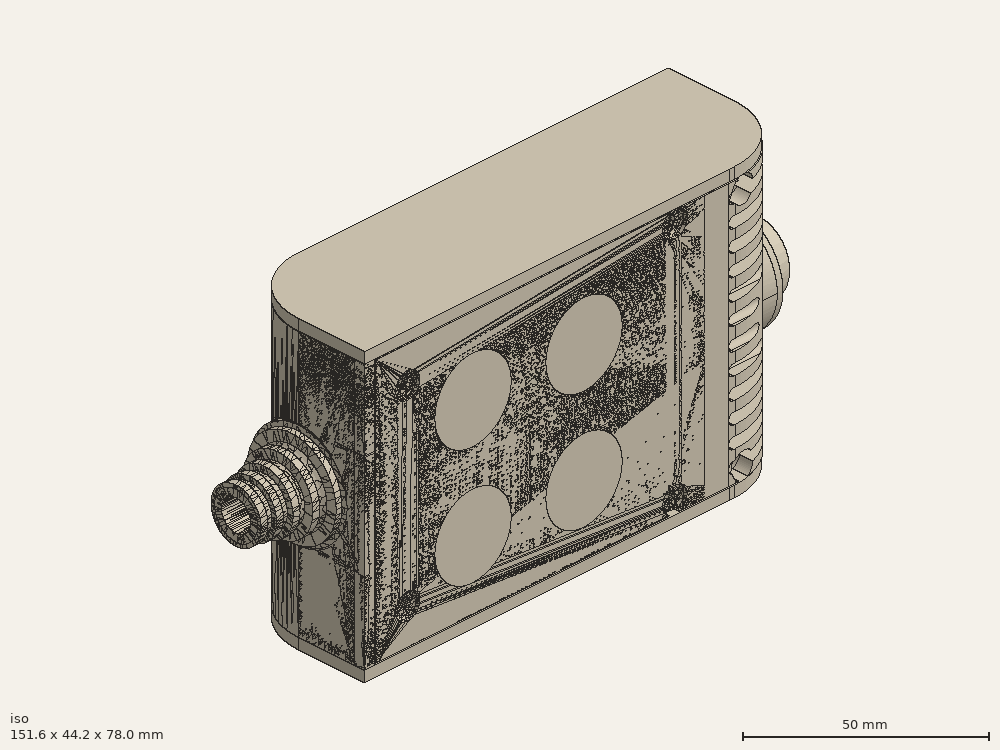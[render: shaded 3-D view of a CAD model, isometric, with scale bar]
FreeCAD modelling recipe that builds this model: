
FCSTD DOCUMENT  (FreeCAD 0.19R0.19.2)
Label: enclosure_183FCStd
License: All rights reserved
LicenseURL: http://en.wikipedia.org/wiki/All_rights_reserved
objects: Part::Revolution×152, Part::MultiFuse×146, Part::Feature×146, Sketcher::SketchObject×84, Part::Cut×70, Part::Cylinder×70, Part::Extrusion×67, Part::Fillet×58, Part::Box×36, App::MeasureDistance×4, PartDesign::Body×2, Image::ImagePlane×1
note: 831 computed .brp shape members not serialized (recipe doc carries the construction recipe); baked Part::Feature solids carry a one-line shape summary decoded from their .brp

FEATURE [Sketcher::SketchObject] Sketch  label="topSketch"
  FullyConstrained = true
  sketch-geometry (20):
    g0: LineSegment StartX=5.21097e-06 StartY=3 StartZ=0 EndX=5.21097e-06 EndY=19 EndZ=0
    g1: ArcOfCircle CenterX=19 CenterY=19 CenterZ=0 NormalX=0 NormalY=0 NormalZ=1 AngleXU=0 Radius=19 StartAngle=1.5708 EndAngle=3.14159
    g2: ArcOfCircle CenterX=19 CenterY=19 CenterZ=0 NormalX=0 NormalY=0 NormalZ=1 AngleXU=0 Radius=16 StartAngle=1.5708 EndAngle=3.14159
    g3: LineSegment StartX=114 StartY=35 StartZ=0 EndX=19 EndY=35 EndZ=0
    g4: LineSegment StartX=5.21097e-06 StartY=3 StartZ=0 EndX=5.21097e-06 EndY=0 EndZ=0
    g5: LineSegment StartX=3 StartY=0 StartZ=0 EndX=5.21097e-06 EndY=0 EndZ=0
    g6: LineSegment StartX=3 StartY=19 StartZ=0 EndX=3 EndY=0 EndZ=0
    g7: LineSegment StartX=19 StartY=38 StartZ=0 EndX=124 EndY=38 EndZ=0
    g8: Circle CenterX=119 CenterY=35 CenterZ=0 NormalX=0 NormalY=0 NormalZ=1 AngleXU=0 Radius=1
    g9: Circle CenterX=121 CenterY=35 CenterZ=0 NormalX=0 NormalY=0 NormalZ=1 AngleXU=0 Radius=1
    g10: Circle CenterX=121 CenterY=33 CenterZ=0 NormalX=0 NormalY=0 NormalZ=1 AngleXU=0 Radius=1
    g11: BSplineCurve PolesCount=3 KnotsCount=2 Degree=2 IsPeriodic=0
    g12: GeomPoint X=119 Y=35 Z=0
    g13: GeomPoint X=121 Y=33 Z=0
    g14: LineSegment StartX=119 StartY=35 StartZ=0 EndX=114 EndY=35 EndZ=0
    g15: ArcOfCircle CenterX=105 CenterY=19 CenterZ=0 NormalX=0 NormalY=0 NormalZ=1 AngleXU=0 Radius=19 StartAngle=5.7297 EndAngle=6.28319
    g16: ArcOfCircle CenterX=105 CenterY=19 CenterZ=0 NormalX=0 NormalY=0 NormalZ=1 AngleXU=0 Radius=16 StartAngle=5.60905 EndAngle=6.28319
    g17: LineSegment StartX=121 StartY=33 StartZ=0 EndX=121 EndY=19 EndZ=0
    g18: LineSegment StartX=124 StartY=38 StartZ=0 EndX=124 EndY=19 EndZ=0
    g19: LineSegment StartX=117.5 StartY=9.01251 StartZ=0 EndX=121.163 EndY=9.0125 EndZ=0
  constraints (46):
    c: Vertical(g0)
    c: Block(g0)
    c: Coincident(g1,g0)
    c: Block(g1)
    c: Coincident(g2,g1)
    c: Block(g2)
    c: Coincident(g3,g2)
    c: Horizontal(g3)
    c: Tangent(g3,g2)
    c: Coincident(g4,g0)
    c: Distance(g4) = 3
    c: Vertical(g4)
    c: Coincident(g5,g4)
    c: Horizontal(g5)
    c: Coincident(g6,g2)
    c: Coincident(g6,g5)
    c: Vertical(g6)
    c: Horizontal(g7)
    c: Distance(g7) = 105
    c: Coincident(g7,g1)
    c: Block(g3)
    c: Weight(g8) = 1
    c: Equal(g8,g9)
    c: Equal(g8,g10)
    c: InternalAlignment(g8,g11)
    c: InternalAlignment(g9,g11)
    c: InternalAlignment(g10,g11)
    c: InternalAlignment(g12,g11)
    c: InternalAlignment(g13,g11)
    c: Block(g11)
    c: Coincident(g14,g11)
    c: Coincident(g14,g3)
    c: Horizontal(g14)
    c: Block(g15)
    c: Coincident(g16,g15)
    c: Block(g16)
    c: Coincident(g17,g11)
    c: Coincident(g17,g16)
    c: Vertical(g17)
    c: Distance(g17) = 14
    c: Coincident(g18,g7)
    c: Coincident(g18,g15)
    c: Vertical(g18)
    c: Distance(g18) = 19
    c: Coincident(g19,g16)
    c: Coincident(g19,g15)
FEATURE [Sketcher::SketchObject] Sketch001  label="bottomSketch"
  FullyConstrained = true
  sketch-geometry (32):
    g0: LineSegment StartX=3.3 StartY=-6.03275e-07 StartZ=0 EndX=98 EndY=-6.03275e-07 EndZ=0
    g1: ArcOfCircle CenterX=98 CenterY=19 CenterZ=0 NormalX=0 NormalY=0 NormalZ=1 AngleXU=0 Radius=19 StartAngle=4.71239 EndAngle=5.71103
    g2: LineSegment StartX=6.3 StartY=8 StartZ=0 EndX=3.3 EndY=8 EndZ=0
    g3: LineSegment StartX=3.3 StartY=8 StartZ=0 EndX=3.3 EndY=-6.03275e-07 EndZ=0
    g4: ArcOfCircle CenterX=8.3 CenterY=5 CenterZ=0 NormalX=0 NormalY=0 NormalZ=1 AngleXU=0 Radius=2 StartAngle=3.14159 EndAngle=4.71239
    g5: LineSegment StartX=6.3 StartY=8 StartZ=0 EndX=6.3 EndY=5 EndZ=0
    g6: ArcOfCircle CenterX=98 CenterY=19 CenterZ=0 NormalX=0 NormalY=0 NormalZ=1 AngleXU=0 Radius=12.7 StartAngle=4.71239 EndAngle=6.28319
    g7: LineSegment StartX=94.7 StartY=3 StartZ=0 EndX=8.3 EndY=3 EndZ=0
    g8-g12: Circle x5 (B-spline internal-alignment scaffolding for g13; pole/knot coordinates omitted)
    g13: BSplineCurve PolesCount=5 KnotsCount=3 Degree=3 IsPeriodic=0
    g14: GeomPoint X=98 Y=6.3 Z=0
    g15: GeomPoint X=96.3938 Y=4.71946 Z=0
    g16: GeomPoint X=94.7 Y=3 Z=0
    g17-g23: Circle x7 (B-spline internal-alignment scaffolding for g24; pole/knot coordinates omitted)
    g24: BSplineCurve PolesCount=7 KnotsCount=5 Degree=3 IsPeriodic=0
    g25-g29: GeomPoint x5 (B-spline internal-alignment scaffolding for g24; pole/knot coordinates omitted)
    g30: ArcOfCircle CenterX=98 CenterY=19 CenterZ=0 NormalX=0 NormalY=0 NormalZ=1 AngleXU=0 Radius=15.7 StartAngle=5.81226 EndAngle=6.28319
    g31: LineSegment StartX=110.7 StartY=19 StartZ=0 EndX=113.7 EndY=19 EndZ=0
  constraints (41):
    c: Horizontal(g0)
    c: Coincident(g1,g0)
    c: Block(g1)
    c: Horizontal(g2)
    c: Distance(g2) = 3
    c: Coincident(g3,g2)
    c: Vertical(g3)
    c: Coincident(g3,g0)
    c: Block(g4)
    c: Block(g2)
    c: Coincident(g5,g2)
    c: Coincident(g5,g4)
    c: Vertical(g5)
    c: Coincident(g6,g1)
    c: Block(g6)
    c: Coincident(g7,g4)
    c: Horizontal(g7)
    c: Block(g0)
    c: Block(g7)
    c: Block(g3)
    c: Coincident(g13,g6)
    c: Weight(g8) = 1
    c: Equal(g8, g9-g12) x4
    c: Coincident(g13,g7)
    c: InternalAlignment(g8-g12 -> g13) x5
    c: InternalAlignment(g14,g13)
    c: InternalAlignment(g15,g13)
    c: InternalAlignment(g16,g13)
    c: Block(g13)
    c: Weight(g17) = 1
    c: Equal(g17, g18-g23) x6
    c: Coincident(g24,g1)
    c: InternalAlignment(g17-g23 -> g24) x7
    c: InternalAlignment(g25-g29 -> g24) x5
    c: Block(g24)
    c: Coincident(g30,g24)
    c: Coincident(g31,g6)
    c: Coincident(g31,g30)
    c: Horizontal(g31)
    c: Block(g31)
    c: Block(g30)
FEATURE [Part::Extrusion] Extrude  label="top"
  Base = -> Sketch
  Dir = (0,0,1)
  DirMode = 2
  FaceMakerClass = Part::FaceMakerBullseye
  LengthFwd = 72
  LengthRev = 0
  Solid = true
  Symmetric = false
FEATURE [Part::Extrusion] Extrude001  label="bottom"
  Base = -> Sketch001
  Dir = (0,0,1)
  DirMode = 2
  FaceMakerClass = Part::FaceMakerBullseye
  LengthFwd = 71.4
  LengthRev = 0
  Placement = pos=(0,0,0.3) rot=(0,0,1;0rad)
  Solid = true
  Symmetric = false
FEATURE [Sketcher::SketchObject] Sketch002  label="topSketch001"
  FullyConstrained = true
  sketch-geometry (8):
    g0: ArcOfCircle CenterX=19 CenterY=19.0975 CenterZ=0 NormalX=0 NormalY=0 NormalZ=1 AngleXU=0 Radius=18.9025 StartAngle=1.5708 EndAngle=3.14674
    g1: LineSegment StartX=0.0977805 StartY=19.0003 StartZ=0 EndX=0.0977805 EndY=0.000251602 EndZ=0
    g2: LineSegment StartX=19 StartY=38 StartZ=0 EndX=124 EndY=38 EndZ=0
    g3: LineSegment StartX=0.0977805 StartY=0.000251602 StartZ=0 EndX=105.098 EndY=0.000251602 EndZ=0
    g4: LineSegment StartX=124 StartY=38 StartZ=0 EndX=125.616 EndY=38 EndZ=0
    g5: LineSegment StartX=105.098 StartY=0.000251602 StartZ=0 EndX=106.713 EndY=0.000251602 EndZ=0
    g6: ArcOfCircle CenterX=106.616 CenterY=19 CenterZ=0 NormalX=0 NormalY=0 NormalZ=1 AngleXU=0 Radius=19 StartAngle=4.71754 EndAngle=6.28319
    g7: LineSegment StartX=125.616 StartY=38 StartZ=0 EndX=125.616 EndY=19 EndZ=0
  constraints (21):
    c: Block(g0)
    c: Coincident(g1,g0)
    c: Vertical(g1)
    c: Horizontal(g2)
    c: Distance(g2) = 105
    c: Coincident(g2,g0)
    c: Distance(g1) = 19
    c: Coincident(g3,g1)
    c: Horizontal(g3)
    c: Distance(g3) = 105
    c: Coincident(g4,g2)
    c: Horizontal(g4)
    c: Distance(g4) = 1.61553
    c: Horizontal(g5)
    c: Equal(g4,g5) = 1.61553
    c: Coincident(g5,g3)
    c: Block(g6)
    c: Coincident(g6,g5)
    c: Coincident(g7,g4)
    c: Coincident(g7,g6)
    c: Vertical(g7)
FEATURE [Part::Extrusion] Extrude002  label="sideA"
  Base = -> Sketch002
  Dir = (0,0,1)
  DirMode = 2
  FaceMakerClass = Part::FaceMakerBullseye
  LengthFwd = 3
  LengthRev = 0
  Placement = pos=(0,0,-3) rot=(0,0,1;0rad)
  Solid = true
  Symmetric = false
FEATURE [Sketcher::SketchObject] Sketch003  label="topSketch002"
  FullyConstrained = true
  sketch-geometry (6):
    g0: LineSegment StartX=19 StartY=38 StartZ=0 EndX=117 EndY=38 EndZ=0
    g1: ArcOfCircle CenterX=19 CenterY=19 CenterZ=0 NormalX=0 NormalY=0 NormalZ=1 AngleXU=0 Radius=19 StartAngle=1.5708 EndAngle=3.14159
    g2: LineSegment StartX=117 StartY=38 StartZ=0 EndX=117 EndY=19 EndZ=0
    g3: LineSegment StartX=98 StartY=1.0161e-12 StartZ=0 EndX=5.22862e-06 EndY=1.0161e-12 EndZ=0
    g4: LineSegment StartX=5.22862e-06 StartY=19 StartZ=0 EndX=5.22862e-06 EndY=1.0161e-12 EndZ=0
    g5: ArcOfCircle CenterX=98 CenterY=19 CenterZ=0 NormalX=0 NormalY=0 NormalZ=1 AngleXU=0 Radius=19 StartAngle=4.71239 EndAngle=6.28319
  constraints (16):
    c: Horizontal(g0)
    c: Distance(g0) = 98
    c: Coincident(g1,g0)
    c: Block(g1)
    c: Coincident(g2,g0)
    c: Vertical(g2)
    c: Distance(g2) = 19
    c: Horizontal(g3)
    c: Coincident(g4,g1)
    c: Vertical(g4)
    c: Coincident(g3,g4)
    c: Block(g3)
    c: Coincident(g5,g2)
    c: Coincident(g5,g3)
    c: Block(g0)
    c: Block(g5)
FEATURE [Sketcher::SketchObject] Sketch004
  FullyConstrained = true
  MapMode = 3
  Placement = pos=(0,0,0) rot=(1,0,0;1.5708rad)
  Support = -> [Extrude]
  sketch-geometry (8):
    g0: Circle CenterX=80.351 CenterY=-67.6202 CenterZ=0 NormalX=0 NormalY=0 NormalZ=1 AngleXU=0 Radius=2
    g1: Circle CenterX=80.351 CenterY=-67.6202 CenterZ=0 NormalX=0 NormalY=0 NormalZ=1 AngleXU=0 Radius=3
    g2: Circle CenterX=80.351 CenterY=-4.92017 CenterZ=0 NormalX=0 NormalY=0 NormalZ=1 AngleXU=0 Radius=2
    g3: Circle CenterX=80.351 CenterY=-4.92017 CenterZ=0 NormalX=0 NormalY=0 NormalZ=1 AngleXU=0 Radius=3
    g4: Circle CenterX=23.851 CenterY=-4.92017 CenterZ=0 NormalX=0 NormalY=0 NormalZ=1 AngleXU=0 Radius=2
    g5: Circle CenterX=23.851 CenterY=-4.92017 CenterZ=0 NormalX=0 NormalY=0 NormalZ=1 AngleXU=0 Radius=3
    g6: Circle CenterX=23.851 CenterY=-67.6202 CenterZ=0 NormalX=0 NormalY=0 NormalZ=1 AngleXU=0 Radius=2
    g7: Circle CenterX=23.851 CenterY=-67.6202 CenterZ=0 NormalX=0 NormalY=0 NormalZ=1 AngleXU=0 Radius=3
  constraints (8):
    c: Block(g3)
    c: Block(g2)
    c: Block(g1)
    c: Block(g0)
    c: Block(g6)
    c: Block(g7)
    c: Block(g4)
    c: Block(g5)
FEATURE [Part::Extrusion] Extrude004
  Base = -> Sketch004
  Dir = (0,-1,2e-16)
  DirMode = 2
  FaceMakerClass = Part::FaceMakerBullseye
  LengthFwd = 6
  LengthRev = 0
  Placement = pos=(0,9,0) rot=(0,0,1;0rad)
  Solid = true
  Symmetric = false
FEATURE [Sketcher::SketchObject] Sketch005
  FullyConstrained = true
  MapMode = 3
  Placement = pos=(0,0,0) rot=(1,0,0;1.5708rad)
  Support = -> [Extrude]
  sketch-geometry (8):
    g0: Circle CenterX=80.351 CenterY=-67.6202 CenterZ=0 NormalX=0 NormalY=0 NormalZ=1 AngleXU=0 Radius=3
    g1: Circle CenterX=80.351 CenterY=-4.92017 CenterZ=0 NormalX=0 NormalY=0 NormalZ=1 AngleXU=0 Radius=3
    g2: Circle CenterX=23.851 CenterY=-4.92017 CenterZ=0 NormalX=0 NormalY=0 NormalZ=1 AngleXU=0 Radius=3
    g3: Circle CenterX=23.851 CenterY=-67.6202 CenterZ=0 NormalX=0 NormalY=0 NormalZ=1 AngleXU=0 Radius=3
    g4: Circle CenterX=23.851 CenterY=-67.6202 CenterZ=0 NormalX=0 NormalY=0 NormalZ=1 AngleXU=0 Radius=5
    g5: Circle CenterX=80.351 CenterY=-67.6202 CenterZ=0 NormalX=0 NormalY=0 NormalZ=1 AngleXU=0 Radius=5
    g6: Circle CenterX=23.851 CenterY=-4.92017 CenterZ=0 NormalX=0 NormalY=0 NormalZ=1 AngleXU=0 Radius=5
    g7: Circle CenterX=80.351 CenterY=-4.92017 CenterZ=0 NormalX=0 NormalY=0 NormalZ=1 AngleXU=0 Radius=5
  constraints (8):
    c: Block(g1)
    c: Block(g0)
    c: Block(g3)
    c: Block(g2)
    c: Block(g5)
    c: Block(g4)
    c: Block(g6)
    c: Block(g7)
FEATURE [Part::Extrusion] Extrude005
  Base = -> Sketch005
  Dir = (0,-1,2e-16)
  DirMode = 2
  FaceMakerClass = Part::FaceMakerBullseye
  LengthFwd = 2
  LengthRev = 0
  Solid = true
  Symmetric = false
FEATURE [Sketcher::SketchObject] Sketch006
  FullyConstrained = true
  MapMode = 3
  Placement = pos=(0,0,0) rot=(1,0,0;1.5708rad)
  sketch-geometry (8):
    g0: Circle CenterX=80.351 CenterY=-67.6202 CenterZ=0 NormalX=0 NormalY=0 NormalZ=1 AngleXU=0 Radius=3
    g1: Circle CenterX=80.351 CenterY=-4.92017 CenterZ=0 NormalX=0 NormalY=0 NormalZ=1 AngleXU=0 Radius=3
    g2: Circle CenterX=23.851 CenterY=-4.92017 CenterZ=0 NormalX=0 NormalY=0 NormalZ=1 AngleXU=0 Radius=3
    g3: Circle CenterX=23.851 CenterY=-67.6202 CenterZ=0 NormalX=0 NormalY=0 NormalZ=1 AngleXU=0 Radius=3
    g4: Circle CenterX=23.851 CenterY=-67.6202 CenterZ=0 NormalX=0 NormalY=0 NormalZ=1 AngleXU=0 Radius=5
    g5: Circle CenterX=80.351 CenterY=-67.6202 CenterZ=0 NormalX=0 NormalY=0 NormalZ=1 AngleXU=0 Radius=5
    g6: Circle CenterX=23.851 CenterY=-4.92017 CenterZ=0 NormalX=0 NormalY=0 NormalZ=1 AngleXU=0 Radius=5
    g7: Circle CenterX=80.351 CenterY=-4.92017 CenterZ=0 NormalX=0 NormalY=0 NormalZ=1 AngleXU=0 Radius=5
  constraints (8):
    c: Block(g1)
    c: Block(g0)
    c: Block(g3)
    c: Block(g2)
    c: Block(g5)
    c: Block(g4)
    c: Block(g6)
    c: Block(g7)
FEATURE [Part::Extrusion] Extrude007
  Base = -> Sketch006
  Dir = (0,-1,2e-16)
  DirMode = 2
  FaceMakerClass = Part::FaceMakerBullseye
  LengthFwd = 2
  LengthRev = 0
  Solid = true
  Symmetric = false
FEATURE [Part::Fillet] Fillet
  Base = -> Extrude007
  Edges = 4 edges r=1.99: [Edge6,Edge12,Edge18,Edge24]
FEATURE [Part::Cut] Cut
  Base = -> Extrude005
  Placement = pos=(0,5,0) rot=(0,0,1;0rad)
  Tool = -> Fillet
FEATURE [Part::MultiFuse] Fusion  label="pCBScrews"
  Placement = pos=(-2.5,0,72.3) rot=(0,0,1;0rad)
  Shapes = -> [Extrude004,Cut]
FEATURE [App::MeasureDistance] Distance  label="Distance: 0.69 mm"
  Distance = 0.685967
  P1 = (24.0138,2.9647,0.3)
  P2 = (23.8901,3,-0.373787)
FEATURE [App::MeasureDistance] Distance001  label="Distance: 0.53 mm"
  Distance = 0.533607
  P1 = (80.2939,3,72.2334)
  P2 = (80.281,2.99661,71.7)
FEATURE [Part::Fillet] Fillet001
  Base = -> Extrude001
  Edges = 1 edges r=2.4: [Edge17]
FEATURE [Part::Fillet] Fillet002  label="bottom001"
  Base = -> Fillet001
  Edges = 1 edges r=2.4: [Edge36]
FEATURE [Part::Fillet] Fillet003  label="top001"
  Base = -> Extrude
  Edges = 1 edges r=2: [Edge1]
FEATURE [Sketcher::SketchObject] Sketch007
  FullyConstrained = true
  sketch-geometry (16):
    g0: LineSegment StartX=4 StartY=0 StartZ=0 EndX=4 EndY=2.4 EndZ=0
    g1: LineSegment StartX=4 StartY=2.4 StartZ=0 EndX=7 EndY=2.4 EndZ=0
    g2: LineSegment StartX=4 StartY=0 StartZ=0 EndX=5.7 EndY=0 EndZ=0
    g3: LineSegment StartX=5.7 StartY=0 StartZ=0 EndX=5.7 EndY=-5.6 EndZ=0
    g4-g8: Circle x5 (B-spline internal-alignment scaffolding for g9; pole/knot coordinates omitted)
    g9: BSplineCurve PolesCount=5 KnotsCount=3 Degree=3 IsPeriodic=0
    g10: GeomPoint X=7 Y=2.4 Z=0
    g11: GeomPoint X=10.4582 Y=-1.55472 Z=0
    g12: GeomPoint X=14 Y=-5.6 Z=0
    g13: LineSegment StartX=14 StartY=-5.6 StartZ=0 EndX=14 EndY=-14.1 EndZ=0
    g14: LineSegment StartX=14 StartY=-14.1 StartZ=0 EndX=6.5 EndY=-14.1 EndZ=0
    g15: LineSegment StartX=5.7 StartY=-5.6 StartZ=0 EndX=6.5 EndY=-14.1 EndZ=0
  constraints (28):
    c: Distance(g0) = 2.4
    c: Vertical(g0)
    c: Block(g0)
    c: Coincident(g1,g0)
    c: Horizontal(g1)
    c: Distance(g1) = 3
    c: Coincident(g2,g0)
    c: Horizontal(g2)
    c: Distance(g2) = 1.7
    c: Coincident(g3,g2)
    c: Vertical(g3)
    c: Distance(g3) = 5.6
    c: Coincident(g9,g1)
    c: Weight(g4) = 1
    c: Equal(g4, g5-g8) x4
    c: InternalAlignment(g4-g8 -> g9) x5
    c: InternalAlignment(g10,g9)
    c: InternalAlignment(g11,g9)
    c: InternalAlignment(g12,g9)
    c: Block(g9)
    c: Coincident(g13,g9)
    c: Vertical(g13)
    c: Distance(g13) = 8.5
    c: Coincident(g14,g13)
    c: Horizontal(g14)
    c: Distance(g14) = 7.5
    c: Coincident(g15,g3)
    c: Coincident(g15,g14)
FEATURE [Part::Feature] Face
  shape: bbox 10 x 16.5 x 2e-07 mm, 1 faces, 0 solids (baked)
FEATURE [Part::Revolution] Revolve  label="plugHousing"
  Angle = 360
  Axis = (0,1,0)
  Base = (0,0,0)
  FaceMakerClass = Part::FaceMakerBullseye
  Placement = pos=(0,0,36.15) rot=(0,0,1;0rad)
  Solid = false
  Source = -> Face
  Symmetric = false
FEATURE [Part::Feature] Face001
  shape: bbox 10 x 16.5 x 2e-07 mm, 1 faces, 0 solids (baked)
FEATURE [Part::Revolution] Revolve001  label="plugHousing001"
  Angle = 360
  Axis = (0,1,0)
  Base = (0,0,0)
  FaceMakerClass = Part::FaceMakerBullseye
  Placement = pos=(0,0,36.15) rot=(0,0,1;0rad)
  Solid = false
  Source = -> Face001
  Symmetric = false
FEATURE [Part::MultiFuse] Fusion001  label="plugHousing002"
  Placement = pos=(0,0,0) rot=(0,0,1;1.5708rad)
  Shapes = -> [Revolve001,Revolve]
FEATURE [Part::Feature] Face002
  shape: bbox 10 x 16.5 x 2e-07 mm, 1 faces, 0 solids (baked)
FEATURE [Part::Revolution] Revolve003  label="plugHousing005"
  Angle = 360
  Axis = (0,1,0)
  Base = (0,0,0)
  FaceMakerClass = Part::FaceMakerBullseye
  Placement = pos=(0,0,36.15) rot=(0,0,1;0rad)
  Solid = false
  Source = -> Face002
  Symmetric = false
FEATURE [Part::Feature] Face003
  shape: bbox 10 x 16.5 x 2e-07 mm, 1 faces, 0 solids (baked)
FEATURE [Part::Revolution] Revolve002  label="plugHousing003"
  Angle = 360
  Axis = (0,1,0)
  Base = (0,0,0)
  FaceMakerClass = Part::FaceMakerBullseye
  Placement = pos=(0,0,36.15) rot=(0,0,1;0rad)
  Solid = false
  Source = -> Face003
  Symmetric = false
FEATURE [Part::MultiFuse] Fusion002  label="plugHousing004"
  Placement = pos=(0,0,0) rot=(0,0,1;1.5708rad)
  Shapes = -> [Revolve002,Revolve003]
FEATURE [Part::MultiFuse] Fusion003  label="plugHousing006"
  Placement = pos=(0,19,0) rot=(0,0,1;3.14159rad)
  Shapes = -> [Fusion002,Fusion001]
FEATURE [Part::Feature] Face004
  shape: bbox 10 x 16.5 x 2e-07 mm, 1 faces, 0 solids (baked)
FEATURE [Part::Revolution] Revolve006  label="plugHousing010"
  Angle = 360
  Axis = (0,1,0)
  Base = (0,0,0)
  FaceMakerClass = Part::FaceMakerBullseye
  Placement = pos=(0,0,36.15) rot=(0,0,1;0rad)
  Solid = false
  Source = -> Face004
  Symmetric = false
FEATURE [Part::Feature] Face005
  shape: bbox 10 x 16.5 x 2e-07 mm, 1 faces, 0 solids (baked)
FEATURE [Part::Revolution] Revolve007  label="plugHousing011"
  Angle = 360
  Axis = (0,1,0)
  Base = (0,0,0)
  FaceMakerClass = Part::FaceMakerBullseye
  Placement = pos=(0,0,36.15) rot=(0,0,1;0rad)
  Solid = false
  Source = -> Face005
  Symmetric = false
FEATURE [Part::Feature] Face006
  shape: bbox 10 x 16.5 x 2e-07 mm, 1 faces, 0 solids (baked)
FEATURE [Part::Revolution] Revolve004  label="plugHousing007"
  Angle = 360
  Axis = (0,1,0)
  Base = (0,0,0)
  FaceMakerClass = Part::FaceMakerBullseye
  Placement = pos=(0,0,36.15) rot=(0,0,1;0rad)
  Solid = false
  Source = -> Face006
  Symmetric = false
FEATURE [Part::MultiFuse] Fusion004  label="plugHousing009"
  Placement = pos=(0,0,0) rot=(0,0,1;1.5708rad)
  Shapes = -> [Revolve004,Revolve007]
FEATURE [Part::Feature] Face007
  shape: bbox 10 x 16.5 x 2e-07 mm, 1 faces, 0 solids (baked)
FEATURE [Part::Revolution] Revolve005  label="plugHousing008"
  Angle = 360
  Axis = (0,1,0)
  Base = (0,0,0)
  FaceMakerClass = Part::FaceMakerBullseye
  Placement = pos=(0,0,36.15) rot=(0,0,1;0rad)
  Solid = false
  Source = -> Face007
  Symmetric = false
FEATURE [Part::MultiFuse] Fusion005  label="plugHousing012"
  Placement = pos=(0,0,0) rot=(0,0,1;1.5708rad)
  Shapes = -> [Revolve006,Revolve005]
FEATURE [Part::MultiFuse] Fusion006  label="plugHousing013"
  Placement = pos=(0,19,0) rot=(0,0,1;3.14159rad)
  Shapes = -> [Fusion005,Fusion004]
FEATURE [Part::MultiFuse] Fusion007  label="plugHousing014"
  Placement = pos=(122.621,0,-0.15) rot=(0,0,1;0rad)
  Shapes = -> [Fusion003,Fusion006]
FEATURE [Part::Cylinder] Cylinder002
  Angle = 360
  AttacherType = Attacher::AttachEngine3D
  Height = 20
  Placement = pos=(0,0,36.15) rot=(0,0,1;0rad)
  Radius = 4
FEATURE [Part::Cylinder] Cylinder003
  Angle = 360
  AttacherType = Attacher::AttachEngine3D
  Height = 10
  Placement = pos=(0,0,36.15) rot=(0,0,1;0rad)
  Radius = 4
FEATURE [Part::MultiFuse] Fusion009  label="removeToCreateHoleForPlugHousing"
  Placement = pos=(70,19,36.15) rot=(0,1,0;1.5708rad)
  Shapes = -> [Cylinder002,Cylinder003]
FEATURE [Part::Cylinder] Cylinder004
  Angle = 360
  AttacherType = Attacher::AttachEngine3D
  Height = 20
  Placement = pos=(0,0,36.15) rot=(0,0,1;0rad)
  Radius = 4
FEATURE [Part::Cylinder] Cylinder005
  Angle = 360
  AttacherType = Attacher::AttachEngine3D
  Height = 10
  Placement = pos=(0,0,36.15) rot=(0,0,1;0rad)
  Radius = 4
FEATURE [Part::MultiFuse] Fusion010  label="removeToCreateHoleForPlugHousing001"
  Placement = pos=(70,19,36.15) rot=(0,1,0;1.5708rad)
  Shapes = -> [Cylinder004,Cylinder005]
FEATURE [Part::Cut] Cut001
  Base = -> Fillet003
  Tool = -> Fusion010
FEATURE [Part::Cut] Cut002  label="Bottom"
  Base = -> Fillet002
  Tool = -> Fusion009
FEATURE [Part::Feature] Face008
  shape: bbox 10 x 16.5 x 2e-07 mm, 1 faces, 0 solids (baked)
FEATURE [Part::Revolution] Revolve011  label="plugHousing021"
  Angle = 360
  Axis = (0,1,0)
  Base = (0,0,0)
  FaceMakerClass = Part::FaceMakerBullseye
  Placement = pos=(0,0,36.15) rot=(0,0,1;0rad)
  Solid = false
  Source = -> Face008
  Symmetric = false
FEATURE [Part::Feature] Face009
  shape: bbox 10 x 16.5 x 2e-07 mm, 1 faces, 0 solids (baked)
FEATURE [Part::Revolution] Revolve012  label="plugHousing022"
  Angle = 360
  Axis = (0,1,0)
  Base = (0,0,0)
  FaceMakerClass = Part::FaceMakerBullseye
  Placement = pos=(0,0,36.15) rot=(0,0,1;0rad)
  Solid = false
  Source = -> Face009
  Symmetric = false
FEATURE [Part::Feature] Face010 .. Face013  x4 (patterned run collapsed; names and placements below)
  shape: bbox 10 x 16.5 x 2e-07 mm, 1 faces, 0 solids (baked)
FEATURE [Part::Revolution] Revolve015  label="plugHousing027"
  Angle = 360
  Axis = (0,1,0)
  Base = (0,0,0)
  FaceMakerClass = Part::FaceMakerBullseye
  Placement = pos=(0,0,36.15) rot=(0,0,1;0rad)
  Solid = false
  Source = -> Face013
  Symmetric = false
FEATURE [Part::Feature] Face014
  shape: bbox 10 x 16.5 x 2e-07 mm, 1 faces, 0 solids (baked)
FEATURE [Part::Feature] Face015
  shape: bbox 10 x 16.5 x 2e-07 mm, 1 faces, 0 solids (baked)
FEATURE [Part::Feature] Face016
  shape: bbox 10 x 16.5 x 2e-07 mm, 1 faces, 0 solids (baked)
FEATURE [Part::Revolution] Revolve019  label="plugHousing033"
  Angle = 360
  Axis = (0,1,0)
  Base = (0,0,0)
  FaceMakerClass = Part::FaceMakerBullseye
  Placement = pos=(0,0,36.15) rot=(0,0,1;0rad)
  Solid = false
  Source = -> Face016
  Symmetric = false
FEATURE [Part::Feature] Face017
  shape: bbox 10 x 16.5 x 2e-07 mm, 1 faces, 0 solids (baked)
FEATURE [Part::Revolution] Revolve020  label="plugHousing034"
  Angle = 360
  Axis = (0,1,0)
  Base = (0,0,0)
  FaceMakerClass = Part::FaceMakerBullseye
  Placement = pos=(0,0,36.15) rot=(0,0,1;0rad)
  Solid = false
  Source = -> Face017
  Symmetric = false
FEATURE [Part::Feature] Face018
  shape: bbox 10 x 16.5 x 2e-07 mm, 1 faces, 0 solids (baked)
FEATURE [Part::Revolution] Revolve016  label="plugHousing030"
  Angle = 360
  Axis = (0,1,0)
  Base = (0,0,0)
  FaceMakerClass = Part::FaceMakerBullseye
  Placement = pos=(0,0,36.15) rot=(0,0,1;0rad)
  Solid = false
  Source = -> Face018
  Symmetric = false
FEATURE [Part::MultiFuse] Fusion020  label="plugHousing038"
  Placement = pos=(0,0,0) rot=(0,0,1;1.5708rad)
  Shapes = -> [Revolve016,Revolve020]
FEATURE [Part::Feature] Face019
  shape: bbox 10 x 16.5 x 2e-07 mm, 1 faces, 0 solids (baked)
FEATURE [Part::Feature] Face020
  shape: bbox 10 x 16.5 x 2e-07 mm, 1 faces, 0 solids (baked)
FEATURE [Part::Revolution] Revolve017  label="plugHousing031"
  Angle = 360
  Axis = (0,1,0)
  Base = (0,0,0)
  FaceMakerClass = Part::FaceMakerBullseye
  Placement = pos=(0,0,36.15) rot=(0,0,1;0rad)
  Solid = false
  Source = -> Face020
  Symmetric = false
FEATURE [Part::MultiFuse] Fusion021  label="plugHousing039"
  Placement = pos=(0,0,0) rot=(0,0,1;1.5708rad)
  Shapes = -> [Revolve019,Revolve017]
FEATURE [Part::MultiFuse] Fusion023  label="plugHousing041"
  Placement = pos=(0,19,0) rot=(0,0,1;3.14159rad)
  Shapes = -> [Fusion021,Fusion020]
FEATURE [Part::Revolution] Revolve022  label="plugHousing043"
  Angle = 360
  Axis = (0,1,0)
  Base = (0,0,0)
  FaceMakerClass = Part::FaceMakerBullseye
  Placement = pos=(0,0,36.15) rot=(0,0,1;0rad)
  Solid = false
  Source = -> Face019
  Symmetric = false
FEATURE [Part::Feature] Face021
  shape: bbox 10 x 16.5 x 2e-07 mm, 1 faces, 0 solids (baked)
FEATURE [Part::Revolution] Revolve023  label="plugHousing044"
  Angle = 360
  Axis = (0,1,0)
  Base = (0,0,0)
  FaceMakerClass = Part::FaceMakerBullseye
  Placement = pos=(0,0,36.15) rot=(0,0,1;0rad)
  Solid = false
  Source = -> Face021
  Symmetric = false
FEATURE [Part::Feature] Face022
  shape: bbox 10 x 16.5 x 2e-07 mm, 1 faces, 0 solids (baked)
FEATURE [Part::Revolution] Revolve018  label="plugHousing032"
  Angle = 360
  Axis = (0,1,0)
  Base = (0,0,0)
  FaceMakerClass = Part::FaceMakerBullseye
  Placement = pos=(0,0,36.15) rot=(0,0,1;0rad)
  Solid = false
  Source = -> Face022
  Symmetric = false
FEATURE [Part::MultiFuse] Fusion022  label="plugHousing040"
  Placement = pos=(0,0,0) rot=(0,0,1;1.5708rad)
  Shapes = -> [Revolve018,Revolve023]
FEATURE [Part::Feature] Face023
  shape: bbox 10 x 16.5 x 2e-07 mm, 1 faces, 0 solids (baked)
FEATURE [Part::Revolution] Revolve021  label="plugHousing035"
  Angle = 360
  Axis = (0,1,0)
  Base = (0,0,0)
  FaceMakerClass = Part::FaceMakerBullseye
  Placement = pos=(0,0,36.15) rot=(0,0,1;0rad)
  Solid = false
  Source = -> Face023
  Symmetric = false
FEATURE [Part::MultiFuse] Fusion018  label="plugHousing036"
  Placement = pos=(0,0,0) rot=(0,0,1;1.5708rad)
  Shapes = -> [Revolve022,Revolve021]
FEATURE [Part::MultiFuse] Fusion019  label="plugHousing037"
  Placement = pos=(0,19,0) rot=(0,0,1;3.14159rad)
  Shapes = -> [Fusion018,Fusion022]
FEATURE [Part::MultiFuse] Fusion024  label="plugHousing042"
  Placement = pos=(122.621,0,-0.15) rot=(0,0,1;0rad)
  Shapes = -> [Fusion023,Fusion019]
FEATURE [Part::Cylinder] Cylinder006
  Angle = 360
  AttacherType = Attacher::AttachEngine3D
  Height = 20
  Placement = pos=(0,0,36.15) rot=(0,0,1;0rad)
  Radius = 14.3
FEATURE [Part::Cylinder] Cylinder007
  Angle = 360
  AttacherType = Attacher::AttachEngine3D
  Height = 10
  Placement = pos=(0,0,36.15) rot=(0,0,1;0rad)
  Radius = 4
FEATURE [Part::MultiFuse] Fusion026  label="removeToCreteHoleForPlugHousing"
  Placement = pos=(70,19,36) rot=(0,1,0;1.5708rad)
  Shapes = -> [Cylinder006,Cylinder007]
FEATURE [Part::Box] Box001  label="Cube001"
  AttacherType = Attacher::AttachEngine3D
  Height = 28
  Length = 3
  Placement = pos=(110.7,19,22) rot=(0,0,1;0rad)
  Width = 15.7
FEATURE [Part::Cut] Cut003  label="top002"
  Base = -> Cut001
  Tool = -> Fusion007
FEATURE [Part::Revolution] Revolve008  label="plugHousing015"
  Angle = 360
  Axis = (0,1,0)
  Base = (0,0,0)
  FaceMakerClass = Part::FaceMakerBullseye
  Placement = pos=(0,0,36.15) rot=(0,0,1;0rad)
  Solid = false
  Source = -> Face010
  Symmetric = false
FEATURE [Part::MultiFuse] Fusion013  label="plugHousing020"
  Placement = pos=(0,0,0) rot=(0,0,1;1.5708rad)
  Shapes = -> [Revolve008,Revolve012]
FEATURE [Part::Cut] Cut004  label="top003"
  Base = -> Cut003
  Placement = pos=(1,0,0) rot=(0,0,1;0rad)
  Tool = -> Fusion026
FEATURE [Part::Cylinder] Cylinder008
  Angle = 360
  AttacherType = Attacher::AttachEngine3D
  Height = 20
  Placement = pos=(0,0,36.15) rot=(0,0,1;0rad)
  Radius = 10.3
FEATURE [Part::Cylinder] Cylinder009
  Angle = 360
  AttacherType = Attacher::AttachEngine3D
  Height = 10
  Placement = pos=(0,0,36.15) rot=(0,0,1;0rad)
  Radius = 4
FEATURE [Part::MultiFuse] Fusion027  label="removeToCreteHoleForPlugHousing001"
  Placement = pos=(70,19,36) rot=(0,1,0;1.5708rad)
  Shapes = -> [Cylinder008,Cylinder009]
FEATURE [Part::Cut] Cut005  label="plugHousingTab"
  Base = -> Box001
  Tool = -> Fusion027
FEATURE [Part::MultiFuse] Fusion028  label="plugHousing045"
  Shapes = -> [Fusion024,Cut005]
FEATURE [Part::Box] Box002  label="Cube002"
  AttacherType = Attacher::AttachEngine3D
  Height = 28.8
  Length = 3
  Placement = pos=(107.3,28,21.6) rot=(0,0,1;0rad)
  Width = 7
FEATURE [Part::Box] Box003  label="Cube003"
  AttacherType = Attacher::AttachEngine3D
  Height = 3
  Length = 6.4
  Placement = pos=(107.3,28,18.6) rot=(0,0,1;0rad)
  Width = 7
FEATURE [Part::Box] Box004  label="Cube004"
  AttacherType = Attacher::AttachEngine3D
  Height = 3
  Length = 6.4
  Placement = pos=(107.3,28,50.4) rot=(0,0,1;0rad)
  Width = 7
FEATURE [Part::MultiFuse] Fusion029  label="plugHousingBracketHolder"
  Shapes = -> [Box004,Box002,Box003]
FEATURE [Part::Cylinder] Cylinder010
  Angle = 360
  AttacherType = Attacher::AttachEngine3D
  Height = 20
  Placement = pos=(0,0,36.15) rot=(0,0,1;0rad)
  Radius = 14.3
FEATURE [Part::Cylinder] Cylinder011
  Angle = 360
  AttacherType = Attacher::AttachEngine3D
  Height = 10
  Placement = pos=(0,0,36.15) rot=(0,0,1;0rad)
  Radius = 4
FEATURE [Part::MultiFuse] Fusion030  label="removeToCreteHoleForPlugHousing002"
  Placement = pos=(70,19,36) rot=(0,1,0;1.5708rad)
  Shapes = -> [Cylinder010,Cylinder011]
FEATURE [Part::Cut] Cut006  label="plugHousingBracketHolder001"
  Base = -> Fusion029
  Tool = -> Fusion030
FEATURE [Part::Cylinder] Cylinder012
  Angle = 360
  AttacherType = Attacher::AttachEngine3D
  Height = 20
  Placement = pos=(0,0,36.15) rot=(0,0,1;0rad)
  Radius = 7
FEATURE [Part::Cylinder] Cylinder013
  Angle = 360
  AttacherType = Attacher::AttachEngine3D
  Height = 10
  Placement = pos=(0,0,36.15) rot=(0,0,1;0rad)
  Radius = 4
FEATURE [Part::MultiFuse] Fusion032  label="removeToCreteHoleForPlugHousing003"
  Placement = pos=(70,19,36) rot=(0,1,0;1.5708rad)
  Shapes = -> [Cylinder012,Cylinder013]
FEATURE [Part::Cut] Cut007  label="bottom002"
  Base = -> Cut002
  Tool = -> Fusion032
FEATURE [Sketcher::SketchObject] Sketch008
  FullyConstrained = true
  sketch-geometry (54):
    g0: LineSegment StartX=-4.2 StartY=0 StartZ=0 EndX=-6.2 EndY=0 EndZ=0
    g1: LineSegment StartX=-14 StartY=-18 StartZ=0 EndX=-14 EndY=-26.5 EndZ=0
    g2: LineSegment StartX=-4.2 StartY=0 StartZ=0 EndX=-4.2 EndY=-13.4877 EndZ=0
    g3: Circle CenterX=-4.2 CenterY=-13.4877 CenterZ=0 NormalX=0 NormalY=0 NormalZ=1 AngleXU=0 Radius=1
    g4: Circle CenterX=-4.2 CenterY=-26.5 CenterZ=0 NormalX=0 NormalY=0 NormalZ=1 AngleXU=0 Radius=1
    g5: Circle CenterX=-8.2 CenterY=-26.5 CenterZ=0 NormalX=0 NormalY=0 NormalZ=1 AngleXU=0 Radius=1
    g6: BSplineCurve PolesCount=3 KnotsCount=2 Degree=2 IsPeriodic=0
    g7: GeomPoint X=-4.2 Y=-13.4877 Z=0
    g8: GeomPoint X=-8.2 Y=-26.5 Z=0
    g9: LineSegment StartX=-14 StartY=-26.5 StartZ=0 EndX=-8.2 EndY=-26.5 EndZ=0
    g10: LineSegment StartX=-10.15 StartY=-12 StartZ=0 EndX=-10.15 EndY=-14 EndZ=0
    g11: LineSegment StartX=-12.8401 StartY=-16 StartZ=0 EndX=-10.1571 EndY=-16 EndZ=0
    g12: LineSegment StartX=-10.15 StartY=-14 StartZ=0 EndX=-8.70761 EndY=-14 EndZ=0
    g13: LineSegment StartX=-12.8401 StartY=-16 StartZ=0 EndX=-12.8401 EndY=-17.6958 EndZ=0
    g14: LineSegment StartX=-10.15 StartY=-12 StartZ=0 EndX=-7.79258 EndY=-12 EndZ=0
    g15: Circle CenterX=-6.2215 CenterY=-2 CenterZ=0 NormalX=0 NormalY=0 NormalZ=1 AngleXU=0 Radius=1
    g16: Circle CenterX=-6.22762 CenterY=-2.58724 CenterZ=0 NormalX=0 NormalY=0 NormalZ=1 AngleXU=0 Radius=1
    g17: Circle CenterX=-6.32538 CenterY=-4 CenterZ=0 NormalX=0 NormalY=0 NormalZ=1 AngleXU=0 Radius=1
    g18: BSplineCurve PolesCount=3 KnotsCount=2 Degree=2 IsPeriodic=0
    g19: GeomPoint X=-6.2215 Y=-2 Z=0
    g20: GeomPoint X=-6.32538 Y=-4 Z=0
    g21: Circle CenterX=-6.48644 CenterY=-5.99526 CenterZ=0 NormalX=0 NormalY=0 NormalZ=1 AngleXU=0 Radius=1
    g22: Circle CenterX=-6.58486 CenterY=-6.99526 CenterZ=0 NormalX=0 NormalY=0 NormalZ=1 AngleXU=0 Radius=1
    g23: Circle CenterX=-6.77343 CenterY=-8 CenterZ=0 NormalX=0 NormalY=0 NormalZ=1 AngleXU=0 Radius=1
    g24: BSplineCurve PolesCount=3 KnotsCount=2 Degree=2 IsPeriodic=0
    g25: GeomPoint X=-6.48644 Y=-5.99526 Z=0
    g26: GeomPoint X=-6.77343 Y=-8 Z=0
    g27: Circle CenterX=-7.19003 CenterY=-10 CenterZ=0 NormalX=0 NormalY=0 NormalZ=1 AngleXU=0 Radius=1
    g28: Circle CenterX=-7.44407 CenterY=-11.0915 CenterZ=0 NormalX=0 NormalY=0 NormalZ=1 AngleXU=0 Radius=1
    g29: Circle CenterX=-7.79258 CenterY=-12 CenterZ=0 NormalX=0 NormalY=0 NormalZ=1 AngleXU=0 Radius=1
    g30: BSplineCurve PolesCount=3 KnotsCount=2 Degree=2 IsPeriodic=0
    g31: GeomPoint X=-7.19003 Y=-10 Z=0
    g32: GeomPoint X=-7.79258 Y=-12 Z=0
    g33: Circle CenterX=-8.70761 CenterY=-14 CenterZ=0 NormalX=0 NormalY=0 NormalZ=1 AngleXU=0 Radius=1
    g34: Circle CenterX=-9.33087 CenterY=-15.1837 CenterZ=0 NormalX=0 NormalY=0 NormalZ=1 AngleXU=0 Radius=1
    g35: Circle CenterX=-10.1571 CenterY=-16 CenterZ=0 NormalX=0 NormalY=0 NormalZ=1 AngleXU=0 Radius=1
    g36: BSplineCurve PolesCount=3 KnotsCount=2 Degree=2 IsPeriodic=0
    g37: GeomPoint X=-8.70761 Y=-14 Z=0
    g38: GeomPoint X=-10.1571 Y=-16 Z=0
    g39: Circle CenterX=-12.8401 CenterY=-17.6958 CenterZ=0 NormalX=0 NormalY=0 NormalZ=1 AngleXU=0 Radius=1
    g40: Circle CenterX=-13.3521 CenterY=-17.9027 CenterZ=0 NormalX=0 NormalY=0 NormalZ=1 AngleXU=0 Radius=1
    g41: Circle CenterX=-14 CenterY=-18 CenterZ=0 NormalX=0 NormalY=0 NormalZ=1 AngleXU=0 Radius=1
    g42: BSplineCurve PolesCount=3 KnotsCount=2 Degree=2 IsPeriodic=0
    g43: GeomPoint X=-12.8401 Y=-17.6958 Z=0
    g44: GeomPoint X=-14 Y=-18 Z=0
    g45: LineSegment StartX=-6.2 StartY=0 StartZ=0 EndX=-7.2 EndY=0 EndZ=0
    g46: LineSegment StartX=-7.2 StartY=0 StartZ=0 EndX=-7.2 EndY=-2 EndZ=0
    g47: LineSegment StartX=-7.2 StartY=-2 StartZ=0 EndX=-6.2215 EndY=-2 EndZ=0
    g48: LineSegment StartX=-6.32538 StartY=-4 StartZ=0 EndX=-7.65538 EndY=-4 EndZ=0
    g49: LineSegment StartX=-7.65538 StartY=-4 StartZ=0 EndX=-7.65538 EndY=-5.99526 EndZ=0
    g50: LineSegment StartX=-7.65538 StartY=-5.99526 StartZ=0 EndX=-6.48644 EndY=-5.99526 EndZ=0
    g51: LineSegment StartX=-6.77343 StartY=-8 StartZ=0 EndX=-8.43343 EndY=-8 EndZ=0
    g52: LineSegment StartX=-8.43343 StartY=-8 StartZ=0 EndX=-8.43343 EndY=-10 EndZ=0
    g53: LineSegment StartX=-8.43343 StartY=-10 StartZ=0 EndX=-7.19003 EndY=-10 EndZ=0
  constraints (112):
    c: Horizontal(g0)
    c: Distance(g0) = 2
    c: Block(g0)
    c: Vertical(g1)
    c: Coincident(g2,g0)
    c: Vertical(g2)
    c: Block(g2)
    c: Coincident(g6,g2)
    c: Weight(g3) = 1
    c: Equal(g3,g4)
    c: Equal(g3,g5)
    c: InternalAlignment(g3,g6)
    c: InternalAlignment(g4,g6)
    c: InternalAlignment(g5,g6)
    c: InternalAlignment(g7,g6)
    c: InternalAlignment(g8,g6)
    c: Block(g6)
    c: Coincident(g9,g1)
    c: Coincident(g9,g6)
    c: Horizontal(g9)
    c: Vertical(g10)
    c: Block(g10)
    c: Horizontal(g11)
    c: Block(g11)
    c: Coincident(g12,g10)
    c: Horizontal(g12)
    c: Block(g12)
    c: Coincident(g13,g11)
    c: Vertical(g13)
    c: Block(g13)
    c: Coincident(g14,g10)
    c: Horizontal(g14)
    c: Block(g14)
    c: Block(g9)
    c: Block(g1)
    c: Weight(g15) = 1
    c: Equal(g15,g16)
    c: Equal(g15,g17)
    c: InternalAlignment(g15,g18)
    c: InternalAlignment(g16,g18)
    c: InternalAlignment(g17,g18)
    c: InternalAlignment(g19,g18)
    c: InternalAlignment(g20,g18)
    c: Weight(g21) = 1
    c: Equal(g21,g22)
    c: Equal(g21,g23)
    c: InternalAlignment(g21,g24)
    c: InternalAlignment(g22,g24)
    c: InternalAlignment(g23,g24)
    c: InternalAlignment(g25,g24)
    c: InternalAlignment(g26,g24)
    c: Weight(g27) = 1
    c: Equal(g27,g28)
    c: Equal(g27,g29)
    c: Coincident(g30,g14)
    c: InternalAlignment(g27,g30)
    c: InternalAlignment(g28,g30)
    c: InternalAlignment(g29,g30)
    c: InternalAlignment(g31,g30)
    c: InternalAlignment(g32,g30)
    c: Coincident(g36,g12)
    c: Weight(g33) = 1
    c: Equal(g33,g34)
    c: Equal(g33,g35)
    c: Coincident(g36,g11)
    c: InternalAlignment(g33,g36)
    c: InternalAlignment(g34,g36)
    c: InternalAlignment(g35,g36)
    c: InternalAlignment(g37,g36)
    c: InternalAlignment(g38,g36)
    c: Coincident(g42,g13)
    c: Weight(g39) = 1
    c: Equal(g39,g40)
    c: Equal(g39,g41)
    c: Coincident(g42,g1)
    c: InternalAlignment(g39,g42)
    c: InternalAlignment(g40,g42)
    c: InternalAlignment(g41,g42)
    c: InternalAlignment(g43,g42)
    c: InternalAlignment(g44,g42)
    c: Block(g18)
    c: Block(g24)
    c: Block(g30)
    c: Block(g36)
    c: Block(g42)
    c: Horizontal(g45)
    c: Coincident(g45,g0)
    c: Vertical(g46)
    c: Coincident(g46,g45)
    c: Coincident(g47,g46)
    c: Coincident(g47,g18)
    c: Horizontal(g47)
    c: Block(g46)
    c: Coincident(g48,g18)
    c: Horizontal(g48)
    c: Distance(g48) = 1.33
    c: Vertical(g49)
    c: Coincident(g49,g48)
    c: Coincident(g50,g49)
    c: Coincident(g50,g24)
    c: Horizontal(g50)
    c: Tangent(g50,g22)
    c: Horizontal(g51)
    c: Coincident(g51,g24)
    c: Block(g51)
    c: Vertical(g52)
    c: Block(g52)
    c: Coincident(g52,g51)
    c: Coincident(g53,g52)
    c: Coincident(g53,g30)
    c: Horizontal(g53)
    c: Distance(g1) = 8.5
FEATURE [Part::Feature] Face024
  shape: bbox 9.8 x 26.5 x 2e-07 mm, 1 faces, 0 solids (baked)
FEATURE [Part::Revolution] Revolve024
  Angle = 360
  Axis = (0,1,0)
  Base = (0,0,0)
  FaceMakerClass = Part::FaceMakerBullseye
  Placement = pos=(0,0,0) rot=(0,0,1;1.5708rad)
  Solid = false
  Source = -> Face024
  Symmetric = false
FEATURE [Part::Feature] Face025
  shape: bbox 9.8 x 26.5 x 2e-07 mm, 1 faces, 0 solids (baked)
FEATURE [Part::Revolution] Revolve025
  Angle = 360
  Axis = (0,1,0)
  Base = (0,0,0)
  FaceMakerClass = Part::FaceMakerBullseye
  Placement = pos=(0,0,0) rot=(0,0,1;1.5708rad)
  Solid = false
  Source = -> Face025
  Symmetric = false
FEATURE [Part::MultiFuse] Fusion033
  Placement = pos=(-18,19,36) rot=(0,0,1;0rad)
  Shapes = -> [Revolve025,Revolve024]
FEATURE [Part::Cylinder] Cylinder014
  Angle = 360
  AttacherType = Attacher::AttachEngine3D
  Height = 20
  Placement = pos=(0,0,36.15) rot=(0,0,1;0rad)
  Radius = 14.3
FEATURE [Part::Cylinder] Cylinder015
  Angle = 360
  AttacherType = Attacher::AttachEngine3D
  Height = 10
  Placement = pos=(0,0,36.15) rot=(0,0,1;0rad)
  Radius = 4
FEATURE [Part::MultiFuse] Fusion034  label="removeToCreteHoleForPlugHousing004"
  Placement = pos=(-42,19,36) rot=(0,1,0;1.5708rad)
  Shapes = -> [Cylinder014,Cylinder015]
FEATURE [Part::Cut] Cut008  label="top004"
  Base = -> Cut004
  Placement = pos=(-1,0,0) rot=(0,0,1;0rad)
  Tool = -> Fusion034
FEATURE [Part::Box] Box005  label="Cube005"
  AttacherType = Attacher::AttachEngine3D
  Height = 28
  Length = 3
  Placement = pos=(110.7,19,22) rot=(0,0,1;0rad)
  Width = 15.7
FEATURE [Part::Cylinder] Cylinder016
  Angle = 360
  AttacherType = Attacher::AttachEngine3D
  Height = 10
  Placement = pos=(0,0,36.15) rot=(0,0,1;0rad)
  Radius = 4
FEATURE [Part::Cylinder] Cylinder017
  Angle = 360
  AttacherType = Attacher::AttachEngine3D
  Height = 20
  Placement = pos=(0,0,36.15) rot=(0,0,1;0rad)
  Radius = 10.3
FEATURE [Part::MultiFuse] Fusion035  label="removeToCreteHoleForPlugHousing005"
  Placement = pos=(70,19,36) rot=(0,1,0;1.5708rad)
  Shapes = -> [Cylinder017,Cylinder016]
FEATURE [Part::Cut] Cut009  label="plugHousingTab001"
  Base = -> Box005
  Placement = pos=(-107.4,-14,0) rot=(0,0,1;0rad)
  Tool = -> Fusion035
FEATURE [Part::Box] Box006  label="Cube006"
  AttacherType = Attacher::AttachEngine3D
  Height = 28
  Length = 3
  Placement = pos=(110.7,19,22) rot=(0,0,1;0rad)
  Width = 15.7
FEATURE [Part::Cylinder] Cylinder018
  Angle = 360
  AttacherType = Attacher::AttachEngine3D
  Height = 10
  Placement = pos=(0,0,36.15) rot=(0,0,1;0rad)
  Radius = 4
FEATURE [Part::Cylinder] Cylinder019
  Angle = 360
  AttacherType = Attacher::AttachEngine3D
  Height = 20
  Placement = pos=(0,0,36.15) rot=(0,0,1;0rad)
  Radius = 10.3
FEATURE [Part::MultiFuse] Fusion036  label="removeToCreteHoleForPlugHousing006"
  Placement = pos=(70,19,36) rot=(0,1,0;1.5708rad)
  Shapes = -> [Cylinder019,Cylinder018]
FEATURE [Part::Cut] Cut010  label="plugHousingTab002"
  Base = -> Box006
  Placement = pos=(-107.4,-14,0) rot=(0,0,1;0rad)
  Tool = -> Fusion036
FEATURE [Part::MultiFuse] Fusion037
  Placement = pos=(9.6,23,0) rot=(0,0,1;3.14159rad)
  Shapes = -> [Cut009,Cut010]
FEATURE [Part::Box] Box  label="Cube"
  AttacherType = Attacher::AttachEngine3D
  Height = 10
  Length = 3
  Placement = pos=(3.3,4,12) rot=(0,0,1;0rad)
  Width = 10
FEATURE [Part::Fillet] Fillet004
  Base = -> Fusion028
  Edges = 1 edges r=2: [Edge25]
FEATURE [Part::Fillet] Fillet005  label="plugHousing046"
  Base = -> Fillet004
  Edges = 1 edges r=2: [Edge8]
FEATURE [Part::Fillet] Fillet006
  Base = -> Box
  Edges = 1 edges r=2: [Edge11]
FEATURE [Part::Box] Box007  label="Cube007"
  AttacherType = Attacher::AttachEngine3D
  Height = 10
  Length = 3
  Placement = pos=(3.3,4,50) rot=(0,0,1;0rad)
  Width = 10
FEATURE [Part::Fillet] Fillet007
  Base = -> Box007
  Edges = 1 edges r=2: [Edge12]
FEATURE [Part::Box] Box008  label="Cube008"
  AttacherType = Attacher::AttachEngine3D
  Height = 28
  Length = 4
  Placement = pos=(5,0,22) rot=(0,0,1;0rad)
  Width = 10
FEATURE [Part::Fillet] Fillet008
  Base = -> Box008
  Edges = 1 edges r=1: [Edge7]
FEATURE [Part::Fillet] Fillet009
  Base = -> Fillet008
  Edges = 1 edges r=2: [Edge5]
FEATURE [Part::Fillet] Fillet010
  Base = -> Fillet009
  Edges = 1 edges r=2: [Edge2]
FEATURE [Sketcher::SketchObject] Sketch009  label="topSketch003"
  FullyConstrained = true
  sketch-geometry (4):
    g0: LineSegment StartX=16.8446 StartY=31.512 StartZ=0 EndX=16.3251 EndY=34.4666 EndZ=0
    g1: ArcOfCircle CenterX=19 CenterY=19.2524 CenterZ=0 NormalX=0 NormalY=0 NormalZ=1 AngleXU=0 Radius=15.4476 StartAngle=1.74483 EndAngle=2.72717
    g2: ArcOfCircle CenterX=19 CenterY=19.2524 CenterZ=0 NormalX=0 NormalY=0 NormalZ=1 AngleXU=0 Radius=12.4476 StartAngle=1.74483 EndAngle=2.73189
    g3: LineSegment StartX=4.86004 StartY=25.4725 StartZ=0 EndX=7.58253 EndY=24.2107 EndZ=0
  constraints (7):
    c: Block(g0)
    c: Coincident(g1,g0)
    c: Coincident(g2,g0)
    c: Coincident(g3,g1)
    c: Coincident(g3,g2)
    c: Block(g1)
    c: Block(g2)
FEATURE [Part::Extrusion] Extrude008
  Base = -> Sketch009
  Dir = (0,0,1)
  DirMode = 2
  FaceMakerClass = Part::FaceMakerBullseye
  LengthFwd = 10
  LengthRev = 0
  Placement = pos=(0,0,31) rot=(0,0,1;0rad)
  Solid = true
  Symmetric = false
FEATURE [Part::Cylinder] Cylinder020
  Angle = 360
  AttacherType = Attacher::AttachEngine3D
  Height = 20
  Placement = pos=(0,0,36.15) rot=(0,0,1;0rad)
  Radius = 8.2
FEATURE [Part::Cylinder] Cylinder021
  Angle = 360
  AttacherType = Attacher::AttachEngine3D
  Height = 10
  Placement = pos=(0,0,36.15) rot=(0,0,1;0rad)
  Radius = 4
FEATURE [Part::MultiFuse] Fusion038  label="removeToCreteHoleForPlugHousing007"
  Placement = pos=(-42,19,36) rot=(0,1,0;1.5708rad)
  Shapes = -> [Cylinder020,Cylinder021]
FEATURE [Part::Cut] Cut011
  Base = -> Extrude008
  Tool = -> Fusion038
FEATURE [Part::Fillet] Fillet011
  Base = -> Cut011
  Edges = 1 edges r=2: [Edge1]
FEATURE [Part::Fillet] Fillet012
  Base = -> Fillet011
  Edges = 1 edges r=2.5: [Edge1]
FEATURE [Part::Fillet] Fillet013
  Base = -> Fillet012
  Edges = 1 edges r=2.5: [Edge2]
FEATURE [Part::Box] Box010  label="Cube010"
  AttacherType = Attacher::AttachEngine3D
  Height = 16
  Length = 8
  Placement = pos=(12.7,31.52,28) rot=(0,0,1;0rad)
  Width = 4
FEATURE [Sketcher::SketchObject] Sketch010  label="topSketch004"
  FullyConstrained = true
  sketch-geometry (4):
    g0: LineSegment StartX=16.8446 StartY=31.512 StartZ=0 EndX=16.3251 EndY=34.4666 EndZ=0
    g1: ArcOfCircle CenterX=19 CenterY=19.2524 CenterZ=0 NormalX=0 NormalY=0 NormalZ=1 AngleXU=0 Radius=15.4476 StartAngle=1.74483 EndAngle=2.72717
    g2: ArcOfCircle CenterX=19 CenterY=19.2524 CenterZ=0 NormalX=0 NormalY=0 NormalZ=1 AngleXU=0 Radius=12.4476 StartAngle=1.74483 EndAngle=2.73189
    g3: LineSegment StartX=4.86004 StartY=25.4725 StartZ=0 EndX=7.58253 EndY=24.2107 EndZ=0
  constraints (7):
    c: Block(g0)
    c: Coincident(g1,g0)
    c: Coincident(g2,g0)
    c: Coincident(g3,g1)
    c: Coincident(g3,g2)
    c: Block(g1)
    c: Block(g2)
FEATURE [Part::Cylinder] Cylinder022
  Angle = 360
  AttacherType = Attacher::AttachEngine3D
  Height = 10
  Placement = pos=(0,0,36.15) rot=(0,0,1;0rad)
  Radius = 4
FEATURE [Sketcher::SketchObject] Sketch011  label="topSketch005"
  FullyConstrained = true
  sketch-geometry (4):
    g0: LineSegment StartX=16.8446 StartY=31.512 StartZ=0 EndX=16.3251 EndY=34.4666 EndZ=0
    g1: ArcOfCircle CenterX=19 CenterY=19.2524 CenterZ=0 NormalX=0 NormalY=0 NormalZ=1 AngleXU=0 Radius=15.4476 StartAngle=1.74483 EndAngle=2.72717
    g2: ArcOfCircle CenterX=19 CenterY=19.2524 CenterZ=0 NormalX=0 NormalY=0 NormalZ=1 AngleXU=0 Radius=12.4476 StartAngle=1.74483 EndAngle=2.73189
    g3: LineSegment StartX=4.86004 StartY=25.4725 StartZ=0 EndX=7.58253 EndY=24.2107 EndZ=0
  constraints (7):
    c: Block(g0)
    c: Coincident(g1,g0)
    c: Coincident(g2,g0)
    c: Coincident(g3,g1)
    c: Coincident(g3,g2)
    c: Block(g1)
    c: Block(g2)
FEATURE [Part::Extrusion] Extrude010
  Base = -> Sketch011
  Dir = (0,0,1)
  DirMode = 2
  FaceMakerClass = Part::FaceMakerBullseye
  LengthFwd = 10.6
  LengthRev = 0
  Placement = pos=(0,0,31) rot=(0,0,1;0rad)
  Solid = true
  Symmetric = false
FEATURE [Part::Cylinder] Cylinder023
  Angle = 360
  AttacherType = Attacher::AttachEngine3D
  Height = 20
  Placement = pos=(0,0,36.15) rot=(0,0,1;0rad)
  Radius = 8.2
FEATURE [Part::MultiFuse] Fusion039  label="removeToCreteHoleForPlugHousing008"
  Placement = pos=(-42,19,36) rot=(0,1,0;1.5708rad)
  Shapes = -> [Cylinder023,Cylinder022]
FEATURE [Part::Cut] Cut012
  Base = -> Extrude010
  Placement = pos=(0,0,-0.3) rot=(0,0,1;0rad)
  Tool = -> Fusion039
FEATURE [Part::Cut] Cut013
  Base = -> Box010
  Tool = -> Cut012
FEATURE [Part::Fillet] Fillet014
  Base = -> Cut013
  Edges = 1 edges r=0.7: [Edge13]
FEATURE [Part::Fillet] Fillet015
  Base = -> Fillet014
  Edges = 1 edges r=0.7: [Edge13]
FEATURE [Part::Fillet] Fillet016
  Base = -> Fillet015
  Edges = 1 edges r=0.7: [Edge16]
FEATURE [Part::Fillet] Fillet017
  Base = -> Fillet016
  Edges = 1 edges r=0.7: [Edge11]
FEATURE [Part::Fillet] Fillet018
  Base = -> Fillet017
  Edges = 1 edges r=0.7: [Edge10]
FEATURE [Part::Fillet] Fillet019
  Base = -> Fillet018
  Edges = 1 edges r=1.2: [Edge5]
FEATURE [Part::Fillet] Fillet020
  Base = -> Fillet019
  Edges = 1 edges r=1.2: [Edge12]
FEATURE [Part::Fillet] Fillet021
  Base = -> Fillet020
  Edges = 1 edges r=2: [Edge1]
  Placement = pos=(0.3,0,0) rot=(0,0,1;0rad)
FEATURE [Part::MultiFuse] Fusion040  label="top005"
  Shapes = -> [Cut008,Fillet021]
FEATURE [Part::MultiFuse] Fusion041  label="wireHolder"
  Shapes = -> [Fusion033,Fillet013]
FEATURE [Part::MultiFuse] Fusion042
  Shapes = -> [Fillet007,Fusion041]
FEATURE [Part::MultiFuse] Fusion043  label="wireHolder001"
  Shapes = -> [Fusion042,Fillet010]
FEATURE [Part::MultiFuse] Fusion044  label="wireHolder002"
  Shapes = -> [Fillet006,Fusion037,Fusion043]
FEATURE [Part::Feature] Face026
  shape: bbox 11 x 6 x 2e-07 mm, 1 faces, 0 solids (baked)
FEATURE [Part::Revolution] Revolve026
  Angle = 360
  Axis = (0,1,0)
  Base = (0,0,0)
  FaceMakerClass = Part::FaceMakerBullseye
  Placement = pos=(30.3,-1,19.7) rot=(0,0,1;0rad)
  Solid = false
  Source = -> Face026
  Symmetric = false
FEATURE [Sketcher::SketchObject] Sketch013  label="topSketch006"
  FullyConstrained = true
  sketch-geometry (13):
    g0: LineSegment StartX=117 StartY=19 StartZ=0 EndX=117 EndY=38 EndZ=0
    g1: ArcOfCircle CenterX=98 CenterY=19 CenterZ=0 NormalX=0 NormalY=0 NormalZ=1 AngleXU=0 Radius=19 StartAngle=5.7297 EndAngle=6.28319
    g2: LineSegment StartX=0 StartY=3 StartZ=0 EndX=0 EndY=19 EndZ=0
    g3: LineSegment StartX=19 StartY=38 StartZ=0 EndX=117 EndY=38 EndZ=0
    g4: ArcOfCircle CenterX=19 CenterY=19 CenterZ=0 NormalX=0 NormalY=0 NormalZ=1 AngleXU=0 Radius=19 StartAngle=1.5708 EndAngle=3.14159
    g5: ArcOfCircle CenterX=19 CenterY=19 CenterZ=0 NormalX=0 NormalY=0 NormalZ=1 AngleXU=0 Radius=16 StartAngle=1.5708 EndAngle=3.14159
    g6: ArcOfCircle CenterX=98 CenterY=19 CenterZ=0 NormalX=0 NormalY=0 NormalZ=1 AngleXU=0 Radius=16 StartAngle=5.60905 EndAngle=6.28319
    g7: LineSegment StartX=114 StartY=19 StartZ=0 EndX=114 EndY=35 EndZ=0
    g8: LineSegment StartX=110.5 StartY=9.01251 StartZ=0 EndX=114.163 EndY=9.01251 EndZ=0
    g9: LineSegment StartX=114 StartY=35 StartZ=0 EndX=19 EndY=35 EndZ=0
    g10: LineSegment StartX=0 StartY=3 StartZ=0 EndX=0 EndY=0 EndZ=0
    g11: LineSegment StartX=3 StartY=0 StartZ=0 EndX=0 EndY=0 EndZ=0
    g12: LineSegment StartX=3 StartY=19 StartZ=0 EndX=3 EndY=0 EndZ=0
  constraints (33):
    c: Vertical(g0)
    c: Distance(g0) = 19
    c: Block(g0)
    c: Coincident(g1,g0)
    c: Block(g1)
    c: Vertical(g2)
    c: Block(g2)
    c: Coincident(g3,g0)
    c: Horizontal(g3)
    c: Distance(g3) = 98
    c: Coincident(g4,g3)
    c: Coincident(g4,g2)
    c: Block(g4)
    c: Coincident(g5,g4)
    c: Coincident(g6,g1)
    c: Block(g6)
    c: Block(g5)
    c: Coincident(g7,g6)
    c: Vertical(g7)
    c: Coincident(g8,g6)
    c: Coincident(g8,g1)
    c: Coincident(g9,g7)
    c: Coincident(g9,g5)
    c: Horizontal(g9)
    c: Tangent(g9,g5)
    c: Coincident(g10,g2)
    c: Distance(g10) = 3
    c: Vertical(g10)
    c: Coincident(g11,g10)
    c: Horizontal(g11)
    c: Coincident(g12,g5)
    c: Coincident(g12,g11)
    c: Vertical(g12)
FEATURE [Part::Extrusion] Extrude011  label="top006"
  Base = -> Sketch013
  Dir = (0,0,1)
  DirMode = 2
  FaceMakerClass = Part::FaceMakerBullseye
  LengthFwd = 72
  LengthRev = 0
  Solid = true
  Symmetric = false
FEATURE [Sketcher::SketchObject] Sketch014
  FullyConstrained = true
  MapMode = 3
  Placement = pos=(0,0,0) rot=(1,0,0;1.5708rad)
  Support = -> [Extrude011]
  sketch-geometry (8):
    g0: Circle CenterX=80.351 CenterY=-67.6202 CenterZ=0 NormalX=0 NormalY=0 NormalZ=1 AngleXU=0 Radius=2
    g1: Circle CenterX=80.351 CenterY=-67.6202 CenterZ=0 NormalX=0 NormalY=0 NormalZ=1 AngleXU=0 Radius=3
    g2: Circle CenterX=80.351 CenterY=-4.92017 CenterZ=0 NormalX=0 NormalY=0 NormalZ=1 AngleXU=0 Radius=2
    g3: Circle CenterX=80.351 CenterY=-4.92017 CenterZ=0 NormalX=0 NormalY=0 NormalZ=1 AngleXU=0 Radius=3
    g4: Circle CenterX=23.851 CenterY=-4.92017 CenterZ=0 NormalX=0 NormalY=0 NormalZ=1 AngleXU=0 Radius=2
    g5: Circle CenterX=23.851 CenterY=-4.92017 CenterZ=0 NormalX=0 NormalY=0 NormalZ=1 AngleXU=0 Radius=3
    g6: Circle CenterX=23.851 CenterY=-67.6202 CenterZ=0 NormalX=0 NormalY=0 NormalZ=1 AngleXU=0 Radius=2
    g7: Circle CenterX=23.851 CenterY=-67.6202 CenterZ=0 NormalX=0 NormalY=0 NormalZ=1 AngleXU=0 Radius=3
  constraints (8):
    c: Block(g3)
    c: Block(g2)
    c: Block(g1)
    c: Block(g0)
    c: Block(g6)
    c: Block(g7)
    c: Block(g4)
    c: Block(g5)
FEATURE [Part::Feature] Face027
  shape: bbox 11 x 6 x 2e-07 mm, 1 faces, 0 solids (baked)
FEATURE [Part::Revolution] Revolve027
  Angle = 360
  Axis = (0,1,0)
  Base = (0,0,0)
  FaceMakerClass = Part::FaceMakerBullseye
  Placement = pos=(30.3,-1,51.7) rot=(0,0,1;0rad)
  Solid = false
  Source = -> Face027
  Symmetric = false
FEATURE [Part::Feature] Face028
  shape: bbox 11 x 6 x 2e-07 mm, 1 faces, 0 solids (baked)
FEATURE [Part::Revolution] Revolve028
  Angle = 360
  Axis = (0,1,0)
  Base = (0,0,0)
  FaceMakerClass = Part::FaceMakerBullseye
  Placement = pos=(62.3,-1,19.7) rot=(0,0,1;0rad)
  Solid = false
  Source = -> Face028
  Symmetric = false
FEATURE [Part::Feature] Face029
  shape: bbox 11 x 6 x 2e-07 mm, 1 faces, 0 solids (baked)
FEATURE [Part::Revolution] Revolve029
  Angle = 360
  Axis = (0,1,0)
  Base = (0,0,0)
  FaceMakerClass = Part::FaceMakerBullseye
  Placement = pos=(62.3,-1,51.7) rot=(0,0,1;0rad)
  Solid = false
  Source = -> Face029
  Symmetric = false
FEATURE [Part::Feature] Wire
  shape: bbox 11 x 5.2 x 2e-07 mm, 0 faces, 0 solids (baked)
FEATURE [Part::Revolution] Revolve030
  Angle = 360
  Axis = (0,1,0)
  Base = (0,0,0)
  FaceMakerClass = Part::FaceMakerBullseye
  Placement = pos=(30.3,38,19.7) rot=(0,0,1;0rad)
  Solid = true
  Source = -> Wire
  Symmetric = false
FEATURE [Part::Feature] Wire001
  shape: bbox 11 x 5.2 x 2e-07 mm, 0 faces, 0 solids (baked)
FEATURE [Part::Revolution] Revolve031
  Angle = 360
  Axis = (0,1,0)
  Base = (0,0,0)
  FaceMakerClass = Part::FaceMakerBullseye
  Placement = pos=(30.3,38,51.7) rot=(0,0,1;0rad)
  Solid = true
  Source = -> Wire001
  Symmetric = false
FEATURE [Part::Feature] Wire002
  shape: bbox 11 x 5.2 x 2e-07 mm, 0 faces, 0 solids (baked)
FEATURE [Part::Revolution] Revolve032
  Angle = 360
  Axis = (0,1,0)
  Base = (0,0,0)
  FaceMakerClass = Part::FaceMakerBullseye
  Placement = pos=(62.3,38,51.7) rot=(0,0,1;0rad)
  Solid = true
  Source = -> Wire002
  Symmetric = false
FEATURE [Part::Feature] Wire003
  shape: bbox 11 x 5.2 x 2e-07 mm, 0 faces, 0 solids (baked)
FEATURE [Part::Revolution] Revolve033
  Angle = 360
  Axis = (0,1,0)
  Base = (0,0,0)
  FaceMakerClass = Part::FaceMakerBullseye
  Placement = pos=(62.3,38,19.7) rot=(0,0,1;0rad)
  Solid = true
  Source = -> Wire003
  Symmetric = false
FEATURE [Part::MultiFuse] Fusion045  label="altRandScrewHousing"
  Shapes = -> [Revolve029,Revolve027,Revolve028,Revolve026]
FEATURE [Part::MultiFuse] Fusion046  label="fanScrewHousing"
  Shapes = -> [Revolve033,Revolve032,Revolve031,Revolve030]
FEATURE [Sketcher::SketchObject] Sketch015
  FullyConstrained = true
  sketch-geometry (17):
    g0: Circle CenterX=-3.5 CenterY=23.5 CenterZ=0 NormalX=0 NormalY=0 NormalZ=1 AngleXU=0 Radius=1
    g1: Circle CenterX=-1 CenterY=15.25 CenterZ=0 NormalX=0 NormalY=0 NormalZ=1 AngleXU=0 Radius=1
    g2: Circle CenterX=-3.5 CenterY=7 CenterZ=0 NormalX=0 NormalY=0 NormalZ=1 AngleXU=0 Radius=1
    g3: BSplineCurve PolesCount=3 KnotsCount=2 Degree=2 IsPeriodic=0
    g4: GeomPoint X=-3.5 Y=23.5 Z=0
    g5: GeomPoint X=-3.5 Y=7 Z=0
    g6: Circle CenterX=-4.8 CenterY=30.5 CenterZ=0 NormalX=0 NormalY=0 NormalZ=1 AngleXU=0 Radius=1
    g7: Circle CenterX=-3.5 CenterY=30.5 CenterZ=0 NormalX=0 NormalY=0 NormalZ=1 AngleXU=0 Radius=1
    g8: Circle CenterX=-3.5 CenterY=29.2 CenterZ=0 NormalX=0 NormalY=0 NormalZ=1 AngleXU=0 Radius=1
    g9: BSplineCurve PolesCount=3 KnotsCount=2 Degree=2 IsPeriodic=0
    g10: GeomPoint X=-4.8 Y=30.5 Z=0
    g11: GeomPoint X=-3.5 Y=29.2 Z=0
    g12: LineSegment StartX=-3.5 StartY=29.2 StartZ=0 EndX=-3.5 EndY=23.5 EndZ=0
    g13: LineSegment StartX=-4.8 StartY=30.5 StartZ=0 EndX=0 EndY=30.5 EndZ=0
    g14: LineSegment StartX=-3.5 StartY=0.3 StartZ=0 EndX=0 EndY=0.3 EndZ=0
    g15: LineSegment StartX=-3.5 StartY=0.3 StartZ=0 EndX=-3.5 EndY=7 EndZ=0
    g16: LineSegment StartX=0 StartY=0.3 StartZ=0 EndX=0 EndY=30.5 EndZ=0
  constraints (33):
    c: Weight(g0) = 1
    c: Equal(g0,g1)
    c: Equal(g0,g2)
    c: InternalAlignment(g0,g3)
    c: InternalAlignment(g1,g3)
    c: InternalAlignment(g2,g3)
    c: InternalAlignment(g4,g3)
    c: InternalAlignment(g5,g3)
    c: Block(g3)
    c: Weight(g6) = 1
    c: Equal(g6,g7)
    c: Equal(g6,g8)
    c: InternalAlignment(g6,g9)
    c: InternalAlignment(g7,g9)
    c: InternalAlignment(g8,g9)
    c: InternalAlignment(g10,g9)
    c: InternalAlignment(g11,g9)
    c: Block(g9)
    c: Coincident(g12,g9)
    c: Coincident(g12,g3)
    c: Vertical(g12)
    c: Coincident(g13,g9)
    c: Horizontal(g13)
    c: Distance(g13) = 4.8
    c: Horizontal(g14)
    c: Block(g14)
    c: Coincident(g15,g14)
    c: Coincident(g15,g3)
    c: Vertical(g15)
    c: Coincident(g16,g14)
    c: Coincident(g16,g13)
    c: Vertical(g16)
    c: Tangent(g16,g1)
FEATURE [Sketcher::SketchObject] Sketch016
  FullyConstrained = true
  sketch-geometry (16):
    g0: Circle CenterX=-3.5 CenterY=23.5 CenterZ=0 NormalX=0 NormalY=0 NormalZ=1 AngleXU=0 Radius=1
    g1: Circle CenterX=-1 CenterY=15.25 CenterZ=0 NormalX=0 NormalY=0 NormalZ=1 AngleXU=0 Radius=1
    g2: Circle CenterX=-3.5 CenterY=7 CenterZ=0 NormalX=0 NormalY=0 NormalZ=1 AngleXU=0 Radius=1
    g3: BSplineCurve PolesCount=3 KnotsCount=2 Degree=2 IsPeriodic=0
    g4: GeomPoint X=-3.5 Y=23.5 Z=0
    g5: GeomPoint X=-3.5 Y=7 Z=0
    g6: LineSegment StartX=-3.5 StartY=28.2 StartZ=0 EndX=-3.5 EndY=23.5 EndZ=0
    g7: LineSegment StartX=0 StartY=29.5 StartZ=0 EndX=0 EndY=30 EndZ=0
    g8: LineSegment StartX=-3.5 StartY=28.2 StartZ=0 EndX=-3.5 EndY=30 EndZ=0
    g9: LineSegment StartX=0 StartY=30 StartZ=0 EndX=0 EndY=30.5 EndZ=0
    g10: LineSegment StartX=0 StartY=30.5 StartZ=0 EndX=-3.5 EndY=30.5 EndZ=0
    g11: LineSegment StartX=-3.5 StartY=30.5 StartZ=0 EndX=-3.5 EndY=30 EndZ=0
    g12: LineSegment StartX=0 StartY=29.5 StartZ=0 EndX=0 EndY=5 EndZ=0
    g13: LineSegment StartX=-3.5 StartY=0.3 StartZ=0 EndX=-3.5 EndY=7 EndZ=0
    g14: LineSegment StartX=-3.5 StartY=0.3 StartZ=0 EndX=0 EndY=0.3 EndZ=0
    g15: LineSegment StartX=0 StartY=5 StartZ=0 EndX=0 EndY=0.3 EndZ=0
  constraints (39):
    c: Weight(g0) = 1
    c: Equal(g0,g1)
    c: Equal(g0,g2)
    c: InternalAlignment(g0,g3)
    c: InternalAlignment(g1,g3)
    c: InternalAlignment(g2,g3)
    c: InternalAlignment(g4,g3)
    c: InternalAlignment(g5,g3)
    c: Block(g3)
    c: Coincident(g6,g3)
    c: Vertical(g6)
    c: Vertical(g7)
    c: Distance(g7) = 0.5
    c: Coincident(g8,g6)
    c: Vertical(g8)
    c: Block(g6)
    c: Block(g7)
    c: Vertical(g9)
    c: Equal(g7,g9) = 0.5
    c: Block(g9)
    c: Coincident(g9,g7)
    c: Horizontal(g10)
    c: Coincident(g10,g9)
    c: Coincident(g11,g10)
    c: Coincident(g11,g8)
    c: Vertical(g11)
    c: Block(g11)
    c: Coincident(g12,g7)
    c: Vertical(g12)
    c: Coincident(g13,g3)
    c: Vertical(g13)
    c: Distance(g13) = 6.7
    c: Coincident(g14,g13)
    c: Horizontal(g14)
    c: Block(g14)
    c: Coincident(g15,g12)
    c: Coincident(g15,g14)
    c: Vertical(g15)
    c: Block(g15)
FEATURE [Sketcher::SketchObject] Sketch017
  FullyConstrained = true
  sketch-geometry (11):
    g0: LineSegment StartX=-3.5 StartY=1e-16 StartZ=0 EndX=-1.6 EndY=1e-16 EndZ=0
    g1: LineSegment StartX=-1.6 StartY=1e-16 StartZ=0 EndX=-1.6 EndY=1.5 EndZ=0
    g2: LineSegment StartX=-3.5 StartY=1.5 StartZ=0 EndX=-1.6 EndY=1.5 EndZ=0
    g3: LineSegment StartX=-3.5 StartY=1e-16 StartZ=0 EndX=-4.8 EndY=1e-16 EndZ=0
    g4: Circle CenterX=-3.5 CenterY=1.3 CenterZ=0 NormalX=0 NormalY=0 NormalZ=1 AngleXU=0 Radius=1
    g5: Circle CenterX=-3.5 CenterY=1e-16 CenterZ=0 NormalX=0 NormalY=0 NormalZ=1 AngleXU=0 Radius=1
    g6: Circle CenterX=-4.8 CenterY=1e-16 CenterZ=0 NormalX=0 NormalY=0 NormalZ=1 AngleXU=0 Radius=1
    g7: BSplineCurve PolesCount=3 KnotsCount=2 Degree=2 IsPeriodic=0
    g8: GeomPoint X=-3.5 Y=1.3 Z=0
    g9: GeomPoint X=-4.8 Y=1e-16 Z=0
    g10: LineSegment StartX=-3.5 StartY=1.3 StartZ=0 EndX=-3.5 EndY=1.5 EndZ=0
  constraints (24):
    c: Horizontal(g0)
    c: Distance(g0) = 1.9
    c: Block(g0)
    c: Coincident(g1,g0)
    c: Vertical(g1)
    c: Coincident(g2,g1)
    c: Horizontal(g2)
    c: Coincident(g3,g0)
    c: Horizontal(g3)
    c: Distance(g3) = 1.3
    c: Weight(g4) = 1
    c: Equal(g4,g5)
    c: Coincident(g5,g0)
    c: Equal(g4,g6)
    c: Coincident(g7,g3)
    c: InternalAlignment(g4,g7)
    c: InternalAlignment(g5,g7)
    c: InternalAlignment(g6,g7)
    c: InternalAlignment(g8,g7)
    c: InternalAlignment(g9,g7)
    c: Coincident(g10,g7)
    c: Coincident(g10,g2)
    c: Vertical(g10)
    c: Block(g10)
FEATURE [Part::Feature] Face035
  shape: bbox 3.2 x 1.5 x 2e-07 mm, 1 faces, 0 solids (baked)
FEATURE [Part::Revolution] Revolve039  label="backCaseScrewRetainer"
  Angle = 360
  Axis = (0,1,0)
  Base = (0,0,0)
  FaceMakerClass = Part::FaceMakerBullseye
  Placement = pos=(12.5,3,62) rot=(0,0,1;0rad)
  Solid = false
  Source = -> Face035
  Symmetric = false
FEATURE [Part::Feature] Face036
  shape: bbox 3.2 x 1.5 x 2e-07 mm, 1 faces, 0 solids (baked)
FEATURE [Part::Feature] Face039
  shape: bbox 4.8 x 30.2 x 2e-07 mm, 1 faces, 0 solids (baked)
FEATURE [Part::Revolution] Revolve043  label="frontCaseScrewPost002"
  Angle = 360
  Axis = (0,1,0)
  Base = (0,0,0)
  FaceMakerClass = Part::FaceMakerBullseye
  Placement = pos=(89.5,4.5,3.5) rot=(0,0,1;0rad)
  Solid = false
  Source = -> Face039
  Symmetric = false
FEATURE [Part::Feature] Face042
  shape: bbox 4.8 x 30.2 x 2e-07 mm, 1 faces, 0 solids (baked)
FEATURE [Part::Revolution] Revolve046  label="frontCaseScrewPost003"
  Angle = 360
  Axis = (0,1,0)
  Base = (0,0,0)
  FaceMakerClass = Part::FaceMakerBullseye
  Placement = pos=(89.5,4.5,68.5) rot=(0,0,1;0rad)
  Solid = false
  Source = -> Face042
  Symmetric = false
FEATURE [Part::Feature] Face043
  shape: bbox 3.2 x 1.5 x 2e-07 mm, 1 faces, 0 solids (baked)
FEATURE [Part::Revolution] Revolve047  label="frontCaseScrewRetainer002"
  Angle = 360
  Axis = (0,1,0)
  Base = (0,0,0)
  FaceMakerClass = Part::FaceMakerBullseye
  Placement = pos=(89.5,3,68.5) rot=(0,0,1;0rad)
  Solid = false
  Source = -> Face043
  Symmetric = false
FEATURE [Part::Feature] Face044
  shape: bbox 3.2 x 1.5 x 2e-07 mm, 1 faces, 0 solids (baked)
FEATURE [Part::Revolution] Revolve048  label="frontCaseScrewRetainer003"
  Angle = 360
  Axis = (0,1,0)
  Base = (0,0,0)
  FaceMakerClass = Part::FaceMakerBullseye
  Placement = pos=(89.5,3,3.5) rot=(0,0,1;0rad)
  Solid = false
  Source = -> Face044
  Symmetric = false
FEATURE [App::MeasureDistance] Distance002  label="Distance: 1.67 mm"
  Distance = 1.66921
  P1 = (99.2361,4.7524,71.7)
  P2 = (99.2347,6.42161,71.7)
FEATURE [Sketcher::SketchObject] Sketch018
  FullyConstrained = true
  sketch-geometry (7):
    g0: LineSegment StartX=0 StartY=0 StartZ=0 EndX=0 EndY=6 EndZ=0
    g1: Circle CenterX=0 CenterY=0 CenterZ=0 NormalX=0 NormalY=0 NormalZ=1 AngleXU=0 Radius=1
    g2: Circle CenterX=8 CenterY=6 CenterZ=0 NormalX=0 NormalY=0 NormalZ=1 AngleXU=0 Radius=1
    g3: BSplineCurve PolesCount=3 KnotsCount=2 Degree=2 IsPeriodic=0
    g4: GeomPoint X=0 Y=0 Z=0
    g5: GeomPoint X=8 Y=6 Z=0
    g6: LineSegment StartX=0 StartY=6 StartZ=0 EndX=8 EndY=6 EndZ=0
  constraints (14):
    c: Coincident(g0,g-1)
    c: Distance(g0) = 6
    c: Vertical(g0)
    c: Coincident(g3,g0)
    c: Weight(g1) = 1
    c: Equal(g1,g2)
    c: InternalAlignment(g1,g3)
    c: InternalAlignment(g2,g3)
    c: InternalAlignment(g4,g3)
    c: InternalAlignment(g5,g3)
    c: Block(g3)
    c: Coincident(g6,g0)
    c: Coincident(g6,g3)
    c: Horizontal(g6)
FEATURE [Part::Extrusion] Extrude012  label="caseScrewPillarBracket"
  Base = -> Sketch018
  Dir = (0,0,1)
  DirMode = 2
  FaceMakerClass = Part::FaceMakerBullseye
  LengthFwd = 2.4
  LengthRev = 0
  Placement = pos=(15.76,29,8.8) rot=(0,1,0;0rad)
  Solid = true
  Symmetric = false
FEATURE [Sketcher::SketchObject] Sketch019
  FullyConstrained = true
  sketch-geometry (7):
    g0: LineSegment StartX=0 StartY=0 StartZ=0 EndX=0 EndY=6 EndZ=0
    g1: Circle CenterX=0 CenterY=0 CenterZ=0 NormalX=0 NormalY=0 NormalZ=1 AngleXU=0 Radius=1
    g2: Circle CenterX=8 CenterY=6 CenterZ=0 NormalX=0 NormalY=0 NormalZ=1 AngleXU=0 Radius=1
    g3: BSplineCurve PolesCount=3 KnotsCount=2 Degree=2 IsPeriodic=0
    g4: GeomPoint X=0 Y=0 Z=0
    g5: GeomPoint X=8 Y=6 Z=0
    g6: LineSegment StartX=0 StartY=6 StartZ=0 EndX=8 EndY=6 EndZ=0
  constraints (14):
    c: Coincident(g0,g-1)
    c: Distance(g0) = 6
    c: Vertical(g0)
    c: Coincident(g3,g0)
    c: Weight(g1) = 1
    c: Equal(g1,g2)
    c: InternalAlignment(g1,g3)
    c: InternalAlignment(g2,g3)
    c: InternalAlignment(g4,g3)
    c: InternalAlignment(g5,g3)
    c: Block(g3)
    c: Coincident(g6,g0)
    c: Coincident(g6,g3)
    c: Horizontal(g6)
FEATURE [Part::Extrusion] Extrude013  label="caseScrewPillarBracket001"
  Base = -> Sketch019
  Dir = (0,0,1)
  DirMode = 2
  FaceMakerClass = Part::FaceMakerBullseye
  LengthFwd = 2.4
  LengthRev = 0
  Placement = pos=(15.76,29,60.8) rot=(0,0,1;0rad)
  Solid = true
  Symmetric = false
FEATURE [Sketcher::SketchObject] Sketch020
  FullyConstrained = true
  sketch-geometry (7):
    g0: LineSegment StartX=0 StartY=0 StartZ=0 EndX=0 EndY=6 EndZ=0
    g1: Circle CenterX=0 CenterY=0 CenterZ=0 NormalX=0 NormalY=0 NormalZ=1 AngleXU=0 Radius=1
    g2: Circle CenterX=8 CenterY=6 CenterZ=0 NormalX=0 NormalY=0 NormalZ=1 AngleXU=0 Radius=1
    g3: BSplineCurve PolesCount=3 KnotsCount=2 Degree=2 IsPeriodic=0
    g4: GeomPoint X=0 Y=0 Z=0
    g5: GeomPoint X=8 Y=6 Z=0
    g6: LineSegment StartX=0 StartY=6 StartZ=0 EndX=8 EndY=6 EndZ=0
  constraints (14):
    c: Coincident(g0,g-1)
    c: Distance(g0) = 6
    c: Vertical(g0)
    c: Coincident(g3,g0)
    c: Weight(g1) = 1
    c: Equal(g1,g2)
    c: InternalAlignment(g1,g3)
    c: InternalAlignment(g2,g3)
    c: InternalAlignment(g4,g3)
    c: InternalAlignment(g5,g3)
    c: Block(g3)
    c: Coincident(g6,g0)
    c: Coincident(g6,g3)
    c: Horizontal(g6)
FEATURE [Part::Extrusion] Extrude014  label="caseScrewPillarBracket002"
  Base = -> Sketch020
  Dir = (0,0,1)
  DirMode = 2
  FaceMakerClass = Part::FaceMakerBullseye
  LengthFwd = 2.4
  LengthRev = 0
  Placement = pos=(13.7,29,13.26) rot=(0,-1,0;1.5708rad)
  Solid = true
  Symmetric = false
FEATURE [Sketcher::SketchObject] Sketch021
  FullyConstrained = true
  sketch-geometry (7):
    g0: LineSegment StartX=0 StartY=0 StartZ=0 EndX=0 EndY=6 EndZ=0
    g1: Circle CenterX=0 CenterY=0 CenterZ=0 NormalX=0 NormalY=0 NormalZ=1 AngleXU=0 Radius=1
    g2: Circle CenterX=8 CenterY=6 CenterZ=0 NormalX=0 NormalY=0 NormalZ=1 AngleXU=0 Radius=1
    g3: BSplineCurve PolesCount=3 KnotsCount=2 Degree=2 IsPeriodic=0
    g4: GeomPoint X=0 Y=0 Z=0
    g5: GeomPoint X=8 Y=6 Z=0
    g6: LineSegment StartX=0 StartY=6 StartZ=0 EndX=8 EndY=6 EndZ=0
  constraints (14):
    c: Coincident(g0,g-1)
    c: Distance(g0) = 6
    c: Vertical(g0)
    c: Coincident(g3,g0)
    c: Weight(g1) = 1
    c: Equal(g1,g2)
    c: InternalAlignment(g1,g3)
    c: InternalAlignment(g2,g3)
    c: InternalAlignment(g4,g3)
    c: InternalAlignment(g5,g3)
    c: Block(g3)
    c: Coincident(g6,g0)
    c: Coincident(g6,g3)
    c: Horizontal(g6)
FEATURE [Part::Extrusion] Extrude015  label="caseScrewPillarBracket003"
  Base = -> Sketch021
  Dir = (0,0,1)
  DirMode = 2
  FaceMakerClass = Part::FaceMakerBullseye
  LengthFwd = 2.4
  LengthRev = 0
  Placement = pos=(11.3,29,58.74) rot=(0,1,0;1.5708rad)
  Solid = true
  Symmetric = false
FEATURE [Sketcher::SketchObject] Sketch022
  FullyConstrained = true
  sketch-geometry (7):
    g0: LineSegment StartX=0 StartY=0 StartZ=0 EndX=0 EndY=6 EndZ=0
    g1: Circle CenterX=0 CenterY=0 CenterZ=0 NormalX=0 NormalY=0 NormalZ=1 AngleXU=0 Radius=1
    g2: Circle CenterX=8 CenterY=6 CenterZ=0 NormalX=0 NormalY=0 NormalZ=1 AngleXU=0 Radius=1
    g3: BSplineCurve PolesCount=3 KnotsCount=2 Degree=2 IsPeriodic=0
    g4: GeomPoint X=0 Y=0 Z=0
    g5: GeomPoint X=8 Y=6 Z=0
    g6: LineSegment StartX=0 StartY=6 StartZ=0 EndX=8 EndY=6 EndZ=0
  constraints (14):
    c: Coincident(g0,g-1)
    c: Distance(g0) = 6
    c: Vertical(g0)
    c: Coincident(g3,g0)
    c: Weight(g1) = 1
    c: Equal(g1,g2)
    c: InternalAlignment(g1,g3)
    c: InternalAlignment(g2,g3)
    c: InternalAlignment(g4,g3)
    c: InternalAlignment(g5,g3)
    c: Block(g3)
    c: Coincident(g6,g0)
    c: Coincident(g6,g3)
    c: Horizontal(g6)
FEATURE [Part::Extrusion] Extrude016  label="caseScrewPillarBracket004"
  Base = -> Sketch022
  Dir = (0,0,1)
  DirMode = 2
  FaceMakerClass = Part::FaceMakerBullseye
  LengthFwd = 2.4
  LengthRev = 0
  Placement = pos=(88.3,29,65.23) rot=(0,1,0;1.5708rad)
  Solid = true
  Symmetric = false
FEATURE [Sketcher::SketchObject] Sketch023
  FullyConstrained = true
  sketch-geometry (7):
    g0: LineSegment StartX=0 StartY=0 StartZ=0 EndX=0 EndY=6 EndZ=0
    g1: Circle CenterX=0 CenterY=0 CenterZ=0 NormalX=0 NormalY=0 NormalZ=1 AngleXU=0 Radius=1
    g2: Circle CenterX=8 CenterY=6 CenterZ=0 NormalX=0 NormalY=0 NormalZ=1 AngleXU=0 Radius=1
    g3: BSplineCurve PolesCount=3 KnotsCount=2 Degree=2 IsPeriodic=0
    g4: GeomPoint X=0 Y=0 Z=0
    g5: GeomPoint X=8 Y=6 Z=0
    g6: LineSegment StartX=0 StartY=6 StartZ=0 EndX=8 EndY=6 EndZ=0
  constraints (14):
    c: Coincident(g0,g-1)
    c: Distance(g0) = 6
    c: Vertical(g0)
    c: Coincident(g3,g0)
    c: Weight(g1) = 1
    c: Equal(g1,g2)
    c: InternalAlignment(g1,g3)
    c: InternalAlignment(g2,g3)
    c: InternalAlignment(g4,g3)
    c: InternalAlignment(g5,g3)
    c: Block(g3)
    c: Coincident(g6,g0)
    c: Coincident(g6,g3)
    c: Horizontal(g6)
FEATURE [Part::Extrusion] Extrude017  label="caseScrewPillarBracket005"
  Base = -> Sketch023
  Dir = (0,0,1)
  DirMode = 2
  FaceMakerClass = Part::FaceMakerBullseye
  LengthFwd = 2.4
  LengthRev = 0
  Placement = pos=(90.7,29,6.77) rot=(0,-1,0;1.5708rad)
  Solid = true
  Symmetric = false
FEATURE [Sketcher::SketchObject] Sketch024
  FullyConstrained = true
  sketch-geometry (7):
    g0: LineSegment StartX=0 StartY=0 StartZ=0 EndX=0 EndY=6 EndZ=0
    g1: Circle CenterX=0 CenterY=0 CenterZ=0 NormalX=0 NormalY=0 NormalZ=1 AngleXU=0 Radius=1
    g2: Circle CenterX=8 CenterY=6 CenterZ=0 NormalX=0 NormalY=0 NormalZ=1 AngleXU=0 Radius=1
    g3: BSplineCurve PolesCount=3 KnotsCount=2 Degree=2 IsPeriodic=0
    g4: GeomPoint X=0 Y=0 Z=0
    g5: GeomPoint X=8 Y=6 Z=0
    g6: LineSegment StartX=0 StartY=6 StartZ=0 EndX=8 EndY=6 EndZ=0
  constraints (14):
    c: Coincident(g0,g-1)
    c: Distance(g0) = 6
    c: Vertical(g0)
    c: Coincident(g3,g0)
    c: Weight(g1) = 1
    c: Equal(g1,g2)
    c: InternalAlignment(g1,g3)
    c: InternalAlignment(g2,g3)
    c: InternalAlignment(g4,g3)
    c: InternalAlignment(g5,g3)
    c: Block(g3)
    c: Coincident(g6,g0)
    c: Coincident(g6,g3)
    c: Horizontal(g6)
FEATURE [Part::Extrusion] Extrude018  label="caseScrewPillarBracket006"
  Base = -> Sketch024
  Dir = (0,0,1)
  DirMode = 2
  FaceMakerClass = Part::FaceMakerBullseye
  LengthFwd = 2.4
  LengthRev = 0
  Placement = pos=(103.7,29,6.77) rot=(0,-1,0;1.5708rad)
  Solid = true
  Symmetric = false
FEATURE [Sketcher::SketchObject] Sketch025
  FullyConstrained = true
  sketch-geometry (7):
    g0: LineSegment StartX=0 StartY=0 StartZ=0 EndX=0 EndY=6 EndZ=0
    g1: Circle CenterX=0 CenterY=0 CenterZ=0 NormalX=0 NormalY=0 NormalZ=1 AngleXU=0 Radius=1
    g2: Circle CenterX=8 CenterY=6 CenterZ=0 NormalX=0 NormalY=0 NormalZ=1 AngleXU=0 Radius=1
    g3: BSplineCurve PolesCount=3 KnotsCount=2 Degree=2 IsPeriodic=0
    g4: GeomPoint X=0 Y=0 Z=0
    g5: GeomPoint X=8 Y=6 Z=0
    g6: LineSegment StartX=0 StartY=6 StartZ=0 EndX=8 EndY=6 EndZ=0
  constraints (14):
    c: Coincident(g0,g-1)
    c: Distance(g0) = 6
    c: Vertical(g0)
    c: Coincident(g3,g0)
    c: Weight(g1) = 1
    c: Equal(g1,g2)
    c: InternalAlignment(g1,g3)
    c: InternalAlignment(g2,g3)
    c: InternalAlignment(g4,g3)
    c: InternalAlignment(g5,g3)
    c: Block(g3)
    c: Coincident(g6,g0)
    c: Coincident(g6,g3)
    c: Horizontal(g6)
FEATURE [Part::Extrusion] Extrude019  label="caseScrewPillarBracket007"
  Base = -> Sketch025
  Dir = (0,0,1)
  DirMode = 2
  FaceMakerClass = Part::FaceMakerBullseye
  LengthFwd = 2.4
  LengthRev = 0
  Placement = pos=(101.3,29,65.23) rot=(0,1,0;1.5708rad)
  Solid = true
  Symmetric = false
FEATURE [Part::Box] Box011  label="frontCaseScrewPillarBracket"
  AttacherType = Attacher::AttachEngine3D
  Height = 2.4
  Length = 16
  Placement = pos=(87,28,2.3) rot=(0,0,1;0rad)
  Width = 7
FEATURE [Part::Box] Box012  label="frontCaseScrewPillarBracket001"
  AttacherType = Attacher::AttachEngine3D
  Height = 2.4
  Length = 16
  Placement = pos=(87,28,67.3) rot=(0,0,1;0rad)
  Width = 7
FEATURE [Sketcher::SketchObject] Sketch026
  FullyConstrained = true
  sketch-geometry (17):
    g0: Circle CenterX=-3.5 CenterY=23.5 CenterZ=0 NormalX=0 NormalY=0 NormalZ=1 AngleXU=0 Radius=1
    g1: Circle CenterX=-1 CenterY=15.25 CenterZ=0 NormalX=0 NormalY=0 NormalZ=1 AngleXU=0 Radius=1
    g2: Circle CenterX=-3.5 CenterY=7 CenterZ=0 NormalX=0 NormalY=0 NormalZ=1 AngleXU=0 Radius=1
    g3: BSplineCurve PolesCount=3 KnotsCount=2 Degree=2 IsPeriodic=0
    g4: GeomPoint X=-3.5 Y=23.5 Z=0
    g5: GeomPoint X=-3.5 Y=7 Z=0
    g6: Circle CenterX=-4.8 CenterY=30.5 CenterZ=0 NormalX=0 NormalY=0 NormalZ=1 AngleXU=0 Radius=1
    g7: Circle CenterX=-3.5 CenterY=30.5 CenterZ=0 NormalX=0 NormalY=0 NormalZ=1 AngleXU=0 Radius=1
    g8: Circle CenterX=-3.5 CenterY=29.2 CenterZ=0 NormalX=0 NormalY=0 NormalZ=1 AngleXU=0 Radius=1
    g9: BSplineCurve PolesCount=3 KnotsCount=2 Degree=2 IsPeriodic=0
    g10: GeomPoint X=-4.8 Y=30.5 Z=0
    g11: GeomPoint X=-3.5 Y=29.2 Z=0
    g12: LineSegment StartX=-3.5 StartY=29.2 StartZ=0 EndX=-3.5 EndY=23.5 EndZ=0
    g13: LineSegment StartX=-4.8 StartY=30.5 StartZ=0 EndX=0 EndY=30.5 EndZ=0
    g14: LineSegment StartX=-3.5 StartY=5 StartZ=0 EndX=-3.5 EndY=7 EndZ=0
    g15: LineSegment StartX=0 StartY=5 StartZ=0 EndX=0 EndY=30.5 EndZ=0
    g16: LineSegment StartX=-3.5 StartY=5 StartZ=0 EndX=0 EndY=5 EndZ=0
  constraints (33):
    c: Weight(g0) = 1
    c: Equal(g0,g1)
    c: Equal(g0,g2)
    c: InternalAlignment(g0,g3)
    c: InternalAlignment(g1,g3)
    c: InternalAlignment(g2,g3)
    c: InternalAlignment(g4,g3)
    c: InternalAlignment(g5,g3)
    c: Block(g3)
    c: Weight(g6) = 1
    c: Equal(g6,g7)
    c: Equal(g6,g8)
    c: InternalAlignment(g6,g9)
    c: InternalAlignment(g7,g9)
    c: InternalAlignment(g8,g9)
    c: InternalAlignment(g10,g9)
    c: InternalAlignment(g11,g9)
    c: Block(g9)
    c: Coincident(g12,g9)
    c: Coincident(g12,g3)
    c: Vertical(g12)
    c: Coincident(g13,g9)
    c: Horizontal(g13)
    c: Distance(g13) = 4.8
    c: Coincident(g14,g3)
    c: Vertical(g14)
    c: Coincident(g15,g13)
    c: Vertical(g15)
    c: Tangent(g15,g1)
    c: Distance(g14) = 2
    c: Coincident(g16,g14)
    c: Horizontal(g16)
    c: Coincident(g15,g16)
FEATURE [Part::Feature] Face050
  shape: bbox 4.8 x 25.5 x 2e-07 mm, 1 faces, 0 solids (baked)
FEATURE [Part::Revolution] Revolve054  label="moreFrontCaseScrewPost001"
  Angle = 360
  Axis = (0,1,0)
  Base = (0,0,0)
  FaceMakerClass = Part::FaceMakerBullseye
  Placement = pos=(102.5,4.5,3.5) rot=(0,0,1;0rad)
  Solid = false
  Source = -> Face050
  Symmetric = false
FEATURE [Part::Feature] Face051
  shape: bbox 4.8 x 25.5 x 2e-07 mm, 1 faces, 0 solids (baked)
FEATURE [Part::Revolution] Revolve055  label="moreFrontCaseScrewPost002"
  Angle = 360
  Axis = (0,1,0)
  Base = (0,0,0)
  FaceMakerClass = Part::FaceMakerBullseye
  Placement = pos=(102.5,4.5,68.5) rot=(0,0,1;0rad)
  Solid = false
  Source = -> Face051
  Symmetric = false
FEATURE [Sketcher::SketchObject] Sketch027
  FullyConstrained = true
  sketch-geometry (10):
    g0: LineSegment StartX=-1.6 StartY=4.7 StartZ=0 EndX=-1.6 EndY=1.7 EndZ=0
    g1: LineSegment StartX=-3.5 StartY=4.7 StartZ=0 EndX=-1.6 EndY=4.7 EndZ=0
    g2: LineSegment StartX=-1.6 StartY=1.7 StartZ=0 EndX=-1.6 EndY=1.5 EndZ=0
    g3: LineSegment StartX=-1.6 StartY=1.5 StartZ=0 EndX=-5.2 EndY=1.5 EndZ=0
    g4: Circle CenterX=-3.5 CenterY=4.7 CenterZ=0 NormalX=0 NormalY=0 NormalZ=1 AngleXU=0 Radius=1
    g5: Circle CenterX=-3.59627 CenterY=2.99743 CenterZ=0 NormalX=0 NormalY=0 NormalZ=1 AngleXU=0 Radius=1
    g6: Circle CenterX=-5.2 CenterY=1.5 CenterZ=0 NormalX=0 NormalY=0 NormalZ=1 AngleXU=0 Radius=1
    g7: BSplineCurve PolesCount=3 KnotsCount=2 Degree=2 IsPeriodic=0
    g8: GeomPoint X=-3.5 Y=4.7 Z=0
    g9: GeomPoint X=-5.2 Y=1.5 Z=0
  constraints (23):
    c: Vertical(g0)
    c: Distance(g0) = 3
    c: Coincident(g1,g0)
    c: Horizontal(g1)
    c: Block(g0)
    c: Block(g1)
    c: Coincident(g2,g0)
    c: Vertical(g2)
    c: Distance(g2) = 0.2
    c: Coincident(g3,g2)
    c: Horizontal(g3)
    c: Block(g3)
    c: Coincident(g7,g1)
    c: Weight(g4) = 1
    c: Equal(g4,g5)
    c: Equal(g4,g6)
    c: Coincident(g7,g3)
    c: InternalAlignment(g4,g7)
    c: InternalAlignment(g5,g7)
    c: InternalAlignment(g6,g7)
    c: InternalAlignment(g8,g7)
    c: InternalAlignment(g9,g7)
    c: Block(g7)
FEATURE [Sketcher::SketchObject] Sketch028
  FullyConstrained = true
  sketch-geometry (18):
    g0: LineSegment StartX=0 StartY=3e-16 StartZ=0 EndX=0 EndY=1.7 EndZ=0
    g1: LineSegment StartX=-3.5 StartY=0 StartZ=0 EndX=-3.5 EndY=0.9 EndZ=0
    g2: Circle CenterX=-2.7 CenterY=1.7 CenterZ=0 NormalX=0 NormalY=0 NormalZ=1 AngleXU=0 Radius=1
    g3: Circle CenterX=-3.5 CenterY=1.7 CenterZ=0 NormalX=0 NormalY=0 NormalZ=1 AngleXU=0 Radius=1
    g4: Circle CenterX=-3.5 CenterY=0.9 CenterZ=0 NormalX=0 NormalY=0 NormalZ=1 AngleXU=0 Radius=1
    g5: BSplineCurve PolesCount=3 KnotsCount=2 Degree=2 IsPeriodic=0
    g6: GeomPoint X=-2.7 Y=1.7 Z=0
    g7: GeomPoint X=-3.5 Y=0.9 Z=0
    g8: LineSegment StartX=-3.5 StartY=0 StartZ=0 EndX=-3.5 EndY=-7 EndZ=0
    g9: LineSegment StartX=0 StartY=3e-16 StartZ=0 EndX=0 EndY=-7 EndZ=0
    g10: LineSegment StartX=-3.5 StartY=-7 StartZ=0 EndX=0 EndY=-7 EndZ=0
    g11: LineSegment StartX=-2.7 StartY=1.7 StartZ=0 EndX=-1.6 EndY=1.7 EndZ=0
    g12: LineSegment StartX=0 StartY=1.7 StartZ=0 EndX=0 EndY=4.5 EndZ=0
    g13: LineSegment StartX=0 StartY=4.5 StartZ=0 EndX=0 EndY=10.8 EndZ=0
    g14: LineSegment StartX=0 StartY=10.8 StartZ=0 EndX=-2 EndY=10.8 EndZ=0
    g15: LineSegment StartX=-1.6 StartY=4.7 StartZ=0 EndX=-1.6 EndY=1.7 EndZ=0
    g16: LineSegment StartX=-1.6 StartY=4.7 StartZ=0 EndX=-2 EndY=4.7 EndZ=0
    g17: LineSegment StartX=-2 StartY=4.7 StartZ=0 EndX=-2 EndY=10.8 EndZ=0
  constraints (44):
    c: Vertical(g0)
    c: Vertical(g1)
    c: Distance(g1) = 0.9
    c: Block(g0)
    c: Distance(g0) = 1.7
    c: Weight(g2) = 1
    c: Equal(g2,g3)
    c: Equal(g2,g4)
    c: Coincident(g5,g1)
    c: InternalAlignment(g2,g5)
    c: InternalAlignment(g3,g5)
    c: InternalAlignment(g4,g5)
    c: InternalAlignment(g6,g5)
    c: InternalAlignment(g7,g5)
    c: Block(g5)
    c: Coincident(g8,g1)
    c: Vertical(g8)
    c: Distance(g8) = 7
    c: Vertical(g9)
    c: Equal(g8,g9) = 7
    c: Coincident(g9,g0)
    c: Coincident(g10,g8)
    c: Coincident(g10,g9)
    c: Horizontal(g10)
    c: Coincident(g11,g5)
    c: Horizontal(g11)
    c: Coincident(g12,g0)
    c: Vertical(g12)
    c: Distance(g12) = 2.8
    c: Coincident(g13,g12)
    c: Vertical(g13)
    c: Distance(g13) = 6.3
    c: Coincident(g14,g13)
    c: Horizontal(g14)
    c: Distance(g14) = 2
    c: Vertical(g15)
    c: Distance(g15) = 3
    c: Block(g11)
    c: Coincident(g15,g11)
    c: Coincident(g16,g15)
    c: Horizontal(g16)
    c: Coincident(g17,g16)
    c: Coincident(g17,g14)
    c: Vertical(g17)
FEATURE [Part::Revolution] Revolve040  label="backCaseScrewRetainer001"
  Angle = 360
  Axis = (0,1,0)
  Base = (0,0,0)
  FaceMakerClass = Part::FaceMakerBullseye
  Placement = pos=(12.5,3,10) rot=(0,0,1;0rad)
  Solid = false
  Source = -> Face036
  Symmetric = false
FEATURE [Part::Feature] Face055
  shape: bbox 3.5 x 30.2 x 2e-07 mm, 1 faces, 0 solids (baked)
FEATURE [Part::Revolution] Revolve059  label="backCaseScrewPost"
  Angle = 360
  Axis = (0,1,0)
  Base = (0,0,0)
  FaceMakerClass = Part::FaceMakerBullseye
  Placement = pos=(12.5,4.5,10) rot=(0,0,1;0rad)
  Solid = false
  Source = -> Face055
  Symmetric = false
FEATURE [Part::Feature] Face056
  shape: bbox 3.5 x 30.2 x 2e-07 mm, 1 faces, 0 solids (baked)
FEATURE [Part::Revolution] Revolve060  label="backCaseScrewPost001"
  Angle = 360
  Axis = (0,1,0)
  Base = (0,0,0)
  FaceMakerClass = Part::FaceMakerBullseye
  Placement = pos=(12.5,4.5,62) rot=(0,0,1;0rad)
  Solid = false
  Source = -> Face056
  Symmetric = false
FEATURE [Part::Feature] Face057
  shape: bbox 3.5 x 17.8 x 2e-07 mm, 1 faces, 0 solids (baked)
FEATURE [Part::Revolution] Revolve061  label="removeToCreateScrewAndThreadedInsertHole"
  Angle = 360
  Axis = (0,1,0)
  Base = (0,0,0)
  FaceMakerClass = Part::FaceMakerBullseye
  Placement = pos=(12.5,0,10) rot=(0,0,1;0rad)
  Solid = false
  Source = -> Face057
  Symmetric = false
FEATURE [Part::Feature] Face058
  shape: bbox 3.5 x 17.8 x 2e-07 mm, 1 faces, 0 solids (baked)
FEATURE [Part::Revolution] Revolve062  label="removeToCreateScrewAndThreadedInsertHole001"
  Angle = 360
  Axis = (0,1,0)
  Base = (0,0,0)
  FaceMakerClass = Part::FaceMakerBullseye
  Placement = pos=(12.5,0,62) rot=(0,0,1;0rad)
  Solid = false
  Source = -> Face058
  Symmetric = false
FEATURE [Part::Feature] Face059
  shape: bbox 3.5 x 17.8 x 2e-07 mm, 1 faces, 0 solids (baked)
FEATURE [Part::Revolution] Revolve063  label="removeToCreateScrewAndThreadedInsertHole002"
  Angle = 360
  Axis = (0,1,0)
  Base = (0,0,0)
  FaceMakerClass = Part::FaceMakerBullseye
  Placement = pos=(89.5,0,68.5) rot=(0,0,1;0rad)
  Solid = false
  Source = -> Face059
  Symmetric = false
FEATURE [Part::Feature] Face060
  shape: bbox 3.5 x 17.8 x 2e-07 mm, 1 faces, 0 solids (baked)
FEATURE [Part::Revolution] Revolve064  label="removeToCreateScrewAndThreadedInsertHole003"
  Angle = 360
  Axis = (0,1,0)
  Base = (0,0,0)
  FaceMakerClass = Part::FaceMakerBullseye
  Placement = pos=(89.5,0,3.5) rot=(0,0,1;0rad)
  Solid = false
  Source = -> Face060
  Symmetric = false
FEATURE [Part::Feature] Face061
  shape: bbox 3.5 x 17.8 x 2e-07 mm, 1 faces, 0 solids (baked)
FEATURE [Part::Revolution] Revolve065  label="removeToCreateScrewAndThreadedInsertHole004"
  Angle = 360
  Axis = (0,1,0)
  Base = (0,0,0)
  FaceMakerClass = Part::FaceMakerBullseye
  Placement = pos=(102.5,4.7,3.5) rot=(0,0,1;0rad)
  Solid = false
  Source = -> Face061
  Symmetric = false
FEATURE [Part::Feature] Face062
  shape: bbox 3.5 x 17.8 x 2e-07 mm, 1 faces, 0 solids (baked)
FEATURE [Part::Revolution] Revolve066  label="removeToCreateScrewAndThreadedInsertHole005"
  Angle = 360
  Axis = (0,1,0)
  Base = (0,0,0)
  FaceMakerClass = Part::FaceMakerBullseye
  Placement = pos=(102.5,4.7,68.5) rot=(0,0,1;0rad)
  Solid = false
  Source = -> Face062
  Symmetric = false
FEATURE [Part::MultiFuse] Fusion047  label="makeHoles"
  Shapes = -> [Revolve066,Revolve065,Revolve064,Revolve063,Revolve062,Revolve061]
FEATURE [Part::Feature] Face063
  shape: bbox 3.6 x 3.2 x 2e-07 mm, 1 faces, 0 solids (baked)
FEATURE [Part::Revolution] Revolve067  label="moreFrontCaseScrewRetainer002"
  Angle = 360
  Axis = (0,1,0)
  Base = (0,0,0)
  FaceMakerClass = Part::FaceMakerBullseye
  Placement = pos=(102.5,4.5,68.5) rot=(0,0,1;0rad)
  Solid = false
  Source = -> Face063
  Symmetric = false
FEATURE [Part::Feature] Face064
  shape: bbox 3.6 x 3.2 x 2e-07 mm, 1 faces, 0 solids (baked)
FEATURE [Part::Revolution] Revolve068  label="moreFrontCaseScrewRetainer003"
  Angle = 360
  Axis = (0,1,0)
  Base = (0,0,0)
  FaceMakerClass = Part::FaceMakerBullseye
  Placement = pos=(102.5,4.5,3.5) rot=(0,0,1;0rad)
  Solid = false
  Source = -> Face064
  Symmetric = false
FEATURE [Part::Feature] Face065
  shape: bbox 3.5 x 17.8 x 2e-07 mm, 1 faces, 0 solids (baked)
FEATURE [Part::Revolution] Revolve069  label="removeToCreateScrewAndThreadedInsertHole006"
  Angle = 360
  Axis = (0,1,0)
  Base = (0,0,0)
  FaceMakerClass = Part::FaceMakerBullseye
  Placement = pos=(12.5,0,10) rot=(0,0,1;0rad)
  Solid = false
  Source = -> Face065
  Symmetric = false
FEATURE [Part::Feature] Face066
  shape: bbox 3.5 x 17.8 x 2e-07 mm, 1 faces, 0 solids (baked)
FEATURE [Part::Revolution] Revolve070  label="removeToCreateScrewAndThreadedInsertHole007"
  Angle = 360
  Axis = (0,1,0)
  Base = (0,0,0)
  FaceMakerClass = Part::FaceMakerBullseye
  Placement = pos=(12.5,0,62) rot=(0,0,1;0rad)
  Solid = false
  Source = -> Face066
  Symmetric = false
FEATURE [Part::Feature] Face067
  shape: bbox 3.5 x 17.8 x 2e-07 mm, 1 faces, 0 solids (baked)
FEATURE [Part::Revolution] Revolve071  label="removeToCreateScrewAndThreadedInsertHole008"
  Angle = 360
  Axis = (0,1,0)
  Base = (0,0,0)
  FaceMakerClass = Part::FaceMakerBullseye
  Placement = pos=(89.5,0,68.5) rot=(0,0,1;0rad)
  Solid = false
  Source = -> Face067
  Symmetric = false
FEATURE [Part::Feature] Face068
  shape: bbox 3.5 x 17.8 x 2e-07 mm, 1 faces, 0 solids (baked)
FEATURE [Part::Revolution] Revolve072  label="removeToCreateScrewAndThreadedInsertHole009"
  Angle = 360
  Axis = (0,1,0)
  Base = (0,0,0)
  FaceMakerClass = Part::FaceMakerBullseye
  Placement = pos=(89.5,0,3.5) rot=(0,0,1;0rad)
  Solid = false
  Source = -> Face068
  Symmetric = false
FEATURE [Part::Feature] Face069
  shape: bbox 3.5 x 17.8 x 2e-07 mm, 1 faces, 0 solids (baked)
FEATURE [Part::Feature] Face070
  shape: bbox 3.5 x 17.8 x 2e-07 mm, 1 faces, 0 solids (baked)
FEATURE [Part::Revolution] Revolve073  label="removeToCreateScrewAndThreadedInsertHole010"
  Angle = 360
  Axis = (0,1,0)
  Base = (0,0,0)
  FaceMakerClass = Part::FaceMakerBullseye
  Placement = pos=(102.5,4.7,3.5) rot=(0,0,1;0rad)
  Solid = false
  Source = -> Face069
  Symmetric = false
FEATURE [Part::Revolution] Revolve074  label="removeToCreateScrewAndThreadedInsertHole011"
  Angle = 360
  Axis = (0,1,0)
  Base = (0,0,0)
  FaceMakerClass = Part::FaceMakerBullseye
  Placement = pos=(102.5,4.7,68.5) rot=(0,0,1;0rad)
  Solid = false
  Source = -> Face070
  Symmetric = false
FEATURE [Part::MultiFuse] Fusion048  label="makeHoles001"
  Shapes = -> [Revolve074,Revolve073,Revolve072,Revolve071,Revolve070,Revolve069]
FEATURE [Part::MultiFuse] Fusion049  label="caseScrewRetainers"
  Shapes = -> [Revolve067,Revolve068,Revolve048,Revolve047,Revolve039,Revolve040]
FEATURE [Part::Cut] Cut015  label="caseScrewRetainers001"
  Base = -> Fusion049
  Tool = -> Fusion048
FEATURE [Part::MultiFuse] Fusion050  label="casePillars"
  Shapes = -> [Revolve055,Revolve054,Revolve043,Revolve046,Revolve059,Revolve060]
FEATURE [Part::Feature] Face071 .. Face076  x6 (patterned run collapsed; names and placements below)
  shape: bbox 3.5 x 17.8 x 2e-07 mm, 1 faces, 0 solids (baked)
FEATURE [Part::Revolution] Revolve075  label="removeToCreateScrewAndThreadedInsertHole012"
  Angle = 360
  Axis = (0,1,0)
  Base = (0,0,0)
  FaceMakerClass = Part::FaceMakerBullseye
  Placement = pos=(12.5,0,10) rot=(0,0,1;0rad)
  Solid = false
  Source = -> Face071
  Symmetric = false
FEATURE [Part::Revolution] Revolve076  label="removeToCreateScrewAndThreadedInsertHole013"
  Angle = 360
  Axis = (0,1,0)
  Base = (0,0,0)
  FaceMakerClass = Part::FaceMakerBullseye
  Placement = pos=(12.5,0,62) rot=(0,0,1;0rad)
  Solid = false
  Source = -> Face072
  Symmetric = false
FEATURE [Part::Revolution] Revolve077  label="removeToCreateScrewAndThreadedInsertHole014"
  Angle = 360
  Axis = (0,1,0)
  Base = (0,0,0)
  FaceMakerClass = Part::FaceMakerBullseye
  Placement = pos=(89.5,0,68.5) rot=(0,0,1;0rad)
  Solid = false
  Source = -> Face073
  Symmetric = false
FEATURE [Part::Revolution] Revolve078  label="removeToCreateScrewAndThreadedInsertHole015"
  Angle = 360
  Axis = (0,1,0)
  Base = (0,0,0)
  FaceMakerClass = Part::FaceMakerBullseye
  Placement = pos=(89.5,0,3.5) rot=(0,0,1;0rad)
  Solid = false
  Source = -> Face074
  Symmetric = false
FEATURE [Part::Revolution] Revolve079  label="removeToCreateScrewAndThreadedInsertHole016"
  Angle = 360
  Axis = (0,1,0)
  Base = (0,0,0)
  FaceMakerClass = Part::FaceMakerBullseye
  Placement = pos=(102.5,4.7,3.5) rot=(0,0,1;0rad)
  Solid = false
  Source = -> Face075
  Symmetric = false
FEATURE [Part::Revolution] Revolve080  label="removeToCreateScrewAndThreadedInsertHole017"
  Angle = 360
  Axis = (0,1,0)
  Base = (0,0,0)
  FaceMakerClass = Part::FaceMakerBullseye
  Placement = pos=(102.5,4.7,68.5) rot=(0,0,1;0rad)
  Solid = false
  Source = -> Face076
  Symmetric = false
FEATURE [Part::MultiFuse] Fusion051  label="makeHoles002"
  Shapes = -> [Revolve080,Revolve079,Revolve078,Revolve077,Revolve076,Revolve075]
FEATURE [Part::Cut] Cut016  label="caesPillars"
  Base = -> Fusion050
  Tool = -> Fusion051
FEATURE [Part::Revolution] Revolve009  label="plugHousing016"
  Angle = 360
  Axis = (0,1,0)
  Base = (0,0,0)
  FaceMakerClass = Part::FaceMakerBullseye
  Placement = pos=(0,0,36.15) rot=(0,0,1;0rad)
  Solid = false
  Source = -> Face012
  Symmetric = false
FEATURE [Part::MultiFuse] Fusion014  label="plugHousing023"
  Placement = pos=(0,0,0) rot=(0,0,1;1.5708rad)
  Shapes = -> [Revolve011,Revolve009]
FEATURE [Part::Revolution] Revolve010  label="plugHousing017"
  Angle = 360
  Axis = (0,1,0)
  Base = (0,0,0)
  FaceMakerClass = Part::FaceMakerBullseye
  Placement = pos=(0,0,36.15) rot=(0,0,1;0rad)
  Solid = false
  Source = -> Face014
  Symmetric = false
FEATURE [Part::MultiFuse] Fusion015  label="plugHousing024"
  Placement = pos=(0,0,0) rot=(0,0,1;1.5708rad)
  Shapes = -> [Revolve010,Revolve015]
FEATURE [Part::Revolution] Revolve014  label="plugHousing026"
  Angle = 360
  Axis = (0,1,0)
  Base = (0,0,0)
  FaceMakerClass = Part::FaceMakerBullseye
  Placement = pos=(0,0,36.15) rot=(0,0,1;0rad)
  Solid = false
  Source = -> Face011
  Symmetric = false
FEATURE [Part::Revolution] Revolve013  label="plugHousing025"
  Angle = 360
  Axis = (0,1,0)
  Base = (0,0,0)
  FaceMakerClass = Part::FaceMakerBullseye
  Placement = pos=(0,0,36.15) rot=(0,0,1;0rad)
  Solid = false
  Source = -> Face015
  Symmetric = false
FEATURE [Part::MultiFuse] Fusion016  label="plugHousing028"
  Placement = pos=(0,19,0) rot=(0,0,1;3.14159rad)
  Shapes = -> [Fusion014,Fusion013]
FEATURE [Part::MultiFuse] Fusion011  label="plugHousing018"
  Placement = pos=(0,0,0) rot=(0,0,1;1.5708rad)
  Shapes = -> [Revolve014,Revolve013]
FEATURE [Part::MultiFuse] Fusion012  label="plugHousing019"
  Placement = pos=(0,19,0) rot=(0,0,1;3.14159rad)
  Shapes = -> [Fusion011,Fusion015]
FEATURE [Part::MultiFuse] Fusion017  label="plugHousing029"
  Placement = pos=(122.621,0,-0.15) rot=(0,0,1;0rad)
  Shapes = -> [Fusion016,Fusion012]
FEATURE [Part::MultiFuse] Fusion052  label="casePillarRetainers"
  Shapes = -> [Extrude012,Extrude013,Extrude014,Extrude015,Extrude016,Extrude017,Extrude018,Extrude019,Box011,Box012]
FEATURE [Part::Feature] Face077
  shape: bbox 3.5 x 17.8 x 2e-07 mm, 1 faces, 0 solids (baked)
FEATURE [Part::Revolution] Revolve081  label="removeToCreateScrewAndThreadedInsertHole018"
  Angle = 360
  Axis = (0,1,0)
  Base = (0,0,0)
  FaceMakerClass = Part::FaceMakerBullseye
  Placement = pos=(62.3,30.3,19.7) rot=(0,0,1;0rad)
  Solid = false
  Source = -> Face077
  Symmetric = false
FEATURE [Part::Feature] Face078
  shape: bbox 3.5 x 17.8 x 2e-07 mm, 1 faces, 0 solids (baked)
FEATURE [Part::Revolution] Revolve082  label="removeToCreateScrewAndThreadedInsertHole019"
  Angle = 360
  Axis = (0,1,0)
  Base = (0,0,0)
  FaceMakerClass = Part::FaceMakerBullseye
  Placement = pos=(62.3,30.3,51.7) rot=(0,0,1;0rad)
  Solid = false
  Source = -> Face078
  Symmetric = false
FEATURE [Part::Feature] Face079
  shape: bbox 3.5 x 17.8 x 2e-07 mm, 1 faces, 0 solids (baked)
FEATURE [Part::Revolution] Revolve083  label="removeToCreateScrewAndThreadedInsertHole020"
  Angle = 360
  Axis = (0,1,0)
  Base = (0,0,0)
  FaceMakerClass = Part::FaceMakerBullseye
  Placement = pos=(30.3,30.3,19.7) rot=(0,0,1;0rad)
  Solid = false
  Source = -> Face079
  Symmetric = false
FEATURE [Part::Feature] Face080
  shape: bbox 3.5 x 17.8 x 2e-07 mm, 1 faces, 0 solids (baked)
FEATURE [Part::Revolution] Revolve084  label="removeToCreateScrewAndThreadedInsertHole021"
  Angle = 360
  Axis = (0,1,0)
  Base = (0,0,0)
  FaceMakerClass = Part::FaceMakerBullseye
  Placement = pos=(30.3,30.3,51.7) rot=(0,0,1;0rad)
  Solid = false
  Source = -> Face080
  Symmetric = false
FEATURE [Part::MultiFuse] Fusion053  label="createThreadedInsertHolesForFan"
  Shapes = -> [Revolve081,Revolve082,Revolve083,Revolve084]
FEATURE [Part::Cut] Cut017  label="fanScrewHousing001"
  Base = -> Fusion046
  Tool = -> Fusion053
FEATURE [Part::Feature] Face081
  shape: bbox 3.5 x 17.8 x 2e-07 mm, 1 faces, 0 solids (baked)
FEATURE [Part::Revolution] Revolve085  label="removeToCreateScrewAndThreadedInsertHole022"
  Angle = 360
  Axis = (0,1,0)
  Base = (0,0,0)
  FaceMakerClass = Part::FaceMakerBullseye
  Placement = pos=(62.3,30.3,19.7) rot=(0,0,1;0rad)
  Solid = false
  Source = -> Face081
  Symmetric = false
FEATURE [Part::Feature] Face082
  shape: bbox 3.5 x 17.8 x 2e-07 mm, 1 faces, 0 solids (baked)
FEATURE [Part::Revolution] Revolve086  label="removeToCreateScrewAndThreadedInsertHole023"
  Angle = 360
  Axis = (0,1,0)
  Base = (0,0,0)
  FaceMakerClass = Part::FaceMakerBullseye
  Placement = pos=(62.3,30.3,51.7) rot=(0,0,1;0rad)
  Solid = false
  Source = -> Face082
  Symmetric = false
FEATURE [Part::Feature] Face083
  shape: bbox 3.5 x 17.8 x 2e-07 mm, 1 faces, 0 solids (baked)
FEATURE [Part::Revolution] Revolve087  label="removeToCreateScrewAndThreadedInsertHole024"
  Angle = 360
  Axis = (0,1,0)
  Base = (0,0,0)
  FaceMakerClass = Part::FaceMakerBullseye
  Placement = pos=(30.3,30.3,19.7) rot=(0,0,1;0rad)
  Solid = false
  Source = -> Face083
  Symmetric = false
FEATURE [Part::Feature] Face084
  shape: bbox 3.5 x 17.8 x 2e-07 mm, 1 faces, 0 solids (baked)
FEATURE [Part::Revolution] Revolve088  label="removeToCreateScrewAndThreadedInsertHole025"
  Angle = 360
  Axis = (0,1,0)
  Base = (0,0,0)
  FaceMakerClass = Part::FaceMakerBullseye
  Placement = pos=(30.3,30.3,51.7) rot=(0,0,1;0rad)
  Solid = false
  Source = -> Face084
  Symmetric = false
FEATURE [Part::MultiFuse] Fusion054  label="createThreadedInsertHolesForFan001"
  Shapes = -> [Revolve085,Revolve086,Revolve087,Revolve088]
FEATURE [Part::Cut] Cut018  label="top007"
  Base = -> Fusion040
  Tool = -> Fusion054
FEATURE [Sketcher::SketchObject] Sketch029
  FullyConstrained = false
  Placement = pos=(0,0,0) rot=(1,0,0;1.5708rad)
  sketch-geometry (24):
    g0: ArcOfCircle CenterX=-4 CenterY=-10.5 CenterZ=0 NormalX=0 NormalY=0 NormalZ=1 AngleXU=0 Radius=1.5 StartAngle=6e-16 EndAngle=3.14159
    g1: ArcOfCircle CenterX=-34.2 CenterY=-10.5 CenterZ=0 NormalX=0 NormalY=0 NormalZ=1 AngleXU=0 Radius=1.5 StartAngle=0 EndAngle=3.14159
    g2: ArcOfCircle CenterX=-34.2 CenterY=-27.7 CenterZ=0 NormalX=0 NormalY=0 NormalZ=1 AngleXU=0 Radius=1.5 StartAngle=3.14159 EndAngle=6.28319
    g3: ArcOfCircle CenterX=-4 CenterY=-27.7 CenterZ=0 NormalX=0 NormalY=0 NormalZ=1 AngleXU=0 Radius=1.5 StartAngle=3.1416 EndAngle=6.28319
    g4: ArcOfCircle CenterX=-10 CenterY=-4.3 CenterZ=0 NormalX=0 NormalY=0 NormalZ=1 AngleXU=0 Radius=1.5 StartAngle=2e-16 EndAngle=3.14159
    g5: ArcOfCircle CenterX=-16.1 CenterY=-1.8 CenterZ=0 NormalX=0 NormalY=0 NormalZ=1 AngleXU=0 Radius=1.5 StartAngle=5e-16 EndAngle=3.14159
    g6: ArcOfCircle CenterX=-22.1 CenterY=-1.8 CenterZ=0 NormalX=0 NormalY=0 NormalZ=1 AngleXU=0 Radius=1.5 StartAngle=5e-16 EndAngle=3.14159
    g7: ArcOfCircle CenterX=-28.2 CenterY=-4.3 CenterZ=0 NormalX=0 NormalY=0 NormalZ=1 AngleXU=0 Radius=1.5 StartAngle=2e-16 EndAngle=3.14159
    g8: ArcOfCircle CenterX=-10 CenterY=-33.9 CenterZ=0 NormalX=0 NormalY=0 NormalZ=1 AngleXU=0 Radius=1.5 StartAngle=3.14159 EndAngle=6.28319
    g9: ArcOfCircle CenterX=-16.1 CenterY=-36.4 CenterZ=0 NormalX=0 NormalY=0 NormalZ=1 AngleXU=0 Radius=1.5 StartAngle=3.14159 EndAngle=6.28319
    g10: ArcOfCircle CenterX=-22.1 CenterY=-36.4 CenterZ=0 NormalX=0 NormalY=0 NormalZ=1 AngleXU=0 Radius=1.5 StartAngle=3.14159 EndAngle=6.28319
    g11: ArcOfCircle CenterX=-28.2 CenterY=-33.9 CenterZ=0 NormalX=0 NormalY=0 NormalZ=1 AngleXU=0 Radius=1.5 StartAngle=3.14159 EndAngle=6.28319
    g12: LineSegment StartX=-35.7 StartY=-10.5 StartZ=0 EndX=-35.7 EndY=-27.7 EndZ=0
    g13: LineSegment StartX=-32.7 StartY=-10.5 StartZ=0 EndX=-32.7 EndY=-27.7 EndZ=0
    g14: LineSegment StartX=-29.7 StartY=-33.9 StartZ=0 EndX=-29.7 EndY=-4.3 EndZ=0
    g15: LineSegment StartX=-26.7 StartY=-33.9 StartZ=0 EndX=-26.7 EndY=-4.3 EndZ=0
    g16: LineSegment StartX=-2.5 StartY=-10.5 StartZ=0 EndX=-2.5 EndY=-27.7 EndZ=0
    g17: LineSegment StartX=-8.5 StartY=-4.3 StartZ=0 EndX=-8.5 EndY=-33.9 EndZ=0
    g18: LineSegment StartX=-5.5 StartY=-10.5 StartZ=0 EndX=-5.5 EndY=-27.7 EndZ=0
    g19: LineSegment StartX=-11.5 StartY=-4.3 StartZ=0 EndX=-11.5 EndY=-33.9 EndZ=0
    g20: LineSegment StartX=-14.6 StartY=-1.8 StartZ=0 EndX=-14.6 EndY=-36.4 EndZ=0
    g21: LineSegment StartX=-17.6 StartY=-1.8 StartZ=0 EndX=-17.6 EndY=-36.4 EndZ=0
    g22: LineSegment StartX=-20.6 StartY=-36.4 StartZ=0 EndX=-20.6 EndY=-1.8 EndZ=0
    g23: LineSegment StartX=-23.6 StartY=-1.8 StartZ=0 EndX=-23.6 EndY=-36.4 EndZ=0
  constraints (48):
    c: Block(g0)
    c: Block(g1)
    c: Block(g2)
    c: Block(g3)
    c: Block(g4)
    c: Block(g5)
    c: Block(g6)
    c: Block(g7)
    c: Block(g8)
    c: Block(g9)
    c: Block(g10)
    c: Block(g11)
    c: Coincident(g12,g1)
    c: Coincident(g12,g2)
    c: Vertical(g12)
    c: Coincident(g13,g1)
    c: Coincident(g13,g2)
    c: Vertical(g13)
    c: Coincident(g14,g11)
    c: Coincident(g14,g7)
    c: Vertical(g14)
    c: Coincident(g15,g11)
    c: Coincident(g15,g7)
    c: Vertical(g15)
    c: Coincident(g16,g0)
    c: Coincident(g16,g3)
    c: Vertical(g16)
    c: Coincident(g17,g4)
    c: Coincident(g17,g8)
    c: Vertical(g17)
    c: Coincident(g18,g0)
    c: Coincident(g18,g3)
    c: Vertical(g18)
    c: Coincident(g19,g4)
    c: Coincident(g19,g8)
    c: Vertical(g19)
    c: Coincident(g20,g5)
    c: Coincident(g20,g9)
    c: Vertical(g20)
    c: Coincident(g21,g5)
    c: Coincident(g21,g9)
    c: Vertical(g21)
    c: Coincident(g22,g10)
    c: Coincident(g22,g6)
    c: Vertical(g22)
    c: Coincident(g23,g6)
    c: Coincident(g23,g10)
    c: Vertical(g23)
FEATURE [Part::Extrusion] Extrude020  label="removeToCreateFanGrillHoles"
  Base = -> Sketch029
  Dir = (0,-1,6e-16)
  DirMode = 2
  FaceMakerClass = Part::FaceMakerBullseye
  LengthFwd = 10
  LengthRev = 0
  Placement = pos=(65.4,44,54.82) rot=(0,0,1;0rad)
  Solid = true
  Symmetric = false
FEATURE [Part::MultiFuse] Fusion055  label="top008"
  Shapes = -> [Cut017,Cut018]
FEATURE [Part::Cut] Cut019  label="top009"
  Base = -> Fusion055
  Tool = -> Extrude020
FEATURE [App::MeasureDistance] Distance003  label="Distance: 71.95 mm"
  Distance = 71.9513
  P1 = (117,38,72)
  P2 = (117,38,0.0487319)
FEATURE [Sketcher::SketchObject] Sketch030
  FullyConstrained = true
  Placement = pos=(117,19,0) rot=(0.57735,0.57735,0.57735;2.0944rad)
  sketch-geometry (48):
    g0: LineSegment StartX=-49.19 StartY=69.25 StartZ=0 EndX=-49.19 EndY=66.25 EndZ=0
    g1: LineSegment StartX=-49.19 StartY=63.5 StartZ=0 EndX=-49.19 EndY=60.5 EndZ=0
    g2: LineSegment StartX=-49.19 StartY=57.75 StartZ=0 EndX=-49.19 EndY=54.75 EndZ=0
    g3: LineSegment StartX=-49.19 StartY=52 StartZ=0 EndX=-49.19 EndY=49 EndZ=0
    g4: LineSegment StartX=-49.19 StartY=46.25 StartZ=0 EndX=-49.19 EndY=43.25 EndZ=0
    g5: LineSegment StartX=-49.19 StartY=40.5 StartZ=0 EndX=-49.19 EndY=37.5 EndZ=0
    g6: LineSegment StartX=-49.19 StartY=34.5 StartZ=0 EndX=-49.19 EndY=31.5 EndZ=0
    g7: LineSegment StartX=-49.19 StartY=28.75 StartZ=0 EndX=-49.19 EndY=25.75 EndZ=0
    g8: LineSegment StartX=-49.19 StartY=23 StartZ=0 EndX=-49.19 EndY=20 EndZ=0
    g9: LineSegment StartX=-49.19 StartY=17.25 StartZ=0 EndX=-49.19 EndY=14.25 EndZ=0
    g10: LineSegment StartX=-49.19 StartY=11.5 StartZ=0 EndX=-49.19 EndY=8.5 EndZ=0
    g11: LineSegment StartX=-49.19 StartY=5.75 StartZ=0 EndX=-49.19 EndY=2.75 EndZ=0
    g12: ArcOfCircle CenterX=-1.5 CenterY=67.75 CenterZ=0 NormalX=0 NormalY=0 NormalZ=1 AngleXU=0 Radius=1.5 StartAngle=4.71239 EndAngle=7.85398
    g13: ArcOfCircle CenterX=-1.5 CenterY=62 CenterZ=0 NormalX=0 NormalY=0 NormalZ=1 AngleXU=0 Radius=1.5 StartAngle=4.71239 EndAngle=7.85398
    g14: ArcOfCircle CenterX=-1.5 CenterY=56.25 CenterZ=0 NormalX=0 NormalY=0 NormalZ=1 AngleXU=0 Radius=1.5 StartAngle=4.71239 EndAngle=7.85398
    g15: ArcOfCircle CenterX=-11.49 CenterY=50.5 CenterZ=0 NormalX=0 NormalY=0 NormalZ=1 AngleXU=0 Radius=1.5 StartAngle=4.71239 EndAngle=7.85398
    g16: ArcOfCircle CenterX=-16.28 CenterY=44.75 CenterZ=0 NormalX=0 NormalY=0 NormalZ=1 AngleXU=0 Radius=1.5 StartAngle=4.71239 EndAngle=7.85398
    g17: ArcOfCircle CenterX=-18.2337 CenterY=39 CenterZ=0 NormalX=0 NormalY=0 NormalZ=1 AngleXU=0 Radius=1.5 StartAngle=4.71485 EndAngle=7.85398
    g18: ArcOfCircle CenterX=-16.2837 CenterY=27.25 CenterZ=0 NormalX=0 NormalY=0 NormalZ=1 AngleXU=0 Radius=1.5 StartAngle=4.71485 EndAngle=7.85398
    g19: ArcOfCircle CenterX=-18.2337 CenterY=33 CenterZ=0 NormalX=0 NormalY=0 NormalZ=1 AngleXU=0 Radius=1.5 StartAngle=4.71485 EndAngle=7.85398
    g20: ArcOfCircle CenterX=-11.49 CenterY=21.5 CenterZ=0 NormalX=0 NormalY=0 NormalZ=1 AngleXU=0 Radius=1.5 StartAngle=4.71239 EndAngle=7.85398
    g21: ArcOfCircle CenterX=-1.5 CenterY=4.25 CenterZ=0 NormalX=0 NormalY=0 NormalZ=1 AngleXU=0 Radius=1.5 StartAngle=4.71239 EndAngle=7.85398
    g22: ArcOfCircle CenterX=-1.5 CenterY=10 CenterZ=0 NormalX=0 NormalY=0 NormalZ=1 AngleXU=0 Radius=1.5 StartAngle=4.71239 EndAngle=7.85398
    g23: ArcOfCircle CenterX=-1.5 CenterY=15.75 CenterZ=0 NormalX=0 NormalY=0 NormalZ=1 AngleXU=0 Radius=1.5 StartAngle=4.71239 EndAngle=7.85398
    g24: LineSegment StartX=-49.19 StartY=69.25 StartZ=0 EndX=-1.5 EndY=69.25 EndZ=0
    g25: LineSegment StartX=-49.19 StartY=66.25 StartZ=0 EndX=-1.5 EndY=66.25 EndZ=0
    g26: LineSegment StartX=-49.19 StartY=63.5 StartZ=0 EndX=-1.5 EndY=63.5 EndZ=0
    g27: LineSegment StartX=-49.19 StartY=60.5 StartZ=0 EndX=-1.5 EndY=60.5 EndZ=0
    g28: LineSegment StartX=-49.19 StartY=57.75 StartZ=0 EndX=-1.5 EndY=57.75 EndZ=0
    g29: LineSegment StartX=-49.19 StartY=54.75 StartZ=0 EndX=-1.5 EndY=54.75 EndZ=0
    g30: LineSegment StartX=-49.19 StartY=52 StartZ=0 EndX=-11.49 EndY=52 EndZ=0
    g31: LineSegment StartX=-49.19 StartY=49 StartZ=0 EndX=-11.49 EndY=49 EndZ=0
    g32: LineSegment StartX=-49.19 StartY=46.25 StartZ=0 EndX=-16.28 EndY=46.25 EndZ=0
    g33: LineSegment StartX=-49.19 StartY=43.25 StartZ=0 EndX=-16.28 EndY=43.25 EndZ=0
    g34: LineSegment StartX=-49.19 StartY=40.5 StartZ=0 EndX=-18.2337 EndY=40.5 EndZ=0
    g35: LineSegment StartX=-49.19 StartY=37.5 StartZ=0 EndX=-18.23 EndY=37.5 EndZ=0
    g36: LineSegment StartX=-49.19 StartY=34.5 StartZ=0 EndX=-18.2337 EndY=34.5 EndZ=0
    g37: LineSegment StartX=-49.19 StartY=31.5 StartZ=0 EndX=-18.23 EndY=31.5 EndZ=0
    g38: LineSegment StartX=-49.19 StartY=28.75 StartZ=0 EndX=-16.2837 EndY=28.75 EndZ=0
    g39: LineSegment StartX=-49.19 StartY=25.75 StartZ=0 EndX=-16.28 EndY=25.75 EndZ=0
    g40: LineSegment StartX=-49.19 StartY=23 StartZ=0 EndX=-11.49 EndY=23 EndZ=0
    g41: LineSegment StartX=-49.19 StartY=20 StartZ=0 EndX=-11.49 EndY=20 EndZ=0
    g42: LineSegment StartX=-49.19 StartY=17.25 StartZ=0 EndX=-1.5 EndY=17.25 EndZ=0
    g43: LineSegment StartX=-49.19 StartY=14.25 StartZ=0 EndX=-1.5 EndY=14.25 EndZ=0
    g44: LineSegment StartX=-49.19 StartY=11.5 StartZ=0 EndX=-1.5 EndY=11.5 EndZ=0
    g45: LineSegment StartX=-49.19 StartY=8.5 StartZ=0 EndX=-1.5 EndY=8.5 EndZ=0
    g46: LineSegment StartX=-49.19 StartY=5.75 StartZ=0 EndX=-1.5 EndY=5.75 EndZ=0
    g47: LineSegment StartX=-49.19 StartY=2.75 StartZ=0 EndX=-1.5 EndY=2.75 EndZ=0
  constraints (120):
    c: Vertical(g0)
    c: Distance(g0) = 3
    c: Block(g0)
    c: Vertical(g1)
    c: Distance(g1) = 3
    c: Vertical(g2)
    c: Equal(g0,g2) = 3
    c: Block(g2)
    c: Vertical(g3)
    c: Equal(g1,g3) = 3
    c: Vertical(g4)
    c: Equal(g0,g4) = 3
    c: Block(g4)
    c: Vertical(g5)
    c: Equal(g1,g5) = 3
    c: Vertical(g6)
    c: Equal(g0,g6) = 3
    c: Block(g6)
    c: Vertical(g7)
    c: Equal(g1,g7) = 3
    c: Vertical(g8)
    c: Equal(g0,g8) = 3
    c: Block(g8)
    c: Vertical(g9)
    c: Equal(g1,g9) = 3
    c: Vertical(g10)
    c: Equal(g0,g10) = 3
    c: Block(g10)
    c: Vertical(g11)
    c: Equal(g1,g11) = 3
    c: Block(g12)
    c: Block(g13)
    c: Block(g14)
    c: Block(g15)
    c: Block(g16)
    c: Block(g17)
    c: Block(g18)
    c: Block(g19)
    c: Block(g20)
    c: Block(g21)
    c: Block(g22)
    c: Block(g23)
    c: Block(g11)
    c: Block(g9)
    c: Block(g7)
    c: Block(g5)
    c: Block(g3)
    c: Block(g1)
    c: Coincident(g24,g0)
    c: Coincident(g24,g12)
    c: Horizontal(g24)
    c: Coincident(g25,g0)
    c: Coincident(g25,g12)
    c: Horizontal(g25)
    c: Coincident(g26,g1)
    c: Coincident(g26,g13)
    c: Horizontal(g26)
    c: Coincident(g27,g1)
    c: Coincident(g27,g13)
    c: Horizontal(g27)
    c: Coincident(g28,g2)
    c: Coincident(g28,g14)
    c: Horizontal(g28)
    c: Coincident(g29,g2)
    c: Coincident(g29,g14)
    c: Horizontal(g29)
    c: Coincident(g30,g3)
    c: Coincident(g30,g15)
    c: Horizontal(g30)
    c: Coincident(g31,g3)
    c: Coincident(g31,g15)
    c: Horizontal(g31)
    c: Coincident(g32,g4)
    c: Coincident(g32,g16)
    c: Horizontal(g32)
    c: Coincident(g33,g4)
    c: Coincident(g33,g16)
    c: Horizontal(g33)
    c: Coincident(g34,g5)
    c: Coincident(g34,g17)
    c: Horizontal(g34)
    c: Coincident(g35,g5)
    c: Coincident(g35,g17)
    c: Horizontal(g35)
    c: Coincident(g36,g6)
    c: Coincident(g36,g19)
    c: Horizontal(g36)
    c: Coincident(g37,g6)
    c: Coincident(g37,g19)
    c: Horizontal(g37)
    c: Coincident(g38,g7)
    c: Coincident(g38,g18)
    c: Horizontal(g38)
    c: Coincident(g39,g7)
    c: Coincident(g39,g18)
    c: Horizontal(g39)
    c: Coincident(g40,g8)
    c: Coincident(g40,g20)
    c: Horizontal(g40)
    c: Coincident(g41,g8)
    c: Coincident(g41,g20)
    c: Horizontal(g41)
    c: Coincident(g42,g9)
    c: Coincident(g42,g23)
    c: Horizontal(g42)
    c: Coincident(g43,g9)
    c: Coincident(g43,g23)
    c: Horizontal(g43)
    c: Coincident(g44,g10)
    c: Coincident(g44,g22)
    c: Horizontal(g44)
    c: Coincident(g45,g10)
    c: Coincident(g45,g22)
    c: Horizontal(g45)
    c: Coincident(g46,g11)
    c: Coincident(g46,g21)
    c: Horizontal(g46)
    c: Coincident(g47,g11)
    c: Coincident(g47,g21)
    c: Horizontal(g47)
FEATURE [Sketcher::SketchObject] Sketch031
  FullyConstrained = true
  Placement = pos=(117,19,0) rot=(0.57735,0.57735,0.57735;2.0944rad)
  sketch-geometry (24):
    g0: ArcOfCircle CenterX=-49.19 CenterY=67.75 CenterZ=0 NormalX=0 NormalY=0 NormalZ=1 AngleXU=0 Radius=1.5 StartAngle=1.5708 EndAngle=4.71239
    g1: ArcOfCircle CenterX=-49.19 CenterY=62 CenterZ=0 NormalX=0 NormalY=0 NormalZ=1 AngleXU=0 Radius=1.5 StartAngle=1.5708 EndAngle=4.71239
    g2: ArcOfCircle CenterX=-49.19 CenterY=56.25 CenterZ=0 NormalX=0 NormalY=0 NormalZ=1 AngleXU=0 Radius=1.5 StartAngle=1.5708 EndAngle=4.71239
    g3: ArcOfCircle CenterX=-49.19 CenterY=50.5 CenterZ=0 NormalX=0 NormalY=0 NormalZ=1 AngleXU=0 Radius=1.5 StartAngle=1.5708 EndAngle=4.71239
    g4: ArcOfCircle CenterX=-49.19 CenterY=44.75 CenterZ=0 NormalX=0 NormalY=0 NormalZ=1 AngleXU=0 Radius=1.5 StartAngle=1.5708 EndAngle=4.71239
    g5: ArcOfCircle CenterX=-49.19 CenterY=39 CenterZ=0 NormalX=0 NormalY=0 NormalZ=1 AngleXU=0 Radius=1.5 StartAngle=1.5708 EndAngle=4.71239
    g6: ArcOfCircle CenterX=-49.19 CenterY=33 CenterZ=0 NormalX=0 NormalY=0 NormalZ=1 AngleXU=0 Radius=1.5 StartAngle=1.5708 EndAngle=4.71239
    g7: ArcOfCircle CenterX=-49.19 CenterY=27.25 CenterZ=0 NormalX=0 NormalY=0 NormalZ=1 AngleXU=0 Radius=1.5 StartAngle=1.5708 EndAngle=4.71239
    g8: ArcOfCircle CenterX=-49.19 CenterY=21.5 CenterZ=0 NormalX=0 NormalY=0 NormalZ=1 AngleXU=0 Radius=1.5 StartAngle=1.5708 EndAngle=4.71239
    g9: ArcOfCircle CenterX=-49.19 CenterY=15.75 CenterZ=0 NormalX=0 NormalY=0 NormalZ=1 AngleXU=0 Radius=1.5 StartAngle=1.5708 EndAngle=4.71239
    g10: ArcOfCircle CenterX=-49.19 CenterY=10 CenterZ=0 NormalX=0 NormalY=0 NormalZ=1 AngleXU=0 Radius=1.5 StartAngle=1.5708 EndAngle=4.71239
    g11: ArcOfCircle CenterX=-49.19 CenterY=4.25 CenterZ=0 NormalX=0 NormalY=0 NormalZ=1 AngleXU=0 Radius=1.5 StartAngle=1.5708 EndAngle=4.71239
    g12: LineSegment StartX=-49.19 StartY=69.25 StartZ=0 EndX=-49.19 EndY=66.25 EndZ=0
    g13: LineSegment StartX=-49.19 StartY=63.5 StartZ=0 EndX=-49.19 EndY=60.5 EndZ=0
    g14: LineSegment StartX=-49.19 StartY=57.75 StartZ=0 EndX=-49.19 EndY=54.75 EndZ=0
    g15: LineSegment StartX=-49.19 StartY=52 StartZ=0 EndX=-49.19 EndY=49 EndZ=0
    g16: LineSegment StartX=-49.19 StartY=46.25 StartZ=0 EndX=-49.19 EndY=43.25 EndZ=0
    g17: LineSegment StartX=-49.19 StartY=40.5 StartZ=0 EndX=-49.19 EndY=37.5 EndZ=0
    g18: LineSegment StartX=-49.19 StartY=34.5 StartZ=0 EndX=-49.19 EndY=31.5 EndZ=0
    g19: LineSegment StartX=-49.19 StartY=28.75 StartZ=0 EndX=-49.19 EndY=25.75 EndZ=0
    g20: LineSegment StartX=-49.19 StartY=23 StartZ=0 EndX=-49.19 EndY=20 EndZ=0
    g21: LineSegment StartX=-49.19 StartY=17.25 StartZ=0 EndX=-49.19 EndY=14.25 EndZ=0
    g22: LineSegment StartX=-49.19 StartY=11.5 StartZ=0 EndX=-49.19 EndY=8.5 EndZ=0
    g23: LineSegment StartX=-49.19 StartY=5.75 StartZ=0 EndX=-49.19 EndY=2.75 EndZ=0
  constraints (48):
    c: Block(g0)
    c: Block(g1)
    c: Block(g2)
    c: Block(g3)
    c: Block(g4)
    c: Block(g5)
    c: Block(g6)
    c: Block(g7)
    c: Block(g8)
    c: Block(g9)
    c: Block(g10)
    c: Block(g11)
    c: Coincident(g12,g0)
    c: Coincident(g12,g0)
    c: Vertical(g12)
    c: Vertical(g13)
    c: Coincident(g13,g1)
    c: Vertical(g14)
    c: Coincident(g14,g2)
    c: Vertical(g15)
    c: Coincident(g15,g3)
    c: Vertical(g16)
    c: Coincident(g16,g4)
    c: Vertical(g17)
    c: Coincident(g17,g5)
    c: Vertical(g18)
    c: Coincident(g18,g6)
    c: Vertical(g19)
    c: Coincident(g19,g7)
    c: Vertical(g20)
    c: Coincident(g20,g8)
    c: Vertical(g21)
    c: Coincident(g21,g9)
    c: Vertical(g22)
    c: Coincident(g22,g10)
    c: Vertical(g23)
    c: Coincident(g23,g11)
    c: Block(g23)
    c: Block(g22)
    c: Block(g21)
    c: Block(g20)
    c: Block(g13)
    c: Block(g14)
    c: Block(g15)
    c: Block(g16)
    c: Block(g17)
    c: Block(g18)
    c: Block(g19)
FEATURE [Part::Extrusion] Extrude022
  Base = -> Sketch030
  Dir = (1,-2e-16,2e-16)
  DirMode = 2
  FaceMakerClass = Part::FaceMakerBullseye
  LengthFwd = 19
  LengthRev = 0
  Placement = pos=(-19,0,0) rot=(0,0,1;0rad)
  Solid = true
  Symmetric = false
FEATURE [Part::Fillet] Fillet022
  Base = -> Extrude022
  Edges = 24 edges r=1.49: [Edge6,Edge11,Edge18,Edge23,Edge30,Edge35,Edge42,Edge47,Edge54,Edge59,Edge66,Edge71,Edge78,Edge83,Edge90,Edge95,Edge102,Edge107,Edge114,Edge119,Edge126,Edge131,Edge138,Edge143]
FEATURE [Part::Cut] Cut020  label="top010"
  Base = -> Cut019
  Tool = -> Fillet022
FEATURE [Sketcher::SketchObject] Sketch032
  FullyConstrained = true
  Placement = pos=(117,19,0) rot=(0.57735,0.57735,0.57735;2.0944rad)
  sketch-geometry (48):
    g0: LineSegment StartX=-49.19 StartY=69.25 StartZ=0 EndX=-49.19 EndY=66.25 EndZ=0
    g1: LineSegment StartX=-49.19 StartY=63.5 StartZ=0 EndX=-49.19 EndY=60.5 EndZ=0
    g2: LineSegment StartX=-49.19 StartY=57.75 StartZ=0 EndX=-49.19 EndY=54.75 EndZ=0
    g3: LineSegment StartX=-49.19 StartY=52 StartZ=0 EndX=-49.19 EndY=49 EndZ=0
    g4: LineSegment StartX=-49.19 StartY=46.25 StartZ=0 EndX=-49.19 EndY=43.25 EndZ=0
    g5: LineSegment StartX=-49.19 StartY=40.5 StartZ=0 EndX=-49.19 EndY=37.5 EndZ=0
    g6: LineSegment StartX=-49.19 StartY=34.5 StartZ=0 EndX=-49.19 EndY=31.5 EndZ=0
    g7: LineSegment StartX=-49.19 StartY=28.75 StartZ=0 EndX=-49.19 EndY=25.75 EndZ=0
    g8: LineSegment StartX=-49.19 StartY=23 StartZ=0 EndX=-49.19 EndY=20 EndZ=0
    g9: LineSegment StartX=-49.19 StartY=17.25 StartZ=0 EndX=-49.19 EndY=14.25 EndZ=0
    g10: LineSegment StartX=-49.19 StartY=11.5 StartZ=0 EndX=-49.19 EndY=8.5 EndZ=0
    g11: LineSegment StartX=-49.19 StartY=5.75 StartZ=0 EndX=-49.19 EndY=2.75 EndZ=0
    g12: ArcOfCircle CenterX=-1.5 CenterY=67.75 CenterZ=0 NormalX=0 NormalY=0 NormalZ=1 AngleXU=0 Radius=1.5 StartAngle=4.71239 EndAngle=7.85398
    g13: ArcOfCircle CenterX=-1.5 CenterY=62 CenterZ=0 NormalX=0 NormalY=0 NormalZ=1 AngleXU=0 Radius=1.5 StartAngle=4.71239 EndAngle=7.85398
    g14: ArcOfCircle CenterX=-1.5 CenterY=56.25 CenterZ=0 NormalX=0 NormalY=0 NormalZ=1 AngleXU=0 Radius=1.5 StartAngle=4.71239 EndAngle=7.85398
    g15: ArcOfCircle CenterX=-11.49 CenterY=50.5 CenterZ=0 NormalX=0 NormalY=0 NormalZ=1 AngleXU=0 Radius=1.5 StartAngle=4.71239 EndAngle=7.85398
    g16: ArcOfCircle CenterX=-16.28 CenterY=44.75 CenterZ=0 NormalX=0 NormalY=0 NormalZ=1 AngleXU=0 Radius=1.5 StartAngle=4.71239 EndAngle=7.85398
    g17: ArcOfCircle CenterX=-18.2337 CenterY=39 CenterZ=0 NormalX=0 NormalY=0 NormalZ=1 AngleXU=0 Radius=1.5 StartAngle=4.71485 EndAngle=7.85398
    g18: ArcOfCircle CenterX=-16.2837 CenterY=27.25 CenterZ=0 NormalX=0 NormalY=0 NormalZ=1 AngleXU=0 Radius=1.5 StartAngle=4.71485 EndAngle=7.85398
    g19: ArcOfCircle CenterX=-18.2337 CenterY=33 CenterZ=0 NormalX=0 NormalY=0 NormalZ=1 AngleXU=0 Radius=1.5 StartAngle=4.71485 EndAngle=7.85398
    g20: ArcOfCircle CenterX=-11.49 CenterY=21.5 CenterZ=0 NormalX=0 NormalY=0 NormalZ=1 AngleXU=0 Radius=1.5 StartAngle=4.71239 EndAngle=7.85398
    g21: ArcOfCircle CenterX=-1.5 CenterY=4.25 CenterZ=0 NormalX=0 NormalY=0 NormalZ=1 AngleXU=0 Radius=1.5 StartAngle=4.71239 EndAngle=7.85398
    g22: ArcOfCircle CenterX=-1.5 CenterY=10 CenterZ=0 NormalX=0 NormalY=0 NormalZ=1 AngleXU=0 Radius=1.5 StartAngle=4.71239 EndAngle=7.85398
    g23: ArcOfCircle CenterX=-1.5 CenterY=15.75 CenterZ=0 NormalX=0 NormalY=0 NormalZ=1 AngleXU=0 Radius=1.5 StartAngle=4.71239 EndAngle=7.85398
    g24: LineSegment StartX=-49.19 StartY=69.25 StartZ=0 EndX=-1.5 EndY=69.25 EndZ=0
    g25: LineSegment StartX=-49.19 StartY=66.25 StartZ=0 EndX=-1.5 EndY=66.25 EndZ=0
    g26: LineSegment StartX=-49.19 StartY=63.5 StartZ=0 EndX=-1.5 EndY=63.5 EndZ=0
    g27: LineSegment StartX=-49.19 StartY=60.5 StartZ=0 EndX=-1.5 EndY=60.5 EndZ=0
    g28: LineSegment StartX=-49.19 StartY=57.75 StartZ=0 EndX=-1.5 EndY=57.75 EndZ=0
    g29: LineSegment StartX=-49.19 StartY=54.75 StartZ=0 EndX=-1.5 EndY=54.75 EndZ=0
    g30: LineSegment StartX=-49.19 StartY=52 StartZ=0 EndX=-11.49 EndY=52 EndZ=0
    g31: LineSegment StartX=-49.19 StartY=49 StartZ=0 EndX=-11.49 EndY=49 EndZ=0
    g32: LineSegment StartX=-49.19 StartY=46.25 StartZ=0 EndX=-16.28 EndY=46.25 EndZ=0
    g33: LineSegment StartX=-49.19 StartY=43.25 StartZ=0 EndX=-16.28 EndY=43.25 EndZ=0
    g34: LineSegment StartX=-49.19 StartY=40.5 StartZ=0 EndX=-18.2337 EndY=40.5 EndZ=0
    g35: LineSegment StartX=-49.19 StartY=37.5 StartZ=0 EndX=-18.23 EndY=37.5 EndZ=0
    g36: LineSegment StartX=-49.19 StartY=34.5 StartZ=0 EndX=-18.2337 EndY=34.5 EndZ=0
    g37: LineSegment StartX=-49.19 StartY=31.5 StartZ=0 EndX=-18.23 EndY=31.5 EndZ=0
    g38: LineSegment StartX=-49.19 StartY=28.75 StartZ=0 EndX=-16.2837 EndY=28.75 EndZ=0
    g39: LineSegment StartX=-49.19 StartY=25.75 StartZ=0 EndX=-16.28 EndY=25.75 EndZ=0
    g40: LineSegment StartX=-49.19 StartY=23 StartZ=0 EndX=-11.49 EndY=23 EndZ=0
    g41: LineSegment StartX=-49.19 StartY=20 StartZ=0 EndX=-11.49 EndY=20 EndZ=0
    g42: LineSegment StartX=-49.19 StartY=17.25 StartZ=0 EndX=-1.5 EndY=17.25 EndZ=0
    g43: LineSegment StartX=-49.19 StartY=14.25 StartZ=0 EndX=-1.5 EndY=14.25 EndZ=0
    g44: LineSegment StartX=-49.19 StartY=11.5 StartZ=0 EndX=-1.5 EndY=11.5 EndZ=0
    g45: LineSegment StartX=-49.19 StartY=8.5 StartZ=0 EndX=-1.5 EndY=8.5 EndZ=0
    g46: LineSegment StartX=-49.19 StartY=5.75 StartZ=0 EndX=-1.5 EndY=5.75 EndZ=0
    g47: LineSegment StartX=-49.19 StartY=2.75 StartZ=0 EndX=-1.5 EndY=2.75 EndZ=0
  constraints (120):
    c: Vertical(g0)
    c: Distance(g0) = 3
    c: Block(g0)
    c: Vertical(g1)
    c: Distance(g1) = 3
    c: Vertical(g2)
    c: Equal(g0,g2) = 3
    c: Block(g2)
    c: Vertical(g3)
    c: Equal(g1,g3) = 3
    c: Vertical(g4)
    c: Equal(g0,g4) = 3
    c: Block(g4)
    c: Vertical(g5)
    c: Equal(g1,g5) = 3
    c: Vertical(g6)
    c: Equal(g0,g6) = 3
    c: Block(g6)
    c: Vertical(g7)
    c: Equal(g1,g7) = 3
    c: Vertical(g8)
    c: Equal(g0,g8) = 3
    c: Block(g8)
    c: Vertical(g9)
    c: Equal(g1,g9) = 3
    c: Vertical(g10)
    c: Equal(g0,g10) = 3
    c: Block(g10)
    c: Vertical(g11)
    c: Equal(g1,g11) = 3
    c: Block(g12)
    c: Block(g13)
    c: Block(g14)
    c: Block(g15)
    c: Block(g16)
    c: Block(g17)
    c: Block(g18)
    c: Block(g19)
    c: Block(g20)
    c: Block(g21)
    c: Block(g22)
    c: Block(g23)
    c: Block(g11)
    c: Block(g9)
    c: Block(g7)
    c: Block(g5)
    c: Block(g3)
    c: Block(g1)
    c: Coincident(g24,g0)
    c: Coincident(g24,g12)
    c: Horizontal(g24)
    c: Coincident(g25,g0)
    c: Coincident(g25,g12)
    c: Horizontal(g25)
    c: Coincident(g26,g1)
    c: Coincident(g26,g13)
    c: Horizontal(g26)
    c: Coincident(g27,g1)
    c: Coincident(g27,g13)
    c: Horizontal(g27)
    c: Coincident(g28,g2)
    c: Coincident(g28,g14)
    c: Horizontal(g28)
    c: Coincident(g29,g2)
    c: Coincident(g29,g14)
    c: Horizontal(g29)
    c: Coincident(g30,g3)
    c: Coincident(g30,g15)
    c: Horizontal(g30)
    c: Coincident(g31,g3)
    c: Coincident(g31,g15)
    c: Horizontal(g31)
    c: Coincident(g32,g4)
    c: Coincident(g32,g16)
    c: Horizontal(g32)
    c: Coincident(g33,g4)
    c: Coincident(g33,g16)
    c: Horizontal(g33)
    c: Coincident(g34,g5)
    c: Coincident(g34,g17)
    c: Horizontal(g34)
    c: Coincident(g35,g5)
    c: Coincident(g35,g17)
    c: Horizontal(g35)
    c: Coincident(g36,g6)
    c: Coincident(g36,g19)
    c: Horizontal(g36)
    c: Coincident(g37,g6)
    c: Coincident(g37,g19)
    c: Horizontal(g37)
    c: Coincident(g38,g7)
    c: Coincident(g38,g18)
    c: Horizontal(g38)
    c: Coincident(g39,g7)
    c: Coincident(g39,g18)
    c: Horizontal(g39)
    c: Coincident(g40,g8)
    c: Coincident(g40,g20)
    c: Horizontal(g40)
    c: Coincident(g41,g8)
    c: Coincident(g41,g20)
    c: Horizontal(g41)
    c: Coincident(g42,g9)
    c: Coincident(g42,g23)
    c: Horizontal(g42)
    c: Coincident(g43,g9)
    c: Coincident(g43,g23)
    c: Horizontal(g43)
    c: Coincident(g44,g10)
    c: Coincident(g44,g22)
    c: Horizontal(g44)
    c: Coincident(g45,g10)
    c: Coincident(g45,g22)
    c: Horizontal(g45)
    c: Coincident(g46,g11)
    c: Coincident(g46,g21)
    c: Horizontal(g46)
    c: Coincident(g47,g11)
    c: Coincident(g47,g21)
    c: Horizontal(g47)
FEATURE [Part::Extrusion] Extrude023
  Base = -> Sketch032
  Dir = (1,-2e-16,2e-16)
  DirMode = 2
  FaceMakerClass = Part::FaceMakerBullseye
  LengthFwd = 19
  LengthRev = 0
  Placement = pos=(-19,0,0) rot=(0,0,1;0rad)
  Solid = true
  Symmetric = false
FEATURE [Part::Fillet] Fillet023
  Base = -> Extrude023
  Edges = <same value as first occurrence — deduplicated (x6 in doc)>
  Placement = pos=(0,0.05,0) rot=(0,0,1;0rad)
FEATURE [Part::Cut] Cut014  label="bottom003"
  Base = -> Cut007
  Tool = -> Fusion047
FEATURE [Part::Cut] Cut021  label="bottom004"
  Base = -> Cut014
  Tool = -> Fillet023
FEATURE [Sketcher::SketchObject] Sketch033
  FullyConstrained = true
  Placement = pos=(117,19,0) rot=(0.57735,0.57735,0.57735;2.0944rad)
  sketch-geometry (8):
    g0: LineSegment StartX=-49.19 StartY=69.25 StartZ=0 EndX=-49.19 EndY=66.25 EndZ=0
    g1: LineSegment StartX=-49.19 StartY=5.75 StartZ=0 EndX=-49.19 EndY=2.75 EndZ=0
    g2: ArcOfCircle CenterX=-1.5 CenterY=67.75 CenterZ=0 NormalX=0 NormalY=0 NormalZ=1 AngleXU=0 Radius=1.5 StartAngle=4.71239 EndAngle=7.85398
    g3: ArcOfCircle CenterX=-1.5 CenterY=4.25 CenterZ=0 NormalX=0 NormalY=0 NormalZ=1 AngleXU=0 Radius=1.5 StartAngle=4.71239 EndAngle=7.85398
    g4: LineSegment StartX=-49.19 StartY=69.25 StartZ=0 EndX=-1.5 EndY=69.25 EndZ=0
    g5: LineSegment StartX=-49.19 StartY=66.25 StartZ=0 EndX=-1.5 EndY=66.25 EndZ=0
    g6: LineSegment StartX=-49.19 StartY=5.75 StartZ=0 EndX=-1.5 EndY=5.75 EndZ=0
    g7: LineSegment StartX=-49.19 StartY=2.75 StartZ=0 EndX=-1.5 EndY=2.75 EndZ=0
  constraints (19):
    c: Vertical(g0)
    c: Distance(g0) = 3
    c: Block(g0)
    c: Vertical(g1)
    c: Block(g2)
    c: Block(g3)
    c: Block(g1)
    c: Coincident(g4,g0)
    c: Coincident(g4,g2)
    c: Horizontal(g4)
    c: Coincident(g5,g0)
    c: Coincident(g5,g2)
    c: Horizontal(g5)
    c: Coincident(g6,g1)
    c: Coincident(g6,g3)
    c: Horizontal(g6)
    c: Coincident(g7,g1)
    c: Coincident(g7,g3)
    c: Horizontal(g7)
FEATURE [Sketcher::SketchObject] Sketch034
  FullyConstrained = true
  Placement = pos=(117,19,0) rot=(0.57735,0.57735,0.57735;2.0944rad)
  sketch-geometry (8):
    g0: LineSegment StartX=-49.19 StartY=63.5 StartZ=0 EndX=-49.19 EndY=60.5 EndZ=0
    g1: LineSegment StartX=-49.19 StartY=11.5 StartZ=0 EndX=-49.19 EndY=8.5 EndZ=0
    g2: ArcOfCircle CenterX=-1.5 CenterY=62 CenterZ=0 NormalX=0 NormalY=0 NormalZ=1 AngleXU=0 Radius=1.5 StartAngle=4.71239 EndAngle=7.85398
    g3: ArcOfCircle CenterX=-1.5 CenterY=10 CenterZ=0 NormalX=0 NormalY=0 NormalZ=1 AngleXU=0 Radius=1.5 StartAngle=4.71239 EndAngle=7.85398
    g4: LineSegment StartX=-49.19 StartY=63.5 StartZ=0 EndX=-1.5 EndY=63.5 EndZ=0
    g5: LineSegment StartX=-49.19 StartY=60.5 StartZ=0 EndX=-1.5 EndY=60.5 EndZ=0
    g6: LineSegment StartX=-49.19 StartY=11.5 StartZ=0 EndX=-1.5 EndY=11.5 EndZ=0
    g7: LineSegment StartX=-49.19 StartY=8.5 StartZ=0 EndX=-1.5 EndY=8.5 EndZ=0
  constraints (19):
    c: Vertical(g0)
    c: Distance(g0) = 3
    c: Vertical(g1)
    c: Block(g1)
    c: Block(g2)
    c: Block(g3)
    c: Block(g0)
    c: Coincident(g4,g0)
    c: Coincident(g4,g2)
    c: Horizontal(g4)
    c: Coincident(g5,g0)
    c: Coincident(g5,g2)
    c: Horizontal(g5)
    c: Coincident(g6,g1)
    c: Coincident(g6,g3)
    c: Horizontal(g6)
    c: Coincident(g7,g1)
    c: Coincident(g7,g3)
    c: Horizontal(g7)
FEATURE [Part::Extrusion] Extrude024
  Base = -> Sketch033
  Dir = (1,0,0)
  DirMode = 2
  FaceMakerClass = Part::FaceMakerBullseye
  LengthFwd = 10
  LengthRev = 0
  Solid = true
  Symmetric = false
FEATURE [Part::Extrusion] Extrude025
  Base = -> Sketch034
  Dir = (1,0,0)
  DirMode = 2
  FaceMakerClass = Part::FaceMakerBullseye
  LengthFwd = 10
  LengthRev = 0
  Solid = true
  Symmetric = false
FEATURE [Part::Fillet] Fillet024  label="removeFromtMoreFrontCaseScrewRetainers"
  Base = -> Extrude024
  Edges = 4 edges r=1.49: [Edge6,Edge11,Edge18,Edge23]
  Placement = pos=(-11,0,0) rot=(0,0,1;0rad)
FEATURE [Part::Fillet] Fillet025  label="removeFromtMoreFrontCaseScrewRetainers001"
  Base = -> Extrude025
  Edges = 4 edges r=1.49: [Edge6,Edge11,Edge18,Edge23]
  Placement = pos=(-19,0,0) rot=(0,0,1;0rad)
FEATURE [Part::Cut] Cut022
  Base = -> Cut015
  Tool = -> Fillet025
FEATURE [Part::Cut] Cut023  label="screwRetainers"
  Base = -> Cut022
  Tool = -> Fillet024
FEATURE [Part::MultiFuse] Fusion056  label="bottom005"
  Shapes = -> [Fusion044,Cut021]
FEATURE [Part::MultiFuse] Fusion057  label="casePillars001"
  Shapes = -> [Cut016,Fusion052]
FEATURE [Part::MultiFuse] Fusion058  label="bottom006"
  Shapes = -> [Fusion056,Cut023]
FEATURE [Part::MultiFuse] Fusion059  label="bottom007"
  Shapes = -> [Fusion058,Fillet005]
FEATURE [Part::MultiFuse] Fusion060  label="bottom008"
  Shapes = -> [Fusion059,Fusion]
FEATURE [Part::MultiFuse] Fusion061  label="top011"
  Shapes = -> [Cut006,Cut020]
FEATURE [Part::MultiFuse] Fusion062  label="top012"
  Shapes = -> [Fusion057,Fusion061]
FEATURE [Sketcher::SketchObject] Sketch035  label="topSketch007"
  FullyConstrained = true
  sketch-geometry (6):
    g0: LineSegment StartX=19 StartY=38 StartZ=0 EndX=117 EndY=38 EndZ=0
    g1: ArcOfCircle CenterX=19 CenterY=19 CenterZ=0 NormalX=0 NormalY=0 NormalZ=1 AngleXU=0 Radius=19 StartAngle=1.5708 EndAngle=3.14159
    g2: LineSegment StartX=117 StartY=38 StartZ=0 EndX=117 EndY=19 EndZ=0
    g3: LineSegment StartX=98 StartY=1.0161e-12 StartZ=0 EndX=5.22862e-06 EndY=1.0161e-12 EndZ=0
    g4: LineSegment StartX=5.22862e-06 StartY=19 StartZ=0 EndX=5.22862e-06 EndY=1.0161e-12 EndZ=0
    g5: ArcOfCircle CenterX=98 CenterY=19 CenterZ=0 NormalX=0 NormalY=0 NormalZ=1 AngleXU=0 Radius=19 StartAngle=4.71239 EndAngle=6.28319
  constraints (16):
    c: Horizontal(g0)
    c: Distance(g0) = 98
    c: Coincident(g1,g0)
    c: Block(g1)
    c: Coincident(g2,g0)
    c: Vertical(g2)
    c: Distance(g2) = 19
    c: Horizontal(g3)
    c: Coincident(g4,g1)
    c: Vertical(g4)
    c: Coincident(g3,g4)
    c: Block(g3)
    c: Coincident(g5,g2)
    c: Coincident(g5,g3)
    c: Block(g0)
    c: Block(g5)
FEATURE [Part::Extrusion] Extrude026  label="sideA001"
  Base = -> Sketch035
  Dir = (0,0,1)
  DirMode = 2
  FaceMakerClass = Part::FaceMakerBullseye
  LengthFwd = 3
  LengthRev = 0
  Placement = pos=(0,0,-2.7) rot=(0,0,1;0rad)
  Solid = true
  Symmetric = false
FEATURE [Sketcher::SketchObject] Sketch036  label="topSketch008"
  FullyConstrained = true
  sketch-geometry (6):
    g0: LineSegment StartX=19 StartY=38 StartZ=0 EndX=117 EndY=38 EndZ=0
    g1: ArcOfCircle CenterX=19 CenterY=19 CenterZ=0 NormalX=0 NormalY=0 NormalZ=1 AngleXU=0 Radius=19 StartAngle=1.5708 EndAngle=3.14159
    g2: LineSegment StartX=117 StartY=38 StartZ=0 EndX=117 EndY=19 EndZ=0
    g3: LineSegment StartX=98 StartY=1.0161e-12 StartZ=0 EndX=5.22862e-06 EndY=1.0161e-12 EndZ=0
    g4: LineSegment StartX=5.22862e-06 StartY=19 StartZ=0 EndX=5.22862e-06 EndY=1.0161e-12 EndZ=0
    g5: ArcOfCircle CenterX=98 CenterY=19 CenterZ=0 NormalX=0 NormalY=0 NormalZ=1 AngleXU=0 Radius=19 StartAngle=4.71239 EndAngle=6.28319
  constraints (16):
    c: Horizontal(g0)
    c: Distance(g0) = 98
    c: Coincident(g1,g0)
    c: Block(g1)
    c: Coincident(g2,g0)
    c: Vertical(g2)
    c: Distance(g2) = 19
    c: Horizontal(g3)
    c: Coincident(g4,g1)
    c: Vertical(g4)
    c: Coincident(g3,g4)
    c: Block(g3)
    c: Coincident(g5,g2)
    c: Coincident(g5,g3)
    c: Block(g0)
    c: Block(g5)
FEATURE [Part::Extrusion] Extrude027  label="sideB001"
  Base = -> Sketch036
  Dir = (0,0,1)
  DirMode = 2
  FaceMakerClass = Part::FaceMakerBullseye
  LengthFwd = 3
  LengthRev = 0
  Placement = pos=(0,0,71.7) rot=(0,0,1;0rad)
  Solid = true
  Symmetric = false
FEATURE [Part::MultiFuse] Fusion064  label="removeFromBottom"
  Shapes = -> [Extrude026,Extrude027]
FEATURE [Part::Cut] Cut024  label="bottom009"
  Base = -> Fusion060
  Tool = -> Fusion064
FEATURE [Sketcher::SketchObject] Sketch037  label="topSketch009"
  FullyConstrained = true
  sketch-geometry (8):
    g0: ArcOfCircle CenterX=19 CenterY=19.1201 CenterZ=0 NormalX=0 NormalY=0 NormalZ=1 AngleXU=0 Radius=18.8799 StartAngle=1.5708 EndAngle=3.14793
    g1: LineSegment StartX=0.120501 StartY=19.0004 StartZ=0 EndX=0.120501 EndY=0.000382114 EndZ=0
    g2: LineSegment StartX=19 StartY=38 StartZ=0 EndX=124 EndY=38 EndZ=0
    g3: LineSegment StartX=0.120501 StartY=0.000382114 StartZ=0 EndX=105.121 EndY=0.000382114 EndZ=0
    g4: LineSegment StartX=124 StartY=38 StartZ=0 EndX=125.616 EndY=38 EndZ=0
    g5: LineSegment StartX=105.121 StartY=0.000382114 StartZ=0 EndX=106.736 EndY=0.000382114 EndZ=0
    g6: ArcOfCircle CenterX=106.616 CenterY=19 CenterZ=0 NormalX=0 NormalY=0 NormalZ=1 AngleXU=0 Radius=19 StartAngle=4.71873 EndAngle=6.28319
    g7: LineSegment StartX=125.616 StartY=38 StartZ=0 EndX=125.616 EndY=19 EndZ=0
  constraints (21):
    c: Block(g0)
    c: Coincident(g1,g0)
    c: Vertical(g1)
    c: Horizontal(g2)
    c: Distance(g2) = 105
    c: Coincident(g2,g0)
    c: Distance(g1) = 19
    c: Coincident(g3,g1)
    c: Horizontal(g3)
    c: Distance(g3) = 105
    c: Coincident(g4,g2)
    c: Horizontal(g4)
    c: Distance(g4) = 1.61553
    c: Horizontal(g5)
    c: Equal(g4,g5) = 1.61553
    c: Coincident(g5,g3)
    c: Block(g6)
    c: Coincident(g6,g5)
    c: Coincident(g7,g4)
    c: Coincident(g7,g6)
    c: Vertical(g7)
FEATURE [Part::Extrusion] Extrude028  label="sideB"
  Base = -> Sketch037
  Dir = (0,0,1)
  DirMode = 2
  FaceMakerClass = Part::FaceMakerBullseye
  LengthFwd = 3
  LengthRev = 0
  Placement = pos=(0,0,72) rot=(0,0,1;0rad)
  Solid = true
  Symmetric = false
FEATURE [Sketcher::SketchObject] Sketch038  label="topSketch010"
  FullyConstrained = true
  sketch-geometry (22):
    g0: LineSegment StartX=5.21097e-06 StartY=3 StartZ=0 EndX=5.21097e-06 EndY=19 EndZ=0
    g1: ArcOfCircle CenterX=19 CenterY=19 CenterZ=0 NormalX=0 NormalY=0 NormalZ=1 AngleXU=0 Radius=19 StartAngle=1.5708 EndAngle=3.14159
    g2: ArcOfCircle CenterX=19 CenterY=19 CenterZ=0 NormalX=0 NormalY=0 NormalZ=1 AngleXU=0 Radius=16 StartAngle=1.5708 EndAngle=3.14159
    g3: LineSegment StartX=114 StartY=35 StartZ=0 EndX=19 EndY=35 EndZ=0
    g4: LineSegment StartX=5.21097e-06 StartY=3 StartZ=0 EndX=5.21097e-06 EndY=0 EndZ=0
    g5: LineSegment StartX=3 StartY=0 StartZ=0 EndX=5.21097e-06 EndY=0 EndZ=0
    g6: LineSegment StartX=3 StartY=19 StartZ=0 EndX=3 EndY=0 EndZ=0
    g7: LineSegment StartX=19 StartY=38 StartZ=0 EndX=124 EndY=38 EndZ=0
    g8: Circle CenterX=119 CenterY=35 CenterZ=0 NormalX=0 NormalY=0 NormalZ=1 AngleXU=0 Radius=1
    g9: Circle CenterX=121 CenterY=35 CenterZ=0 NormalX=0 NormalY=0 NormalZ=1 AngleXU=0 Radius=1
    g10: Circle CenterX=121 CenterY=33 CenterZ=0 NormalX=0 NormalY=0 NormalZ=1 AngleXU=0 Radius=1
    g11: BSplineCurve PolesCount=3 KnotsCount=2 Degree=2 IsPeriodic=0
    g12: GeomPoint X=119 Y=35 Z=0
    g13: GeomPoint X=121 Y=33 Z=0
    g14: LineSegment StartX=119 StartY=35 StartZ=0 EndX=114 EndY=35 EndZ=0
    g15: ArcOfCircle CenterX=105 CenterY=19 CenterZ=0 NormalX=0 NormalY=0 NormalZ=1 AngleXU=0 Radius=16 StartAngle=5.60905 EndAngle=6.28319
    g16: LineSegment StartX=121 StartY=33 StartZ=0 EndX=121 EndY=19 EndZ=0
    g17: LineSegment StartX=117.5 StartY=9.01251 StartZ=0 EndX=121.163 EndY=9.0125 EndZ=0
    g18: ArcOfCircle CenterX=105 CenterY=19 CenterZ=0 NormalX=0 NormalY=0 NormalZ=1 AngleXU=0 Radius=20.6155 StartAngle=5.7297 EndAngle=6.28319
    g19: LineSegment StartX=121.163 StartY=9.0125 StartZ=0 EndX=122.538 EndY=8.16329 EndZ=0
    g20: LineSegment StartX=124 StartY=38 StartZ=0 EndX=125.616 EndY=38 EndZ=0
    g21: LineSegment StartX=125.616 StartY=19 StartZ=0 EndX=125.616 EndY=38 EndZ=0
  constraints (49):
    c: Vertical(g0)
    c: Block(g0)
    c: Coincident(g1,g0)
    c: Block(g1)
    c: Coincident(g2,g1)
    c: Block(g2)
    c: Coincident(g3,g2)
    c: Horizontal(g3)
    c: Tangent(g3,g2)
    c: Coincident(g4,g0)
    c: Distance(g4) = 3
    c: Vertical(g4)
    c: Coincident(g5,g4)
    c: Horizontal(g5)
    c: Coincident(g6,g2)
    c: Coincident(g6,g5)
    c: Vertical(g6)
    c: Horizontal(g7)
    c: Distance(g7) = 105
    c: Coincident(g7,g1)
    c: Block(g3)
    c: Weight(g8) = 1
    c: Equal(g8,g9)
    c: Equal(g8,g10)
    c: InternalAlignment(g8,g11)
    c: InternalAlignment(g9,g11)
    c: InternalAlignment(g10,g11)
    c: InternalAlignment(g12,g11)
    c: InternalAlignment(g13,g11)
    c: Block(g11)
    c: Coincident(g14,g11)
    c: Coincident(g14,g3)
    c: Horizontal(g14)
    c: Block(g15)
    c: Coincident(g16,g11)
    c: Coincident(g16,g15)
    c: Vertical(g16)
    c: Distance(g16) = 14
    c: Coincident(g17,g15)
    c: Block(g18)
    c: Coincident(g19,g18)
    c: Coincident(g20,g7)
    c: Horizontal(g20)
    c: Vertical(g21)
    c: Coincident(g20,g21)
    c: Block(g20)
    c: Block(g21)
    c: Block(g19)
    c: Block(g17)
FEATURE [Part::Extrusion] Extrude029
  Base = -> Sketch038
  Dir = (0,0,1)
  DirMode = 2
  FaceMakerClass = Part::FaceMakerBullseye
  LengthFwd = 72
  LengthRev = 0
  Solid = true
  Symmetric = false
FEATURE [Part::Feature] Face085
  shape: bbox 4.8 x 25.5 x 2e-07 mm, 1 faces, 0 solids (baked)
FEATURE [Part::Revolution] Revolve089  label="moreFrontCaseScrewPost003"
  Angle = 360
  Axis = (0,1,0)
  Base = (0,0,0)
  FaceMakerClass = Part::FaceMakerBullseye
  Placement = pos=(109.5,4.5,3.5) rot=(0,0,1;0rad)
  Solid = false
  Source = -> Face085
  Symmetric = false
FEATURE [Part::Feature] Face086
  shape: bbox 4.8 x 25.5 x 2e-07 mm, 1 faces, 0 solids (baked)
FEATURE [Part::Revolution] Revolve090  label="moreFrontCaseScrewPost004"
  Angle = 360
  Axis = (0,1,0)
  Base = (0,0,0)
  FaceMakerClass = Part::FaceMakerBullseye
  Placement = pos=(109.5,4.5,68.5) rot=(0,0,1;0rad)
  Solid = false
  Source = -> Face086
  Symmetric = false
FEATURE [Part::Fillet] Fillet026  label="top013"
  Base = -> Extrude029
  Edges = 1 edges r=2: [Edge35]
FEATURE [Sketcher::SketchObject] Sketch039
  FullyConstrained = true
  sketch-geometry (7):
    g0: LineSegment StartX=0 StartY=0 StartZ=0 EndX=0 EndY=6 EndZ=0
    g1: Circle CenterX=0 CenterY=0 CenterZ=0 NormalX=0 NormalY=0 NormalZ=1 AngleXU=0 Radius=1
    g2: Circle CenterX=8 CenterY=6 CenterZ=0 NormalX=0 NormalY=0 NormalZ=1 AngleXU=0 Radius=1
    g3: BSplineCurve PolesCount=3 KnotsCount=2 Degree=2 IsPeriodic=0
    g4: GeomPoint X=0 Y=0 Z=0
    g5: GeomPoint X=8 Y=6 Z=0
    g6: LineSegment StartX=0 StartY=6 StartZ=0 EndX=8 EndY=6 EndZ=0
  constraints (14):
    c: Coincident(g0,g-1)
    c: Distance(g0) = 6
    c: Vertical(g0)
    c: Coincident(g3,g0)
    c: Weight(g1) = 1
    c: Equal(g1,g2)
    c: InternalAlignment(g1,g3)
    c: InternalAlignment(g2,g3)
    c: InternalAlignment(g4,g3)
    c: InternalAlignment(g5,g3)
    c: Block(g3)
    c: Coincident(g6,g0)
    c: Coincident(g6,g3)
    c: Horizontal(g6)
FEATURE [Sketcher::SketchObject] Sketch040
  FullyConstrained = true
  sketch-geometry (7):
    g0: LineSegment StartX=0 StartY=0 StartZ=0 EndX=0 EndY=6 EndZ=0
    g1: Circle CenterX=0 CenterY=0 CenterZ=0 NormalX=0 NormalY=0 NormalZ=1 AngleXU=0 Radius=1
    g2: Circle CenterX=8 CenterY=6 CenterZ=0 NormalX=0 NormalY=0 NormalZ=1 AngleXU=0 Radius=1
    g3: BSplineCurve PolesCount=3 KnotsCount=2 Degree=2 IsPeriodic=0
    g4: GeomPoint X=0 Y=0 Z=0
    g5: GeomPoint X=8 Y=6 Z=0
    g6: LineSegment StartX=0 StartY=6 StartZ=0 EndX=8 EndY=6 EndZ=0
  constraints (14):
    c: Coincident(g0,g-1)
    c: Distance(g0) = 6
    c: Vertical(g0)
    c: Coincident(g3,g0)
    c: Weight(g1) = 1
    c: Equal(g1,g2)
    c: InternalAlignment(g1,g3)
    c: InternalAlignment(g2,g3)
    c: InternalAlignment(g4,g3)
    c: InternalAlignment(g5,g3)
    c: Block(g3)
    c: Coincident(g6,g0)
    c: Coincident(g6,g3)
    c: Horizontal(g6)
FEATURE [Sketcher::SketchObject] Sketch041
  FullyConstrained = true
  sketch-geometry (7):
    g0: LineSegment StartX=0 StartY=0 StartZ=0 EndX=0 EndY=6 EndZ=0
    g1: Circle CenterX=0 CenterY=0 CenterZ=0 NormalX=0 NormalY=0 NormalZ=1 AngleXU=0 Radius=1
    g2: Circle CenterX=8 CenterY=6 CenterZ=0 NormalX=0 NormalY=0 NormalZ=1 AngleXU=0 Radius=1
    g3: BSplineCurve PolesCount=3 KnotsCount=2 Degree=2 IsPeriodic=0
    g4: GeomPoint X=0 Y=0 Z=0
    g5: GeomPoint X=8 Y=6 Z=0
    g6: LineSegment StartX=0 StartY=6 StartZ=0 EndX=8 EndY=6 EndZ=0
  constraints (14):
    c: Coincident(g0,g-1)
    c: Distance(g0) = 6
    c: Vertical(g0)
    c: Coincident(g3,g0)
    c: Weight(g1) = 1
    c: Equal(g1,g2)
    c: InternalAlignment(g1,g3)
    c: InternalAlignment(g2,g3)
    c: InternalAlignment(g4,g3)
    c: InternalAlignment(g5,g3)
    c: Block(g3)
    c: Coincident(g6,g0)
    c: Coincident(g6,g3)
    c: Horizontal(g6)
FEATURE [Sketcher::SketchObject] Sketch042
  FullyConstrained = true
  sketch-geometry (7):
    g0: LineSegment StartX=0 StartY=0 StartZ=0 EndX=0 EndY=6 EndZ=0
    g1: Circle CenterX=0 CenterY=0 CenterZ=0 NormalX=0 NormalY=0 NormalZ=1 AngleXU=0 Radius=1
    g2: Circle CenterX=8 CenterY=6 CenterZ=0 NormalX=0 NormalY=0 NormalZ=1 AngleXU=0 Radius=1
    g3: BSplineCurve PolesCount=3 KnotsCount=2 Degree=2 IsPeriodic=0
    g4: GeomPoint X=0 Y=0 Z=0
    g5: GeomPoint X=8 Y=6 Z=0
    g6: LineSegment StartX=0 StartY=6 StartZ=0 EndX=8 EndY=6 EndZ=0
  constraints (14):
    c: Coincident(g0,g-1)
    c: Distance(g0) = 6
    c: Vertical(g0)
    c: Coincident(g3,g0)
    c: Weight(g1) = 1
    c: Equal(g1,g2)
    c: InternalAlignment(g1,g3)
    c: InternalAlignment(g2,g3)
    c: InternalAlignment(g4,g3)
    c: InternalAlignment(g5,g3)
    c: Block(g3)
    c: Coincident(g6,g0)
    c: Coincident(g6,g3)
    c: Horizontal(g6)
FEATURE [Part::Extrusion] Extrude030  label="caseScrewPillarBracket008"
  Base = -> Sketch039
  Dir = (0,0,1)
  DirMode = 2
  FaceMakerClass = Part::FaceMakerBullseye
  LengthFwd = 2.4
  LengthRev = 0
  Placement = pos=(15.76,29,8.8) rot=(0,1,0;0rad)
  Solid = true
  Symmetric = false
FEATURE [Part::Extrusion] Extrude031  label="caseScrewPillarBracket009"
  Base = -> Sketch040
  Dir = (0,0,1)
  DirMode = 2
  FaceMakerClass = Part::FaceMakerBullseye
  LengthFwd = 2.4
  LengthRev = 0
  Placement = pos=(15.76,29,60.8) rot=(0,0,1;0rad)
  Solid = true
  Symmetric = false
FEATURE [Part::Extrusion] Extrude032  label="caseScrewPillarBracket010"
  Base = -> Sketch041
  Dir = (0,0,1)
  DirMode = 2
  FaceMakerClass = Part::FaceMakerBullseye
  LengthFwd = 2.4
  LengthRev = 0
  Placement = pos=(13.7,29,13.26) rot=(0,-1,0;1.5708rad)
  Solid = true
  Symmetric = false
FEATURE [Part::Extrusion] Extrude033  label="caseScrewPillarBracket011"
  Base = -> Sketch042
  Dir = (0,0,1)
  DirMode = 2
  FaceMakerClass = Part::FaceMakerBullseye
  LengthFwd = 2.4
  LengthRev = 0
  Placement = pos=(11.3,29,58.74) rot=(0,1,0;1.5708rad)
  Solid = true
  Symmetric = false
FEATURE [Sketcher::SketchObject] Sketch043
  FullyConstrained = true
  sketch-geometry (7):
    g0: LineSegment StartX=0 StartY=0 StartZ=0 EndX=0 EndY=6 EndZ=0
    g1: Circle CenterX=0 CenterY=0 CenterZ=0 NormalX=0 NormalY=0 NormalZ=1 AngleXU=0 Radius=1
    g2: Circle CenterX=8 CenterY=6 CenterZ=0 NormalX=0 NormalY=0 NormalZ=1 AngleXU=0 Radius=1
    g3: BSplineCurve PolesCount=3 KnotsCount=2 Degree=2 IsPeriodic=0
    g4: GeomPoint X=0 Y=0 Z=0
    g5: GeomPoint X=8 Y=6 Z=0
    g6: LineSegment StartX=0 StartY=6 StartZ=0 EndX=8 EndY=6 EndZ=0
  constraints (14):
    c: Coincident(g0,g-1)
    c: Distance(g0) = 6
    c: Vertical(g0)
    c: Coincident(g3,g0)
    c: Weight(g1) = 1
    c: Equal(g1,g2)
    c: InternalAlignment(g1,g3)
    c: InternalAlignment(g2,g3)
    c: InternalAlignment(g4,g3)
    c: InternalAlignment(g5,g3)
    c: Block(g3)
    c: Coincident(g6,g0)
    c: Coincident(g6,g3)
    c: Horizontal(g6)
FEATURE [Part::Extrusion] Extrude034  label="caseScrewPillarBracket012"
  Base = -> Sketch043
  Dir = (0,0,1)
  DirMode = 2
  FaceMakerClass = Part::FaceMakerBullseye
  LengthFwd = 2.4
  LengthRev = 0
  Placement = pos=(88.3,29,65.23) rot=(0,1,0;1.5708rad)
  Solid = true
  Symmetric = false
FEATURE [Sketcher::SketchObject] Sketch044
  FullyConstrained = true
  sketch-geometry (7):
    g0: LineSegment StartX=0 StartY=0 StartZ=0 EndX=0 EndY=6 EndZ=0
    g1: Circle CenterX=0 CenterY=0 CenterZ=0 NormalX=0 NormalY=0 NormalZ=1 AngleXU=0 Radius=1
    g2: Circle CenterX=8 CenterY=6 CenterZ=0 NormalX=0 NormalY=0 NormalZ=1 AngleXU=0 Radius=1
    g3: BSplineCurve PolesCount=3 KnotsCount=2 Degree=2 IsPeriodic=0
    g4: GeomPoint X=0 Y=0 Z=0
    g5: GeomPoint X=8 Y=6 Z=0
    g6: LineSegment StartX=0 StartY=6 StartZ=0 EndX=8 EndY=6 EndZ=0
  constraints (14):
    c: Coincident(g0,g-1)
    c: Distance(g0) = 6
    c: Vertical(g0)
    c: Coincident(g3,g0)
    c: Weight(g1) = 1
    c: Equal(g1,g2)
    c: InternalAlignment(g1,g3)
    c: InternalAlignment(g2,g3)
    c: InternalAlignment(g4,g3)
    c: InternalAlignment(g5,g3)
    c: Block(g3)
    c: Coincident(g6,g0)
    c: Coincident(g6,g3)
    c: Horizontal(g6)
FEATURE [Part::Extrusion] Extrude035  label="caseScrewPillarBracket013"
  Base = -> Sketch044
  Dir = (0,0,1)
  DirMode = 2
  FaceMakerClass = Part::FaceMakerBullseye
  LengthFwd = 2.4
  LengthRev = 0
  Placement = pos=(90.7,29,6.77) rot=(0,-1,0;1.5708rad)
  Solid = true
  Symmetric = false
FEATURE [Sketcher::SketchObject] Sketch045
  FullyConstrained = true
  sketch-geometry (7):
    g0: LineSegment StartX=0 StartY=0 StartZ=0 EndX=0 EndY=6 EndZ=0
    g1: Circle CenterX=0 CenterY=0 CenterZ=0 NormalX=0 NormalY=0 NormalZ=1 AngleXU=0 Radius=1
    g2: Circle CenterX=8 CenterY=6 CenterZ=0 NormalX=0 NormalY=0 NormalZ=1 AngleXU=0 Radius=1
    g3: BSplineCurve PolesCount=3 KnotsCount=2 Degree=2 IsPeriodic=0
    g4: GeomPoint X=0 Y=0 Z=0
    g5: GeomPoint X=8 Y=6 Z=0
    g6: LineSegment StartX=0 StartY=6 StartZ=0 EndX=8 EndY=6 EndZ=0
  constraints (14):
    c: Coincident(g0,g-1)
    c: Distance(g0) = 6
    c: Vertical(g0)
    c: Coincident(g3,g0)
    c: Weight(g1) = 1
    c: Equal(g1,g2)
    c: InternalAlignment(g1,g3)
    c: InternalAlignment(g2,g3)
    c: InternalAlignment(g4,g3)
    c: InternalAlignment(g5,g3)
    c: Block(g3)
    c: Coincident(g6,g0)
    c: Coincident(g6,g3)
    c: Horizontal(g6)
FEATURE [Sketcher::SketchObject] Sketch046
  FullyConstrained = true
  sketch-geometry (7):
    g0: LineSegment StartX=0 StartY=0 StartZ=0 EndX=0 EndY=6 EndZ=0
    g1: Circle CenterX=0 CenterY=0 CenterZ=0 NormalX=0 NormalY=0 NormalZ=1 AngleXU=0 Radius=1
    g2: Circle CenterX=8 CenterY=6 CenterZ=0 NormalX=0 NormalY=0 NormalZ=1 AngleXU=0 Radius=1
    g3: BSplineCurve PolesCount=3 KnotsCount=2 Degree=2 IsPeriodic=0
    g4: GeomPoint X=0 Y=0 Z=0
    g5: GeomPoint X=8 Y=6 Z=0
    g6: LineSegment StartX=0 StartY=6 StartZ=0 EndX=8 EndY=6 EndZ=0
  constraints (14):
    c: Coincident(g0,g-1)
    c: Distance(g0) = 6
    c: Vertical(g0)
    c: Coincident(g3,g0)
    c: Weight(g1) = 1
    c: Equal(g1,g2)
    c: InternalAlignment(g1,g3)
    c: InternalAlignment(g2,g3)
    c: InternalAlignment(g4,g3)
    c: InternalAlignment(g5,g3)
    c: Block(g3)
    c: Coincident(g6,g0)
    c: Coincident(g6,g3)
    c: Horizontal(g6)
FEATURE [Part::Extrusion] Extrude036  label="caseScrewPillarBracket014"
  Base = -> Sketch045
  Dir = (0,0,1)
  DirMode = 2
  FaceMakerClass = Part::FaceMakerBullseye
  LengthFwd = 2.4
  LengthRev = 0
  Placement = pos=(110.7,29,6.77) rot=(0,-1,0;1.5708rad)
  Solid = true
  Symmetric = false
FEATURE [Part::Extrusion] Extrude037  label="caseScrewPillarBracket015"
  Base = -> Sketch046
  Dir = (0,0,1)
  DirMode = 2
  FaceMakerClass = Part::FaceMakerBullseye
  LengthFwd = 2.4
  LengthRev = 0
  Placement = pos=(108.3,29,65.23) rot=(0,1,0;1.5708rad)
  Solid = true
  Symmetric = false
FEATURE [Part::Box] Box013  label="frontCaseScrewPillarBracket002"
  AttacherType = Attacher::AttachEngine3D
  Height = 2.4
  Length = 22
  Placement = pos=(87,28,2.3) rot=(0,0,1;0rad)
  Width = 7
FEATURE [Part::Box] Box014  label="frontCaseScrewPillarBracket003"
  AttacherType = Attacher::AttachEngine3D
  Height = 2.4
  Length = 22
  Placement = pos=(87,28,67.3) rot=(0,0,1;0rad)
  Width = 7
FEATURE [Part::Feature] Face087
  shape: bbox 4.8 x 30.2 x 2e-07 mm, 1 faces, 0 solids (baked)
FEATURE [Part::Revolution] Revolve091  label="frontCaseScrewPost004"
  Angle = 360
  Axis = (0,1,0)
  Base = (0,0,0)
  FaceMakerClass = Part::FaceMakerBullseye
  Placement = pos=(89.5,4.5,3.5) rot=(0,0,1;0rad)
  Solid = false
  Source = -> Face087
  Symmetric = false
FEATURE [Part::Feature] Face088
  shape: bbox 4.8 x 30.2 x 2e-07 mm, 1 faces, 0 solids (baked)
FEATURE [Part::Revolution] Revolve092  label="frontCaseScrewPost005"
  Angle = 360
  Axis = (0,1,0)
  Base = (0,0,0)
  FaceMakerClass = Part::FaceMakerBullseye
  Placement = pos=(89.5,4.5,68.5) rot=(0,0,1;0rad)
  Solid = false
  Source = -> Face088
  Symmetric = false
FEATURE [Part::Feature] Face089
  shape: bbox 3.5 x 30.2 x 2e-07 mm, 1 faces, 0 solids (baked)
FEATURE [Part::Revolution] Revolve093  label="backCaseScrewPost002"
  Angle = 360
  Axis = (0,1,0)
  Base = (0,0,0)
  FaceMakerClass = Part::FaceMakerBullseye
  Placement = pos=(12.5,4.5,10) rot=(0,0,1;0rad)
  Solid = false
  Source = -> Face089
  Symmetric = false
FEATURE [Part::Feature] Face090
  shape: bbox 3.5 x 30.2 x 2e-07 mm, 1 faces, 0 solids (baked)
FEATURE [Part::Revolution] Revolve094  label="backCaseScrewPost003"
  Angle = 360
  Axis = (0,1,0)
  Base = (0,0,0)
  FaceMakerClass = Part::FaceMakerBullseye
  Placement = pos=(12.5,4.5,62) rot=(0,0,1;0rad)
  Solid = false
  Source = -> Face090
  Symmetric = false
FEATURE [Part::Box] Box015  label="Cube011"
  AttacherType = Attacher::AttachEngine3D
  Height = 28.8
  Length = 3
  Placement = pos=(107.3,28,21.6) rot=(0,0,1;0rad)
  Width = 7
FEATURE [Part::Box] Box016  label="Cube012"
  AttacherType = Attacher::AttachEngine3D
  Height = 3
  Length = 7.4
  Placement = pos=(107.3,28,18.6) rot=(0,0,1;0rad)
  Width = 7
FEATURE [Part::Box] Box017  label="Cube013"
  AttacherType = Attacher::AttachEngine3D
  Height = 3
  Length = 7.4
  Placement = pos=(107.3,28,50.4) rot=(0,0,1;0rad)
  Width = 7
FEATURE [Part::Cylinder] Cylinder024
  Angle = 360
  AttacherType = Attacher::AttachEngine3D
  Height = 20
  Placement = pos=(0,0,36.15) rot=(0,0,1;0rad)
  Radius = 14.3
FEATURE [Part::Cylinder] Cylinder025
  Angle = 360
  AttacherType = Attacher::AttachEngine3D
  Height = 10
  Placement = pos=(0,0,36.15) rot=(0,0,1;0rad)
  Radius = 4
FEATURE [Part::MultiFuse] Fusion066  label="removeToCreteHoleForPlugHousing009"
  Placement = pos=(70,19,36) rot=(0,1,0;1.5708rad)
  Shapes = -> [Cylinder024,Cylinder025]
FEATURE [Part::MultiFuse] Fusion065  label="plugHousingBracketHolder002"
  Shapes = -> [Box017,Box015,Box016]
FEATURE [Part::Cut] Cut025  label="plugHousingBracketHolder003"
  Base = -> Fusion065
  Placement = pos=(7,0,0) rot=(0,0,1;0rad)
  Tool = -> Fusion066
FEATURE [Sketcher::SketchObject] Sketch047
  FullyConstrained = false
  Placement = pos=(0,0,0) rot=(1,0,0;1.5708rad)
  sketch-geometry (24):
    g0: ArcOfCircle CenterX=-4 CenterY=-10.5 CenterZ=0 NormalX=0 NormalY=0 NormalZ=1 AngleXU=0 Radius=1.5 StartAngle=6e-16 EndAngle=3.14159
    g1: ArcOfCircle CenterX=-34.2 CenterY=-10.5 CenterZ=0 NormalX=0 NormalY=0 NormalZ=1 AngleXU=0 Radius=1.5 StartAngle=0 EndAngle=3.14159
    g2: ArcOfCircle CenterX=-34.2 CenterY=-27.7 CenterZ=0 NormalX=0 NormalY=0 NormalZ=1 AngleXU=0 Radius=1.5 StartAngle=3.14159 EndAngle=6.28319
    g3: ArcOfCircle CenterX=-4 CenterY=-27.7 CenterZ=0 NormalX=0 NormalY=0 NormalZ=1 AngleXU=0 Radius=1.5 StartAngle=3.1416 EndAngle=6.28319
    g4: ArcOfCircle CenterX=-10 CenterY=-4.3 CenterZ=0 NormalX=0 NormalY=0 NormalZ=1 AngleXU=0 Radius=1.5 StartAngle=2e-16 EndAngle=3.14159
    g5: ArcOfCircle CenterX=-16.1 CenterY=-1.8 CenterZ=0 NormalX=0 NormalY=0 NormalZ=1 AngleXU=0 Radius=1.5 StartAngle=5e-16 EndAngle=3.14159
    g6: ArcOfCircle CenterX=-22.1 CenterY=-1.8 CenterZ=0 NormalX=0 NormalY=0 NormalZ=1 AngleXU=0 Radius=1.5 StartAngle=5e-16 EndAngle=3.14159
    g7: ArcOfCircle CenterX=-28.2 CenterY=-4.3 CenterZ=0 NormalX=0 NormalY=0 NormalZ=1 AngleXU=0 Radius=1.5 StartAngle=2e-16 EndAngle=3.14159
    g8: ArcOfCircle CenterX=-10 CenterY=-33.9 CenterZ=0 NormalX=0 NormalY=0 NormalZ=1 AngleXU=0 Radius=1.5 StartAngle=3.14159 EndAngle=6.28319
    g9: ArcOfCircle CenterX=-16.1 CenterY=-36.4 CenterZ=0 NormalX=0 NormalY=0 NormalZ=1 AngleXU=0 Radius=1.5 StartAngle=3.14159 EndAngle=6.28319
    g10: ArcOfCircle CenterX=-22.1 CenterY=-36.4 CenterZ=0 NormalX=0 NormalY=0 NormalZ=1 AngleXU=0 Radius=1.5 StartAngle=3.14159 EndAngle=6.28319
    g11: ArcOfCircle CenterX=-28.2 CenterY=-33.9 CenterZ=0 NormalX=0 NormalY=0 NormalZ=1 AngleXU=0 Radius=1.5 StartAngle=3.14159 EndAngle=6.28319
    g12: LineSegment StartX=-35.7 StartY=-10.5 StartZ=0 EndX=-35.7 EndY=-27.7 EndZ=0
    g13: LineSegment StartX=-32.7 StartY=-10.5 StartZ=0 EndX=-32.7 EndY=-27.7 EndZ=0
    g14: LineSegment StartX=-29.7 StartY=-33.9 StartZ=0 EndX=-29.7 EndY=-4.3 EndZ=0
    g15: LineSegment StartX=-26.7 StartY=-33.9 StartZ=0 EndX=-26.7 EndY=-4.3 EndZ=0
    g16: LineSegment StartX=-2.5 StartY=-10.5 StartZ=0 EndX=-2.5 EndY=-27.7 EndZ=0
    g17: LineSegment StartX=-8.5 StartY=-4.3 StartZ=0 EndX=-8.5 EndY=-33.9 EndZ=0
    g18: LineSegment StartX=-5.5 StartY=-10.5 StartZ=0 EndX=-5.5 EndY=-27.7 EndZ=0
    g19: LineSegment StartX=-11.5 StartY=-4.3 StartZ=0 EndX=-11.5 EndY=-33.9 EndZ=0
    g20: LineSegment StartX=-14.6 StartY=-1.8 StartZ=0 EndX=-14.6 EndY=-36.4 EndZ=0
    g21: LineSegment StartX=-17.6 StartY=-1.8 StartZ=0 EndX=-17.6 EndY=-36.4 EndZ=0
    g22: LineSegment StartX=-20.6 StartY=-36.4 StartZ=0 EndX=-20.6 EndY=-1.8 EndZ=0
    g23: LineSegment StartX=-23.6 StartY=-1.8 StartZ=0 EndX=-23.6 EndY=-36.4 EndZ=0
  constraints (48):
    c: Block(g0)
    c: Block(g1)
    c: Block(g2)
    c: Block(g3)
    c: Block(g4)
    c: Block(g5)
    c: Block(g6)
    c: Block(g7)
    c: Block(g8)
    c: Block(g9)
    c: Block(g10)
    c: Block(g11)
    c: Coincident(g12,g1)
    c: Coincident(g12,g2)
    c: Vertical(g12)
    c: Coincident(g13,g1)
    c: Coincident(g13,g2)
    c: Vertical(g13)
    c: Coincident(g14,g11)
    c: Coincident(g14,g7)
    c: Vertical(g14)
    c: Coincident(g15,g11)
    c: Coincident(g15,g7)
    c: Vertical(g15)
    c: Coincident(g16,g0)
    c: Coincident(g16,g3)
    c: Vertical(g16)
    c: Coincident(g17,g4)
    c: Coincident(g17,g8)
    c: Vertical(g17)
    c: Coincident(g18,g0)
    c: Coincident(g18,g3)
    c: Vertical(g18)
    c: Coincident(g19,g4)
    c: Coincident(g19,g8)
    c: Vertical(g19)
    c: Coincident(g20,g5)
    c: Coincident(g20,g9)
    c: Vertical(g20)
    c: Coincident(g21,g5)
    c: Coincident(g21,g9)
    c: Vertical(g21)
    c: Coincident(g22,g10)
    c: Coincident(g22,g6)
    c: Vertical(g22)
    c: Coincident(g23,g6)
    c: Coincident(g23,g10)
    c: Vertical(g23)
FEATURE [Part::Extrusion] Extrude038  label="removeToCreateFanGrillHoles001"
  Base = -> Sketch047
  Dir = (0,-1,6e-16)
  DirMode = 2
  FaceMakerClass = Part::FaceMakerBullseye
  LengthFwd = 10
  LengthRev = 0
  Placement = pos=(65.4,44,54.82) rot=(0,0,1;0rad)
  Solid = true
  Symmetric = false
FEATURE [Part::Feature] Wire004
  shape: bbox 11 x 5.2 x 2e-07 mm, 0 faces, 0 solids (baked)
FEATURE [Part::Revolution] Revolve095
  Angle = 360
  Axis = (0,1,0)
  Base = (0,0,0)
  FaceMakerClass = Part::FaceMakerBullseye
  Placement = pos=(30.3,38,19.7) rot=(0,0,1;0rad)
  Solid = true
  Source = -> Wire004
  Symmetric = false
FEATURE [Part::Feature] Wire005
  shape: bbox 11 x 5.2 x 2e-07 mm, 0 faces, 0 solids (baked)
FEATURE [Part::Revolution] Revolve096
  Angle = 360
  Axis = (0,1,0)
  Base = (0,0,0)
  FaceMakerClass = Part::FaceMakerBullseye
  Placement = pos=(30.3,38,51.7) rot=(0,0,1;0rad)
  Solid = true
  Source = -> Wire005
  Symmetric = false
FEATURE [Part::Feature] Wire006
  shape: bbox 11 x 5.2 x 2e-07 mm, 0 faces, 0 solids (baked)
FEATURE [Part::Revolution] Revolve097
  Angle = 360
  Axis = (0,1,0)
  Base = (0,0,0)
  FaceMakerClass = Part::FaceMakerBullseye
  Placement = pos=(62.3,38,51.7) rot=(0,0,1;0rad)
  Solid = true
  Source = -> Wire006
  Symmetric = false
FEATURE [Part::Feature] Wire007
  shape: bbox 11 x 5.2 x 2e-07 mm, 0 faces, 0 solids (baked)
FEATURE [Part::Revolution] Revolve098
  Angle = 360
  Axis = (0,1,0)
  Base = (0,0,0)
  FaceMakerClass = Part::FaceMakerBullseye
  Placement = pos=(62.3,38,19.7) rot=(0,0,1;0rad)
  Solid = true
  Source = -> Wire007
  Symmetric = false
FEATURE [Part::MultiFuse] Fusion067  label="fanScrewHousing002"
  Shapes = -> [Revolve098,Revolve097,Revolve096,Revolve095]
FEATURE [Part::Feature] Face091 .. Face094  x4 (patterned run collapsed; names and placements below)
  shape: bbox 3.5 x 17.8 x 2e-07 mm, 1 faces, 0 solids (baked)
FEATURE [Part::Revolution] Revolve099  label="removeToCreateScrewAndThreadedInsertHole026"
  Angle = 360
  Axis = (0,1,0)
  Base = (0,0,0)
  FaceMakerClass = Part::FaceMakerBullseye
  Placement = pos=(62.3,30.3,19.7) rot=(0,0,1;0rad)
  Solid = false
  Source = -> Face091
  Symmetric = false
FEATURE [Part::Revolution] Revolve100  label="removeToCreateScrewAndThreadedInsertHole027"
  Angle = 360
  Axis = (0,1,0)
  Base = (0,0,0)
  FaceMakerClass = Part::FaceMakerBullseye
  Placement = pos=(62.3,30.3,51.7) rot=(0,0,1;0rad)
  Solid = false
  Source = -> Face092
  Symmetric = false
FEATURE [Part::Revolution] Revolve101  label="removeToCreateScrewAndThreadedInsertHole028"
  Angle = 360
  Axis = (0,1,0)
  Base = (0,0,0)
  FaceMakerClass = Part::FaceMakerBullseye
  Placement = pos=(30.3,30.3,19.7) rot=(0,0,1;0rad)
  Solid = false
  Source = -> Face093
  Symmetric = false
FEATURE [Part::Revolution] Revolve102  label="removeToCreateScrewAndThreadedInsertHole029"
  Angle = 360
  Axis = (0,1,0)
  Base = (0,0,0)
  FaceMakerClass = Part::FaceMakerBullseye
  Placement = pos=(30.3,30.3,51.7) rot=(0,0,1;0rad)
  Solid = false
  Source = -> Face094
  Symmetric = false
FEATURE [Part::MultiFuse] Fusion068  label="createThreadedInsertHolesForFan002"
  Shapes = -> [Revolve099,Revolve100,Revolve101,Revolve102]
FEATURE [Part::Cut] Cut026  label="fanScrewHousing003"
  Base = -> Fusion067
  Tool = -> Fusion068
FEATURE [Sketcher::SketchObject] Sketch048
  FullyConstrained = false
  Placement = pos=(0,0,0) rot=(1,0,0;1.5708rad)
  sketch-geometry (24):
    g0: ArcOfCircle CenterX=-4 CenterY=-10.5 CenterZ=0 NormalX=0 NormalY=0 NormalZ=1 AngleXU=0 Radius=1.5 StartAngle=6e-16 EndAngle=3.14159
    g1: ArcOfCircle CenterX=-34.2 CenterY=-10.5 CenterZ=0 NormalX=0 NormalY=0 NormalZ=1 AngleXU=0 Radius=1.5 StartAngle=0 EndAngle=3.14159
    g2: ArcOfCircle CenterX=-34.2 CenterY=-27.7 CenterZ=0 NormalX=0 NormalY=0 NormalZ=1 AngleXU=0 Radius=1.5 StartAngle=3.14159 EndAngle=6.28319
    g3: ArcOfCircle CenterX=-4 CenterY=-27.7 CenterZ=0 NormalX=0 NormalY=0 NormalZ=1 AngleXU=0 Radius=1.5 StartAngle=3.1416 EndAngle=6.28319
    g4: ArcOfCircle CenterX=-10 CenterY=-4.3 CenterZ=0 NormalX=0 NormalY=0 NormalZ=1 AngleXU=0 Radius=1.5 StartAngle=2e-16 EndAngle=3.14159
    g5: ArcOfCircle CenterX=-16.1 CenterY=-1.8 CenterZ=0 NormalX=0 NormalY=0 NormalZ=1 AngleXU=0 Radius=1.5 StartAngle=5e-16 EndAngle=3.14159
    g6: ArcOfCircle CenterX=-22.1 CenterY=-1.8 CenterZ=0 NormalX=0 NormalY=0 NormalZ=1 AngleXU=0 Radius=1.5 StartAngle=5e-16 EndAngle=3.14159
    g7: ArcOfCircle CenterX=-28.2 CenterY=-4.3 CenterZ=0 NormalX=0 NormalY=0 NormalZ=1 AngleXU=0 Radius=1.5 StartAngle=2e-16 EndAngle=3.14159
    g8: ArcOfCircle CenterX=-10 CenterY=-33.9 CenterZ=0 NormalX=0 NormalY=0 NormalZ=1 AngleXU=0 Radius=1.5 StartAngle=3.14159 EndAngle=6.28319
    g9: ArcOfCircle CenterX=-16.1 CenterY=-36.4 CenterZ=0 NormalX=0 NormalY=0 NormalZ=1 AngleXU=0 Radius=1.5 StartAngle=3.14159 EndAngle=6.28319
    g10: ArcOfCircle CenterX=-22.1 CenterY=-36.4 CenterZ=0 NormalX=0 NormalY=0 NormalZ=1 AngleXU=0 Radius=1.5 StartAngle=3.14159 EndAngle=6.28319
    g11: ArcOfCircle CenterX=-28.2 CenterY=-33.9 CenterZ=0 NormalX=0 NormalY=0 NormalZ=1 AngleXU=0 Radius=1.5 StartAngle=3.14159 EndAngle=6.28319
    g12: LineSegment StartX=-35.7 StartY=-10.5 StartZ=0 EndX=-35.7 EndY=-27.7 EndZ=0
    g13: LineSegment StartX=-32.7 StartY=-10.5 StartZ=0 EndX=-32.7 EndY=-27.7 EndZ=0
    g14: LineSegment StartX=-29.7 StartY=-33.9 StartZ=0 EndX=-29.7 EndY=-4.3 EndZ=0
    g15: LineSegment StartX=-26.7 StartY=-33.9 StartZ=0 EndX=-26.7 EndY=-4.3 EndZ=0
    g16: LineSegment StartX=-2.5 StartY=-10.5 StartZ=0 EndX=-2.5 EndY=-27.7 EndZ=0
    g17: LineSegment StartX=-8.5 StartY=-4.3 StartZ=0 EndX=-8.5 EndY=-33.9 EndZ=0
    g18: LineSegment StartX=-5.5 StartY=-10.5 StartZ=0 EndX=-5.5 EndY=-27.7 EndZ=0
    g19: LineSegment StartX=-11.5 StartY=-4.3 StartZ=0 EndX=-11.5 EndY=-33.9 EndZ=0
    g20: LineSegment StartX=-14.6 StartY=-1.8 StartZ=0 EndX=-14.6 EndY=-36.4 EndZ=0
    g21: LineSegment StartX=-17.6 StartY=-1.8 StartZ=0 EndX=-17.6 EndY=-36.4 EndZ=0
    g22: LineSegment StartX=-20.6 StartY=-36.4 StartZ=0 EndX=-20.6 EndY=-1.8 EndZ=0
    g23: LineSegment StartX=-23.6 StartY=-1.8 StartZ=0 EndX=-23.6 EndY=-36.4 EndZ=0
  constraints (48):
    c: Block(g0)
    c: Block(g1)
    c: Block(g2)
    c: Block(g3)
    c: Block(g4)
    c: Block(g5)
    c: Block(g6)
    c: Block(g7)
    c: Block(g8)
    c: Block(g9)
    c: Block(g10)
    c: Block(g11)
    c: Coincident(g12,g1)
    c: Coincident(g12,g2)
    c: Vertical(g12)
    c: Coincident(g13,g1)
    c: Coincident(g13,g2)
    c: Vertical(g13)
    c: Coincident(g14,g11)
    c: Coincident(g14,g7)
    c: Vertical(g14)
    c: Coincident(g15,g11)
    c: Coincident(g15,g7)
    c: Vertical(g15)
    c: Coincident(g16,g0)
    c: Coincident(g16,g3)
    c: Vertical(g16)
    c: Coincident(g17,g4)
    c: Coincident(g17,g8)
    c: Vertical(g17)
    c: Coincident(g18,g0)
    c: Coincident(g18,g3)
    c: Vertical(g18)
    c: Coincident(g19,g4)
    c: Coincident(g19,g8)
    c: Vertical(g19)
    c: Coincident(g20,g5)
    c: Coincident(g20,g9)
    c: Vertical(g20)
    c: Coincident(g21,g5)
    c: Coincident(g21,g9)
    c: Vertical(g21)
    c: Coincident(g22,g10)
    c: Coincident(g22,g6)
    c: Vertical(g22)
    c: Coincident(g23,g6)
    c: Coincident(g23,g10)
    c: Vertical(g23)
FEATURE [Part::Extrusion] Extrude039  label="removeToCreateFanGrillHoles002"
  Base = -> Sketch048
  Dir = (0,-1,6e-16)
  DirMode = 2
  FaceMakerClass = Part::FaceMakerBullseye
  LengthFwd = 10
  LengthRev = 0
  Placement = pos=(65.4,44,54.82) rot=(0,0,1;0rad)
  Solid = true
  Symmetric = false
FEATURE [Part::Cut] Cut027  label="fanScrewHousing004"
  Base = -> Cut026
  Tool = -> Extrude038
FEATURE [Part::Cut] Cut028  label="top014"
  Base = -> Fillet026
  Tool = -> Extrude039
FEATURE [Part::Feature] Face095 .. Face098  x4 (patterned run collapsed; names and placements below)
  shape: bbox 3.5 x 17.8 x 2e-07 mm, 1 faces, 0 solids (baked)
FEATURE [Part::Revolution] Revolve103  label="removeToCreateScrewAndThreadedInsertHole030"
  Angle = 360
  Axis = (0,1,0)
  Base = (0,0,0)
  FaceMakerClass = Part::FaceMakerBullseye
  Placement = pos=(62.3,30.3,19.7) rot=(0,0,1;0rad)
  Solid = false
  Source = -> Face095
  Symmetric = false
FEATURE [Part::Revolution] Revolve104  label="removeToCreateScrewAndThreadedInsertHole031"
  Angle = 360
  Axis = (0,1,0)
  Base = (0,0,0)
  FaceMakerClass = Part::FaceMakerBullseye
  Placement = pos=(62.3,30.3,51.7) rot=(0,0,1;0rad)
  Solid = false
  Source = -> Face096
  Symmetric = false
FEATURE [Part::Revolution] Revolve105  label="removeToCreateScrewAndThreadedInsertHole032"
  Angle = 360
  Axis = (0,1,0)
  Base = (0,0,0)
  FaceMakerClass = Part::FaceMakerBullseye
  Placement = pos=(30.3,30.3,19.7) rot=(0,0,1;0rad)
  Solid = false
  Source = -> Face097
  Symmetric = false
FEATURE [Part::Revolution] Revolve106  label="removeToCreateScrewAndThreadedInsertHole033"
  Angle = 360
  Axis = (0,1,0)
  Base = (0,0,0)
  FaceMakerClass = Part::FaceMakerBullseye
  Placement = pos=(30.3,30.3,51.7) rot=(0,0,1;0rad)
  Solid = false
  Source = -> Face098
  Symmetric = false
FEATURE [Part::MultiFuse] Fusion069  label="createThreadedInsertHolesForFan003"
  Shapes = -> [Revolve103,Revolve104,Revolve105,Revolve106]
FEATURE [Part::Cut] Cut029  label="top015"
  Base = -> Cut028
  Tool = -> Fusion054
FEATURE [Part::Cut] Cut030  label="fanScrewHousing005"
  Base = -> Cut027
  Tool = -> Fusion069
FEATURE [Part::Cylinder] Cylinder026  label="removeToCreteHoleForPlugHousing010"
  Angle = 360
  AttacherType = Attacher::AttachEngine3D
  Height = 20
  Placement = pos=(-2,19,36) rot=(0,1,0;1.5708rad)
  Radius = 14.3
FEATURE [Part::Box] Box018  label="removeToCreteHoleForPlugHousing011"
  AttacherType = Attacher::AttachEngine3D
  Height = 28.6
  Length = 10
  Placement = pos=(-2,0,21.7) rot=(0,0,1;0rad)
  Width = 19
FEATURE [Part::Box] Box019  label="wireHolderBottomCaseBit"
  AttacherType = Attacher::AttachEngine3D
  Height = 28
  Length = 3
  Placement = pos=(0,0,22) rot=(0,0,1;0rad)
  Width = 21
FEATURE [Part::Cylinder] Cylinder027  label="removeToCreteHoleForPlugHousing012"
  Angle = 360
  AttacherType = Attacher::AttachEngine3D
  Height = 20
  Placement = pos=(-2,19,36) rot=(0,1,0;1.5708rad)
  Radius = 14.3
FEATURE [Part::Cut] Cut031  label="wireHolderBottomCaseBit001"
  Base = -> Box019
  Tool = -> Cylinder027
FEATURE [Part::MultiFuse] Fusion070  label="removeToCreteHoleForPlugHousing013"
  Shapes = -> [Box018,Cylinder026]
FEATURE [Part::Cut] Cut032  label="top016"
  Base = -> Cut029
  Tool = -> Fusion070
FEATURE [Part::Cylinder] Cylinder028
  Angle = 360
  AttacherType = Attacher::AttachEngine3D
  Height = 20
  Placement = pos=(0,0,36.15) rot=(0,0,1;0rad)
  Radius = 14.3
FEATURE [Part::Cylinder] Cylinder029
  Angle = 360
  AttacherType = Attacher::AttachEngine3D
  Height = 10
  Placement = pos=(0,0,36.15) rot=(0,0,1;0rad)
  Radius = 4
FEATURE [Part::MultiFuse] Fusion071  label="removeToCreteHoleForPlugHousing014"
  Placement = pos=(70,19,36) rot=(0,1,0;1.5708rad)
  Shapes = -> [Cylinder028,Cylinder029]
FEATURE [Sketcher::SketchObject] Sketch049  label="topSketch011"
  FullyConstrained = true
  sketch-geometry (4):
    g0: ArcOfCircle CenterX=105 CenterY=19 CenterZ=0 NormalX=0 NormalY=0 NormalZ=1 AngleXU=0 Radius=20.6155 StartAngle=5.54125 EndAngle=6.28319
    g1: ArcOfCircle CenterX=105 CenterY=19 CenterZ=0 NormalX=0 NormalY=0 NormalZ=1 AngleXU=0 Radius=13 StartAngle=5.54125 EndAngle=6.28319
    g2: LineSegment StartX=118 StartY=19 StartZ=0 EndX=125.616 EndY=19 EndZ=0
    g3: LineSegment StartX=114.583 StartY=10.2157 StartZ=0 EndX=120.197 EndY=5.06982 EndZ=0
  constraints (7):
    c: Block(g0)
    c: Block(g1)
    c: Coincident(g2,g1)
    c: Coincident(g2,g0)
    c: Horizontal(g2)
    c: Coincident(g3,g1)
    c: Coincident(g3,g0)
FEATURE [Part::Box] Box020  label="removeToCreteHoleForPlugHousing015"
  AttacherType = Attacher::AttachEngine3D
  Height = 28.6
  Length = 20
  Placement = pos=(106.15,0,21.7) rot=(0,0,1;0rad)
  Width = 19
FEATURE [Part::MultiFuse] Fusion072  label="removeToCreteHoleForPlugHousing016"
  Shapes = -> [Box020,Fusion071]
FEATURE [Part::Cut] Cut033  label="removeToCreteHoleForPlugHousing017"
  Base = -> Cut032
  Tool = -> Fusion072
FEATURE [Part::Cylinder] Cylinder030
  Angle = 360
  AttacherType = Attacher::AttachEngine3D
  Height = 20
  Placement = pos=(0,0,36.15) rot=(0,0,1;0rad)
  Radius = 14.3
FEATURE [Part::Cylinder] Cylinder031
  Angle = 360
  AttacherType = Attacher::AttachEngine3D
  Height = 10
  Placement = pos=(0,0,36.15) rot=(0,0,1;0rad)
  Radius = 4
FEATURE [Part::Box] Box021  label="removeToCreteHoleForPlugHousing019"
  AttacherType = Attacher::AttachEngine3D
  Height = 28.6
  Length = 20
  Placement = pos=(106.15,0,21.7) rot=(0,0,1;0rad)
  Width = 19
FEATURE [Part::MultiFuse] Fusion074  label="removeToCreteHoleForPlugHousing020"
  Placement = pos=(70,19,36) rot=(0,1,0;1.5708rad)
  Shapes = -> [Cylinder030,Cylinder031]
FEATURE [Part::MultiFuse] Fusion073  label="removeToCreteHoleForPlugHousing018"
  Placement = pos=(0,0,28.3) rot=(0,0,1;0rad)
  Shapes = -> [Box021,Fusion074]
FEATURE [Part::Cylinder] Cylinder032
  Angle = 360
  AttacherType = Attacher::AttachEngine3D
  Height = 20
  Placement = pos=(0,0,36.15) rot=(0,0,1;0rad)
  Radius = 14.3
FEATURE [Part::Cylinder] Cylinder033
  Angle = 360
  AttacherType = Attacher::AttachEngine3D
  Height = 10
  Placement = pos=(0,0,36.15) rot=(0,0,1;0rad)
  Radius = 4
FEATURE [Part::Box] Box022  label="removeToCreteHoleForPlugHousing021"
  AttacherType = Attacher::AttachEngine3D
  Height = 28.6
  Length = 20
  Placement = pos=(106.15,0,21.7) rot=(0,0,1;0rad)
  Width = 19
FEATURE [Part::MultiFuse] Fusion076  label="removeToCreteHoleForPlugHousing023"
  Placement = pos=(70,19,36) rot=(0,1,0;1.5708rad)
  Shapes = -> [Cylinder032,Cylinder033]
FEATURE [Part::MultiFuse] Fusion075  label="removeToCreteHoleForPlugHousing022"
  Placement = pos=(0,0,-28.3) rot=(0,0,1;0rad)
  Shapes = -> [Box022,Fusion076]
FEATURE [Part::MultiFuse] Fusion077  label="removeToCreatePlugHousingBottomBit"
  Shapes = -> [Fusion075,Fusion073]
FEATURE [Part::Cylinder] Cylinder034
  Angle = 360
  AttacherType = Attacher::AttachEngine3D
  Height = 20
  Placement = pos=(0,0,36.15) rot=(0,0,1;0rad)
  Radius = 14
FEATURE [Part::Cylinder] Cylinder035
  Angle = 360
  AttacherType = Attacher::AttachEngine3D
  Height = 10
  Placement = pos=(0,0,36.15) rot=(0,0,1;0rad)
  Radius = 4
FEATURE [Part::MultiFuse] Fusion078  label="removeToCreteHoleForPlugHousing024"
  Placement = pos=(70,19,36) rot=(0,1,0;1.5708rad)
  Shapes = -> [Cylinder034,Cylinder035]
FEATURE [Part::MultiFuse] Fusion079  label="removeToCreatePlugHousingBottomBit001"
  Shapes = -> [Fusion078,Fusion077]
FEATURE [Part::Extrusion] Extrude040  label="bottomPlugHousingBit"
  Base = -> Sketch049
  Dir = (0,0,1)
  DirMode = 2
  FaceMakerClass = Part::FaceMakerBullseye
  LengthFwd = 72
  LengthRev = 0
  Solid = true
  Symmetric = false
FEATURE [Part::Cut] Cut034  label="bottomPlugHousingBit001"
  Base = -> Extrude040
  Placement = pos=(-0.09,0,0) rot=(0,0,1;0rad)
  Tool = -> Fusion079
FEATURE [Part::Box] Box023  label="Cube014"
  AttacherType = Attacher::AttachEngine3D
  Height = 16
  Length = 8
  Placement = pos=(12.7,31.52,28) rot=(0,0,1;0rad)
  Width = 4
FEATURE [Part::Cylinder] Cylinder036
  Angle = 360
  AttacherType = Attacher::AttachEngine3D
  Height = 10
  Placement = pos=(0,0,36.15) rot=(0,0,1;0rad)
  Radius = 4
FEATURE [Part::Cylinder] Cylinder037
  Angle = 360
  AttacherType = Attacher::AttachEngine3D
  Height = 20
  Placement = pos=(0,0,36.15) rot=(0,0,1;0rad)
  Radius = 8.2
FEATURE [Part::MultiFuse] Fusion080  label="removeToCreteHoleForPlugHousing025"
  Placement = pos=(-42,19,36) rot=(0,1,0;1.5708rad)
  Shapes = -> [Cylinder037,Cylinder036]
FEATURE [Sketcher::SketchObject] Sketch050  label="topSketch012"
  FullyConstrained = true
  sketch-geometry (4):
    g0: LineSegment StartX=16.8446 StartY=31.512 StartZ=0 EndX=16.3251 EndY=34.4666 EndZ=0
    g1: ArcOfCircle CenterX=19 CenterY=19.2524 CenterZ=0 NormalX=0 NormalY=0 NormalZ=1 AngleXU=0 Radius=15.4476 StartAngle=1.74483 EndAngle=2.72717
    g2: ArcOfCircle CenterX=19 CenterY=19.2524 CenterZ=0 NormalX=0 NormalY=0 NormalZ=1 AngleXU=0 Radius=12.4476 StartAngle=1.74483 EndAngle=2.73189
    g3: LineSegment StartX=4.86004 StartY=25.4725 StartZ=0 EndX=7.58253 EndY=24.2107 EndZ=0
  constraints (7):
    c: Block(g0)
    c: Coincident(g1,g0)
    c: Coincident(g2,g0)
    c: Coincident(g3,g1)
    c: Coincident(g3,g2)
    c: Block(g1)
    c: Block(g2)
FEATURE [Part::Extrusion] Extrude041
  Base = -> Sketch050
  Dir = (0,0,1)
  DirMode = 2
  FaceMakerClass = Part::FaceMakerBullseye
  LengthFwd = 10.6
  LengthRev = 0
  Placement = pos=(0,0,31) rot=(0,0,1;0rad)
  Solid = true
  Symmetric = false
FEATURE [Part::Cut] Cut035
  Base = -> Extrude041
  Placement = pos=(0,0,-0.3) rot=(0,0,1;0rad)
  Tool = -> Fusion080
FEATURE [Part::Cut] Cut036
  Base = -> Box023
  Tool = -> Cut035
FEATURE [Part::Fillet] Fillet027
  Base = -> Cut036
  Edges = 1 edges r=0.7: [Edge13]
FEATURE [Part::Fillet] Fillet028
  Base = -> Fillet027
  Edges = 1 edges r=0.7: [Edge13]
FEATURE [Part::Fillet] Fillet029
  Base = -> Fillet028
  Edges = 1 edges r=0.7: [Edge16]
FEATURE [Part::Fillet] Fillet030
  Base = -> Fillet029
  Edges = 1 edges r=0.7: [Edge11]
FEATURE [Part::Fillet] Fillet031
  Base = -> Fillet030
  Edges = 1 edges r=0.7: [Edge10]
FEATURE [Part::Fillet] Fillet032
  Base = -> Fillet031
  Edges = 1 edges r=1.2: [Edge5]
FEATURE [Part::Fillet] Fillet033
  Base = -> Fillet032
  Edges = 1 edges r=1.2: [Edge12]
FEATURE [Part::Fillet] Fillet034  label="wireHousingRetainer"
  Base = -> Fillet033
  Edges = 1 edges r=2: [Edge1]
  Placement = pos=(0.3,0,0) rot=(0,0,1;0rad)
FEATURE [Part::Feature] Face099
  shape: bbox 3.5 x 17.8 x 2e-07 mm, 1 faces, 0 solids (baked)
FEATURE [Part::Revolution] Revolve107  label="removeToCreateScrewAndThreadedInsertHole034"
  Angle = 360
  Axis = (0,1,0)
  Base = (0,0,0)
  FaceMakerClass = Part::FaceMakerBullseye
  Placement = pos=(12.5,0,10) rot=(0,0,1;0rad)
  Solid = false
  Source = -> Face099
  Symmetric = false
FEATURE [Part::Feature] Face100
  shape: bbox 3.5 x 17.8 x 2e-07 mm, 1 faces, 0 solids (baked)
FEATURE [Part::Revolution] Revolve108  label="removeToCreateScrewAndThreadedInsertHole035"
  Angle = 360
  Axis = (0,1,0)
  Base = (0,0,0)
  FaceMakerClass = Part::FaceMakerBullseye
  Placement = pos=(12.5,0,62) rot=(0,0,1;0rad)
  Solid = false
  Source = -> Face100
  Symmetric = false
FEATURE [Part::Feature] Face101
  shape: bbox 3.5 x 17.8 x 2e-07 mm, 1 faces, 0 solids (baked)
FEATURE [Part::Revolution] Revolve109  label="removeToCreateScrewAndThreadedInsertHole036"
  Angle = 360
  Axis = (0,1,0)
  Base = (0,0,0)
  FaceMakerClass = Part::FaceMakerBullseye
  Placement = pos=(89.5,0,68.5) rot=(0,0,1;0rad)
  Solid = false
  Source = -> Face101
  Symmetric = false
FEATURE [Part::Feature] Face102
  shape: bbox 3.5 x 17.8 x 2e-07 mm, 1 faces, 0 solids (baked)
FEATURE [Part::Revolution] Revolve110  label="removeToCreateScrewAndThreadedInsertHole037"
  Angle = 360
  Axis = (0,1,0)
  Base = (0,0,0)
  FaceMakerClass = Part::FaceMakerBullseye
  Placement = pos=(89.5,0,3.5) rot=(0,0,1;0rad)
  Solid = false
  Source = -> Face102
  Symmetric = false
FEATURE [Part::Feature] Face103
  shape: bbox 3.5 x 17.8 x 2e-07 mm, 1 faces, 0 solids (baked)
FEATURE [Part::Revolution] Revolve111  label="removeToCreateScrewAndThreadedInsertHole038"
  Angle = 360
  Axis = (0,1,0)
  Base = (0,0,0)
  FaceMakerClass = Part::FaceMakerBullseye
  Placement = pos=(109.5,4.7,3.5) rot=(0,0,1;0rad)
  Solid = false
  Source = -> Face103
  Symmetric = false
FEATURE [Part::Feature] Face104
  shape: bbox 3.5 x 17.8 x 2e-07 mm, 1 faces, 0 solids (baked)
FEATURE [Part::Revolution] Revolve112  label="removeToCreateScrewAndThreadedInsertHole039"
  Angle = 360
  Axis = (0,1,0)
  Base = (0,0,0)
  FaceMakerClass = Part::FaceMakerBullseye
  Placement = pos=(109.5,4.7,68.5) rot=(0,0,1;0rad)
  Solid = false
  Source = -> Face104
  Symmetric = false
FEATURE [Part::MultiFuse] Fusion081  label="removeToCreateScrewAndThreadedInsertHole040"
  Shapes = -> [Revolve107,Revolve108,Revolve109,Revolve110,Revolve111,Revolve112]
FEATURE [Part::MultiFuse] Fusion082  label="casePillars002"
  Shapes = -> [Revolve094,Revolve092,Revolve090,Revolve089,Revolve091,Revolve093]
FEATURE [Part::Cut] Cut037  label="casePillars003"
  Base = -> Fusion082
  Tool = -> Fusion081
FEATURE [Sketcher::SketchObject] Sketch051
  FullyConstrained = true
  Placement = pos=(117,19,0) rot=(0.57735,0.57735,0.57735;2.0944rad)
  sketch-geometry (48):
    g0: LineSegment StartX=-49.19 StartY=69.25 StartZ=0 EndX=-49.19 EndY=66.25 EndZ=0
    g1: LineSegment StartX=-49.19 StartY=63.5 StartZ=0 EndX=-49.19 EndY=60.5 EndZ=0
    g2: LineSegment StartX=-49.19 StartY=57.75 StartZ=0 EndX=-49.19 EndY=54.75 EndZ=0
    g3: LineSegment StartX=-49.19 StartY=52 StartZ=0 EndX=-49.19 EndY=49 EndZ=0
    g4: LineSegment StartX=-49.19 StartY=46.25 StartZ=0 EndX=-49.19 EndY=43.25 EndZ=0
    g5: LineSegment StartX=-49.19 StartY=40.5 StartZ=0 EndX=-49.19 EndY=37.5 EndZ=0
    g6: LineSegment StartX=-49.19 StartY=34.5 StartZ=0 EndX=-49.19 EndY=31.5 EndZ=0
    g7: LineSegment StartX=-49.19 StartY=28.75 StartZ=0 EndX=-49.19 EndY=25.75 EndZ=0
    g8: LineSegment StartX=-49.19 StartY=23 StartZ=0 EndX=-49.19 EndY=20 EndZ=0
    g9: LineSegment StartX=-49.19 StartY=17.25 StartZ=0 EndX=-49.19 EndY=14.25 EndZ=0
    g10: LineSegment StartX=-49.19 StartY=11.5 StartZ=0 EndX=-49.19 EndY=8.5 EndZ=0
    g11: LineSegment StartX=-49.19 StartY=5.75 StartZ=0 EndX=-49.19 EndY=2.75 EndZ=0
    g12: ArcOfCircle CenterX=-1.5 CenterY=67.75 CenterZ=0 NormalX=0 NormalY=0 NormalZ=1 AngleXU=0 Radius=1.5 StartAngle=4.71239 EndAngle=7.85398
    g13: ArcOfCircle CenterX=-1.5 CenterY=62 CenterZ=0 NormalX=0 NormalY=0 NormalZ=1 AngleXU=0 Radius=1.5 StartAngle=4.71239 EndAngle=7.85398
    g14: ArcOfCircle CenterX=-1.5 CenterY=56.25 CenterZ=0 NormalX=0 NormalY=0 NormalZ=1 AngleXU=0 Radius=1.5 StartAngle=4.71239 EndAngle=7.85398
    g15: ArcOfCircle CenterX=-11.49 CenterY=50.5 CenterZ=0 NormalX=0 NormalY=0 NormalZ=1 AngleXU=0 Radius=1.5 StartAngle=4.71239 EndAngle=7.85398
    g16: ArcOfCircle CenterX=-16.28 CenterY=44.75 CenterZ=0 NormalX=0 NormalY=0 NormalZ=1 AngleXU=0 Radius=1.5 StartAngle=4.71239 EndAngle=7.85398
    g17: ArcOfCircle CenterX=-18.2337 CenterY=39 CenterZ=0 NormalX=0 NormalY=0 NormalZ=1 AngleXU=0 Radius=1.5 StartAngle=4.71485 EndAngle=7.85398
    g18: ArcOfCircle CenterX=-16.2837 CenterY=27.25 CenterZ=0 NormalX=0 NormalY=0 NormalZ=1 AngleXU=0 Radius=1.5 StartAngle=4.71485 EndAngle=7.85398
    g19: ArcOfCircle CenterX=-18.2337 CenterY=33 CenterZ=0 NormalX=0 NormalY=0 NormalZ=1 AngleXU=0 Radius=1.5 StartAngle=4.71485 EndAngle=7.85398
    g20: ArcOfCircle CenterX=-11.49 CenterY=21.5 CenterZ=0 NormalX=0 NormalY=0 NormalZ=1 AngleXU=0 Radius=1.5 StartAngle=4.71239 EndAngle=7.85398
    g21: ArcOfCircle CenterX=-1.5 CenterY=4.25 CenterZ=0 NormalX=0 NormalY=0 NormalZ=1 AngleXU=0 Radius=1.5 StartAngle=4.71239 EndAngle=7.85398
    g22: ArcOfCircle CenterX=-1.5 CenterY=10 CenterZ=0 NormalX=0 NormalY=0 NormalZ=1 AngleXU=0 Radius=1.5 StartAngle=4.71239 EndAngle=7.85398
    g23: ArcOfCircle CenterX=-1.5 CenterY=15.75 CenterZ=0 NormalX=0 NormalY=0 NormalZ=1 AngleXU=0 Radius=1.5 StartAngle=4.71239 EndAngle=7.85398
    g24: LineSegment StartX=-49.19 StartY=69.25 StartZ=0 EndX=-1.5 EndY=69.25 EndZ=0
    g25: LineSegment StartX=-49.19 StartY=66.25 StartZ=0 EndX=-1.5 EndY=66.25 EndZ=0
    g26: LineSegment StartX=-49.19 StartY=63.5 StartZ=0 EndX=-1.5 EndY=63.5 EndZ=0
    g27: LineSegment StartX=-49.19 StartY=60.5 StartZ=0 EndX=-1.5 EndY=60.5 EndZ=0
    g28: LineSegment StartX=-49.19 StartY=57.75 StartZ=0 EndX=-1.5 EndY=57.75 EndZ=0
    g29: LineSegment StartX=-49.19 StartY=54.75 StartZ=0 EndX=-1.5 EndY=54.75 EndZ=0
    g30: LineSegment StartX=-49.19 StartY=52 StartZ=0 EndX=-11.49 EndY=52 EndZ=0
    g31: LineSegment StartX=-49.19 StartY=49 StartZ=0 EndX=-11.49 EndY=49 EndZ=0
    g32: LineSegment StartX=-49.19 StartY=46.25 StartZ=0 EndX=-16.28 EndY=46.25 EndZ=0
    g33: LineSegment StartX=-49.19 StartY=43.25 StartZ=0 EndX=-16.28 EndY=43.25 EndZ=0
    g34: LineSegment StartX=-49.19 StartY=40.5 StartZ=0 EndX=-18.2337 EndY=40.5 EndZ=0
    g35: LineSegment StartX=-49.19 StartY=37.5 StartZ=0 EndX=-18.23 EndY=37.5 EndZ=0
    g36: LineSegment StartX=-49.19 StartY=34.5 StartZ=0 EndX=-18.2337 EndY=34.5 EndZ=0
    g37: LineSegment StartX=-49.19 StartY=31.5 StartZ=0 EndX=-18.23 EndY=31.5 EndZ=0
    g38: LineSegment StartX=-49.19 StartY=28.75 StartZ=0 EndX=-16.2837 EndY=28.75 EndZ=0
    g39: LineSegment StartX=-49.19 StartY=25.75 StartZ=0 EndX=-16.28 EndY=25.75 EndZ=0
    g40: LineSegment StartX=-49.19 StartY=23 StartZ=0 EndX=-11.49 EndY=23 EndZ=0
    g41: LineSegment StartX=-49.19 StartY=20 StartZ=0 EndX=-11.49 EndY=20 EndZ=0
    g42: LineSegment StartX=-49.19 StartY=17.25 StartZ=0 EndX=-1.5 EndY=17.25 EndZ=0
    g43: LineSegment StartX=-49.19 StartY=14.25 StartZ=0 EndX=-1.5 EndY=14.25 EndZ=0
    g44: LineSegment StartX=-49.19 StartY=11.5 StartZ=0 EndX=-1.5 EndY=11.5 EndZ=0
    g45: LineSegment StartX=-49.19 StartY=8.5 StartZ=0 EndX=-1.5 EndY=8.5 EndZ=0
    g46: LineSegment StartX=-49.19 StartY=5.75 StartZ=0 EndX=-1.5 EndY=5.75 EndZ=0
    g47: LineSegment StartX=-49.19 StartY=2.75 StartZ=0 EndX=-1.5 EndY=2.75 EndZ=0
  constraints (120):
    c: Vertical(g0)
    c: Distance(g0) = 3
    c: Block(g0)
    c: Vertical(g1)
    c: Distance(g1) = 3
    c: Vertical(g2)
    c: Equal(g0,g2) = 3
    c: Block(g2)
    c: Vertical(g3)
    c: Equal(g1,g3) = 3
    c: Vertical(g4)
    c: Equal(g0,g4) = 3
    c: Block(g4)
    c: Vertical(g5)
    c: Equal(g1,g5) = 3
    c: Vertical(g6)
    c: Equal(g0,g6) = 3
    c: Block(g6)
    c: Vertical(g7)
    c: Equal(g1,g7) = 3
    c: Vertical(g8)
    c: Equal(g0,g8) = 3
    c: Block(g8)
    c: Vertical(g9)
    c: Equal(g1,g9) = 3
    c: Vertical(g10)
    c: Equal(g0,g10) = 3
    c: Block(g10)
    c: Vertical(g11)
    c: Equal(g1,g11) = 3
    c: Block(g12)
    c: Block(g13)
    c: Block(g14)
    c: Block(g15)
    c: Block(g16)
    c: Block(g17)
    c: Block(g18)
    c: Block(g19)
    c: Block(g20)
    c: Block(g21)
    c: Block(g22)
    c: Block(g23)
    c: Block(g11)
    c: Block(g9)
    c: Block(g7)
    c: Block(g5)
    c: Block(g3)
    c: Block(g1)
    c: Coincident(g24,g0)
    c: Coincident(g24,g12)
    c: Horizontal(g24)
    c: Coincident(g25,g0)
    c: Coincident(g25,g12)
    c: Horizontal(g25)
    c: Coincident(g26,g1)
    c: Coincident(g26,g13)
    c: Horizontal(g26)
    c: Coincident(g27,g1)
    c: Coincident(g27,g13)
    c: Horizontal(g27)
    c: Coincident(g28,g2)
    c: Coincident(g28,g14)
    c: Horizontal(g28)
    c: Coincident(g29,g2)
    c: Coincident(g29,g14)
    c: Horizontal(g29)
    c: Coincident(g30,g3)
    c: Coincident(g30,g15)
    c: Horizontal(g30)
    c: Coincident(g31,g3)
    c: Coincident(g31,g15)
    c: Horizontal(g31)
    c: Coincident(g32,g4)
    c: Coincident(g32,g16)
    c: Horizontal(g32)
    c: Coincident(g33,g4)
    c: Coincident(g33,g16)
    c: Horizontal(g33)
    c: Coincident(g34,g5)
    c: Coincident(g34,g17)
    c: Horizontal(g34)
    c: Coincident(g35,g5)
    c: Coincident(g35,g17)
    c: Horizontal(g35)
    c: Coincident(g36,g6)
    c: Coincident(g36,g19)
    c: Horizontal(g36)
    c: Coincident(g37,g6)
    c: Coincident(g37,g19)
    c: Horizontal(g37)
    c: Coincident(g38,g7)
    c: Coincident(g38,g18)
    c: Horizontal(g38)
    c: Coincident(g39,g7)
    c: Coincident(g39,g18)
    c: Horizontal(g39)
    c: Coincident(g40,g8)
    c: Coincident(g40,g20)
    c: Horizontal(g40)
    c: Coincident(g41,g8)
    c: Coincident(g41,g20)
    c: Horizontal(g41)
    c: Coincident(g42,g9)
    c: Coincident(g42,g23)
    c: Horizontal(g42)
    c: Coincident(g43,g9)
    c: Coincident(g43,g23)
    c: Horizontal(g43)
    c: Coincident(g44,g10)
    c: Coincident(g44,g22)
    c: Horizontal(g44)
    c: Coincident(g45,g10)
    c: Coincident(g45,g22)
    c: Horizontal(g45)
    c: Coincident(g46,g11)
    c: Coincident(g46,g21)
    c: Horizontal(g46)
    c: Coincident(g47,g11)
    c: Coincident(g47,g21)
    c: Horizontal(g47)
FEATURE [Part::Extrusion] Extrude042
  Base = -> Sketch051
  Dir = (1,-2e-16,2e-16)
  DirMode = 2
  FaceMakerClass = Part::FaceMakerBullseye
  LengthFwd = 19
  LengthRev = 0
  Placement = pos=(-19,0,0) rot=(0,0,1;0rad)
  Solid = true
  Symmetric = false
FEATURE [Part::Fillet] Fillet035  label="removeToCreateVentalationHoles"
  Base = -> Extrude042
  Edges = <same value as first occurrence — deduplicated (x6 in doc)>
  Placement = pos=(7,0,0) rot=(0,0,1;0rad)
FEATURE [Part::Cut] Cut038  label="top017"
  Base = -> Cut033
  Tool = -> Fillet035
FEATURE [Sketcher::SketchObject] Sketch052  label="bottomSketch001"
  FullyConstrained = true
  sketch-geometry (45):
    g0: LineSegment StartX=6.29999 StartY=8 StartZ=0 EndX=3.29999 EndY=8 EndZ=0
    g1: LineSegment StartX=3.29999 StartY=8 StartZ=0 EndX=3.29999 EndY=-6.03275e-07 EndZ=0
    g2: ArcOfCircle CenterX=8.29999 CenterY=5 CenterZ=0 NormalX=0 NormalY=0 NormalZ=1 AngleXU=0 Radius=2 StartAngle=3.14159 EndAngle=4.71239
    g3: LineSegment StartX=6.29999 StartY=8 StartZ=0 EndX=6.29999 EndY=5 EndZ=0
    g4: ArcOfCircle CenterX=105 CenterY=19 CenterZ=0 NormalX=0 NormalY=0 NormalZ=1 AngleXU=0 Radius=12.7 StartAngle=4.71239 EndAngle=5.94289
    g5-g11: Circle x7 (B-spline internal-alignment scaffolding for g12; pole/knot coordinates omitted)
    g12: BSplineCurve PolesCount=7 KnotsCount=5 Degree=3 IsPeriodic=0
    g13-g17: GeomPoint x5 (B-spline internal-alignment scaffolding for g12; pole/knot coordinates omitted)
    g18: ArcOfCircle CenterX=105 CenterY=19 CenterZ=0 NormalX=0 NormalY=0 NormalZ=1 AngleXU=0 Radius=15.7 StartAngle=5.81226 EndAngle=6.28319
    g19: BSplineCurve PolesCount=5 KnotsCount=3 Degree=3 IsPeriodic=0
    g20: LineSegment StartX=8.29999 StartY=3 StartZ=0 EndX=101.7 EndY=3 EndZ=0
    g21: LineSegment StartX=3.29999 StartY=-6.03275e-07 StartZ=0 EndX=105 EndY=-6.03275e-07 EndZ=0
    g22: LineSegment StartX=120.974 StartY=8.71251 StartZ=0 EndX=122.332 EndY=7.83778 EndZ=0
    g23: LineSegment StartX=105 StartY=-6.03274e-07 StartZ=0 EndX=113 EndY=-6.03274e-07 EndZ=0
    g24: ArcOfCircle CenterX=105 CenterY=19 CenterZ=0 NormalX=0 NormalY=0 NormalZ=1 AngleXU=0 Radius=20.6155 StartAngle=5.11091 EndAngle=5.71103
    g25: ArcOfCircle CenterX=117.7 CenterY=19 CenterZ=0 NormalX=0 NormalY=0 NormalZ=1 AngleXU=0 Radius=3 StartAngle=1.2e-15 EndAngle=2.10468
    g26: Circle CenterX=116.345 CenterY=16.3232 CenterZ=0 NormalX=0 NormalY=0 NormalZ=1 AngleXU=0 Radius=1
    g27: Circle CenterX=117.24 CenterY=15.7584 CenterZ=0 NormalX=0 NormalY=0 NormalZ=1 AngleXU=0 Radius=1
    g28: Circle CenterX=116.972 CenterY=14.7612 CenterZ=0 NormalX=0 NormalY=0 NormalZ=1 AngleXU=0 Radius=1
    g29: BSplineCurve PolesCount=3 KnotsCount=2 Degree=2 IsPeriodic=0
    g30: GeomPoint X=116.345 Y=16.3232 Z=0
    g31: GeomPoint X=116.972 Y=14.7612 Z=0
    g32: Circle CenterX=115.828 CenterY=17.157 CenterZ=0 NormalX=0 NormalY=0 NormalZ=1 AngleXU=0 Radius=1
    g33: Circle CenterX=115.841 CenterY=16.639 CenterZ=0 NormalX=0 NormalY=0 NormalZ=1 AngleXU=0 Radius=1
    g34: Circle CenterX=116.345 CenterY=16.3232 CenterZ=0 NormalX=0 NormalY=0 NormalZ=1 AngleXU=0 Radius=1
    g35: BSplineCurve PolesCount=3 KnotsCount=2 Degree=2 IsPeriodic=0
    g36: GeomPoint X=115.828 Y=17.157 Z=0
    g37: GeomPoint X=116.345 Y=16.3232 Z=0
    g38: LineSegment StartX=115.828 StartY=17.157 StartZ=0 EndX=115.828 EndY=20.8307 EndZ=0
    g39: Circle CenterX=115.828 CenterY=20.8307 CenterZ=0 NormalX=0 NormalY=0 NormalZ=1 AngleXU=0 Radius=1
    g40: Circle CenterX=115.831 CenterY=21.3396 CenterZ=0 NormalX=0 NormalY=0 NormalZ=1 AngleXU=0 Radius=1
    g41: Circle CenterX=116.173 CenterY=21.5825 CenterZ=0 NormalX=0 NormalY=0 NormalZ=1 AngleXU=0 Radius=1
    g42: BSplineCurve PolesCount=3 KnotsCount=2 Degree=2 IsPeriodic=0
    g43: GeomPoint X=115.828 Y=20.8307 Z=0
    g44: GeomPoint X=116.173 Y=21.5825 Z=0
  constraints (70):
    c: Horizontal(g0)
    c: Distance(g0) = 3
    c: Coincident(g1,g0)
    c: Vertical(g1)
    c: Block(g2)
    c: Block(g0)
    c: Coincident(g3,g0)
    c: Coincident(g3,g2)
    c: Vertical(g3)
    c: Block(g1)
    c: Block(g4)
    c: Coincident(g19,g4)
    c: Block(g19)
    c: Equal(g5, g6-g11) x6
    c: InternalAlignment(g5-g11 -> g12) x7
    c: InternalAlignment(g13-g17 -> g12) x5
    c: Block(g12)
    c: Coincident(g18,g12)
    c: Block(g18)
    c: Coincident(g20,g2)
    c: Coincident(g20,g19)
    c: Horizontal(g20)
    c: Distance(g20) = 93.4
    c: Coincident(g21,g1)
    c: Horizontal(g21)
    c: Distance(g21) = 101.7
    c: Horizontal(g23)
    c: Distance(g23) = 8
    c: Coincident(g24,g23)
    c: Block(g23)
    c: Coincident(g22,g24)
    c: Block(g24)
    c: Block(g22)
    c: Distance(g22) = 1.61553
    c: Coincident(g25,g18)
    c: Block(g25)
    c: Weight(g26) = 1
    c: Equal(g26,g27)
    c: Equal(g26,g28)
    c: Coincident(g29,g4)
    c: InternalAlignment(g26,g29)
    c: InternalAlignment(g27,g29)
    c: InternalAlignment(g28,g29)
    c: InternalAlignment(g30,g29)
    c: InternalAlignment(g31,g29)
    c: Block(g29)
    c: Weight(g32) = 1
    c: Equal(g32,g33)
    c: Equal(g32,g34)
    c: Coincident(g35,g29)
    c: InternalAlignment(g32,g35)
    c: InternalAlignment(g33,g35)
    c: InternalAlignment(g34,g35)
    c: InternalAlignment(g36,g35)
    c: InternalAlignment(g37,g35)
    c: Block(g35)
    c: Coincident(g38,g35)
    c: Vertical(g38)
    c: Block(g38)
    c: Coincident(g42,g38)
    c: Weight(g39) = 1
    c: Equal(g39,g40)
    c: Equal(g39,g41)
    c: Coincident(g42,g25)
    c: InternalAlignment(g39,g42)
    c: InternalAlignment(g40,g42)
    c: InternalAlignment(g41,g42)
    c: InternalAlignment(g43,g42)
    c: InternalAlignment(g44,g42)
    c: Block(g42)
FEATURE [Part::Extrusion] Extrude043  label="bottom010"
  Base = -> Sketch052
  Dir = (0,0,1)
  DirMode = 2
  FaceMakerClass = Part::FaceMakerBullseye
  LengthFwd = 71.4
  LengthRev = 0
  Placement = pos=(0,0,0.3) rot=(0,0,1;0rad)
  Solid = true
  Symmetric = false
FEATURE [Sketcher::SketchObject] Sketch053  label="topSketch013"
  FullyConstrained = true
  sketch-geometry (22):
    g0: LineSegment StartX=5.21097e-06 StartY=3 StartZ=0 EndX=5.21097e-06 EndY=19 EndZ=0
    g1: ArcOfCircle CenterX=19 CenterY=19 CenterZ=0 NormalX=0 NormalY=0 NormalZ=1 AngleXU=0 Radius=19 StartAngle=1.5708 EndAngle=3.14159
    g2: ArcOfCircle CenterX=19 CenterY=19 CenterZ=0 NormalX=0 NormalY=0 NormalZ=1 AngleXU=0 Radius=16 StartAngle=1.5708 EndAngle=3.14159
    g3: LineSegment StartX=114 StartY=35 StartZ=0 EndX=19 EndY=35 EndZ=0
    g4: LineSegment StartX=5.21097e-06 StartY=3 StartZ=0 EndX=5.21097e-06 EndY=0 EndZ=0
    g5: LineSegment StartX=3 StartY=0 StartZ=0 EndX=5.21097e-06 EndY=0 EndZ=0
    g6: LineSegment StartX=3 StartY=19 StartZ=0 EndX=3 EndY=0 EndZ=0
    g7: LineSegment StartX=19 StartY=38 StartZ=0 EndX=124 EndY=38 EndZ=0
    g8: Circle CenterX=119 CenterY=35 CenterZ=0 NormalX=0 NormalY=0 NormalZ=1 AngleXU=0 Radius=1
    g9: Circle CenterX=121 CenterY=35 CenterZ=0 NormalX=0 NormalY=0 NormalZ=1 AngleXU=0 Radius=1
    g10: Circle CenterX=121 CenterY=33 CenterZ=0 NormalX=0 NormalY=0 NormalZ=1 AngleXU=0 Radius=1
    g11: BSplineCurve PolesCount=3 KnotsCount=2 Degree=2 IsPeriodic=0
    g12: GeomPoint X=119 Y=35 Z=0
    g13: GeomPoint X=121 Y=33 Z=0
    g14: LineSegment StartX=119 StartY=35 StartZ=0 EndX=114 EndY=35 EndZ=0
    g15: ArcOfCircle CenterX=105 CenterY=19 CenterZ=0 NormalX=0 NormalY=0 NormalZ=1 AngleXU=0 Radius=16 StartAngle=5.60905 EndAngle=6.28319
    g16: LineSegment StartX=121 StartY=33 StartZ=0 EndX=121 EndY=19 EndZ=0
    g17: LineSegment StartX=117.5 StartY=9.01251 StartZ=0 EndX=121.163 EndY=9.0125 EndZ=0
    g18: ArcOfCircle CenterX=105 CenterY=19 CenterZ=0 NormalX=0 NormalY=0 NormalZ=1 AngleXU=0 Radius=20.6155 StartAngle=5.7297 EndAngle=6.28319
    g19: LineSegment StartX=121.163 StartY=9.0125 StartZ=0 EndX=122.538 EndY=8.16329 EndZ=0
    g20: LineSegment StartX=124 StartY=38 StartZ=0 EndX=125.616 EndY=38 EndZ=0
    g21: LineSegment StartX=125.616 StartY=19 StartZ=0 EndX=125.616 EndY=38 EndZ=0
  constraints (50):
    c: Vertical(g0)
    c: Block(g0)
    c: Coincident(g1,g0)
    c: Block(g1)
    c: Coincident(g2,g1)
    c: Block(g2)
    c: Coincident(g3,g2)
    c: Horizontal(g3)
    c: Tangent(g3,g2)
    c: Coincident(g4,g0)
    c: Distance(g4) = 3
    c: Vertical(g4)
    c: Coincident(g5,g4)
    c: Horizontal(g5)
    c: Coincident(g6,g2)
    c: Coincident(g6,g5)
    c: Vertical(g6)
    c: Horizontal(g7)
    c: Distance(g7) = 105
    c: Coincident(g7,g1)
    c: Block(g3)
    c: Weight(g8) = 1
    c: Equal(g8,g9)
    c: Equal(g8,g10)
    c: InternalAlignment(g8,g11)
    c: InternalAlignment(g9,g11)
    c: InternalAlignment(g10,g11)
    c: InternalAlignment(g12,g11)
    c: InternalAlignment(g13,g11)
    c: Block(g11)
    c: Coincident(g14,g11)
    c: Coincident(g14,g3)
    c: Horizontal(g14)
    c: Block(g15)
    c: Coincident(g16,g11)
    c: Coincident(g16,g15)
    c: Vertical(g16)
    c: Distance(g16) = 14
    c: Coincident(g17,g15)
    c: Block(g18)
    c: Coincident(g19,g18)
    c: Coincident(g20,g7)
    c: Horizontal(g20)
    c: Vertical(g21)
    c: Coincident(g20,g21)
    c: Block(g20)
    c: Block(g21)
    c: Block(g19)
    c: Block(g17)
    c: Distance(g20) = 1.61553
FEATURE [Part::Extrusion] Extrude044
  Base = -> Sketch053
  Dir = (0,0,1)
  DirMode = 2
  FaceMakerClass = Part::FaceMakerBullseye
  LengthFwd = 72
  LengthRev = 0
  Solid = true
  Symmetric = false
FEATURE [Part::Fillet] Fillet036  label="top018"
  Base = -> Extrude044
  Edges = 1 edges r=2: [Edge41]
FEATURE [Sketcher::SketchObject] Sketch054
  FullyConstrained = false
  Placement = pos=(0,0,0) rot=(1,0,0;1.5708rad)
  sketch-geometry (24):
    g0: ArcOfCircle CenterX=-4 CenterY=-10.5 CenterZ=0 NormalX=0 NormalY=0 NormalZ=1 AngleXU=0 Radius=1.5 StartAngle=6e-16 EndAngle=3.14159
    g1: ArcOfCircle CenterX=-34.2 CenterY=-10.5 CenterZ=0 NormalX=0 NormalY=0 NormalZ=1 AngleXU=0 Radius=1.5 StartAngle=0 EndAngle=3.14159
    g2: ArcOfCircle CenterX=-34.2 CenterY=-27.7 CenterZ=0 NormalX=0 NormalY=0 NormalZ=1 AngleXU=0 Radius=1.5 StartAngle=3.14159 EndAngle=6.28319
    g3: ArcOfCircle CenterX=-4 CenterY=-27.7 CenterZ=0 NormalX=0 NormalY=0 NormalZ=1 AngleXU=0 Radius=1.5 StartAngle=3.1416 EndAngle=6.28319
    g4: ArcOfCircle CenterX=-10 CenterY=-4.3 CenterZ=0 NormalX=0 NormalY=0 NormalZ=1 AngleXU=0 Radius=1.5 StartAngle=2e-16 EndAngle=3.14159
    g5: ArcOfCircle CenterX=-16.1 CenterY=-1.8 CenterZ=0 NormalX=0 NormalY=0 NormalZ=1 AngleXU=0 Radius=1.5 StartAngle=5e-16 EndAngle=3.14159
    g6: ArcOfCircle CenterX=-22.1 CenterY=-1.8 CenterZ=0 NormalX=0 NormalY=0 NormalZ=1 AngleXU=0 Radius=1.5 StartAngle=5e-16 EndAngle=3.14159
    g7: ArcOfCircle CenterX=-28.2 CenterY=-4.3 CenterZ=0 NormalX=0 NormalY=0 NormalZ=1 AngleXU=0 Radius=1.5 StartAngle=2e-16 EndAngle=3.14159
    g8: ArcOfCircle CenterX=-10 CenterY=-33.9 CenterZ=0 NormalX=0 NormalY=0 NormalZ=1 AngleXU=0 Radius=1.5 StartAngle=3.14159 EndAngle=6.28319
    g9: ArcOfCircle CenterX=-16.1 CenterY=-36.4 CenterZ=0 NormalX=0 NormalY=0 NormalZ=1 AngleXU=0 Radius=1.5 StartAngle=3.14159 EndAngle=6.28319
    g10: ArcOfCircle CenterX=-22.1 CenterY=-36.4 CenterZ=0 NormalX=0 NormalY=0 NormalZ=1 AngleXU=0 Radius=1.5 StartAngle=3.14159 EndAngle=6.28319
    g11: ArcOfCircle CenterX=-28.2 CenterY=-33.9 CenterZ=0 NormalX=0 NormalY=0 NormalZ=1 AngleXU=0 Radius=1.5 StartAngle=3.14159 EndAngle=6.28319
    g12: LineSegment StartX=-35.7 StartY=-10.5 StartZ=0 EndX=-35.7 EndY=-27.7 EndZ=0
    g13: LineSegment StartX=-32.7 StartY=-10.5 StartZ=0 EndX=-32.7 EndY=-27.7 EndZ=0
    g14: LineSegment StartX=-29.7 StartY=-33.9 StartZ=0 EndX=-29.7 EndY=-4.3 EndZ=0
    g15: LineSegment StartX=-26.7 StartY=-33.9 StartZ=0 EndX=-26.7 EndY=-4.3 EndZ=0
    g16: LineSegment StartX=-2.5 StartY=-10.5 StartZ=0 EndX=-2.5 EndY=-27.7 EndZ=0
    g17: LineSegment StartX=-8.5 StartY=-4.3 StartZ=0 EndX=-8.5 EndY=-33.9 EndZ=0
    g18: LineSegment StartX=-5.5 StartY=-10.5 StartZ=0 EndX=-5.5 EndY=-27.7 EndZ=0
    g19: LineSegment StartX=-11.5 StartY=-4.3 StartZ=0 EndX=-11.5 EndY=-33.9 EndZ=0
    g20: LineSegment StartX=-14.6 StartY=-1.8 StartZ=0 EndX=-14.6 EndY=-36.4 EndZ=0
    g21: LineSegment StartX=-17.6 StartY=-1.8 StartZ=0 EndX=-17.6 EndY=-36.4 EndZ=0
    g22: LineSegment StartX=-20.6 StartY=-36.4 StartZ=0 EndX=-20.6 EndY=-1.8 EndZ=0
    g23: LineSegment StartX=-23.6 StartY=-1.8 StartZ=0 EndX=-23.6 EndY=-36.4 EndZ=0
  constraints (48):
    c: Block(g0)
    c: Block(g1)
    c: Block(g2)
    c: Block(g3)
    c: Block(g4)
    c: Block(g5)
    c: Block(g6)
    c: Block(g7)
    c: Block(g8)
    c: Block(g9)
    c: Block(g10)
    c: Block(g11)
    c: Coincident(g12,g1)
    c: Coincident(g12,g2)
    c: Vertical(g12)
    c: Coincident(g13,g1)
    c: Coincident(g13,g2)
    c: Vertical(g13)
    c: Coincident(g14,g11)
    c: Coincident(g14,g7)
    c: Vertical(g14)
    c: Coincident(g15,g11)
    c: Coincident(g15,g7)
    c: Vertical(g15)
    c: Coincident(g16,g0)
    c: Coincident(g16,g3)
    c: Vertical(g16)
    c: Coincident(g17,g4)
    c: Coincident(g17,g8)
    c: Vertical(g17)
    c: Coincident(g18,g0)
    c: Coincident(g18,g3)
    c: Vertical(g18)
    c: Coincident(g19,g4)
    c: Coincident(g19,g8)
    c: Vertical(g19)
    c: Coincident(g20,g5)
    c: Coincident(g20,g9)
    c: Vertical(g20)
    c: Coincident(g21,g5)
    c: Coincident(g21,g9)
    c: Vertical(g21)
    c: Coincident(g22,g10)
    c: Coincident(g22,g6)
    c: Vertical(g22)
    c: Coincident(g23,g6)
    c: Coincident(g23,g10)
    c: Vertical(g23)
FEATURE [Part::Extrusion] Extrude045  label="removeToCreateFanGrillHoles003"
  Base = -> Sketch054
  Dir = (0,-1,6e-16)
  DirMode = 2
  FaceMakerClass = Part::FaceMakerBullseye
  LengthFwd = 10
  LengthRev = 0
  Placement = pos=(65.4,44,54.82) rot=(0,0,1;0rad)
  Solid = true
  Symmetric = false
FEATURE [Part::Feature] Face105 .. Face108  x4 (patterned run collapsed; names and placements below)
  shape: bbox 3.5 x 17.8 x 2e-07 mm, 1 faces, 0 solids (baked)
FEATURE [Part::Revolution] Revolve113  label="removeToCreateScrewAndThreadedInsertHole041"
  Angle = 360
  Axis = (0,1,0)
  Base = (0,0,0)
  FaceMakerClass = Part::FaceMakerBullseye
  Placement = pos=(62.3,30.3,19.7) rot=(0,0,1;0rad)
  Solid = false
  Source = -> Face105
  Symmetric = false
FEATURE [Part::Revolution] Revolve114  label="removeToCreateScrewAndThreadedInsertHole042"
  Angle = 360
  Axis = (0,1,0)
  Base = (0,0,0)
  FaceMakerClass = Part::FaceMakerBullseye
  Placement = pos=(62.3,30.3,51.7) rot=(0,0,1;0rad)
  Solid = false
  Source = -> Face106
  Symmetric = false
FEATURE [Part::Revolution] Revolve115  label="removeToCreateScrewAndThreadedInsertHole043"
  Angle = 360
  Axis = (0,1,0)
  Base = (0,0,0)
  FaceMakerClass = Part::FaceMakerBullseye
  Placement = pos=(30.3,30.3,19.7) rot=(0,0,1;0rad)
  Solid = false
  Source = -> Face107
  Symmetric = false
FEATURE [Part::Revolution] Revolve116  label="removeToCreateScrewAndThreadedInsertHole044"
  Angle = 360
  Axis = (0,1,0)
  Base = (0,0,0)
  FaceMakerClass = Part::FaceMakerBullseye
  Placement = pos=(30.3,30.3,51.7) rot=(0,0,1;0rad)
  Solid = false
  Source = -> Face108
  Symmetric = false
FEATURE [Part::MultiFuse] Fusion083  label="createThreadedInsertHolesForFan004"
  Shapes = -> [Revolve113,Revolve114,Revolve115,Revolve116]
FEATURE [Part::Box] Box024  label="removeToCreteHoleForPlugHousing026"
  AttacherType = Attacher::AttachEngine3D
  Height = 28.6
  Length = 10
  Placement = pos=(-2,0,21.7) rot=(0,0,1;0rad)
  Width = 19
FEATURE [Part::Cylinder] Cylinder038  label="removeToCreteHoleForPlugHousing027"
  Angle = 360
  AttacherType = Attacher::AttachEngine3D
  Height = 20
  Placement = pos=(-2,19,36) rot=(0,1,0;1.5708rad)
  Radius = 14.3
FEATURE [Part::MultiFuse] Fusion084  label="removeToCreteHoleForPlugHousing028"
  Shapes = -> [Box024,Cylinder038]
FEATURE [Part::Cylinder] Cylinder039
  Angle = 360
  AttacherType = Attacher::AttachEngine3D
  Height = 20
  Placement = pos=(0,0,36.15) rot=(0,0,1;0rad)
  Radius = 14.3
FEATURE [Part::Cylinder] Cylinder040
  Angle = 360
  AttacherType = Attacher::AttachEngine3D
  Height = 10
  Placement = pos=(0,0,36.15) rot=(0,0,1;0rad)
  Radius = 4
FEATURE [Part::Box] Box025  label="removeToCreteHoleForPlugHousing030"
  AttacherType = Attacher::AttachEngine3D
  Height = 28.6
  Length = 20
  Placement = pos=(106.15,0,21.7) rot=(0,0,1;0rad)
  Width = 19
FEATURE [Part::MultiFuse] Fusion086  label="removeToCreteHoleForPlugHousing031"
  Placement = pos=(70,19,36) rot=(0,1,0;1.5708rad)
  Shapes = -> [Cylinder039,Cylinder040]
FEATURE [Part::MultiFuse] Fusion085  label="removeToCreteHoleForPlugHousing029"
  Shapes = -> [Box025,Fusion086]
FEATURE [Sketcher::SketchObject] Sketch055
  FullyConstrained = true
  Placement = pos=(117,19,0) rot=(0.57735,0.57735,0.57735;2.0944rad)
  sketch-geometry (48):
    g0: LineSegment StartX=-49.19 StartY=69.25 StartZ=0 EndX=-49.19 EndY=66.25 EndZ=0
    g1: LineSegment StartX=-49.19 StartY=63.5 StartZ=0 EndX=-49.19 EndY=60.5 EndZ=0
    g2: LineSegment StartX=-49.19 StartY=57.75 StartZ=0 EndX=-49.19 EndY=54.75 EndZ=0
    g3: LineSegment StartX=-49.19 StartY=52 StartZ=0 EndX=-49.19 EndY=49 EndZ=0
    g4: LineSegment StartX=-49.19 StartY=46.25 StartZ=0 EndX=-49.19 EndY=43.25 EndZ=0
    g5: LineSegment StartX=-49.19 StartY=40.5 StartZ=0 EndX=-49.19 EndY=37.5 EndZ=0
    g6: LineSegment StartX=-49.19 StartY=34.5 StartZ=0 EndX=-49.19 EndY=31.5 EndZ=0
    g7: LineSegment StartX=-49.19 StartY=28.75 StartZ=0 EndX=-49.19 EndY=25.75 EndZ=0
    g8: LineSegment StartX=-49.19 StartY=23 StartZ=0 EndX=-49.19 EndY=20 EndZ=0
    g9: LineSegment StartX=-49.19 StartY=17.25 StartZ=0 EndX=-49.19 EndY=14.25 EndZ=0
    g10: LineSegment StartX=-49.19 StartY=11.5 StartZ=0 EndX=-49.19 EndY=8.5 EndZ=0
    g11: LineSegment StartX=-49.19 StartY=5.75 StartZ=0 EndX=-49.19 EndY=2.75 EndZ=0
    g12: ArcOfCircle CenterX=-1.5 CenterY=67.75 CenterZ=0 NormalX=0 NormalY=0 NormalZ=1 AngleXU=0 Radius=1.5 StartAngle=4.71239 EndAngle=7.85398
    g13: ArcOfCircle CenterX=-1.5 CenterY=62 CenterZ=0 NormalX=0 NormalY=0 NormalZ=1 AngleXU=0 Radius=1.5 StartAngle=4.71239 EndAngle=7.85398
    g14: ArcOfCircle CenterX=-1.5 CenterY=56.25 CenterZ=0 NormalX=0 NormalY=0 NormalZ=1 AngleXU=0 Radius=1.5 StartAngle=4.71239 EndAngle=7.85398
    g15: ArcOfCircle CenterX=-11.49 CenterY=50.5 CenterZ=0 NormalX=0 NormalY=0 NormalZ=1 AngleXU=0 Radius=1.5 StartAngle=4.71239 EndAngle=7.85398
    g16: ArcOfCircle CenterX=-16.28 CenterY=44.75 CenterZ=0 NormalX=0 NormalY=0 NormalZ=1 AngleXU=0 Radius=1.5 StartAngle=4.71239 EndAngle=7.85398
    g17: ArcOfCircle CenterX=-18.2337 CenterY=39 CenterZ=0 NormalX=0 NormalY=0 NormalZ=1 AngleXU=0 Radius=1.5 StartAngle=4.71485 EndAngle=7.85398
    g18: ArcOfCircle CenterX=-16.2837 CenterY=27.25 CenterZ=0 NormalX=0 NormalY=0 NormalZ=1 AngleXU=0 Radius=1.5 StartAngle=4.71485 EndAngle=7.85398
    g19: ArcOfCircle CenterX=-18.2337 CenterY=33 CenterZ=0 NormalX=0 NormalY=0 NormalZ=1 AngleXU=0 Radius=1.5 StartAngle=4.71485 EndAngle=7.85398
    g20: ArcOfCircle CenterX=-11.49 CenterY=21.5 CenterZ=0 NormalX=0 NormalY=0 NormalZ=1 AngleXU=0 Radius=1.5 StartAngle=4.71239 EndAngle=7.85398
    g21: ArcOfCircle CenterX=-1.5 CenterY=4.25 CenterZ=0 NormalX=0 NormalY=0 NormalZ=1 AngleXU=0 Radius=1.5 StartAngle=4.71239 EndAngle=7.85398
    g22: ArcOfCircle CenterX=-1.5 CenterY=10 CenterZ=0 NormalX=0 NormalY=0 NormalZ=1 AngleXU=0 Radius=1.5 StartAngle=4.71239 EndAngle=7.85398
    g23: ArcOfCircle CenterX=-1.5 CenterY=15.75 CenterZ=0 NormalX=0 NormalY=0 NormalZ=1 AngleXU=0 Radius=1.5 StartAngle=4.71239 EndAngle=7.85398
    g24: LineSegment StartX=-49.19 StartY=69.25 StartZ=0 EndX=-1.5 EndY=69.25 EndZ=0
    g25: LineSegment StartX=-49.19 StartY=66.25 StartZ=0 EndX=-1.5 EndY=66.25 EndZ=0
    g26: LineSegment StartX=-49.19 StartY=63.5 StartZ=0 EndX=-1.5 EndY=63.5 EndZ=0
    g27: LineSegment StartX=-49.19 StartY=60.5 StartZ=0 EndX=-1.5 EndY=60.5 EndZ=0
    g28: LineSegment StartX=-49.19 StartY=57.75 StartZ=0 EndX=-1.5 EndY=57.75 EndZ=0
    g29: LineSegment StartX=-49.19 StartY=54.75 StartZ=0 EndX=-1.5 EndY=54.75 EndZ=0
    g30: LineSegment StartX=-49.19 StartY=52 StartZ=0 EndX=-11.49 EndY=52 EndZ=0
    g31: LineSegment StartX=-49.19 StartY=49 StartZ=0 EndX=-11.49 EndY=49 EndZ=0
    g32: LineSegment StartX=-49.19 StartY=46.25 StartZ=0 EndX=-16.28 EndY=46.25 EndZ=0
    g33: LineSegment StartX=-49.19 StartY=43.25 StartZ=0 EndX=-16.28 EndY=43.25 EndZ=0
    g34: LineSegment StartX=-49.19 StartY=40.5 StartZ=0 EndX=-18.2337 EndY=40.5 EndZ=0
    g35: LineSegment StartX=-49.19 StartY=37.5 StartZ=0 EndX=-18.23 EndY=37.5 EndZ=0
    g36: LineSegment StartX=-49.19 StartY=34.5 StartZ=0 EndX=-18.2337 EndY=34.5 EndZ=0
    g37: LineSegment StartX=-49.19 StartY=31.5 StartZ=0 EndX=-18.23 EndY=31.5 EndZ=0
    g38: LineSegment StartX=-49.19 StartY=28.75 StartZ=0 EndX=-16.2837 EndY=28.75 EndZ=0
    g39: LineSegment StartX=-49.19 StartY=25.75 StartZ=0 EndX=-16.28 EndY=25.75 EndZ=0
    g40: LineSegment StartX=-49.19 StartY=23 StartZ=0 EndX=-11.49 EndY=23 EndZ=0
    g41: LineSegment StartX=-49.19 StartY=20 StartZ=0 EndX=-11.49 EndY=20 EndZ=0
    g42: LineSegment StartX=-49.19 StartY=17.25 StartZ=0 EndX=-1.5 EndY=17.25 EndZ=0
    g43: LineSegment StartX=-49.19 StartY=14.25 StartZ=0 EndX=-1.5 EndY=14.25 EndZ=0
    g44: LineSegment StartX=-49.19 StartY=11.5 StartZ=0 EndX=-1.5 EndY=11.5 EndZ=0
    g45: LineSegment StartX=-49.19 StartY=8.5 StartZ=0 EndX=-1.5 EndY=8.5 EndZ=0
    g46: LineSegment StartX=-49.19 StartY=5.75 StartZ=0 EndX=-1.5 EndY=5.75 EndZ=0
    g47: LineSegment StartX=-49.19 StartY=2.75 StartZ=0 EndX=-1.5 EndY=2.75 EndZ=0
  constraints (120):
    c: Vertical(g0)
    c: Distance(g0) = 3
    c: Block(g0)
    c: Vertical(g1)
    c: Distance(g1) = 3
    c: Vertical(g2)
    c: Equal(g0,g2) = 3
    c: Block(g2)
    c: Vertical(g3)
    c: Equal(g1,g3) = 3
    c: Vertical(g4)
    c: Equal(g0,g4) = 3
    c: Block(g4)
    c: Vertical(g5)
    c: Equal(g1,g5) = 3
    c: Vertical(g6)
    c: Equal(g0,g6) = 3
    c: Block(g6)
    c: Vertical(g7)
    c: Equal(g1,g7) = 3
    c: Vertical(g8)
    c: Equal(g0,g8) = 3
    c: Block(g8)
    c: Vertical(g9)
    c: Equal(g1,g9) = 3
    c: Vertical(g10)
    c: Equal(g0,g10) = 3
    c: Block(g10)
    c: Vertical(g11)
    c: Equal(g1,g11) = 3
    c: Block(g12)
    c: Block(g13)
    c: Block(g14)
    c: Block(g15)
    c: Block(g16)
    c: Block(g17)
    c: Block(g18)
    c: Block(g19)
    c: Block(g20)
    c: Block(g21)
    c: Block(g22)
    c: Block(g23)
    c: Block(g11)
    c: Block(g9)
    c: Block(g7)
    c: Block(g5)
    c: Block(g3)
    c: Block(g1)
    c: Coincident(g24,g0)
    c: Coincident(g24,g12)
    c: Horizontal(g24)
    c: Coincident(g25,g0)
    c: Coincident(g25,g12)
    c: Horizontal(g25)
    c: Coincident(g26,g1)
    c: Coincident(g26,g13)
    c: Horizontal(g26)
    c: Coincident(g27,g1)
    c: Coincident(g27,g13)
    c: Horizontal(g27)
    c: Coincident(g28,g2)
    c: Coincident(g28,g14)
    c: Horizontal(g28)
    c: Coincident(g29,g2)
    c: Coincident(g29,g14)
    c: Horizontal(g29)
    c: Coincident(g30,g3)
    c: Coincident(g30,g15)
    c: Horizontal(g30)
    c: Coincident(g31,g3)
    c: Coincident(g31,g15)
    c: Horizontal(g31)
    c: Coincident(g32,g4)
    c: Coincident(g32,g16)
    c: Horizontal(g32)
    c: Coincident(g33,g4)
    c: Coincident(g33,g16)
    c: Horizontal(g33)
    c: Coincident(g34,g5)
    c: Coincident(g34,g17)
    c: Horizontal(g34)
    c: Coincident(g35,g5)
    c: Coincident(g35,g17)
    c: Horizontal(g35)
    c: Coincident(g36,g6)
    c: Coincident(g36,g19)
    c: Horizontal(g36)
    c: Coincident(g37,g6)
    c: Coincident(g37,g19)
    c: Horizontal(g37)
    c: Coincident(g38,g7)
    c: Coincident(g38,g18)
    c: Horizontal(g38)
    c: Coincident(g39,g7)
    c: Coincident(g39,g18)
    c: Horizontal(g39)
    c: Coincident(g40,g8)
    c: Coincident(g40,g20)
    c: Horizontal(g40)
    c: Coincident(g41,g8)
    c: Coincident(g41,g20)
    c: Horizontal(g41)
    c: Coincident(g42,g9)
    c: Coincident(g42,g23)
    c: Horizontal(g42)
    c: Coincident(g43,g9)
    c: Coincident(g43,g23)
    c: Horizontal(g43)
    c: Coincident(g44,g10)
    c: Coincident(g44,g22)
    c: Horizontal(g44)
    c: Coincident(g45,g10)
    c: Coincident(g45,g22)
    c: Horizontal(g45)
    c: Coincident(g46,g11)
    c: Coincident(g46,g21)
    c: Horizontal(g46)
    c: Coincident(g47,g11)
    c: Coincident(g47,g21)
    c: Horizontal(g47)
FEATURE [Part::Extrusion] Extrude046
  Base = -> Sketch055
  Dir = (1,0,0)
  DirMode = 2
  FaceMakerClass = Part::FaceMakerBullseye
  LengthFwd = 23
  LengthRev = 0
  Placement = pos=(-19,0,0) rot=(0,0,1;0rad)
  Solid = true
  Symmetric = false
FEATURE [Part::Fillet] Fillet038  label="removeToCreateVentalationHoles001"
  Base = -> Extrude046
  Edges = <same value as first occurrence — deduplicated (x6 in doc)>
  Placement = pos=(7,0,0) rot=(0,0,1;0rad)
FEATURE [Sketcher::SketchObject] Sketch056  label="topSketch014"
  FullyConstrained = true
  sketch-geometry (22):
    g0: LineSegment StartX=5.21097e-06 StartY=3 StartZ=0 EndX=5.21097e-06 EndY=19 EndZ=0
    g1: ArcOfCircle CenterX=19 CenterY=19 CenterZ=0 NormalX=0 NormalY=0 NormalZ=1 AngleXU=0 Radius=19 StartAngle=1.5708 EndAngle=3.14159
    g2: ArcOfCircle CenterX=19 CenterY=19 CenterZ=0 NormalX=0 NormalY=0 NormalZ=1 AngleXU=0 Radius=16 StartAngle=1.5708 EndAngle=3.14159
    g3: LineSegment StartX=114 StartY=35 StartZ=0 EndX=19 EndY=35 EndZ=0
    g4: LineSegment StartX=5.21097e-06 StartY=3 StartZ=0 EndX=5.21097e-06 EndY=0 EndZ=0
    g5: LineSegment StartX=3 StartY=0 StartZ=0 EndX=5.21097e-06 EndY=0 EndZ=0
    g6: LineSegment StartX=3 StartY=19 StartZ=0 EndX=3 EndY=0 EndZ=0
    g7: LineSegment StartX=19 StartY=38 StartZ=0 EndX=124 EndY=38 EndZ=0
    g8: Circle CenterX=119 CenterY=35 CenterZ=0 NormalX=0 NormalY=0 NormalZ=1 AngleXU=0 Radius=1
    g9: Circle CenterX=121 CenterY=35 CenterZ=0 NormalX=0 NormalY=0 NormalZ=1 AngleXU=0 Radius=1
    g10: Circle CenterX=121 CenterY=33 CenterZ=0 NormalX=0 NormalY=0 NormalZ=1 AngleXU=0 Radius=1
    g11: BSplineCurve PolesCount=3 KnotsCount=2 Degree=2 IsPeriodic=0
    g12: GeomPoint X=119 Y=35 Z=0
    g13: GeomPoint X=121 Y=33 Z=0
    g14: LineSegment StartX=119 StartY=35 StartZ=0 EndX=114 EndY=35 EndZ=0
    g15: ArcOfCircle CenterX=105 CenterY=19 CenterZ=0 NormalX=0 NormalY=0 NormalZ=1 AngleXU=0 Radius=16 StartAngle=5.60905 EndAngle=6.28319
    g16: LineSegment StartX=121 StartY=33 StartZ=0 EndX=121 EndY=19 EndZ=0
    g17: LineSegment StartX=117.5 StartY=9.01251 StartZ=0 EndX=121.163 EndY=9.0125 EndZ=0
    g18: ArcOfCircle CenterX=105 CenterY=19 CenterZ=0 NormalX=0 NormalY=0 NormalZ=1 AngleXU=0 Radius=20.6155 StartAngle=5.7297 EndAngle=6.28319
    g19: LineSegment StartX=121.163 StartY=9.0125 StartZ=0 EndX=122.538 EndY=8.16329 EndZ=0
    g20: LineSegment StartX=124 StartY=38 StartZ=0 EndX=125.616 EndY=38 EndZ=0
    g21: LineSegment StartX=125.616 StartY=19 StartZ=0 EndX=125.616 EndY=38 EndZ=0
  constraints (49):
    c: Vertical(g0)
    c: Block(g0)
    c: Coincident(g1,g0)
    c: Block(g1)
    c: Coincident(g2,g1)
    c: Block(g2)
    c: Coincident(g3,g2)
    c: Horizontal(g3)
    c: Tangent(g3,g2)
    c: Coincident(g4,g0)
    c: Distance(g4) = 3
    c: Vertical(g4)
    c: Coincident(g5,g4)
    c: Horizontal(g5)
    c: Coincident(g6,g2)
    c: Coincident(g6,g5)
    c: Vertical(g6)
    c: Horizontal(g7)
    c: Distance(g7) = 105
    c: Coincident(g7,g1)
    c: Block(g3)
    c: Weight(g8) = 1
    c: Equal(g8,g9)
    c: Equal(g8,g10)
    c: InternalAlignment(g8,g11)
    c: InternalAlignment(g9,g11)
    c: InternalAlignment(g10,g11)
    c: InternalAlignment(g12,g11)
    c: InternalAlignment(g13,g11)
    c: Block(g11)
    c: Coincident(g14,g11)
    c: Coincident(g14,g3)
    c: Horizontal(g14)
    c: Block(g15)
    c: Coincident(g16,g11)
    c: Coincident(g16,g15)
    c: Vertical(g16)
    c: Distance(g16) = 14
    c: Coincident(g17,g15)
    c: Block(g18)
    c: Coincident(g19,g18)
    c: Coincident(g20,g7)
    c: Horizontal(g20)
    c: Vertical(g21)
    c: Coincident(g20,g21)
    c: Block(g20)
    c: Block(g21)
    c: Block(g19)
    c: Block(g17)
FEATURE [Part::Box] Box026  label="removeToCreteHoleForPlugHousing032"
  AttacherType = Attacher::AttachEngine3D
  Height = 28.6
  Length = 10
  Placement = pos=(-2,0,21.7) rot=(0,0,1;0rad)
  Width = 19
FEATURE [Part::Feature] Face109 .. Face112  x4 (patterned run collapsed; names and placements below)
  shape: bbox 3.5 x 17.8 x 2e-07 mm, 1 faces, 0 solids (baked)
FEATURE [Part::Revolution] Revolve117  label="removeToCreateScrewAndThreadedInsertHole045"
  Angle = 360
  Axis = (0,1,0)
  Base = (0,0,0)
  FaceMakerClass = Part::FaceMakerBullseye
  Placement = pos=(62.3,30.3,19.7) rot=(0,0,1;0rad)
  Solid = false
  Source = -> Face109
  Symmetric = false
FEATURE [Part::Revolution] Revolve118  label="removeToCreateScrewAndThreadedInsertHole046"
  Angle = 360
  Axis = (0,1,0)
  Base = (0,0,0)
  FaceMakerClass = Part::FaceMakerBullseye
  Placement = pos=(62.3,30.3,51.7) rot=(0,0,1;0rad)
  Solid = false
  Source = -> Face110
  Symmetric = false
FEATURE [Part::Revolution] Revolve119  label="removeToCreateScrewAndThreadedInsertHole047"
  Angle = 360
  Axis = (0,1,0)
  Base = (0,0,0)
  FaceMakerClass = Part::FaceMakerBullseye
  Placement = pos=(30.3,30.3,19.7) rot=(0,0,1;0rad)
  Solid = false
  Source = -> Face111
  Symmetric = false
FEATURE [Part::Revolution] Revolve120  label="removeToCreateScrewAndThreadedInsertHole048"
  Angle = 360
  Axis = (0,1,0)
  Base = (0,0,0)
  FaceMakerClass = Part::FaceMakerBullseye
  Placement = pos=(30.3,30.3,51.7) rot=(0,0,1;0rad)
  Solid = false
  Source = -> Face112
  Symmetric = false
FEATURE [Part::MultiFuse] Fusion087  label="createThreadedInsertHolesForFan005"
  Shapes = -> [Revolve117,Revolve118,Revolve119,Revolve120]
FEATURE [Part::Extrusion] Extrude047
  Base = -> Sketch056
  Dir = (0,0,1)
  DirMode = 2
  FaceMakerClass = Part::FaceMakerBullseye
  LengthFwd = 72
  LengthRev = 0
  Solid = true
  Symmetric = false
FEATURE [Part::Fillet] Fillet039  label="top019"
  Base = -> Extrude047
  Edges = 1 edges r=2: [Edge35]
FEATURE [Sketcher::SketchObject] Sketch057
  FullyConstrained = false
  Placement = pos=(0,0,0) rot=(1,0,0;1.5708rad)
  sketch-geometry (24):
    g0: ArcOfCircle CenterX=-4 CenterY=-10.5 CenterZ=0 NormalX=0 NormalY=0 NormalZ=1 AngleXU=0 Radius=1.5 StartAngle=6e-16 EndAngle=3.14159
    g1: ArcOfCircle CenterX=-34.2 CenterY=-10.5 CenterZ=0 NormalX=0 NormalY=0 NormalZ=1 AngleXU=0 Radius=1.5 StartAngle=0 EndAngle=3.14159
    g2: ArcOfCircle CenterX=-34.2 CenterY=-27.7 CenterZ=0 NormalX=0 NormalY=0 NormalZ=1 AngleXU=0 Radius=1.5 StartAngle=3.14159 EndAngle=6.28319
    g3: ArcOfCircle CenterX=-4 CenterY=-27.7 CenterZ=0 NormalX=0 NormalY=0 NormalZ=1 AngleXU=0 Radius=1.5 StartAngle=3.1416 EndAngle=6.28319
    g4: ArcOfCircle CenterX=-10 CenterY=-4.3 CenterZ=0 NormalX=0 NormalY=0 NormalZ=1 AngleXU=0 Radius=1.5 StartAngle=2e-16 EndAngle=3.14159
    g5: ArcOfCircle CenterX=-16.1 CenterY=-1.8 CenterZ=0 NormalX=0 NormalY=0 NormalZ=1 AngleXU=0 Radius=1.5 StartAngle=5e-16 EndAngle=3.14159
    g6: ArcOfCircle CenterX=-22.1 CenterY=-1.8 CenterZ=0 NormalX=0 NormalY=0 NormalZ=1 AngleXU=0 Radius=1.5 StartAngle=5e-16 EndAngle=3.14159
    g7: ArcOfCircle CenterX=-28.2 CenterY=-4.3 CenterZ=0 NormalX=0 NormalY=0 NormalZ=1 AngleXU=0 Radius=1.5 StartAngle=2e-16 EndAngle=3.14159
    g8: ArcOfCircle CenterX=-10 CenterY=-33.9 CenterZ=0 NormalX=0 NormalY=0 NormalZ=1 AngleXU=0 Radius=1.5 StartAngle=3.14159 EndAngle=6.28319
    g9: ArcOfCircle CenterX=-16.1 CenterY=-36.4 CenterZ=0 NormalX=0 NormalY=0 NormalZ=1 AngleXU=0 Radius=1.5 StartAngle=3.14159 EndAngle=6.28319
    g10: ArcOfCircle CenterX=-22.1 CenterY=-36.4 CenterZ=0 NormalX=0 NormalY=0 NormalZ=1 AngleXU=0 Radius=1.5 StartAngle=3.14159 EndAngle=6.28319
    g11: ArcOfCircle CenterX=-28.2 CenterY=-33.9 CenterZ=0 NormalX=0 NormalY=0 NormalZ=1 AngleXU=0 Radius=1.5 StartAngle=3.14159 EndAngle=6.28319
    g12: LineSegment StartX=-35.7 StartY=-10.5 StartZ=0 EndX=-35.7 EndY=-27.7 EndZ=0
    g13: LineSegment StartX=-32.7 StartY=-10.5 StartZ=0 EndX=-32.7 EndY=-27.7 EndZ=0
    g14: LineSegment StartX=-29.7 StartY=-33.9 StartZ=0 EndX=-29.7 EndY=-4.3 EndZ=0
    g15: LineSegment StartX=-26.7 StartY=-33.9 StartZ=0 EndX=-26.7 EndY=-4.3 EndZ=0
    g16: LineSegment StartX=-2.5 StartY=-10.5 StartZ=0 EndX=-2.5 EndY=-27.7 EndZ=0
    g17: LineSegment StartX=-8.5 StartY=-4.3 StartZ=0 EndX=-8.5 EndY=-33.9 EndZ=0
    g18: LineSegment StartX=-5.5 StartY=-10.5 StartZ=0 EndX=-5.5 EndY=-27.7 EndZ=0
    g19: LineSegment StartX=-11.5 StartY=-4.3 StartZ=0 EndX=-11.5 EndY=-33.9 EndZ=0
    g20: LineSegment StartX=-14.6 StartY=-1.8 StartZ=0 EndX=-14.6 EndY=-36.4 EndZ=0
    g21: LineSegment StartX=-17.6 StartY=-1.8 StartZ=0 EndX=-17.6 EndY=-36.4 EndZ=0
    g22: LineSegment StartX=-20.6 StartY=-36.4 StartZ=0 EndX=-20.6 EndY=-1.8 EndZ=0
    g23: LineSegment StartX=-23.6 StartY=-1.8 StartZ=0 EndX=-23.6 EndY=-36.4 EndZ=0
  constraints (48):
    c: Block(g0)
    c: Block(g1)
    c: Block(g2)
    c: Block(g3)
    c: Block(g4)
    c: Block(g5)
    c: Block(g6)
    c: Block(g7)
    c: Block(g8)
    c: Block(g9)
    c: Block(g10)
    c: Block(g11)
    c: Coincident(g12,g1)
    c: Coincident(g12,g2)
    c: Vertical(g12)
    c: Coincident(g13,g1)
    c: Coincident(g13,g2)
    c: Vertical(g13)
    c: Coincident(g14,g11)
    c: Coincident(g14,g7)
    c: Vertical(g14)
    c: Coincident(g15,g11)
    c: Coincident(g15,g7)
    c: Vertical(g15)
    c: Coincident(g16,g0)
    c: Coincident(g16,g3)
    c: Vertical(g16)
    c: Coincident(g17,g4)
    c: Coincident(g17,g8)
    c: Vertical(g17)
    c: Coincident(g18,g0)
    c: Coincident(g18,g3)
    c: Vertical(g18)
    c: Coincident(g19,g4)
    c: Coincident(g19,g8)
    c: Vertical(g19)
    c: Coincident(g20,g5)
    c: Coincident(g20,g9)
    c: Vertical(g20)
    c: Coincident(g21,g5)
    c: Coincident(g21,g9)
    c: Vertical(g21)
    c: Coincident(g22,g10)
    c: Coincident(g22,g6)
    c: Vertical(g22)
    c: Coincident(g23,g6)
    c: Coincident(g23,g10)
    c: Vertical(g23)
FEATURE [Part::Extrusion] Extrude048  label="removeToCreateFanGrillHoles004"
  Base = -> Sketch057
  Dir = (0,-1,6e-16)
  DirMode = 2
  FaceMakerClass = Part::FaceMakerBullseye
  LengthFwd = 10
  LengthRev = 0
  Placement = pos=(65.4,44,54.82) rot=(0,0,1;0rad)
  Solid = true
  Symmetric = false
FEATURE [Part::Cut] Cut040  label="top021"
  Base = -> Fillet039
  Tool = -> Extrude048
FEATURE [Part::Cylinder] Cylinder041  label="removeToCreteHoleForPlugHousing034"
  Angle = 360
  AttacherType = Attacher::AttachEngine3D
  Height = 20
  Placement = pos=(-2,19,36) rot=(0,1,0;1.5708rad)
  Radius = 14.3
FEATURE [Part::MultiFuse] Fusion089  label="removeToCreteHoleForPlugHousing035"
  Shapes = -> [Box026,Cylinder041]
FEATURE [Part::Cylinder] Cylinder042
  Angle = 360
  AttacherType = Attacher::AttachEngine3D
  Height = 20
  Placement = pos=(0,0,36.15) rot=(0,0,1;0rad)
  Radius = 14.3
FEATURE [Part::Cylinder] Cylinder043
  Angle = 360
  AttacherType = Attacher::AttachEngine3D
  Height = 10
  Placement = pos=(0,0,36.15) rot=(0,0,1;0rad)
  Radius = 4
FEATURE [Part::Box] Box027  label="removeToCreteHoleForPlugHousing036"
  AttacherType = Attacher::AttachEngine3D
  Height = 28.6
  Length = 20
  Placement = pos=(106.15,0,21.7) rot=(0,0,1;0rad)
  Width = 19
FEATURE [Part::Cut] Cut041  label="top022"
  Base = -> Cut040
  Tool = -> Fusion087
FEATURE [Part::Cut] Cut039  label="top020"
  Base = -> Cut041
  Tool = -> Fusion089
FEATURE [Part::MultiFuse] Fusion090  label="removeToCreteHoleForPlugHousing037"
  Placement = pos=(70,19,36) rot=(0,1,0;1.5708rad)
  Shapes = -> [Cylinder042,Cylinder043]
FEATURE [Part::MultiFuse] Fusion088  label="removeToCreteHoleForPlugHousing033"
  Shapes = -> [Box027,Fusion090]
FEATURE [Part::Cut] Cut042  label="removeToCreteHoleForPlugHousing038"
  Base = -> Cut039
  Tool = -> Fusion088
FEATURE [Part::MultiFuse] Fusion091  label="removeFromTop"
  Shapes = -> [Fillet038,Fusion085,Fusion084,Fusion083,Extrude045]
FEATURE [Part::Cut] Cut043  label="REAL TOP ====="
  Base = -> Fillet036
  Tool = -> Fusion091
FEATURE [Part::MultiFuse] Fusion092  label="caseScrewPillarBracket016"
  Shapes = -> [Extrude030,Extrude031,Extrude032,Extrude033,Extrude034,Extrude035,Extrude036,Extrude037,Box013,Box014]
FEATURE [Sketcher::SketchObject] Sketch058  label="topSketch015"
  FullyConstrained = true
  sketch-geometry (20):
    g0: LineSegment StartX=5.21097e-06 StartY=3 StartZ=0 EndX=5.21097e-06 EndY=19 EndZ=0
    g1: ArcOfCircle CenterX=19 CenterY=19 CenterZ=0 NormalX=0 NormalY=0 NormalZ=1 AngleXU=0 Radius=19 StartAngle=1.5708 EndAngle=3.14159
    g2: ArcOfCircle CenterX=19 CenterY=19 CenterZ=0 NormalX=0 NormalY=0 NormalZ=1 AngleXU=0 Radius=16 StartAngle=1.5708 EndAngle=3.14159
    g3: LineSegment StartX=114 StartY=35 StartZ=0 EndX=19 EndY=35 EndZ=0
    g4: LineSegment StartX=5.21097e-06 StartY=3 StartZ=0 EndX=5.21097e-06 EndY=0 EndZ=0
    g5: LineSegment StartX=3 StartY=0 StartZ=0 EndX=5.21097e-06 EndY=0 EndZ=0
    g6: LineSegment StartX=3 StartY=19 StartZ=0 EndX=3 EndY=0 EndZ=0
    g7: LineSegment StartX=19 StartY=38 StartZ=0 EndX=124 EndY=38 EndZ=0
    g8: Circle CenterX=119 CenterY=35 CenterZ=0 NormalX=0 NormalY=0 NormalZ=1 AngleXU=0 Radius=1
    g9: Circle CenterX=121 CenterY=35 CenterZ=0 NormalX=0 NormalY=0 NormalZ=1 AngleXU=0 Radius=1
    g10: Circle CenterX=121 CenterY=33 CenterZ=0 NormalX=0 NormalY=0 NormalZ=1 AngleXU=0 Radius=1
    g11: BSplineCurve PolesCount=3 KnotsCount=2 Degree=2 IsPeriodic=0
    g12: GeomPoint X=119 Y=35 Z=0
    g13: GeomPoint X=121 Y=33 Z=0
    g14: LineSegment StartX=119 StartY=35 StartZ=0 EndX=114 EndY=35 EndZ=0
    g15: ArcOfCircle CenterX=105 CenterY=19 CenterZ=0 NormalX=0 NormalY=0 NormalZ=1 AngleXU=0 Radius=19 StartAngle=5.7297 EndAngle=6.28319
    g16: ArcOfCircle CenterX=105 CenterY=19 CenterZ=0 NormalX=0 NormalY=0 NormalZ=1 AngleXU=0 Radius=16 StartAngle=5.60905 EndAngle=6.28319
    g17: LineSegment StartX=121 StartY=33 StartZ=0 EndX=121 EndY=19 EndZ=0
    g18: LineSegment StartX=124 StartY=38 StartZ=0 EndX=124 EndY=19 EndZ=0
    g19: LineSegment StartX=117.5 StartY=9.01251 StartZ=0 EndX=121.163 EndY=9.0125 EndZ=0
  constraints (46):
    c: Vertical(g0)
    c: Block(g0)
    c: Coincident(g1,g0)
    c: Block(g1)
    c: Coincident(g2,g1)
    c: Block(g2)
    c: Coincident(g3,g2)
    c: Horizontal(g3)
    c: Tangent(g3,g2)
    c: Coincident(g4,g0)
    c: Distance(g4) = 3
    c: Vertical(g4)
    c: Coincident(g5,g4)
    c: Horizontal(g5)
    c: Coincident(g6,g2)
    c: Coincident(g6,g5)
    c: Vertical(g6)
    c: Horizontal(g7)
    c: Distance(g7) = 105
    c: Coincident(g7,g1)
    c: Block(g3)
    c: Weight(g8) = 1
    c: Equal(g8,g9)
    c: Equal(g8,g10)
    c: InternalAlignment(g8,g11)
    c: InternalAlignment(g9,g11)
    c: InternalAlignment(g10,g11)
    c: InternalAlignment(g12,g11)
    c: InternalAlignment(g13,g11)
    c: Block(g11)
    c: Coincident(g14,g11)
    c: Coincident(g14,g3)
    c: Horizontal(g14)
    c: Block(g15)
    c: Coincident(g16,g15)
    c: Block(g16)
    c: Coincident(g17,g11)
    c: Coincident(g17,g16)
    c: Vertical(g17)
    c: Distance(g17) = 14
    c: Coincident(g18,g7)
    c: Coincident(g18,g15)
    c: Vertical(g18)
    c: Distance(g18) = 19
    c: Coincident(g19,g16)
    c: Coincident(g19,g15)
FEATURE [Part::Extrusion] Extrude049  label="top023"
  Base = -> Sketch058
  Dir = (0,0,1)
  DirMode = 2
  FaceMakerClass = Part::FaceMakerBullseye
  LengthFwd = 72
  LengthRev = 0
  Solid = true
  Symmetric = false
FEATURE [Sketcher::SketchObject] Sketch059
  FullyConstrained = true
  MapMode = 3
  Placement = pos=(0,0,0) rot=(1,0,0;1.5708rad)
  Support = -> [Extrude049]
  sketch-geometry (8):
    g0: Circle CenterX=80.351 CenterY=-67.6202 CenterZ=0 NormalX=0 NormalY=0 NormalZ=1 AngleXU=0 Radius=2
    g1: Circle CenterX=80.351 CenterY=-67.6202 CenterZ=0 NormalX=0 NormalY=0 NormalZ=1 AngleXU=0 Radius=3
    g2: Circle CenterX=80.351 CenterY=-4.92017 CenterZ=0 NormalX=0 NormalY=0 NormalZ=1 AngleXU=0 Radius=2
    g3: Circle CenterX=80.351 CenterY=-4.92017 CenterZ=0 NormalX=0 NormalY=0 NormalZ=1 AngleXU=0 Radius=3
    g4: Circle CenterX=23.851 CenterY=-4.92017 CenterZ=0 NormalX=0 NormalY=0 NormalZ=1 AngleXU=0 Radius=2
    g5: Circle CenterX=23.851 CenterY=-4.92017 CenterZ=0 NormalX=0 NormalY=0 NormalZ=1 AngleXU=0 Radius=3
    g6: Circle CenterX=23.851 CenterY=-67.6202 CenterZ=0 NormalX=0 NormalY=0 NormalZ=1 AngleXU=0 Radius=2
    g7: Circle CenterX=23.851 CenterY=-67.6202 CenterZ=0 NormalX=0 NormalY=0 NormalZ=1 AngleXU=0 Radius=3
  constraints (8):
    c: Block(g3)
    c: Block(g2)
    c: Block(g1)
    c: Block(g0)
    c: Block(g6)
    c: Block(g7)
    c: Block(g4)
    c: Block(g5)
FEATURE [Sketcher::SketchObject] Sketch060
  FullyConstrained = true
  MapMode = 3
  Placement = pos=(0,0,0) rot=(1,0,0;1.5708rad)
  Support = -> [Extrude049]
  sketch-geometry (8):
    g0: Circle CenterX=80.351 CenterY=-67.6202 CenterZ=0 NormalX=0 NormalY=0 NormalZ=1 AngleXU=0 Radius=3
    g1: Circle CenterX=80.351 CenterY=-4.92017 CenterZ=0 NormalX=0 NormalY=0 NormalZ=1 AngleXU=0 Radius=3
    g2: Circle CenterX=23.851 CenterY=-4.92017 CenterZ=0 NormalX=0 NormalY=0 NormalZ=1 AngleXU=0 Radius=3
    g3: Circle CenterX=23.851 CenterY=-67.6202 CenterZ=0 NormalX=0 NormalY=0 NormalZ=1 AngleXU=0 Radius=3
    g4: Circle CenterX=23.851 CenterY=-67.6202 CenterZ=0 NormalX=0 NormalY=0 NormalZ=1 AngleXU=0 Radius=5
    g5: Circle CenterX=80.351 CenterY=-67.6202 CenterZ=0 NormalX=0 NormalY=0 NormalZ=1 AngleXU=0 Radius=5
    g6: Circle CenterX=23.851 CenterY=-4.92017 CenterZ=0 NormalX=0 NormalY=0 NormalZ=1 AngleXU=0 Radius=5
    g7: Circle CenterX=80.351 CenterY=-4.92017 CenterZ=0 NormalX=0 NormalY=0 NormalZ=1 AngleXU=0 Radius=5
  constraints (8):
    c: Block(g1)
    c: Block(g0)
    c: Block(g3)
    c: Block(g2)
    c: Block(g5)
    c: Block(g4)
    c: Block(g6)
    c: Block(g7)
FEATURE [Sketcher::SketchObject] Sketch061
  FullyConstrained = true
  MapMode = 3
  Placement = pos=(0,0,0) rot=(1,0,0;1.5708rad)
  sketch-geometry (8):
    g0: Circle CenterX=80.351 CenterY=-67.6202 CenterZ=0 NormalX=0 NormalY=0 NormalZ=1 AngleXU=0 Radius=3
    g1: Circle CenterX=80.351 CenterY=-4.92017 CenterZ=0 NormalX=0 NormalY=0 NormalZ=1 AngleXU=0 Radius=3
    g2: Circle CenterX=23.851 CenterY=-4.92017 CenterZ=0 NormalX=0 NormalY=0 NormalZ=1 AngleXU=0 Radius=3
    g3: Circle CenterX=23.851 CenterY=-67.6202 CenterZ=0 NormalX=0 NormalY=0 NormalZ=1 AngleXU=0 Radius=3
    g4: Circle CenterX=23.851 CenterY=-67.6202 CenterZ=0 NormalX=0 NormalY=0 NormalZ=1 AngleXU=0 Radius=5
    g5: Circle CenterX=80.351 CenterY=-67.6202 CenterZ=0 NormalX=0 NormalY=0 NormalZ=1 AngleXU=0 Radius=5
    g6: Circle CenterX=23.851 CenterY=-4.92017 CenterZ=0 NormalX=0 NormalY=0 NormalZ=1 AngleXU=0 Radius=5
    g7: Circle CenterX=80.351 CenterY=-4.92017 CenterZ=0 NormalX=0 NormalY=0 NormalZ=1 AngleXU=0 Radius=5
  constraints (8):
    c: Block(g1)
    c: Block(g0)
    c: Block(g3)
    c: Block(g2)
    c: Block(g5)
    c: Block(g4)
    c: Block(g6)
    c: Block(g7)
FEATURE [Sketcher::SketchObject] Sketch062  label="topSketch016"
  FullyConstrained = true
  sketch-geometry (20):
    g0: LineSegment StartX=5.21097e-06 StartY=3 StartZ=0 EndX=5.21097e-06 EndY=19 EndZ=0
    g1: ArcOfCircle CenterX=19 CenterY=19 CenterZ=0 NormalX=0 NormalY=0 NormalZ=1 AngleXU=0 Radius=19 StartAngle=1.5708 EndAngle=3.14159
    g2: ArcOfCircle CenterX=19 CenterY=19 CenterZ=0 NormalX=0 NormalY=0 NormalZ=1 AngleXU=0 Radius=16 StartAngle=1.5708 EndAngle=3.14159
    g3: LineSegment StartX=114 StartY=35 StartZ=0 EndX=19 EndY=35 EndZ=0
    g4: LineSegment StartX=5.21097e-06 StartY=3 StartZ=0 EndX=5.21097e-06 EndY=0 EndZ=0
    g5: LineSegment StartX=3 StartY=0 StartZ=0 EndX=5.21097e-06 EndY=0 EndZ=0
    g6: LineSegment StartX=3 StartY=19 StartZ=0 EndX=3 EndY=0 EndZ=0
    g7: LineSegment StartX=19 StartY=38 StartZ=0 EndX=124 EndY=38 EndZ=0
    g8: Circle CenterX=119 CenterY=35 CenterZ=0 NormalX=0 NormalY=0 NormalZ=1 AngleXU=0 Radius=1
    g9: Circle CenterX=121 CenterY=35 CenterZ=0 NormalX=0 NormalY=0 NormalZ=1 AngleXU=0 Radius=1
    g10: Circle CenterX=121 CenterY=33 CenterZ=0 NormalX=0 NormalY=0 NormalZ=1 AngleXU=0 Radius=1
    g11: BSplineCurve PolesCount=3 KnotsCount=2 Degree=2 IsPeriodic=0
    g12: GeomPoint X=119 Y=35 Z=0
    g13: GeomPoint X=121 Y=33 Z=0
    g14: LineSegment StartX=119 StartY=35 StartZ=0 EndX=114 EndY=35 EndZ=0
    g15: ArcOfCircle CenterX=105 CenterY=19 CenterZ=0 NormalX=0 NormalY=0 NormalZ=1 AngleXU=0 Radius=19 StartAngle=5.7297 EndAngle=6.28319
    g16: ArcOfCircle CenterX=105 CenterY=19 CenterZ=0 NormalX=0 NormalY=0 NormalZ=1 AngleXU=0 Radius=16 StartAngle=5.60905 EndAngle=6.28319
    g17: LineSegment StartX=121 StartY=33 StartZ=0 EndX=121 EndY=19 EndZ=0
    g18: LineSegment StartX=124 StartY=38 StartZ=0 EndX=124 EndY=19 EndZ=0
    g19: LineSegment StartX=117.5 StartY=9.01251 StartZ=0 EndX=121.163 EndY=9.0125 EndZ=0
  constraints (46):
    c: Vertical(g0)
    c: Block(g0)
    c: Coincident(g1,g0)
    c: Block(g1)
    c: Coincident(g2,g1)
    c: Block(g2)
    c: Coincident(g3,g2)
    c: Horizontal(g3)
    c: Tangent(g3,g2)
    c: Coincident(g4,g0)
    c: Distance(g4) = 3
    c: Vertical(g4)
    c: Coincident(g5,g4)
    c: Horizontal(g5)
    c: Coincident(g6,g2)
    c: Coincident(g6,g5)
    c: Vertical(g6)
    c: Horizontal(g7)
    c: Distance(g7) = 105
    c: Coincident(g7,g1)
    c: Block(g3)
    c: Weight(g8) = 1
    c: Equal(g8,g9)
    c: Equal(g8,g10)
    c: InternalAlignment(g8,g11)
    c: InternalAlignment(g9,g11)
    c: InternalAlignment(g10,g11)
    c: InternalAlignment(g12,g11)
    c: InternalAlignment(g13,g11)
    c: Block(g11)
    c: Coincident(g14,g11)
    c: Coincident(g14,g3)
    c: Horizontal(g14)
    c: Block(g15)
    c: Coincident(g16,g15)
    c: Block(g16)
    c: Coincident(g17,g11)
    c: Coincident(g17,g16)
    c: Vertical(g17)
    c: Distance(g17) = 14
    c: Coincident(g18,g7)
    c: Coincident(g18,g15)
    c: Vertical(g18)
    c: Distance(g18) = 19
    c: Coincident(g19,g16)
    c: Coincident(g19,g15)
FEATURE [Part::Extrusion] Extrude053  label="top024"
  Base = -> Sketch062
  Dir = (0,0,1)
  DirMode = 2
  FaceMakerClass = Part::FaceMakerBullseye
  LengthFwd = 72
  LengthRev = 0
  Solid = true
  Symmetric = false
FEATURE [Sketcher::SketchObject] Sketch063
  FullyConstrained = true
  MapMode = 3
  Placement = pos=(0,0,0) rot=(1,0,0;1.5708rad)
  Support = -> [Extrude053]
  sketch-geometry (8):
    g0: Circle CenterX=80.351 CenterY=-67.6202 CenterZ=0 NormalX=0 NormalY=0 NormalZ=1 AngleXU=0 Radius=2
    g1: Circle CenterX=80.351 CenterY=-67.6202 CenterZ=0 NormalX=0 NormalY=0 NormalZ=1 AngleXU=0 Radius=3
    g2: Circle CenterX=80.351 CenterY=-4.92017 CenterZ=0 NormalX=0 NormalY=0 NormalZ=1 AngleXU=0 Radius=2
    g3: Circle CenterX=80.351 CenterY=-4.92017 CenterZ=0 NormalX=0 NormalY=0 NormalZ=1 AngleXU=0 Radius=3
    g4: Circle CenterX=23.851 CenterY=-4.92017 CenterZ=0 NormalX=0 NormalY=0 NormalZ=1 AngleXU=0 Radius=2
    g5: Circle CenterX=23.851 CenterY=-4.92017 CenterZ=0 NormalX=0 NormalY=0 NormalZ=1 AngleXU=0 Radius=3
    g6: Circle CenterX=23.851 CenterY=-67.6202 CenterZ=0 NormalX=0 NormalY=0 NormalZ=1 AngleXU=0 Radius=2
    g7: Circle CenterX=23.851 CenterY=-67.6202 CenterZ=0 NormalX=0 NormalY=0 NormalZ=1 AngleXU=0 Radius=3
  constraints (8):
    c: Block(g3)
    c: Block(g2)
    c: Block(g1)
    c: Block(g0)
    c: Block(g6)
    c: Block(g7)
    c: Block(g4)
    c: Block(g5)
FEATURE [Part::Extrusion] Extrude054
  Base = -> Sketch063
  Dir = (0,-1,2e-16)
  DirMode = 2
  FaceMakerClass = Part::FaceMakerBullseye
  LengthFwd = 6
  LengthRev = 0
  Placement = pos=(0,9,0) rot=(0,0,1;0rad)
  Solid = true
  Symmetric = false
FEATURE [Sketcher::SketchObject] Sketch064  label="topSketch017"
  FullyConstrained = true
  sketch-geometry (20):
    g0: LineSegment StartX=5.21097e-06 StartY=3 StartZ=0 EndX=5.21097e-06 EndY=19 EndZ=0
    g1: ArcOfCircle CenterX=19 CenterY=19 CenterZ=0 NormalX=0 NormalY=0 NormalZ=1 AngleXU=0 Radius=19 StartAngle=1.5708 EndAngle=3.14159
    g2: ArcOfCircle CenterX=19 CenterY=19 CenterZ=0 NormalX=0 NormalY=0 NormalZ=1 AngleXU=0 Radius=16 StartAngle=1.5708 EndAngle=3.14159
    g3: LineSegment StartX=114 StartY=35 StartZ=0 EndX=19 EndY=35 EndZ=0
    g4: LineSegment StartX=5.21097e-06 StartY=3 StartZ=0 EndX=5.21097e-06 EndY=0 EndZ=0
    g5: LineSegment StartX=3 StartY=0 StartZ=0 EndX=5.21097e-06 EndY=0 EndZ=0
    g6: LineSegment StartX=3 StartY=19 StartZ=0 EndX=3 EndY=0 EndZ=0
    g7: LineSegment StartX=19 StartY=38 StartZ=0 EndX=124 EndY=38 EndZ=0
    g8: Circle CenterX=119 CenterY=35 CenterZ=0 NormalX=0 NormalY=0 NormalZ=1 AngleXU=0 Radius=1
    g9: Circle CenterX=121 CenterY=35 CenterZ=0 NormalX=0 NormalY=0 NormalZ=1 AngleXU=0 Radius=1
    g10: Circle CenterX=121 CenterY=33 CenterZ=0 NormalX=0 NormalY=0 NormalZ=1 AngleXU=0 Radius=1
    g11: BSplineCurve PolesCount=3 KnotsCount=2 Degree=2 IsPeriodic=0
    g12: GeomPoint X=119 Y=35 Z=0
    g13: GeomPoint X=121 Y=33 Z=0
    g14: LineSegment StartX=119 StartY=35 StartZ=0 EndX=114 EndY=35 EndZ=0
    g15: ArcOfCircle CenterX=105 CenterY=19 CenterZ=0 NormalX=0 NormalY=0 NormalZ=1 AngleXU=0 Radius=19 StartAngle=5.7297 EndAngle=6.28319
    g16: ArcOfCircle CenterX=105 CenterY=19 CenterZ=0 NormalX=0 NormalY=0 NormalZ=1 AngleXU=0 Radius=16 StartAngle=5.60905 EndAngle=6.28319
    g17: LineSegment StartX=121 StartY=33 StartZ=0 EndX=121 EndY=19 EndZ=0
    g18: LineSegment StartX=124 StartY=38 StartZ=0 EndX=124 EndY=19 EndZ=0
    g19: LineSegment StartX=117.5 StartY=9.01251 StartZ=0 EndX=121.163 EndY=9.0125 EndZ=0
  constraints (46):
    c: Vertical(g0)
    c: Block(g0)
    c: Coincident(g1,g0)
    c: Block(g1)
    c: Coincident(g2,g1)
    c: Block(g2)
    c: Coincident(g3,g2)
    c: Horizontal(g3)
    c: Tangent(g3,g2)
    c: Coincident(g4,g0)
    c: Distance(g4) = 3
    c: Vertical(g4)
    c: Coincident(g5,g4)
    c: Horizontal(g5)
    c: Coincident(g6,g2)
    c: Coincident(g6,g5)
    c: Vertical(g6)
    c: Horizontal(g7)
    c: Distance(g7) = 105
    c: Coincident(g7,g1)
    c: Block(g3)
    c: Weight(g8) = 1
    c: Equal(g8,g9)
    c: Equal(g8,g10)
    c: InternalAlignment(g8,g11)
    c: InternalAlignment(g9,g11)
    c: InternalAlignment(g10,g11)
    c: InternalAlignment(g12,g11)
    c: InternalAlignment(g13,g11)
    c: Block(g11)
    c: Coincident(g14,g11)
    c: Coincident(g14,g3)
    c: Horizontal(g14)
    c: Block(g15)
    c: Coincident(g16,g15)
    c: Block(g16)
    c: Coincident(g17,g11)
    c: Coincident(g17,g16)
    c: Vertical(g17)
    c: Distance(g17) = 14
    c: Coincident(g18,g7)
    c: Coincident(g18,g15)
    c: Vertical(g18)
    c: Distance(g18) = 19
    c: Coincident(g19,g16)
    c: Coincident(g19,g15)
FEATURE [Sketcher::SketchObject] Sketch065
  FullyConstrained = true
  MapMode = 3
  Placement = pos=(0,0,0) rot=(1,0,0;1.5708rad)
  sketch-geometry (8):
    g0: Circle CenterX=80.351 CenterY=-67.6202 CenterZ=0 NormalX=0 NormalY=0 NormalZ=1 AngleXU=0 Radius=3
    g1: Circle CenterX=80.351 CenterY=-4.92017 CenterZ=0 NormalX=0 NormalY=0 NormalZ=1 AngleXU=0 Radius=3
    g2: Circle CenterX=23.851 CenterY=-4.92017 CenterZ=0 NormalX=0 NormalY=0 NormalZ=1 AngleXU=0 Radius=3
    g3: Circle CenterX=23.851 CenterY=-67.6202 CenterZ=0 NormalX=0 NormalY=0 NormalZ=1 AngleXU=0 Radius=3
    g4: Circle CenterX=23.851 CenterY=-67.6202 CenterZ=0 NormalX=0 NormalY=0 NormalZ=1 AngleXU=0 Radius=5
    g5: Circle CenterX=80.351 CenterY=-67.6202 CenterZ=0 NormalX=0 NormalY=0 NormalZ=1 AngleXU=0 Radius=5
    g6: Circle CenterX=23.851 CenterY=-4.92017 CenterZ=0 NormalX=0 NormalY=0 NormalZ=1 AngleXU=0 Radius=5
    g7: Circle CenterX=80.351 CenterY=-4.92017 CenterZ=0 NormalX=0 NormalY=0 NormalZ=1 AngleXU=0 Radius=5
  constraints (8):
    c: Block(g1)
    c: Block(g0)
    c: Block(g3)
    c: Block(g2)
    c: Block(g5)
    c: Block(g4)
    c: Block(g6)
    c: Block(g7)
FEATURE [Part::Extrusion] Extrude056
  Base = -> Sketch065
  Dir = (0,-1,2e-16)
  DirMode = 2
  FaceMakerClass = Part::FaceMakerBullseye
  LengthFwd = 2
  LengthRev = 0
  Solid = true
  Symmetric = false
FEATURE [Part::Extrusion] Extrude057  label="top025"
  Base = -> Sketch064
  Dir = (0,0,1)
  DirMode = 2
  FaceMakerClass = Part::FaceMakerBullseye
  LengthFwd = 72
  LengthRev = 0
  Solid = true
  Symmetric = false
FEATURE [Sketcher::SketchObject] Sketch066
  FullyConstrained = true
  MapMode = 3
  Placement = pos=(0,0,0) rot=(1,0,0;1.5708rad)
  Support = -> [Extrude057]
  sketch-geometry (8):
    g0: Circle CenterX=80.351 CenterY=-67.6202 CenterZ=0 NormalX=0 NormalY=0 NormalZ=1 AngleXU=0 Radius=3
    g1: Circle CenterX=80.351 CenterY=-4.92017 CenterZ=0 NormalX=0 NormalY=0 NormalZ=1 AngleXU=0 Radius=3
    g2: Circle CenterX=23.851 CenterY=-4.92017 CenterZ=0 NormalX=0 NormalY=0 NormalZ=1 AngleXU=0 Radius=3
    g3: Circle CenterX=23.851 CenterY=-67.6202 CenterZ=0 NormalX=0 NormalY=0 NormalZ=1 AngleXU=0 Radius=3
    g4: Circle CenterX=23.851 CenterY=-67.6202 CenterZ=0 NormalX=0 NormalY=0 NormalZ=1 AngleXU=0 Radius=5
    g5: Circle CenterX=80.351 CenterY=-67.6202 CenterZ=0 NormalX=0 NormalY=0 NormalZ=1 AngleXU=0 Radius=5
    g6: Circle CenterX=23.851 CenterY=-4.92017 CenterZ=0 NormalX=0 NormalY=0 NormalZ=1 AngleXU=0 Radius=5
    g7: Circle CenterX=80.351 CenterY=-4.92017 CenterZ=0 NormalX=0 NormalY=0 NormalZ=1 AngleXU=0 Radius=5
  constraints (8):
    c: Block(g1)
    c: Block(g0)
    c: Block(g3)
    c: Block(g2)
    c: Block(g5)
    c: Block(g4)
    c: Block(g6)
    c: Block(g7)
FEATURE [Part::Extrusion] Extrude055
  Base = -> Sketch066
  Dir = (0,-1,2e-16)
  DirMode = 2
  FaceMakerClass = Part::FaceMakerBullseye
  LengthFwd = 2
  LengthRev = 0
  Solid = true
  Symmetric = false
FEATURE [Part::Fillet] Fillet041
  Base = -> Extrude056
  Edges = 4 edges r=1.99: [Edge6,Edge12,Edge18,Edge24]
FEATURE [Part::Cut] Cut045
  Base = -> Extrude055
  Placement = pos=(0,6,0) rot=(0,0,1;0rad)
  Tool = -> Fillet041
FEATURE [Part::MultiFuse] Fusion095  label="pcbScrewPillars"
  Placement = pos=(-3.2,-1,72.3) rot=(0,0,1;0rad)
  Shapes = -> [Cut045,Extrude054]
FEATURE [Part::Feature] Face113
  shape: bbox 3.2 x 1.5 x 2e-07 mm, 1 faces, 0 solids (baked)
FEATURE [Part::Revolution] Revolve121  label="backCaseScrewRetainer002"
  Angle = 360
  Axis = (0,1,0)
  Base = (0,0,0)
  FaceMakerClass = Part::FaceMakerBullseye
  Placement = pos=(12.5,3,62) rot=(0,0,1;0rad)
  Solid = false
  Source = -> Face113
  Symmetric = false
FEATURE [Part::Feature] Face114
  shape: bbox 3.2 x 1.5 x 2e-07 mm, 1 faces, 0 solids (baked)
FEATURE [Part::Feature] Face115
  shape: bbox 3.2 x 1.5 x 2e-07 mm, 1 faces, 0 solids (baked)
FEATURE [Part::Feature] Face116
  shape: bbox 3.2 x 1.5 x 2e-07 mm, 1 faces, 0 solids (baked)
FEATURE [Part::Revolution] Revolve122  label="frontCaseScrewRetainer004"
  Angle = 360
  Axis = (0,1,0)
  Base = (0,0,0)
  FaceMakerClass = Part::FaceMakerBullseye
  Placement = pos=(89.5,3,68.5) rot=(0,0,1;0rad)
  Solid = false
  Source = -> Face115
  Symmetric = false
FEATURE [Part::Revolution] Revolve123  label="frontCaseScrewRetainer005"
  Angle = 360
  Axis = (0,1,0)
  Base = (0,0,0)
  FaceMakerClass = Part::FaceMakerBullseye
  Placement = pos=(89.5,3,3.5) rot=(0,0,1;0rad)
  Solid = false
  Source = -> Face116
  Symmetric = false
FEATURE [Part::Revolution] Revolve124  label="backCaseScrewRetainer003"
  Angle = 360
  Axis = (0,1,0)
  Base = (0,0,0)
  FaceMakerClass = Part::FaceMakerBullseye
  Placement = pos=(12.5,3,10) rot=(0,0,1;0rad)
  Solid = false
  Source = -> Face114
  Symmetric = false
FEATURE [Part::Feature] Face117
  shape: bbox 3.6 x 3.2 x 2e-07 mm, 1 faces, 0 solids (baked)
FEATURE [Part::Revolution] Revolve125  label="moreFrontCaseScrewRetainer004"
  Angle = 360
  Axis = (0,1,0)
  Base = (0,0,0)
  FaceMakerClass = Part::FaceMakerBullseye
  Placement = pos=(109.5,4.5,68.5) rot=(0,0,1;0rad)
  Solid = false
  Source = -> Face117
  Symmetric = false
FEATURE [Part::Feature] Face118
  shape: bbox 3.6 x 3.2 x 2e-07 mm, 1 faces, 0 solids (baked)
FEATURE [Part::Revolution] Revolve126  label="moreFrontCaseScrewRetainer005"
  Angle = 360
  Axis = (0,1,0)
  Base = (0,0,0)
  FaceMakerClass = Part::FaceMakerBullseye
  Placement = pos=(109.5,4.5,3.5) rot=(0,0,1;0rad)
  Solid = false
  Source = -> Face118
  Symmetric = false
FEATURE [Part::MultiFuse] Fusion096  label="screwRetainers001"
  Shapes = -> [Revolve126,Revolve125,Revolve124,Revolve123,Revolve122,Revolve121]
FEATURE [Part::Feature] Face119
  shape: bbox 10 x 16.5 x 2e-07 mm, 1 faces, 0 solids (baked)
FEATURE [Part::Revolution] Revolve130  label="plugHousing050"
  Angle = 360
  Axis = (0,1,0)
  Base = (0,0,0)
  FaceMakerClass = Part::FaceMakerBullseye
  Placement = pos=(0,0,36.15) rot=(0,0,1;0rad)
  Solid = false
  Source = -> Face119
  Symmetric = false
FEATURE [Part::Feature] Face120
  shape: bbox 10 x 16.5 x 2e-07 mm, 1 faces, 0 solids (baked)
FEATURE [Part::Feature] Face121
  shape: bbox 10 x 16.5 x 2e-07 mm, 1 faces, 0 solids (baked)
FEATURE [Part::Revolution] Revolve127  label="plugHousing047"
  Angle = 360
  Axis = (0,1,0)
  Base = (0,0,0)
  FaceMakerClass = Part::FaceMakerBullseye
  Placement = pos=(0,0,36.15) rot=(0,0,1;0rad)
  Solid = false
  Source = -> Face121
  Symmetric = false
FEATURE [Part::Feature] Face122
  shape: bbox 10 x 16.5 x 2e-07 mm, 1 faces, 0 solids (baked)
FEATURE [Part::Feature] Face123
  shape: bbox 10 x 16.5 x 2e-07 mm, 1 faces, 0 solids (baked)
FEATURE [Part::Revolution] Revolve128  label="plugHousing048"
  Angle = 360
  Axis = (0,1,0)
  Base = (0,0,0)
  FaceMakerClass = Part::FaceMakerBullseye
  Placement = pos=(0,0,36.15) rot=(0,0,1;0rad)
  Solid = false
  Source = -> Face123
  Symmetric = false
FEATURE [Part::MultiFuse] Fusion100  label="plugHousing054"
  Placement = pos=(0,0,0) rot=(0,0,1;1.5708rad)
  Shapes = -> [Revolve130,Revolve128]
FEATURE [Part::Feature] Face124
  shape: bbox 10 x 16.5 x 2e-07 mm, 1 faces, 0 solids (baked)
FEATURE [Part::Feature] Face125
  shape: bbox 10 x 16.5 x 2e-07 mm, 1 faces, 0 solids (baked)
FEATURE [Part::Revolution] Revolve129  label="plugHousing049"
  Angle = 360
  Axis = (0,1,0)
  Base = (0,0,0)
  FaceMakerClass = Part::FaceMakerBullseye
  Placement = pos=(0,0,36.15) rot=(0,0,1;0rad)
  Solid = false
  Source = -> Face125
  Symmetric = false
FEATURE [Part::Feature] Face126
  shape: bbox 10 x 16.5 x 2e-07 mm, 1 faces, 0 solids (baked)
FEATURE [Part::Revolution] Revolve131  label="plugHousing058"
  Angle = 360
  Axis = (0,1,0)
  Base = (0,0,0)
  FaceMakerClass = Part::FaceMakerBullseye
  Placement = pos=(0,0,36.15) rot=(0,0,1;0rad)
  Solid = false
  Source = -> Face120
  Symmetric = false
FEATURE [Part::MultiFuse] Fusion099  label="plugHousing053"
  Placement = pos=(0,0,0) rot=(0,0,1;1.5708rad)
  Shapes = -> [Revolve127,Revolve131]
FEATURE [Part::MultiFuse] Fusion102  label="plugHousing056"
  Placement = pos=(0,19,0) rot=(0,0,1;3.14159rad)
  Shapes = -> [Fusion100,Fusion099]
FEATURE [Part::Revolution] Revolve132  label="plugHousing059"
  Angle = 360
  Axis = (0,1,0)
  Base = (0,0,0)
  FaceMakerClass = Part::FaceMakerBullseye
  Placement = pos=(0,0,36.15) rot=(0,0,1;0rad)
  Solid = false
  Source = -> Face126
  Symmetric = false
FEATURE [Part::Revolution] Revolve133  label="plugHousing060"
  Angle = 360
  Axis = (0,1,0)
  Base = (0,0,0)
  FaceMakerClass = Part::FaceMakerBullseye
  Placement = pos=(0,0,36.15) rot=(0,0,1;0rad)
  Solid = false
  Source = -> Face122
  Symmetric = false
FEATURE [Part::MultiFuse] Fusion097  label="plugHousing051"
  Placement = pos=(0,0,0) rot=(0,0,1;1.5708rad)
  Shapes = -> [Revolve133,Revolve132]
FEATURE [Part::Revolution] Revolve134  label="plugHousing061"
  Angle = 360
  Axis = (0,1,0)
  Base = (0,0,0)
  FaceMakerClass = Part::FaceMakerBullseye
  Placement = pos=(0,0,36.15) rot=(0,0,1;0rad)
  Solid = false
  Source = -> Face124
  Symmetric = false
FEATURE [Part::MultiFuse] Fusion101  label="plugHousing055"
  Placement = pos=(0,0,0) rot=(0,0,1;1.5708rad)
  Shapes = -> [Revolve129,Revolve134]
FEATURE [Part::MultiFuse] Fusion098  label="plugHousing052"
  Placement = pos=(0,19,0) rot=(0,0,1;3.14159rad)
  Shapes = -> [Fusion097,Fusion101]
FEATURE [Part::MultiFuse] Fusion103  label="plugHousing057"
  Placement = pos=(122.621,0,-0.15) rot=(0,0,1;0rad)
  Shapes = -> [Fusion102,Fusion098]
FEATURE [Part::Box] Box028  label="Cube015"
  AttacherType = Attacher::AttachEngine3D
  Height = 28
  Length = 3
  Placement = pos=(110.7,19,22) rot=(0,0,1;0rad)
  Width = 15.7
FEATURE [Part::Cylinder] Cylinder044
  Angle = 360
  AttacherType = Attacher::AttachEngine3D
  Height = 20
  Placement = pos=(0,0,36.15) rot=(0,0,1;0rad)
  Radius = 10.3
FEATURE [Part::Cylinder] Cylinder045
  Angle = 360
  AttacherType = Attacher::AttachEngine3D
  Height = 10
  Placement = pos=(0,0,36.15) rot=(0,0,1;0rad)
  Radius = 4
FEATURE [Part::MultiFuse] Fusion104  label="removeToCreteHoleForPlugHousing040"
  Placement = pos=(70,19,36) rot=(0,1,0;1.5708rad)
  Shapes = -> [Cylinder044,Cylinder045]
FEATURE [Part::Cut] Cut046  label="plugHousingTab003"
  Base = -> Box028
  Tool = -> Fusion104
FEATURE [Part::MultiFuse] Fusion105  label="plugHousing062"
  Shapes = -> [Fusion103,Cut046]
FEATURE [Part::Fillet] Fillet042
  Base = -> Fusion105
  Edges = 1 edges r=2: [Edge25]
FEATURE [Part::Fillet] Fillet043  label="plugHousing063"
  Base = -> Fillet042
  Edges = 1 edges r=2: [Edge8]
  Placement = pos=(7,0,0) rot=(0,0,1;0rad)
FEATURE [Part::Feature] Face127
  shape: bbox 10 x 16.5 x 2e-07 mm, 1 faces, 0 solids (baked)
FEATURE [Part::Feature] Face128
  shape: bbox 10 x 16.5 x 2e-07 mm, 1 faces, 0 solids (baked)
FEATURE [Part::Revolution] Revolve137  label="plugHousing070"
  Angle = 360
  Axis = (0,1,0)
  Base = (0,0,0)
  FaceMakerClass = Part::FaceMakerBullseye
  Placement = pos=(0,0,36.15) rot=(0,0,1;0rad)
  Solid = false
  Source = -> Face127
  Symmetric = false
FEATURE [Part::Revolution] Revolve140  label="plugHousing073"
  Angle = 360
  Axis = (0,1,0)
  Base = (0,0,0)
  FaceMakerClass = Part::FaceMakerBullseye
  Placement = pos=(0,0,36.15) rot=(0,0,1;0rad)
  Solid = false
  Source = -> Face128
  Symmetric = false
FEATURE [Part::Feature] Face129
  shape: bbox 10 x 16.5 x 2e-07 mm, 1 faces, 0 solids (baked)
FEATURE [Part::Revolution] Revolve138  label="plugHousing071"
  Angle = 360
  Axis = (0,1,0)
  Base = (0,0,0)
  FaceMakerClass = Part::FaceMakerBullseye
  Placement = pos=(0,0,36.15) rot=(0,0,1;0rad)
  Solid = false
  Source = -> Face129
  Symmetric = false
FEATURE [Part::Feature] Face130
  shape: bbox 10 x 16.5 x 2e-07 mm, 1 faces, 0 solids (baked)
FEATURE [Part::Revolution] Revolve139  label="plugHousing072"
  Angle = 360
  Axis = (0,1,0)
  Base = (0,0,0)
  FaceMakerClass = Part::FaceMakerBullseye
  Placement = pos=(0,0,36.15) rot=(0,0,1;0rad)
  Solid = false
  Source = -> Face130
  Symmetric = false
FEATURE [Part::Feature] Face131
  shape: bbox 10 x 16.5 x 2e-07 mm, 1 faces, 0 solids (baked)
FEATURE [Part::Revolution] Revolve135  label="plugHousing068"
  Angle = 360
  Axis = (0,1,0)
  Base = (0,0,0)
  FaceMakerClass = Part::FaceMakerBullseye
  Placement = pos=(0,0,36.15) rot=(0,0,1;0rad)
  Solid = false
  Source = -> Face131
  Symmetric = false
FEATURE [Part::MultiFuse] Fusion112  label="plugHousing078"
  Placement = pos=(0,0,0) rot=(0,0,1;1.5708rad)
  Shapes = -> [Revolve135,Revolve139]
FEATURE [Part::Feature] Face132
  shape: bbox 10 x 16.5 x 2e-07 mm, 1 faces, 0 solids (baked)
FEATURE [Part::Revolution] Revolve141  label="plugHousing074"
  Angle = 360
  Axis = (0,1,0)
  Base = (0,0,0)
  FaceMakerClass = Part::FaceMakerBullseye
  Placement = pos=(0,0,36.15) rot=(0,0,1;0rad)
  Solid = false
  Source = -> Face132
  Symmetric = false
FEATURE [Part::MultiFuse] Fusion110  label="plugHousing076"
  Placement = pos=(0,0,0) rot=(0,0,1;1.5708rad)
  Shapes = -> [Revolve141,Revolve140]
FEATURE [Part::Feature] Face133
  shape: bbox 10 x 16.5 x 2e-07 mm, 1 faces, 0 solids (baked)
FEATURE [Part::Revolution] Revolve136  label="plugHousing069"
  Angle = 360
  Axis = (0,1,0)
  Base = (0,0,0)
  FaceMakerClass = Part::FaceMakerBullseye
  Placement = pos=(0,0,36.15) rot=(0,0,1;0rad)
  Solid = false
  Source = -> Face133
  Symmetric = false
FEATURE [Part::MultiFuse] Fusion106  label="plugHousing064"
  Placement = pos=(0,0,0) rot=(0,0,1;1.5708rad)
  Shapes = -> [Revolve138,Revolve136]
FEATURE [Part::MultiFuse] Fusion108  label="plugHousing066"
  Placement = pos=(0,19,0) rot=(0,0,1;3.14159rad)
  Shapes = -> [Fusion106,Fusion112]
FEATURE [Part::Feature] Face134
  shape: bbox 10 x 16.5 x 2e-07 mm, 1 faces, 0 solids (baked)
FEATURE [Part::Revolution] Revolve142  label="plugHousing075"
  Angle = 360
  Axis = (0,1,0)
  Base = (0,0,0)
  FaceMakerClass = Part::FaceMakerBullseye
  Placement = pos=(0,0,36.15) rot=(0,0,1;0rad)
  Solid = false
  Source = -> Face134
  Symmetric = false
FEATURE [Part::MultiFuse] Fusion107  label="plugHousing065"
  Placement = pos=(0,0,0) rot=(0,0,1;1.5708rad)
  Shapes = -> [Revolve137,Revolve142]
FEATURE [Part::MultiFuse] Fusion111  label="plugHousing077"
  Placement = pos=(0,19,0) rot=(0,0,1;3.14159rad)
  Shapes = -> [Fusion110,Fusion107]
FEATURE [Part::MultiFuse] Fusion109  label="plugHousing067"
  Placement = pos=(131.236,0,-0.15) rot=(0,0,1;0rad)
  Shapes = -> [Fusion108,Fusion111]
FEATURE [Part::MultiFuse] Fusion113  label="plugHousing079"
  Shapes = -> [Fillet043,Fusion109]
FEATURE [Part::Feature] Face135
  shape: bbox 3.5 x 17.8 x 2e-07 mm, 1 faces, 0 solids (baked)
FEATURE [Part::Revolution] Revolve143  label="removeToCreateScrewAndThreadedInsertHole049"
  Angle = 360
  Axis = (0,1,0)
  Base = (0,0,0)
  FaceMakerClass = Part::FaceMakerBullseye
  Placement = pos=(12.5,0,10) rot=(0,0,1;0rad)
  Solid = false
  Source = -> Face135
  Symmetric = false
FEATURE [Part::Feature] Face136
  shape: bbox 3.5 x 17.8 x 2e-07 mm, 1 faces, 0 solids (baked)
FEATURE [Part::Revolution] Revolve144  label="removeToCreateScrewAndThreadedInsertHole050"
  Angle = 360
  Axis = (0,1,0)
  Base = (0,0,0)
  FaceMakerClass = Part::FaceMakerBullseye
  Placement = pos=(12.5,0,62) rot=(0,0,1;0rad)
  Solid = false
  Source = -> Face136
  Symmetric = false
FEATURE [Part::Feature] Face137
  shape: bbox 3.5 x 17.8 x 2e-07 mm, 1 faces, 0 solids (baked)
FEATURE [Part::Revolution] Revolve145  label="removeToCreateScrewAndThreadedInsertHole051"
  Angle = 360
  Axis = (0,1,0)
  Base = (0,0,0)
  FaceMakerClass = Part::FaceMakerBullseye
  Placement = pos=(89.5,0,68.5) rot=(0,0,1;0rad)
  Solid = false
  Source = -> Face137
  Symmetric = false
FEATURE [Part::Feature] Face138
  shape: bbox 3.5 x 17.8 x 2e-07 mm, 1 faces, 0 solids (baked)
FEATURE [Part::Revolution] Revolve146  label="removeToCreateScrewAndThreadedInsertHole052"
  Angle = 360
  Axis = (0,1,0)
  Base = (0,0,0)
  FaceMakerClass = Part::FaceMakerBullseye
  Placement = pos=(89.5,0,3.5) rot=(0,0,1;0rad)
  Solid = false
  Source = -> Face138
  Symmetric = false
FEATURE [Part::Feature] Face139
  shape: bbox 3.5 x 17.8 x 2e-07 mm, 1 faces, 0 solids (baked)
FEATURE [Part::Revolution] Revolve147  label="removeToCreateScrewAndThreadedInsertHole053"
  Angle = 360
  Axis = (0,1,0)
  Base = (0,0,0)
  FaceMakerClass = Part::FaceMakerBullseye
  Placement = pos=(109.5,4.7,3.5) rot=(0,0,1;0rad)
  Solid = false
  Source = -> Face139
  Symmetric = false
FEATURE [Part::Feature] Face140
  shape: bbox 3.5 x 17.8 x 2e-07 mm, 1 faces, 0 solids (baked)
FEATURE [Part::Revolution] Revolve148  label="removeToCreateScrewAndThreadedInsertHole054"
  Angle = 360
  Axis = (0,1,0)
  Base = (0,0,0)
  FaceMakerClass = Part::FaceMakerBullseye
  Placement = pos=(109.5,4.7,68.5) rot=(0,0,1;0rad)
  Solid = false
  Source = -> Face140
  Symmetric = false
FEATURE [Part::MultiFuse] Fusion114  label="removeToCreateScrewAndThreadedInsertHole055"
  Shapes = -> [Revolve148,Revolve147,Revolve146,Revolve145,Revolve144,Revolve143]
FEATURE [Part::Cut] Cut047  label="casePillars004"
  Base = -> Cut037
  Tool = -> Fusion114
FEATURE [Part::Feature] Face141
  shape: bbox 3.5 x 17.8 x 2e-07 mm, 1 faces, 0 solids (baked)
FEATURE [Part::Feature] Face142
  shape: bbox 3.5 x 17.8 x 2e-07 mm, 1 faces, 0 solids (baked)
FEATURE [Part::Feature] Face143
  shape: bbox 3.5 x 17.8 x 2e-07 mm, 1 faces, 0 solids (baked)
FEATURE [Part::Revolution] Revolve149  label="removeToCreateScrewAndThreadedInsertHole057"
  Angle = 360
  Axis = (0,1,0)
  Base = (0,0,0)
  FaceMakerClass = Part::FaceMakerBullseye
  Placement = pos=(12.5,0,10) rot=(0,0,1;0rad)
  Solid = false
  Source = -> Face141
  Symmetric = false
FEATURE [Part::Feature] Face144
  shape: bbox 3.5 x 17.8 x 2e-07 mm, 1 faces, 0 solids (baked)
FEATURE [Part::Feature] Face145
  shape: bbox 3.5 x 17.8 x 2e-07 mm, 1 faces, 0 solids (baked)
FEATURE [Part::Feature] Face146
  shape: bbox 3.5 x 17.8 x 2e-07 mm, 1 faces, 0 solids (baked)
FEATURE [Part::Revolution] Revolve150  label="removeToCreateScrewAndThreadedInsertHole058"
  Angle = 360
  Axis = (0,1,0)
  Base = (0,0,0)
  FaceMakerClass = Part::FaceMakerBullseye
  Placement = pos=(12.5,0,62) rot=(0,0,1;0rad)
  Solid = false
  Source = -> Face146
  Symmetric = false
FEATURE [Part::Revolution] Revolve151  label="removeToCreateScrewAndThreadedInsertHole059"
  Angle = 360
  Axis = (0,1,0)
  Base = (0,0,0)
  FaceMakerClass = Part::FaceMakerBullseye
  Placement = pos=(89.5,0,68.5) rot=(0,0,1;0rad)
  Solid = false
  Source = -> Face143
  Symmetric = false
FEATURE [Part::Revolution] Revolve152  label="removeToCreateScrewAndThreadedInsertHole060"
  Angle = 360
  Axis = (0,1,0)
  Base = (0,0,0)
  FaceMakerClass = Part::FaceMakerBullseye
  Placement = pos=(89.5,0,3.5) rot=(0,0,1;0rad)
  Solid = false
  Source = -> Face142
  Symmetric = false
FEATURE [Part::Revolution] Revolve153  label="removeToCreateScrewAndThreadedInsertHole061"
  Angle = 360
  Axis = (0,1,0)
  Base = (0,0,0)
  FaceMakerClass = Part::FaceMakerBullseye
  Placement = pos=(109.5,4.7,3.5) rot=(0,0,1;0rad)
  Solid = false
  Source = -> Face145
  Symmetric = false
FEATURE [Part::Revolution] Revolve154  label="removeToCreateScrewAndThreadedInsertHole062"
  Angle = 360
  Axis = (0,1,0)
  Base = (0,0,0)
  FaceMakerClass = Part::FaceMakerBullseye
  Placement = pos=(109.5,4.7,68.5) rot=(0,0,1;0rad)
  Solid = false
  Source = -> Face144
  Symmetric = false
FEATURE [Part::MultiFuse] Fusion115  label="removeToCreateScrewAndThreadedInsertHole056"
  Shapes = -> [Revolve154,Revolve153,Revolve152,Revolve151,Revolve150,Revolve149]
FEATURE [Part::Feature] Face147
  shape: bbox 9.8 x 26.5 x 2e-07 mm, 1 faces, 0 solids (baked)
FEATURE [Part::Revolution] Revolve155
  Angle = 360
  Axis = (0,1,0)
  Base = (0,0,0)
  FaceMakerClass = Part::FaceMakerBullseye
  Placement = pos=(0,0,0) rot=(0,0,1;1.5708rad)
  Solid = false
  Source = -> Face147
  Symmetric = false
FEATURE [Part::Feature] Face148
  shape: bbox 9.8 x 26.5 x 2e-07 mm, 1 faces, 0 solids (baked)
FEATURE [Part::Revolution] Revolve156
  Angle = 360
  Axis = (0,1,0)
  Base = (0,0,0)
  FaceMakerClass = Part::FaceMakerBullseye
  Placement = pos=(0,0,0) rot=(0,0,1;1.5708rad)
  Solid = false
  Source = -> Face148
  Symmetric = false
FEATURE [Part::MultiFuse] Fusion116
  Placement = pos=(-18,19,36) rot=(0,0,1;0rad)
  Shapes = -> [Revolve156,Revolve155]
FEATURE [Part::Box] Box029  label="Cube016"
  AttacherType = Attacher::AttachEngine3D
  Height = 28
  Length = 3
  Placement = pos=(110.7,19,22) rot=(0,0,1;0rad)
  Width = 15.7
FEATURE [Part::Cylinder] Cylinder046
  Angle = 360
  AttacherType = Attacher::AttachEngine3D
  Height = 10
  Placement = pos=(0,0,36.15) rot=(0,0,1;0rad)
  Radius = 4
FEATURE [Part::Cylinder] Cylinder047
  Angle = 360
  AttacherType = Attacher::AttachEngine3D
  Height = 20
  Placement = pos=(0,0,36.15) rot=(0,0,1;0rad)
  Radius = 10.3
FEATURE [Part::MultiFuse] Fusion117  label="removeToCreteHoleForPlugHousing041"
  Placement = pos=(70,19,36) rot=(0,1,0;1.5708rad)
  Shapes = -> [Cylinder047,Cylinder046]
FEATURE [Part::Cut] Cut049  label="plugHousingTab004"
  Base = -> Box029
  Placement = pos=(-107.4,-14,0) rot=(0,0,1;0rad)
  Tool = -> Fusion117
FEATURE [Part::Box] Box030  label="Cube017"
  AttacherType = Attacher::AttachEngine3D
  Height = 28
  Length = 3
  Placement = pos=(110.7,19,22) rot=(0,0,1;0rad)
  Width = 15.7
FEATURE [Part::Cylinder] Cylinder048
  Angle = 360
  AttacherType = Attacher::AttachEngine3D
  Height = 10
  Placement = pos=(0,0,36.15) rot=(0,0,1;0rad)
  Radius = 4
FEATURE [Part::Cylinder] Cylinder049
  Angle = 360
  AttacherType = Attacher::AttachEngine3D
  Height = 20
  Placement = pos=(0,0,36.15) rot=(0,0,1;0rad)
  Radius = 10.3
FEATURE [Part::MultiFuse] Fusion118  label="removeToCreteHoleForPlugHousing042"
  Placement = pos=(70,19,36) rot=(0,1,0;1.5708rad)
  Shapes = -> [Cylinder049,Cylinder048]
FEATURE [Part::Cut] Cut050  label="plugHousingTab005"
  Base = -> Box030
  Placement = pos=(-107.4,-14,0) rot=(0,0,1;0rad)
  Tool = -> Fusion118
FEATURE [Part::MultiFuse] Fusion119
  Placement = pos=(9.6,23,0) rot=(0,0,1;3.14159rad)
  Shapes = -> [Cut049,Cut050]
FEATURE [Part::Box] Box031  label="Cube018"
  AttacherType = Attacher::AttachEngine3D
  Height = 10
  Length = 3
  Placement = pos=(3.3,4,12) rot=(0,0,1;0rad)
  Width = 10
FEATURE [Part::Fillet] Fillet044
  Base = -> Box031
  Edges = 1 edges r=2: [Edge11]
FEATURE [Part::Box] Box032  label="Cube019"
  AttacherType = Attacher::AttachEngine3D
  Height = 10
  Length = 3
  Placement = pos=(3.3,4,50) rot=(0,0,1;0rad)
  Width = 10
FEATURE [Part::Fillet] Fillet045
  Base = -> Box032
  Edges = 1 edges r=2: [Edge12]
FEATURE [Part::Box] Box033  label="Cube020"
  AttacherType = Attacher::AttachEngine3D
  Height = 28
  Length = 4
  Placement = pos=(5,0,22) rot=(0,0,1;0rad)
  Width = 10
FEATURE [Part::Fillet] Fillet046
  Base = -> Box033
  Edges = 1 edges r=1: [Edge7]
FEATURE [Part::Fillet] Fillet047
  Base = -> Fillet046
  Edges = 1 edges r=2: [Edge5]
FEATURE [Part::Fillet] Fillet048
  Base = -> Fillet047
  Edges = 1 edges r=2: [Edge2]
FEATURE [Part::Cylinder] Cylinder050
  Angle = 360
  AttacherType = Attacher::AttachEngine3D
  Height = 20
  Placement = pos=(0,0,36.15) rot=(0,0,1;0rad)
  Radius = 8.2
FEATURE [Part::Cylinder] Cylinder051
  Angle = 360
  AttacherType = Attacher::AttachEngine3D
  Height = 10
  Placement = pos=(0,0,36.15) rot=(0,0,1;0rad)
  Radius = 4
FEATURE [Part::MultiFuse] Fusion120  label="removeToCreteHoleForPlugHousing043"
  Placement = pos=(-42,19,36) rot=(0,1,0;1.5708rad)
  Shapes = -> [Cylinder050,Cylinder051]
FEATURE [Sketcher::SketchObject] Sketch067  label="topSketch018"
  FullyConstrained = true
  sketch-geometry (4):
    g0: LineSegment StartX=16.8446 StartY=31.512 StartZ=0 EndX=16.3251 EndY=34.4666 EndZ=0
    g1: ArcOfCircle CenterX=19 CenterY=19.2524 CenterZ=0 NormalX=0 NormalY=0 NormalZ=1 AngleXU=0 Radius=15.4476 StartAngle=1.74483 EndAngle=2.72717
    g2: ArcOfCircle CenterX=19 CenterY=19.2524 CenterZ=0 NormalX=0 NormalY=0 NormalZ=1 AngleXU=0 Radius=12.4476 StartAngle=1.74483 EndAngle=2.73189
    g3: LineSegment StartX=4.86004 StartY=25.4725 StartZ=0 EndX=7.58253 EndY=24.2107 EndZ=0
  constraints (7):
    c: Block(g0)
    c: Coincident(g1,g0)
    c: Coincident(g2,g0)
    c: Coincident(g3,g1)
    c: Coincident(g3,g2)
    c: Block(g1)
    c: Block(g2)
FEATURE [Part::Extrusion] Extrude058
  Base = -> Sketch067
  Dir = (0,0,1)
  DirMode = 2
  FaceMakerClass = Part::FaceMakerBullseye
  LengthFwd = 10
  LengthRev = 0
  Placement = pos=(0,0,31) rot=(0,0,1;0rad)
  Solid = true
  Symmetric = false
FEATURE [Part::Cut] Cut051
  Base = -> Extrude058
  Tool = -> Fusion120
FEATURE [Part::Fillet] Fillet049
  Base = -> Cut051
  Edges = 1 edges r=2: [Edge1]
FEATURE [Part::Fillet] Fillet050
  Base = -> Fillet049
  Edges = 1 edges r=2.5: [Edge1]
FEATURE [Part::Fillet] Fillet051
  Base = -> Fillet050
  Edges = 1 edges r=2.5: [Edge2]
FEATURE [Part::MultiFuse] Fusion121  label="wireHolder003"
  Shapes = -> [Fusion116,Fillet051]
FEATURE [Part::MultiFuse] Fusion122
  Shapes = -> [Fillet045,Fusion121]
FEATURE [Part::MultiFuse] Fusion123  label="wireHolder004"
  Shapes = -> [Fusion122,Fillet048]
FEATURE [Part::MultiFuse] Fusion124  label="wireHolder005"
  Shapes = -> [Fillet044,Fusion119,Fusion123]
FEATURE [Sketcher::SketchObject] Sketch068  label="topSketch019"
  FullyConstrained = true
  sketch-geometry (6):
    g0: LineSegment StartX=19 StartY=38 StartZ=0 EndX=117 EndY=38 EndZ=0
    g1: ArcOfCircle CenterX=19 CenterY=19 CenterZ=0 NormalX=0 NormalY=0 NormalZ=1 AngleXU=0 Radius=19 StartAngle=1.5708 EndAngle=3.14159
    g2: LineSegment StartX=117 StartY=38 StartZ=0 EndX=117 EndY=19 EndZ=0
    g3: LineSegment StartX=98 StartY=1.0161e-12 StartZ=0 EndX=5.22862e-06 EndY=1.0161e-12 EndZ=0
    g4: LineSegment StartX=5.22862e-06 StartY=19 StartZ=0 EndX=5.22862e-06 EndY=1.0161e-12 EndZ=0
    g5: ArcOfCircle CenterX=98 CenterY=19 CenterZ=0 NormalX=0 NormalY=0 NormalZ=1 AngleXU=0 Radius=19 StartAngle=4.71239 EndAngle=6.28319
  constraints (16):
    c: Horizontal(g0)
    c: Distance(g0) = 98
    c: Coincident(g1,g0)
    c: Block(g1)
    c: Coincident(g2,g0)
    c: Vertical(g2)
    c: Distance(g2) = 19
    c: Horizontal(g3)
    c: Coincident(g4,g1)
    c: Vertical(g4)
    c: Coincident(g3,g4)
    c: Block(g3)
    c: Coincident(g5,g2)
    c: Coincident(g5,g3)
    c: Block(g0)
    c: Block(g5)
FEATURE [Part::Extrusion] Extrude059  label="sideA002"
  Base = -> Sketch068
  Dir = (0,0,1)
  DirMode = 2
  FaceMakerClass = Part::FaceMakerBullseye
  LengthFwd = 3
  LengthRev = 0
  Placement = pos=(0,0,-2.7) rot=(0,0,1;0rad)
  Solid = true
  Symmetric = false
FEATURE [Sketcher::SketchObject] Sketch069  label="topSketch020"
  FullyConstrained = true
  sketch-geometry (6):
    g0: LineSegment StartX=19 StartY=38 StartZ=0 EndX=117 EndY=38 EndZ=0
    g1: ArcOfCircle CenterX=19 CenterY=19 CenterZ=0 NormalX=0 NormalY=0 NormalZ=1 AngleXU=0 Radius=19 StartAngle=1.5708 EndAngle=3.14159
    g2: LineSegment StartX=117 StartY=38 StartZ=0 EndX=117 EndY=19 EndZ=0
    g3: LineSegment StartX=98 StartY=1.0161e-12 StartZ=0 EndX=5.22862e-06 EndY=1.0161e-12 EndZ=0
    g4: LineSegment StartX=5.22862e-06 StartY=19 StartZ=0 EndX=5.22862e-06 EndY=1.0161e-12 EndZ=0
    g5: ArcOfCircle CenterX=98 CenterY=19 CenterZ=0 NormalX=0 NormalY=0 NormalZ=1 AngleXU=0 Radius=19 StartAngle=4.71239 EndAngle=6.28319
  constraints (16):
    c: Horizontal(g0)
    c: Distance(g0) = 98
    c: Coincident(g1,g0)
    c: Block(g1)
    c: Coincident(g2,g0)
    c: Vertical(g2)
    c: Distance(g2) = 19
    c: Horizontal(g3)
    c: Coincident(g4,g1)
    c: Vertical(g4)
    c: Coincident(g3,g4)
    c: Block(g3)
    c: Coincident(g5,g2)
    c: Coincident(g5,g3)
    c: Block(g0)
    c: Block(g5)
FEATURE [Part::Extrusion] Extrude060  label="sideB002"
  Base = -> Sketch069
  Dir = (0,0,1)
  DirMode = 2
  FaceMakerClass = Part::FaceMakerBullseye
  LengthFwd = 3
  LengthRev = 0
  Placement = pos=(0,0,71.7) rot=(0,0,1;0rad)
  Solid = true
  Symmetric = false
FEATURE [Part::MultiFuse] Fusion127  label="removeFromBottom001"
  Placement = pos=(2,0,0) rot=(0,0,1;0rad)
  Shapes = -> [Extrude059,Extrude060]
FEATURE [Part::Cylinder] Cylinder052
  Angle = 360
  AttacherType = Attacher::AttachEngine3D
  Height = 20
  Placement = pos=(0,0,36.15) rot=(0,0,1;0rad)
  Radius = 14
FEATURE [Part::Cylinder] Cylinder053
  Angle = 360
  AttacherType = Attacher::AttachEngine3D
  Height = 10
  Placement = pos=(0,0,36.15) rot=(0,0,1;0rad)
  Radius = 4
FEATURE [Part::MultiFuse] Fusion128  label="removeToCreteHoleForPlugHousing044"
  Placement = pos=(70,19,36) rot=(0,1,0;1.5708rad)
  Shapes = -> [Cylinder052,Cylinder053]
FEATURE [Part::Cut] Cut052  label="bottom011"
  Base = -> Extrude043
  Tool = -> Fusion128
FEATURE [Part::Cut] Cut054  label="bottom012"
  Base = -> Cut052
  Tool = -> Fusion115
FEATURE [Sketcher::SketchObject] Sketch070
  FullyConstrained = true
  Placement = pos=(117,19,0) rot=(0.57735,0.57735,0.57735;2.0944rad)
  sketch-geometry (48):
    g0: LineSegment StartX=-49.19 StartY=69.25 StartZ=0 EndX=-49.19 EndY=66.25 EndZ=0
    g1: LineSegment StartX=-49.19 StartY=63.5 StartZ=0 EndX=-49.19 EndY=60.5 EndZ=0
    g2: LineSegment StartX=-49.19 StartY=57.75 StartZ=0 EndX=-49.19 EndY=54.75 EndZ=0
    g3: LineSegment StartX=-49.19 StartY=52 StartZ=0 EndX=-49.19 EndY=49 EndZ=0
    g4: LineSegment StartX=-49.19 StartY=46.25 StartZ=0 EndX=-49.19 EndY=43.25 EndZ=0
    g5: LineSegment StartX=-49.19 StartY=40.5 StartZ=0 EndX=-49.19 EndY=37.5 EndZ=0
    g6: LineSegment StartX=-49.19 StartY=34.5 StartZ=0 EndX=-49.19 EndY=31.5 EndZ=0
    g7: LineSegment StartX=-49.19 StartY=28.75 StartZ=0 EndX=-49.19 EndY=25.75 EndZ=0
    g8: LineSegment StartX=-49.19 StartY=23 StartZ=0 EndX=-49.19 EndY=20 EndZ=0
    g9: LineSegment StartX=-49.19 StartY=17.25 StartZ=0 EndX=-49.19 EndY=14.25 EndZ=0
    g10: LineSegment StartX=-49.19 StartY=11.5 StartZ=0 EndX=-49.19 EndY=8.5 EndZ=0
    g11: LineSegment StartX=-49.19 StartY=5.75 StartZ=0 EndX=-49.19 EndY=2.75 EndZ=0
    g12: ArcOfCircle CenterX=-1.5 CenterY=67.75 CenterZ=0 NormalX=0 NormalY=0 NormalZ=1 AngleXU=0 Radius=1.5 StartAngle=4.71239 EndAngle=7.85398
    g13: ArcOfCircle CenterX=-1.5 CenterY=62 CenterZ=0 NormalX=0 NormalY=0 NormalZ=1 AngleXU=0 Radius=1.5 StartAngle=4.71239 EndAngle=7.85398
    g14: ArcOfCircle CenterX=-1.5 CenterY=56.25 CenterZ=0 NormalX=0 NormalY=0 NormalZ=1 AngleXU=0 Radius=1.5 StartAngle=4.71239 EndAngle=7.85398
    g15: ArcOfCircle CenterX=-11.49 CenterY=50.5 CenterZ=0 NormalX=0 NormalY=0 NormalZ=1 AngleXU=0 Radius=1.5 StartAngle=4.71239 EndAngle=7.85398
    g16: ArcOfCircle CenterX=-16.28 CenterY=44.75 CenterZ=0 NormalX=0 NormalY=0 NormalZ=1 AngleXU=0 Radius=1.5 StartAngle=4.71239 EndAngle=7.85398
    g17: ArcOfCircle CenterX=-18.2337 CenterY=39 CenterZ=0 NormalX=0 NormalY=0 NormalZ=1 AngleXU=0 Radius=1.5 StartAngle=4.71485 EndAngle=7.85398
    g18: ArcOfCircle CenterX=-16.2837 CenterY=27.25 CenterZ=0 NormalX=0 NormalY=0 NormalZ=1 AngleXU=0 Radius=1.5 StartAngle=4.71485 EndAngle=7.85398
    g19: ArcOfCircle CenterX=-18.2337 CenterY=33 CenterZ=0 NormalX=0 NormalY=0 NormalZ=1 AngleXU=0 Radius=1.5 StartAngle=4.71485 EndAngle=7.85398
    g20: ArcOfCircle CenterX=-11.49 CenterY=21.5 CenterZ=0 NormalX=0 NormalY=0 NormalZ=1 AngleXU=0 Radius=1.5 StartAngle=4.71239 EndAngle=7.85398
    g21: ArcOfCircle CenterX=-1.5 CenterY=4.25 CenterZ=0 NormalX=0 NormalY=0 NormalZ=1 AngleXU=0 Radius=1.5 StartAngle=4.71239 EndAngle=7.85398
    g22: ArcOfCircle CenterX=-1.5 CenterY=10 CenterZ=0 NormalX=0 NormalY=0 NormalZ=1 AngleXU=0 Radius=1.5 StartAngle=4.71239 EndAngle=7.85398
    g23: ArcOfCircle CenterX=-1.5 CenterY=15.75 CenterZ=0 NormalX=0 NormalY=0 NormalZ=1 AngleXU=0 Radius=1.5 StartAngle=4.71239 EndAngle=7.85398
    g24: LineSegment StartX=-49.19 StartY=69.25 StartZ=0 EndX=-1.5 EndY=69.25 EndZ=0
    g25: LineSegment StartX=-49.19 StartY=66.25 StartZ=0 EndX=-1.5 EndY=66.25 EndZ=0
    g26: LineSegment StartX=-49.19 StartY=63.5 StartZ=0 EndX=-1.5 EndY=63.5 EndZ=0
    g27: LineSegment StartX=-49.19 StartY=60.5 StartZ=0 EndX=-1.5 EndY=60.5 EndZ=0
    g28: LineSegment StartX=-49.19 StartY=57.75 StartZ=0 EndX=-1.5 EndY=57.75 EndZ=0
    g29: LineSegment StartX=-49.19 StartY=54.75 StartZ=0 EndX=-1.5 EndY=54.75 EndZ=0
    g30: LineSegment StartX=-49.19 StartY=52 StartZ=0 EndX=-11.49 EndY=52 EndZ=0
    g31: LineSegment StartX=-49.19 StartY=49 StartZ=0 EndX=-11.49 EndY=49 EndZ=0
    g32: LineSegment StartX=-49.19 StartY=46.25 StartZ=0 EndX=-16.28 EndY=46.25 EndZ=0
    g33: LineSegment StartX=-49.19 StartY=43.25 StartZ=0 EndX=-16.28 EndY=43.25 EndZ=0
    g34: LineSegment StartX=-49.19 StartY=40.5 StartZ=0 EndX=-18.2337 EndY=40.5 EndZ=0
    g35: LineSegment StartX=-49.19 StartY=37.5 StartZ=0 EndX=-18.23 EndY=37.5 EndZ=0
    g36: LineSegment StartX=-49.19 StartY=34.5 StartZ=0 EndX=-18.2337 EndY=34.5 EndZ=0
    g37: LineSegment StartX=-49.19 StartY=31.5 StartZ=0 EndX=-18.23 EndY=31.5 EndZ=0
    g38: LineSegment StartX=-49.19 StartY=28.75 StartZ=0 EndX=-16.2837 EndY=28.75 EndZ=0
    g39: LineSegment StartX=-49.19 StartY=25.75 StartZ=0 EndX=-16.28 EndY=25.75 EndZ=0
    g40: LineSegment StartX=-49.19 StartY=23 StartZ=0 EndX=-11.49 EndY=23 EndZ=0
    g41: LineSegment StartX=-49.19 StartY=20 StartZ=0 EndX=-11.49 EndY=20 EndZ=0
    g42: LineSegment StartX=-49.19 StartY=17.25 StartZ=0 EndX=-1.5 EndY=17.25 EndZ=0
    g43: LineSegment StartX=-49.19 StartY=14.25 StartZ=0 EndX=-1.5 EndY=14.25 EndZ=0
    g44: LineSegment StartX=-49.19 StartY=11.5 StartZ=0 EndX=-1.5 EndY=11.5 EndZ=0
    g45: LineSegment StartX=-49.19 StartY=8.5 StartZ=0 EndX=-1.5 EndY=8.5 EndZ=0
    g46: LineSegment StartX=-49.19 StartY=5.75 StartZ=0 EndX=-1.5 EndY=5.75 EndZ=0
    g47: LineSegment StartX=-49.19 StartY=2.75 StartZ=0 EndX=-1.5 EndY=2.75 EndZ=0
  constraints (120):
    c: Vertical(g0)
    c: Distance(g0) = 3
    c: Block(g0)
    c: Vertical(g1)
    c: Distance(g1) = 3
    c: Vertical(g2)
    c: Equal(g0,g2) = 3
    c: Block(g2)
    c: Vertical(g3)
    c: Equal(g1,g3) = 3
    c: Vertical(g4)
    c: Equal(g0,g4) = 3
    c: Block(g4)
    c: Vertical(g5)
    c: Equal(g1,g5) = 3
    c: Vertical(g6)
    c: Equal(g0,g6) = 3
    c: Block(g6)
    c: Vertical(g7)
    c: Equal(g1,g7) = 3
    c: Vertical(g8)
    c: Equal(g0,g8) = 3
    c: Block(g8)
    c: Vertical(g9)
    c: Equal(g1,g9) = 3
    c: Vertical(g10)
    c: Equal(g0,g10) = 3
    c: Block(g10)
    c: Vertical(g11)
    c: Equal(g1,g11) = 3
    c: Block(g12)
    c: Block(g13)
    c: Block(g14)
    c: Block(g15)
    c: Block(g16)
    c: Block(g17)
    c: Block(g18)
    c: Block(g19)
    c: Block(g20)
    c: Block(g21)
    c: Block(g22)
    c: Block(g23)
    c: Block(g11)
    c: Block(g9)
    c: Block(g7)
    c: Block(g5)
    c: Block(g3)
    c: Block(g1)
    c: Coincident(g24,g0)
    c: Coincident(g24,g12)
    c: Horizontal(g24)
    c: Coincident(g25,g0)
    c: Coincident(g25,g12)
    c: Horizontal(g25)
    c: Coincident(g26,g1)
    c: Coincident(g26,g13)
    c: Horizontal(g26)
    c: Coincident(g27,g1)
    c: Coincident(g27,g13)
    c: Horizontal(g27)
    c: Coincident(g28,g2)
    c: Coincident(g28,g14)
    c: Horizontal(g28)
    c: Coincident(g29,g2)
    c: Coincident(g29,g14)
    c: Horizontal(g29)
    c: Coincident(g30,g3)
    c: Coincident(g30,g15)
    c: Horizontal(g30)
    c: Coincident(g31,g3)
    c: Coincident(g31,g15)
    c: Horizontal(g31)
    c: Coincident(g32,g4)
    c: Coincident(g32,g16)
    c: Horizontal(g32)
    c: Coincident(g33,g4)
    c: Coincident(g33,g16)
    c: Horizontal(g33)
    c: Coincident(g34,g5)
    c: Coincident(g34,g17)
    c: Horizontal(g34)
    c: Coincident(g35,g5)
    c: Coincident(g35,g17)
    c: Horizontal(g35)
    c: Coincident(g36,g6)
    c: Coincident(g36,g19)
    c: Horizontal(g36)
    c: Coincident(g37,g6)
    c: Coincident(g37,g19)
    c: Horizontal(g37)
    c: Coincident(g38,g7)
    c: Coincident(g38,g18)
    c: Horizontal(g38)
    c: Coincident(g39,g7)
    c: Coincident(g39,g18)
    c: Horizontal(g39)
    c: Coincident(g40,g8)
    c: Coincident(g40,g20)
    c: Horizontal(g40)
    c: Coincident(g41,g8)
    c: Coincident(g41,g20)
    c: Horizontal(g41)
    c: Coincident(g42,g9)
    c: Coincident(g42,g23)
    c: Horizontal(g42)
    c: Coincident(g43,g9)
    c: Coincident(g43,g23)
    c: Horizontal(g43)
    c: Coincident(g44,g10)
    c: Coincident(g44,g22)
    c: Horizontal(g44)
    c: Coincident(g45,g10)
    c: Coincident(g45,g22)
    c: Horizontal(g45)
    c: Coincident(g46,g11)
    c: Coincident(g46,g21)
    c: Horizontal(g46)
    c: Coincident(g47,g11)
    c: Coincident(g47,g21)
    c: Horizontal(g47)
FEATURE [Part::Extrusion] Extrude061
  Base = -> Sketch070
  Dir = (1,0,0)
  DirMode = 2
  FaceMakerClass = Part::FaceMakerBullseye
  LengthFwd = 23
  LengthRev = 0
  Placement = pos=(-19,0,0) rot=(0,0,1;0rad)
  Solid = true
  Symmetric = false
FEATURE [Part::Fillet] Fillet052  label="removeToCreateVentalationHoles002"
  Base = -> Extrude061
  Edges = <same value as first occurrence — deduplicated (x6 in doc)>
  Placement = pos=(7,0.02,0) rot=(0,0,1;0rad)
FEATURE [Part::MultiFuse] Fusion130  label="bottom013"
  Shapes = -> [Cut054,Cut034]
FEATURE [Part::Cut] Cut055
  Base = -> Fusion130
  Tool = -> Fillet052
FEATURE [Part::Cylinder] Cylinder054
  Angle = 360
  AttacherType = Attacher::AttachEngine3D
  Height = 20
  Placement = pos=(0,0,36.15) rot=(0,0,1;0rad)
  Radius = 4
FEATURE [Sketcher::SketchObject] Sketch071  label="bottomSketch002"
  FullyConstrained = true
  sketch-geometry (32):
    g0: LineSegment StartX=3.3 StartY=-6.03275e-07 StartZ=0 EndX=98 EndY=-6.03275e-07 EndZ=0
    g1: ArcOfCircle CenterX=98 CenterY=19 CenterZ=0 NormalX=0 NormalY=0 NormalZ=1 AngleXU=0 Radius=19 StartAngle=4.71239 EndAngle=5.71103
    g2: LineSegment StartX=6.3 StartY=8 StartZ=0 EndX=3.3 EndY=8 EndZ=0
    g3: LineSegment StartX=3.3 StartY=8 StartZ=0 EndX=3.3 EndY=-6.03275e-07 EndZ=0
    g4: ArcOfCircle CenterX=8.3 CenterY=5 CenterZ=0 NormalX=0 NormalY=0 NormalZ=1 AngleXU=0 Radius=2 StartAngle=3.14159 EndAngle=4.71239
    g5: LineSegment StartX=6.3 StartY=8 StartZ=0 EndX=6.3 EndY=5 EndZ=0
    g6: ArcOfCircle CenterX=98 CenterY=19 CenterZ=0 NormalX=0 NormalY=0 NormalZ=1 AngleXU=0 Radius=12.7 StartAngle=4.71239 EndAngle=6.28319
    g7: LineSegment StartX=94.7 StartY=3 StartZ=0 EndX=8.3 EndY=3 EndZ=0
    g8-g12: Circle x5 (B-spline internal-alignment scaffolding for g13; pole/knot coordinates omitted)
    g13: BSplineCurve PolesCount=5 KnotsCount=3 Degree=3 IsPeriodic=0
    g14: GeomPoint X=98 Y=6.3 Z=0
    g15: GeomPoint X=96.3938 Y=4.71946 Z=0
    g16: GeomPoint X=94.7 Y=3 Z=0
    g17-g23: Circle x7 (B-spline internal-alignment scaffolding for g24; pole/knot coordinates omitted)
    g24: BSplineCurve PolesCount=7 KnotsCount=5 Degree=3 IsPeriodic=0
    g25-g29: GeomPoint x5 (B-spline internal-alignment scaffolding for g24; pole/knot coordinates omitted)
    g30: ArcOfCircle CenterX=98 CenterY=19 CenterZ=0 NormalX=0 NormalY=0 NormalZ=1 AngleXU=0 Radius=15.7 StartAngle=5.81226 EndAngle=6.28319
    g31: LineSegment StartX=110.7 StartY=19 StartZ=0 EndX=113.7 EndY=19 EndZ=0
  constraints (41):
    c: Horizontal(g0)
    c: Coincident(g1,g0)
    c: Block(g1)
    c: Horizontal(g2)
    c: Distance(g2) = 3
    c: Coincident(g3,g2)
    c: Vertical(g3)
    c: Coincident(g3,g0)
    c: Block(g4)
    c: Block(g2)
    c: Coincident(g5,g2)
    c: Coincident(g5,g4)
    c: Vertical(g5)
    c: Coincident(g6,g1)
    c: Block(g6)
    c: Coincident(g7,g4)
    c: Horizontal(g7)
    c: Block(g0)
    c: Block(g7)
    c: Block(g3)
    c: Coincident(g13,g6)
    c: Weight(g8) = 1
    c: Equal(g8, g9-g12) x4
    c: Coincident(g13,g7)
    c: InternalAlignment(g8-g12 -> g13) x5
    c: InternalAlignment(g14,g13)
    c: InternalAlignment(g15,g13)
    c: InternalAlignment(g16,g13)
    c: Block(g13)
    c: Weight(g17) = 1
    c: Equal(g17, g18-g23) x6
    c: Coincident(g24,g1)
    c: InternalAlignment(g17-g23 -> g24) x7
    c: InternalAlignment(g25-g29 -> g24) x5
    c: Block(g24)
    c: Coincident(g30,g24)
    c: Coincident(g31,g6)
    c: Coincident(g31,g30)
    c: Horizontal(g31)
    c: Block(g31)
    c: Block(g30)
FEATURE [Part::Extrusion] Extrude062  label="bottom014"
  Base = -> Sketch071
  Dir = (0,0,1)
  DirMode = 2
  FaceMakerClass = Part::FaceMakerBullseye
  LengthFwd = 71.4
  LengthRev = 0
  Placement = pos=(0,0,0.3) rot=(0,0,1;0rad)
  Solid = true
  Symmetric = false
FEATURE [Part::Fillet] Fillet054
  Base = -> Extrude062
  Edges = 1 edges r=2.4: [Edge17]
FEATURE [Part::Fillet] Fillet055  label="bottom015"
  Base = -> Fillet054
  Edges = 1 edges r=2.4: [Edge36]
FEATURE [Part::Cylinder] Cylinder055
  Angle = 360
  AttacherType = Attacher::AttachEngine3D
  Height = 10
  Placement = pos=(0,0,36.15) rot=(0,0,1;0rad)
  Radius = 4
FEATURE [Part::MultiFuse] Fusion131  label="removeToCreateHoleForPlugHousing002"
  Placement = pos=(70,19,36.15) rot=(0,1,0;1.5708rad)
  Shapes = -> [Cylinder054,Cylinder055]
FEATURE [Part::Cut] Cut056  label="Bottom001"
  Base = -> Fillet055
  Placement = pos=(9,0,0) rot=(0,0,1;0rad)
  Tool = -> Fusion131
FEATURE [Part::Cut] Cut057
  Base = -> Cut055
  Tool = -> Cut056
FEATURE [Sketcher::SketchObject] Sketch072  label="topSketch021"
  FullyConstrained = true
  sketch-geometry (4):
    g0: ArcOfCircle CenterX=105 CenterY=19 CenterZ=0 NormalX=0 NormalY=0 NormalZ=1 AngleXU=0 Radius=20.6155 StartAngle=5.54125 EndAngle=6.28319
    g1: ArcOfCircle CenterX=105 CenterY=19 CenterZ=0 NormalX=0 NormalY=0 NormalZ=1 AngleXU=0 Radius=13 StartAngle=5.54125 EndAngle=6.28319
    g2: LineSegment StartX=118 StartY=19 StartZ=0 EndX=125.616 EndY=19 EndZ=0
    g3: LineSegment StartX=114.583 StartY=10.2157 StartZ=0 EndX=120.197 EndY=5.06982 EndZ=0
  constraints (7):
    c: Block(g0)
    c: Block(g1)
    c: Coincident(g2,g1)
    c: Coincident(g2,g0)
    c: Horizontal(g2)
    c: Coincident(g3,g1)
    c: Coincident(g3,g0)
FEATURE [Part::Extrusion] Extrude063  label="bottomPlugHousingBit003"
  Base = -> Sketch072
  Dir = (0,0,1)
  DirMode = 2
  FaceMakerClass = Part::FaceMakerBullseye
  LengthFwd = 72
  LengthRev = 0
  Solid = true
  Symmetric = false
FEATURE [Part::Cylinder] Cylinder056
  Angle = 360
  AttacherType = Attacher::AttachEngine3D
  Height = 20
  Placement = pos=(0,0,36.15) rot=(0,0,1;0rad)
  Radius = 14.3
FEATURE [Part::Cylinder] Cylinder057
  Angle = 360
  AttacherType = Attacher::AttachEngine3D
  Height = 10
  Placement = pos=(0,0,36.15) rot=(0,0,1;0rad)
  Radius = 4
FEATURE [Part::Box] Box034  label="removeToCreteHoleForPlugHousing047"
  AttacherType = Attacher::AttachEngine3D
  Height = 28.6
  Length = 20
  Placement = pos=(106.15,0,21.7) rot=(0,0,1;0rad)
  Width = 19
FEATURE [Part::Cylinder] Cylinder058
  Angle = 360
  AttacherType = Attacher::AttachEngine3D
  Height = 20
  Placement = pos=(0,0,36.15) rot=(0,0,1;0rad)
  Radius = 14.3
FEATURE [Part::Cylinder] Cylinder059
  Angle = 360
  AttacherType = Attacher::AttachEngine3D
  Height = 10
  Placement = pos=(0,0,36.15) rot=(0,0,1;0rad)
  Radius = 4
FEATURE [Part::MultiFuse] Fusion134  label="removeToCreteHoleForPlugHousing046"
  Placement = pos=(70,19,36) rot=(0,1,0;1.5708rad)
  Shapes = -> [Cylinder058,Cylinder059]
FEATURE [Part::Cylinder] Cylinder060
  Angle = 360
  AttacherType = Attacher::AttachEngine3D
  Height = 20
  Placement = pos=(0,0,36.15) rot=(0,0,1;0rad)
  Radius = 14
FEATURE [Part::Cylinder] Cylinder061
  Angle = 360
  AttacherType = Attacher::AttachEngine3D
  Height = 10
  Placement = pos=(0,0,36.15) rot=(0,0,1;0rad)
  Radius = 4
FEATURE [Part::MultiFuse] Fusion135  label="removeToCreteHoleForPlugHousing048"
  Placement = pos=(70,19,36) rot=(0,1,0;1.5708rad)
  Shapes = -> [Cylinder060,Cylinder061]
FEATURE [Part::Box] Box035  label="removeToCreteHoleForPlugHousing049"
  AttacherType = Attacher::AttachEngine3D
  Height = 28.6
  Length = 20
  Placement = pos=(106.15,0,21.7) rot=(0,0,1;0rad)
  Width = 19
FEATURE [Part::MultiFuse] Fusion133  label="removeToCreteHoleForPlugHousing045"
  Placement = pos=(0,0,-28.3) rot=(0,0,1;0rad)
  Shapes = -> [Box035,Fusion134]
FEATURE [Part::MultiFuse] Fusion138  label="removeToCreteHoleForPlugHousing051"
  Placement = pos=(70,19,36) rot=(0,1,0;1.5708rad)
  Shapes = -> [Cylinder056,Cylinder057]
FEATURE [Part::MultiFuse] Fusion137  label="removeToCreteHoleForPlugHousing050"
  Placement = pos=(0,0,28.3) rot=(0,0,1;0rad)
  Shapes = -> [Box034,Fusion138]
FEATURE [Part::MultiFuse] Fusion132  label="removeToCreatePlugHousingBottomBit002"
  Shapes = -> [Fusion133,Fusion137]
FEATURE [Part::MultiFuse] Fusion136  label="removeToCreatePlugHousingBottomBit003"
  Shapes = -> [Fusion135,Fusion132]
FEATURE [Part::Cut] Cut058  label="bottomPlugHousingBit002"
  Base = -> Extrude063
  Placement = pos=(-0.09,0,0) rot=(0,0,1;0rad)
  Tool = -> Fusion136
FEATURE [Sketcher::SketchObject] Sketch073  label="bottomSketch003"
  FullyConstrained = true
  sketch-geometry (45):
    g0: LineSegment StartX=6.29999 StartY=8 StartZ=0 EndX=3.29999 EndY=8 EndZ=0
    g1: LineSegment StartX=3.29999 StartY=8 StartZ=0 EndX=3.29999 EndY=-6.03275e-07 EndZ=0
    g2: ArcOfCircle CenterX=8.29999 CenterY=5 CenterZ=0 NormalX=0 NormalY=0 NormalZ=1 AngleXU=0 Radius=2 StartAngle=3.14159 EndAngle=4.71239
    g3: LineSegment StartX=6.29999 StartY=8 StartZ=0 EndX=6.29999 EndY=5 EndZ=0
    g4: ArcOfCircle CenterX=105 CenterY=19 CenterZ=0 NormalX=0 NormalY=0 NormalZ=1 AngleXU=0 Radius=12.7 StartAngle=4.71239 EndAngle=5.94289
    g5-g11: Circle x7 (B-spline internal-alignment scaffolding for g12; pole/knot coordinates omitted)
    g12: BSplineCurve PolesCount=7 KnotsCount=5 Degree=3 IsPeriodic=0
    g13-g17: GeomPoint x5 (B-spline internal-alignment scaffolding for g12; pole/knot coordinates omitted)
    g18: ArcOfCircle CenterX=105 CenterY=19 CenterZ=0 NormalX=0 NormalY=0 NormalZ=1 AngleXU=0 Radius=15.7 StartAngle=5.81226 EndAngle=6.28319
    g19: BSplineCurve PolesCount=5 KnotsCount=3 Degree=3 IsPeriodic=0
    g20: LineSegment StartX=8.29999 StartY=3 StartZ=0 EndX=101.7 EndY=3 EndZ=0
    g21: LineSegment StartX=3.29999 StartY=-6.03275e-07 StartZ=0 EndX=105 EndY=-6.03275e-07 EndZ=0
    g22: LineSegment StartX=120.974 StartY=8.71251 StartZ=0 EndX=122.332 EndY=7.83778 EndZ=0
    g23: LineSegment StartX=105 StartY=-6.03274e-07 StartZ=0 EndX=113 EndY=-6.03274e-07 EndZ=0
    g24: ArcOfCircle CenterX=105 CenterY=19 CenterZ=0 NormalX=0 NormalY=0 NormalZ=1 AngleXU=0 Radius=20.6155 StartAngle=5.11091 EndAngle=5.71103
    g25: ArcOfCircle CenterX=117.7 CenterY=19 CenterZ=0 NormalX=0 NormalY=0 NormalZ=1 AngleXU=0 Radius=3 StartAngle=1.2e-15 EndAngle=2.10468
    g26: Circle CenterX=116.345 CenterY=16.3232 CenterZ=0 NormalX=0 NormalY=0 NormalZ=1 AngleXU=0 Radius=1
    g27: Circle CenterX=117.24 CenterY=15.7584 CenterZ=0 NormalX=0 NormalY=0 NormalZ=1 AngleXU=0 Radius=1
    g28: Circle CenterX=116.972 CenterY=14.7612 CenterZ=0 NormalX=0 NormalY=0 NormalZ=1 AngleXU=0 Radius=1
    g29: BSplineCurve PolesCount=3 KnotsCount=2 Degree=2 IsPeriodic=0
    g30: GeomPoint X=116.345 Y=16.3232 Z=0
    g31: GeomPoint X=116.972 Y=14.7612 Z=0
    g32: Circle CenterX=115.828 CenterY=17.157 CenterZ=0 NormalX=0 NormalY=0 NormalZ=1 AngleXU=0 Radius=1
    g33: Circle CenterX=115.841 CenterY=16.639 CenterZ=0 NormalX=0 NormalY=0 NormalZ=1 AngleXU=0 Radius=1
    g34: Circle CenterX=116.345 CenterY=16.3232 CenterZ=0 NormalX=0 NormalY=0 NormalZ=1 AngleXU=0 Radius=1
    g35: BSplineCurve PolesCount=3 KnotsCount=2 Degree=2 IsPeriodic=0
    g36: GeomPoint X=115.828 Y=17.157 Z=0
    g37: GeomPoint X=116.345 Y=16.3232 Z=0
    g38: LineSegment StartX=115.828 StartY=17.157 StartZ=0 EndX=115.828 EndY=20.8307 EndZ=0
    g39: Circle CenterX=115.828 CenterY=20.8307 CenterZ=0 NormalX=0 NormalY=0 NormalZ=1 AngleXU=0 Radius=1
    g40: Circle CenterX=115.831 CenterY=21.3396 CenterZ=0 NormalX=0 NormalY=0 NormalZ=1 AngleXU=0 Radius=1
    g41: Circle CenterX=116.173 CenterY=21.5825 CenterZ=0 NormalX=0 NormalY=0 NormalZ=1 AngleXU=0 Radius=1
    g42: BSplineCurve PolesCount=3 KnotsCount=2 Degree=2 IsPeriodic=0
    g43: GeomPoint X=115.828 Y=20.8307 Z=0
    g44: GeomPoint X=116.173 Y=21.5825 Z=0
  constraints (70):
    c: Horizontal(g0)
    c: Distance(g0) = 3
    c: Coincident(g1,g0)
    c: Vertical(g1)
    c: Block(g2)
    c: Block(g0)
    c: Coincident(g3,g0)
    c: Coincident(g3,g2)
    c: Vertical(g3)
    c: Block(g1)
    c: Block(g4)
    c: Coincident(g19,g4)
    c: Block(g19)
    c: Equal(g5, g6-g11) x6
    c: InternalAlignment(g5-g11 -> g12) x7
    c: InternalAlignment(g13-g17 -> g12) x5
    c: Block(g12)
    c: Coincident(g18,g12)
    c: Block(g18)
    c: Coincident(g20,g2)
    c: Coincident(g20,g19)
    c: Horizontal(g20)
    c: Distance(g20) = 93.4
    c: Coincident(g21,g1)
    c: Horizontal(g21)
    c: Distance(g21) = 101.7
    c: Horizontal(g23)
    c: Distance(g23) = 8
    c: Coincident(g24,g23)
    c: Block(g23)
    c: Coincident(g22,g24)
    c: Block(g24)
    c: Block(g22)
    c: Distance(g22) = 1.61553
    c: Coincident(g25,g18)
    c: Block(g25)
    c: Weight(g26) = 1
    c: Equal(g26,g27)
    c: Equal(g26,g28)
    c: Coincident(g29,g4)
    c: InternalAlignment(g26,g29)
    c: InternalAlignment(g27,g29)
    c: InternalAlignment(g28,g29)
    c: InternalAlignment(g30,g29)
    c: InternalAlignment(g31,g29)
    c: Block(g29)
    c: Weight(g32) = 1
    c: Equal(g32,g33)
    c: Equal(g32,g34)
    c: Coincident(g35,g29)
    c: InternalAlignment(g32,g35)
    c: InternalAlignment(g33,g35)
    c: InternalAlignment(g34,g35)
    c: InternalAlignment(g36,g35)
    c: InternalAlignment(g37,g35)
    c: Block(g35)
    c: Coincident(g38,g35)
    c: Vertical(g38)
    c: Block(g38)
    c: Coincident(g42,g38)
    c: Weight(g39) = 1
    c: Equal(g39,g40)
    c: Equal(g39,g41)
    c: Coincident(g42,g25)
    c: InternalAlignment(g39,g42)
    c: InternalAlignment(g40,g42)
    c: InternalAlignment(g41,g42)
    c: InternalAlignment(g43,g42)
    c: InternalAlignment(g44,g42)
    c: Block(g42)
FEATURE [Part::Extrusion] Extrude064  label="bottom016"
  Base = -> Sketch073
  Dir = (0,0,1)
  DirMode = 2
  FaceMakerClass = Part::FaceMakerBullseye
  LengthFwd = 71.4
  LengthRev = 0
  Placement = pos=(0,0,0.3) rot=(0,0,1;0rad)
  Solid = true
  Symmetric = false
FEATURE [Part::Revolution] Revolve157  label="removeToCreateScrewAndThreadedInsertHole063"
  Angle = 360
  Axis = (0,1,0)
  Base = (0,0,0)
  FaceMakerClass = Part::FaceMakerBullseye
  Placement = pos=(12.5,0,10) rot=(0,0,1;0rad)
  Solid = false
  Source = -> Face141
  Symmetric = false
FEATURE [Sketcher::SketchObject] Sketch074
  FullyConstrained = true
  Placement = pos=(117,19,0) rot=(0.57735,0.57735,0.57735;2.0944rad)
  sketch-geometry (48):
    g0: LineSegment StartX=-49.19 StartY=69.25 StartZ=0 EndX=-49.19 EndY=66.25 EndZ=0
    g1: LineSegment StartX=-49.19 StartY=63.5 StartZ=0 EndX=-49.19 EndY=60.5 EndZ=0
    g2: LineSegment StartX=-49.19 StartY=57.75 StartZ=0 EndX=-49.19 EndY=54.75 EndZ=0
    g3: LineSegment StartX=-49.19 StartY=52 StartZ=0 EndX=-49.19 EndY=49 EndZ=0
    g4: LineSegment StartX=-49.19 StartY=46.25 StartZ=0 EndX=-49.19 EndY=43.25 EndZ=0
    g5: LineSegment StartX=-49.19 StartY=40.5 StartZ=0 EndX=-49.19 EndY=37.5 EndZ=0
    g6: LineSegment StartX=-49.19 StartY=34.5 StartZ=0 EndX=-49.19 EndY=31.5 EndZ=0
    g7: LineSegment StartX=-49.19 StartY=28.75 StartZ=0 EndX=-49.19 EndY=25.75 EndZ=0
    g8: LineSegment StartX=-49.19 StartY=23 StartZ=0 EndX=-49.19 EndY=20 EndZ=0
    g9: LineSegment StartX=-49.19 StartY=17.25 StartZ=0 EndX=-49.19 EndY=14.25 EndZ=0
    g10: LineSegment StartX=-49.19 StartY=11.5 StartZ=0 EndX=-49.19 EndY=8.5 EndZ=0
    g11: LineSegment StartX=-49.19 StartY=5.75 StartZ=0 EndX=-49.19 EndY=2.75 EndZ=0
    g12: ArcOfCircle CenterX=-1.5 CenterY=67.75 CenterZ=0 NormalX=0 NormalY=0 NormalZ=1 AngleXU=0 Radius=1.5 StartAngle=4.71239 EndAngle=7.85398
    g13: ArcOfCircle CenterX=-1.5 CenterY=62 CenterZ=0 NormalX=0 NormalY=0 NormalZ=1 AngleXU=0 Radius=1.5 StartAngle=4.71239 EndAngle=7.85398
    g14: ArcOfCircle CenterX=-1.5 CenterY=56.25 CenterZ=0 NormalX=0 NormalY=0 NormalZ=1 AngleXU=0 Radius=1.5 StartAngle=4.71239 EndAngle=7.85398
    g15: ArcOfCircle CenterX=-11.49 CenterY=50.5 CenterZ=0 NormalX=0 NormalY=0 NormalZ=1 AngleXU=0 Radius=1.5 StartAngle=4.71239 EndAngle=7.85398
    g16: ArcOfCircle CenterX=-16.28 CenterY=44.75 CenterZ=0 NormalX=0 NormalY=0 NormalZ=1 AngleXU=0 Radius=1.5 StartAngle=4.71239 EndAngle=7.85398
    g17: ArcOfCircle CenterX=-18.2337 CenterY=39 CenterZ=0 NormalX=0 NormalY=0 NormalZ=1 AngleXU=0 Radius=1.5 StartAngle=4.71485 EndAngle=7.85398
    g18: ArcOfCircle CenterX=-16.2837 CenterY=27.25 CenterZ=0 NormalX=0 NormalY=0 NormalZ=1 AngleXU=0 Radius=1.5 StartAngle=4.71485 EndAngle=7.85398
    g19: ArcOfCircle CenterX=-18.2337 CenterY=33 CenterZ=0 NormalX=0 NormalY=0 NormalZ=1 AngleXU=0 Radius=1.5 StartAngle=4.71485 EndAngle=7.85398
    g20: ArcOfCircle CenterX=-11.49 CenterY=21.5 CenterZ=0 NormalX=0 NormalY=0 NormalZ=1 AngleXU=0 Radius=1.5 StartAngle=4.71239 EndAngle=7.85398
    g21: ArcOfCircle CenterX=-1.5 CenterY=4.25 CenterZ=0 NormalX=0 NormalY=0 NormalZ=1 AngleXU=0 Radius=1.5 StartAngle=4.71239 EndAngle=7.85398
    g22: ArcOfCircle CenterX=-1.5 CenterY=10 CenterZ=0 NormalX=0 NormalY=0 NormalZ=1 AngleXU=0 Radius=1.5 StartAngle=4.71239 EndAngle=7.85398
    g23: ArcOfCircle CenterX=-1.5 CenterY=15.75 CenterZ=0 NormalX=0 NormalY=0 NormalZ=1 AngleXU=0 Radius=1.5 StartAngle=4.71239 EndAngle=7.85398
    g24: LineSegment StartX=-49.19 StartY=69.25 StartZ=0 EndX=-1.5 EndY=69.25 EndZ=0
    g25: LineSegment StartX=-49.19 StartY=66.25 StartZ=0 EndX=-1.5 EndY=66.25 EndZ=0
    g26: LineSegment StartX=-49.19 StartY=63.5 StartZ=0 EndX=-1.5 EndY=63.5 EndZ=0
    g27: LineSegment StartX=-49.19 StartY=60.5 StartZ=0 EndX=-1.5 EndY=60.5 EndZ=0
    g28: LineSegment StartX=-49.19 StartY=57.75 StartZ=0 EndX=-1.5 EndY=57.75 EndZ=0
    g29: LineSegment StartX=-49.19 StartY=54.75 StartZ=0 EndX=-1.5 EndY=54.75 EndZ=0
    g30: LineSegment StartX=-49.19 StartY=52 StartZ=0 EndX=-11.49 EndY=52 EndZ=0
    g31: LineSegment StartX=-49.19 StartY=49 StartZ=0 EndX=-11.49 EndY=49 EndZ=0
    g32: LineSegment StartX=-49.19 StartY=46.25 StartZ=0 EndX=-16.28 EndY=46.25 EndZ=0
    g33: LineSegment StartX=-49.19 StartY=43.25 StartZ=0 EndX=-16.28 EndY=43.25 EndZ=0
    g34: LineSegment StartX=-49.19 StartY=40.5 StartZ=0 EndX=-18.2337 EndY=40.5 EndZ=0
    g35: LineSegment StartX=-49.19 StartY=37.5 StartZ=0 EndX=-18.23 EndY=37.5 EndZ=0
    g36: LineSegment StartX=-49.19 StartY=34.5 StartZ=0 EndX=-18.2337 EndY=34.5 EndZ=0
    g37: LineSegment StartX=-49.19 StartY=31.5 StartZ=0 EndX=-18.23 EndY=31.5 EndZ=0
    g38: LineSegment StartX=-49.19 StartY=28.75 StartZ=0 EndX=-16.2837 EndY=28.75 EndZ=0
    g39: LineSegment StartX=-49.19 StartY=25.75 StartZ=0 EndX=-16.28 EndY=25.75 EndZ=0
    g40: LineSegment StartX=-49.19 StartY=23 StartZ=0 EndX=-11.49 EndY=23 EndZ=0
    g41: LineSegment StartX=-49.19 StartY=20 StartZ=0 EndX=-11.49 EndY=20 EndZ=0
    g42: LineSegment StartX=-49.19 StartY=17.25 StartZ=0 EndX=-1.5 EndY=17.25 EndZ=0
    g43: LineSegment StartX=-49.19 StartY=14.25 StartZ=0 EndX=-1.5 EndY=14.25 EndZ=0
    g44: LineSegment StartX=-49.19 StartY=11.5 StartZ=0 EndX=-1.5 EndY=11.5 EndZ=0
    g45: LineSegment StartX=-49.19 StartY=8.5 StartZ=0 EndX=-1.5 EndY=8.5 EndZ=0
    g46: LineSegment StartX=-49.19 StartY=5.75 StartZ=0 EndX=-1.5 EndY=5.75 EndZ=0
    g47: LineSegment StartX=-49.19 StartY=2.75 StartZ=0 EndX=-1.5 EndY=2.75 EndZ=0
  constraints (120):
    c: Vertical(g0)
    c: Distance(g0) = 3
    c: Block(g0)
    c: Vertical(g1)
    c: Distance(g1) = 3
    c: Vertical(g2)
    c: Equal(g0,g2) = 3
    c: Block(g2)
    c: Vertical(g3)
    c: Equal(g1,g3) = 3
    c: Vertical(g4)
    c: Equal(g0,g4) = 3
    c: Block(g4)
    c: Vertical(g5)
    c: Equal(g1,g5) = 3
    c: Vertical(g6)
    c: Equal(g0,g6) = 3
    c: Block(g6)
    c: Vertical(g7)
    c: Equal(g1,g7) = 3
    c: Vertical(g8)
    c: Equal(g0,g8) = 3
    c: Block(g8)
    c: Vertical(g9)
    c: Equal(g1,g9) = 3
    c: Vertical(g10)
    c: Equal(g0,g10) = 3
    c: Block(g10)
    c: Vertical(g11)
    c: Equal(g1,g11) = 3
    c: Block(g12)
    c: Block(g13)
    c: Block(g14)
    c: Block(g15)
    c: Block(g16)
    c: Block(g17)
    c: Block(g18)
    c: Block(g19)
    c: Block(g20)
    c: Block(g21)
    c: Block(g22)
    c: Block(g23)
    c: Block(g11)
    c: Block(g9)
    c: Block(g7)
    c: Block(g5)
    c: Block(g3)
    c: Block(g1)
    c: Coincident(g24,g0)
    c: Coincident(g24,g12)
    c: Horizontal(g24)
    c: Coincident(g25,g0)
    c: Coincident(g25,g12)
    c: Horizontal(g25)
    c: Coincident(g26,g1)
    c: Coincident(g26,g13)
    c: Horizontal(g26)
    c: Coincident(g27,g1)
    c: Coincident(g27,g13)
    c: Horizontal(g27)
    c: Coincident(g28,g2)
    c: Coincident(g28,g14)
    c: Horizontal(g28)
    c: Coincident(g29,g2)
    c: Coincident(g29,g14)
    c: Horizontal(g29)
    c: Coincident(g30,g3)
    c: Coincident(g30,g15)
    c: Horizontal(g30)
    c: Coincident(g31,g3)
    c: Coincident(g31,g15)
    c: Horizontal(g31)
    c: Coincident(g32,g4)
    c: Coincident(g32,g16)
    c: Horizontal(g32)
    c: Coincident(g33,g4)
    c: Coincident(g33,g16)
    c: Horizontal(g33)
    c: Coincident(g34,g5)
    c: Coincident(g34,g17)
    c: Horizontal(g34)
    c: Coincident(g35,g5)
    c: Coincident(g35,g17)
    c: Horizontal(g35)
    c: Coincident(g36,g6)
    c: Coincident(g36,g19)
    c: Horizontal(g36)
    c: Coincident(g37,g6)
    c: Coincident(g37,g19)
    c: Horizontal(g37)
    c: Coincident(g38,g7)
    c: Coincident(g38,g18)
    c: Horizontal(g38)
    c: Coincident(g39,g7)
    c: Coincident(g39,g18)
    c: Horizontal(g39)
    c: Coincident(g40,g8)
    c: Coincident(g40,g20)
    c: Horizontal(g40)
    c: Coincident(g41,g8)
    c: Coincident(g41,g20)
    c: Horizontal(g41)
    c: Coincident(g42,g9)
    c: Coincident(g42,g23)
    c: Horizontal(g42)
    c: Coincident(g43,g9)
    c: Coincident(g43,g23)
    c: Horizontal(g43)
    c: Coincident(g44,g10)
    c: Coincident(g44,g22)
    c: Horizontal(g44)
    c: Coincident(g45,g10)
    c: Coincident(g45,g22)
    c: Horizontal(g45)
    c: Coincident(g46,g11)
    c: Coincident(g46,g21)
    c: Horizontal(g46)
    c: Coincident(g47,g11)
    c: Coincident(g47,g21)
    c: Horizontal(g47)
FEATURE [Part::Extrusion] Extrude065
  Base = -> Sketch074
  Dir = (1,0,0)
  DirMode = 2
  FaceMakerClass = Part::FaceMakerBullseye
  LengthFwd = 23
  LengthRev = 0
  Placement = pos=(-19,0,0) rot=(0,0,1;0rad)
  Solid = true
  Symmetric = false
FEATURE [Part::Fillet] Fillet056  label="removeToCreateVentalationHoles003"
  Base = -> Extrude065
  Edges = <same value as first occurrence — deduplicated (x6 in doc)>
  Placement = pos=(7,0.02,0) rot=(0,0,1;0rad)
FEATURE [Part::Revolution] Revolve158  label="removeToCreateScrewAndThreadedInsertHole065"
  Angle = 360
  Axis = (0,1,0)
  Base = (0,0,0)
  FaceMakerClass = Part::FaceMakerBullseye
  Placement = pos=(12.5,0,62) rot=(0,0,1;0rad)
  Solid = false
  Source = -> Face146
  Symmetric = false
FEATURE [Part::Revolution] Revolve159  label="removeToCreateScrewAndThreadedInsertHole066"
  Angle = 360
  Axis = (0,1,0)
  Base = (0,0,0)
  FaceMakerClass = Part::FaceMakerBullseye
  Placement = pos=(89.5,0,68.5) rot=(0,0,1;0rad)
  Solid = false
  Source = -> Face143
  Symmetric = false
FEATURE [Part::Revolution] Revolve160  label="removeToCreateScrewAndThreadedInsertHole067"
  Angle = 360
  Axis = (0,1,0)
  Base = (0,0,0)
  FaceMakerClass = Part::FaceMakerBullseye
  Placement = pos=(89.5,0,3.5) rot=(0,0,1;0rad)
  Solid = false
  Source = -> Face142
  Symmetric = false
FEATURE [Part::Revolution] Revolve161  label="removeToCreateScrewAndThreadedInsertHole068"
  Angle = 360
  Axis = (0,1,0)
  Base = (0,0,0)
  FaceMakerClass = Part::FaceMakerBullseye
  Placement = pos=(109.5,4.7,3.5) rot=(0,0,1;0rad)
  Solid = false
  Source = -> Face145
  Symmetric = false
FEATURE [Part::Revolution] Revolve162  label="removeToCreateScrewAndThreadedInsertHole069"
  Angle = 360
  Axis = (0,1,0)
  Base = (0,0,0)
  FaceMakerClass = Part::FaceMakerBullseye
  Placement = pos=(109.5,4.7,68.5) rot=(0,0,1;0rad)
  Solid = false
  Source = -> Face144
  Symmetric = false
FEATURE [Part::MultiFuse] Fusion141  label="removeToCreateScrewAndThreadedInsertHole064"
  Shapes = -> [Revolve162,Revolve161,Revolve160,Revolve159,Revolve158,Revolve157]
FEATURE [Part::Cylinder] Cylinder062
  Angle = 360
  AttacherType = Attacher::AttachEngine3D
  Height = 20
  Placement = pos=(0,0,36.15) rot=(0,0,1;0rad)
  Radius = 14
FEATURE [Part::Cylinder] Cylinder063
  Angle = 360
  AttacherType = Attacher::AttachEngine3D
  Height = 10
  Placement = pos=(0,0,36.15) rot=(0,0,1;0rad)
  Radius = 4
FEATURE [Part::MultiFuse] Fusion139  label="removeToCreteHoleForPlugHousing052"
  Placement = pos=(70,19,36) rot=(0,1,0;1.5708rad)
  Shapes = -> [Cylinder062,Cylinder063]
FEATURE [Part::Cut] Cut060  label="bottom017"
  Base = -> Extrude064
  Tool = -> Fusion139
FEATURE [Part::Cut] Cut061  label="bottom019"
  Base = -> Cut060
  Tool = -> Fusion141
FEATURE [Part::MultiFuse] Fusion140  label="bottom018"
  Shapes = -> [Cut061,Cut058]
FEATURE [Part::Cut] Cut059  label="bottom020"
  Base = -> Fusion140
  Tool = -> Fillet056
FEATURE [Part::Box] Box036  label="Cube021"
  AttacherType = Attacher::AttachEngine3D
  Height = 80
  Length = 26
  Placement = pos=(0,-1,-5) rot=(0,0,1;0rad)
  Width = 11
FEATURE [Part::Cut] Cut062  label="removeFromBottom002"
  Base = -> Cut057
  Tool = -> Box036
FEATURE [Part::Cut] Cut063
  Base = -> Cut059
  Tool = -> Cut062
FEATURE [Part::Cut] Cut064  label="pcbStands"
  Base = -> Fusion095
  Tool = -> Fusion127
FEATURE [Sketcher::SketchObject] Sketch075  label="topSketch022"
  FullyConstrained = true
  sketch-geometry (6):
    g0: LineSegment StartX=19 StartY=38 StartZ=0 EndX=117 EndY=38 EndZ=0
    g1: ArcOfCircle CenterX=19 CenterY=19 CenterZ=0 NormalX=0 NormalY=0 NormalZ=1 AngleXU=0 Radius=19 StartAngle=1.5708 EndAngle=3.14159
    g2: LineSegment StartX=117 StartY=38 StartZ=0 EndX=117 EndY=19 EndZ=0
    g3: LineSegment StartX=98 StartY=1.0161e-12 StartZ=0 EndX=5.22862e-06 EndY=1.0161e-12 EndZ=0
    g4: LineSegment StartX=5.22862e-06 StartY=19 StartZ=0 EndX=5.22862e-06 EndY=1.0161e-12 EndZ=0
    g5: ArcOfCircle CenterX=98 CenterY=19 CenterZ=0 NormalX=0 NormalY=0 NormalZ=1 AngleXU=0 Radius=19 StartAngle=4.71239 EndAngle=6.28319
  constraints (16):
    c: Horizontal(g0)
    c: Distance(g0) = 98
    c: Coincident(g1,g0)
    c: Block(g1)
    c: Coincident(g2,g0)
    c: Vertical(g2)
    c: Distance(g2) = 19
    c: Horizontal(g3)
    c: Coincident(g4,g1)
    c: Vertical(g4)
    c: Coincident(g3,g4)
    c: Block(g3)
    c: Coincident(g5,g2)
    c: Coincident(g5,g3)
    c: Block(g0)
    c: Block(g5)
FEATURE [Part::Extrusion] Extrude067  label="sideB003"
  Base = -> Sketch075
  Dir = (0,0,1)
  DirMode = 2
  FaceMakerClass = Part::FaceMakerBullseye
  LengthFwd = 3
  LengthRev = 0
  Placement = pos=(0,0,71.7) rot=(0,0,1;0rad)
  Solid = true
  Symmetric = false
FEATURE [Sketcher::SketchObject] Sketch076  label="topSketch023"
  FullyConstrained = true
  sketch-geometry (6):
    g0: LineSegment StartX=19 StartY=38 StartZ=0 EndX=117 EndY=38 EndZ=0
    g1: ArcOfCircle CenterX=19 CenterY=19 CenterZ=0 NormalX=0 NormalY=0 NormalZ=1 AngleXU=0 Radius=19 StartAngle=1.5708 EndAngle=3.14159
    g2: LineSegment StartX=117 StartY=38 StartZ=0 EndX=117 EndY=19 EndZ=0
    g3: LineSegment StartX=98 StartY=1.0161e-12 StartZ=0 EndX=5.22862e-06 EndY=1.0161e-12 EndZ=0
    g4: LineSegment StartX=5.22862e-06 StartY=19 StartZ=0 EndX=5.22862e-06 EndY=1.0161e-12 EndZ=0
    g5: ArcOfCircle CenterX=98 CenterY=19 CenterZ=0 NormalX=0 NormalY=0 NormalZ=1 AngleXU=0 Radius=19 StartAngle=4.71239 EndAngle=6.28319
  constraints (16):
    c: Horizontal(g0)
    c: Distance(g0) = 98
    c: Coincident(g1,g0)
    c: Block(g1)
    c: Coincident(g2,g0)
    c: Vertical(g2)
    c: Distance(g2) = 19
    c: Horizontal(g3)
    c: Coincident(g4,g1)
    c: Vertical(g4)
    c: Coincident(g3,g4)
    c: Block(g3)
    c: Coincident(g5,g2)
    c: Coincident(g5,g3)
    c: Block(g0)
    c: Block(g5)
FEATURE [Part::Extrusion] Extrude066  label="sideA003"
  Base = -> Sketch076
  Dir = (0,0,1)
  DirMode = 2
  FaceMakerClass = Part::FaceMakerBullseye
  LengthFwd = 3
  LengthRev = 0
  Placement = pos=(0,0,-2.7) rot=(0,0,1;0rad)
  Solid = true
  Symmetric = false
FEATURE [Part::MultiFuse] Fusion142  label="removeFromBottom003"
  Placement = pos=(2,0,0) rot=(0,0,1;0rad)
  Shapes = -> [Extrude066,Extrude067]
FEATURE [Part::Cut] Cut065  label="screwRetainers002"
  Base = -> Fusion096
  Tool = -> Fusion142
FEATURE [Sketcher::SketchObject] Sketch077
  FullyConstrained = true
  Placement = pos=(117,19,0) rot=(0.57735,0.57735,0.57735;2.0944rad)
  sketch-geometry (8):
    g0: LineSegment StartX=-49.19 StartY=63.5 StartZ=0 EndX=-49.19 EndY=60.5 EndZ=0
    g1: LineSegment StartX=-49.19 StartY=11.5 StartZ=0 EndX=-49.19 EndY=8.5 EndZ=0
    g2: ArcOfCircle CenterX=-1.5 CenterY=62 CenterZ=0 NormalX=0 NormalY=0 NormalZ=1 AngleXU=0 Radius=1.5 StartAngle=4.71239 EndAngle=7.85398
    g3: ArcOfCircle CenterX=-1.5 CenterY=10 CenterZ=0 NormalX=0 NormalY=0 NormalZ=1 AngleXU=0 Radius=1.5 StartAngle=4.71239 EndAngle=7.85398
    g4: LineSegment StartX=-49.19 StartY=63.5 StartZ=0 EndX=-1.5 EndY=63.5 EndZ=0
    g5: LineSegment StartX=-49.19 StartY=60.5 StartZ=0 EndX=-1.5 EndY=60.5 EndZ=0
    g6: LineSegment StartX=-49.19 StartY=11.5 StartZ=0 EndX=-1.5 EndY=11.5 EndZ=0
    g7: LineSegment StartX=-49.19 StartY=8.5 StartZ=0 EndX=-1.5 EndY=8.5 EndZ=0
  constraints (19):
    c: Vertical(g0)
    c: Distance(g0) = 3
    c: Vertical(g1)
    c: Block(g1)
    c: Block(g2)
    c: Block(g3)
    c: Block(g0)
    c: Coincident(g4,g0)
    c: Coincident(g4,g2)
    c: Horizontal(g4)
    c: Coincident(g5,g0)
    c: Coincident(g5,g2)
    c: Horizontal(g5)
    c: Coincident(g6,g1)
    c: Coincident(g6,g3)
    c: Horizontal(g6)
    c: Coincident(g7,g1)
    c: Coincident(g7,g3)
    c: Horizontal(g7)
FEATURE [Part::Extrusion] Extrude068
  Base = -> Sketch077
  Dir = (1,0,0)
  DirMode = 2
  FaceMakerClass = Part::FaceMakerBullseye
  LengthFwd = 10
  LengthRev = 0
  Solid = true
  Symmetric = false
FEATURE [Part::Fillet] Fillet057  label="removeFromtMoreFrontCaseScrewRetainers002"
  Base = -> Extrude068
  Edges = 4 edges r=1.49: [Edge6,Edge11,Edge18,Edge23]
  Placement = pos=(-12,0,0) rot=(0,0,1;0rad)
FEATURE [Sketcher::SketchObject] Sketch078
  FullyConstrained = true
  Placement = pos=(117,19,0) rot=(0.57735,0.57735,0.57735;2.0944rad)
  sketch-geometry (8):
    g0: LineSegment StartX=-49.19 StartY=69.25 StartZ=0 EndX=-49.19 EndY=66.25 EndZ=0
    g1: LineSegment StartX=-49.19 StartY=5.75 StartZ=0 EndX=-49.19 EndY=2.75 EndZ=0
    g2: ArcOfCircle CenterX=-1.5 CenterY=67.75 CenterZ=0 NormalX=0 NormalY=0 NormalZ=1 AngleXU=0 Radius=1.5 StartAngle=4.71239 EndAngle=7.85398
    g3: ArcOfCircle CenterX=-1.5 CenterY=4.25 CenterZ=0 NormalX=0 NormalY=0 NormalZ=1 AngleXU=0 Radius=1.5 StartAngle=4.71239 EndAngle=7.85398
    g4: LineSegment StartX=-49.19 StartY=69.25 StartZ=0 EndX=-1.5 EndY=69.25 EndZ=0
    g5: LineSegment StartX=-49.19 StartY=66.25 StartZ=0 EndX=-1.5 EndY=66.25 EndZ=0
    g6: LineSegment StartX=-49.19 StartY=5.75 StartZ=0 EndX=-1.5 EndY=5.75 EndZ=0
    g7: LineSegment StartX=-49.19 StartY=2.75 StartZ=0 EndX=-1.5 EndY=2.75 EndZ=0
  constraints (19):
    c: Vertical(g0)
    c: Distance(g0) = 3
    c: Block(g0)
    c: Vertical(g1)
    c: Block(g2)
    c: Block(g3)
    c: Block(g1)
    c: Coincident(g4,g0)
    c: Coincident(g4,g2)
    c: Horizontal(g4)
    c: Coincident(g5,g0)
    c: Coincident(g5,g2)
    c: Horizontal(g5)
    c: Coincident(g6,g1)
    c: Coincident(g6,g3)
    c: Horizontal(g6)
    c: Coincident(g7,g1)
    c: Coincident(g7,g3)
    c: Horizontal(g7)
FEATURE [Part::Extrusion] Extrude069
  Base = -> Sketch078
  Dir = (1,0,0)
  DirMode = 2
  FaceMakerClass = Part::FaceMakerBullseye
  LengthFwd = 10
  LengthRev = 0
  Solid = true
  Symmetric = false
FEATURE [Part::Fillet] Fillet058  label="removeFromtMoreFrontCaseScrewRetainers003"
  Base = -> Extrude069
  Edges = 4 edges r=1.49: [Edge6,Edge11,Edge18,Edge23]
  Placement = pos=(-4,0,0) rot=(0,0,1;0rad)
FEATURE [Part::Cut] Cut066
  Base = -> Cut065
  Tool = -> Fillet058
FEATURE [Part::Cut] Cut067  label="screwPillars"
  Base = -> Cut066
  Tool = -> Fillet057
FEATURE [Part::MultiFuse] Fusion143  label="bottom021"
  Shapes = -> [Cut031,Cut063]
FEATURE [Part::Cylinder] Cylinder
  Angle = 360
  AttacherType = Attacher::AttachEngine3D
  Height = 10
  Placement = pos=(20.65,12,4.68) rot=(1,0,0;1.5708rad)
  Radius = 2
FEATURE [Part::Cylinder] Cylinder064
  Angle = 360
  AttacherType = Attacher::AttachEngine3D
  Height = 10
  Placement = pos=(20.65,12,67.38) rot=(1,0,0;1.5708rad)
  Radius = 2
FEATURE [Part::Cylinder] Cylinder065
  Angle = 360
  AttacherType = Attacher::AttachEngine3D
  Height = 10
  Placement = pos=(77.15,12,67.38) rot=(1,0,0;1.5708rad)
  Radius = 2
FEATURE [Part::Cylinder] Cylinder066
  Angle = 360
  AttacherType = Attacher::AttachEngine3D
  Height = 10
  Placement = pos=(77.15,12,4.68) rot=(1,0,0;1.5708rad)
  Radius = 2
FEATURE [Part::MultiFuse] Fusion144  label="removeFromThreadedInsertHousing"
  Shapes = -> [Cylinder065,Cylinder064,Cylinder,Cylinder066]
FEATURE [Part::Cut] Cut068  label="pcbStands001"
  Base = -> Cut064
  Tool = -> Fusion144
FEATURE [Part::MultiFuse] Fusion145
  Shapes = -> [Cut068,Fusion143]
FEATURE [Part::MultiFuse] Fusion146
  Shapes = -> [Fusion145]
FEATURE [Part::MultiFuse] Fusion147  label="bottom022"
  Shapes = -> [Cut067,Fusion146]
FEATURE [Part::MultiFuse] Fusion148  label="casePillars005"
  Shapes = -> [Cut047,Fusion092]
FEATURE [Part::MultiFuse] Fusion149  label="bottom023"
  Shapes = -> [Fusion124,Fusion113,Fusion147]
FEATURE [Part::MultiFuse] Fusion150  label="topBits"
  Shapes = -> [Cut025,Fusion148,Cut030,Fillet034]
FEATURE [Part::Feature] Face149 .. Face152  x4 (patterned run collapsed; names and placements below)
  shape: bbox 3.2 x 1.5 x 2e-07 mm, 1 faces, 0 solids (baked)
FEATURE [Part::Feature] Face153
  shape: bbox 3.6 x 3.2 x 2e-07 mm, 1 faces, 0 solids (baked)
FEATURE [Part::Feature] Face154
  shape: bbox 3.6 x 3.2 x 2e-07 mm, 1 faces, 0 solids (baked)
FEATURE [Sketcher::SketchObject] Sketch079  label="topSketch024"
  FullyConstrained = true
  sketch-geometry (6):
    g0: LineSegment StartX=19 StartY=38 StartZ=0 EndX=117 EndY=38 EndZ=0
    g1: ArcOfCircle CenterX=19 CenterY=19 CenterZ=0 NormalX=0 NormalY=0 NormalZ=1 AngleXU=0 Radius=19 StartAngle=1.5708 EndAngle=3.14159
    g2: LineSegment StartX=117 StartY=38 StartZ=0 EndX=117 EndY=19 EndZ=0
    g3: LineSegment StartX=98 StartY=1.0161e-12 StartZ=0 EndX=5.22862e-06 EndY=1.0161e-12 EndZ=0
    g4: LineSegment StartX=5.22862e-06 StartY=19 StartZ=0 EndX=5.22862e-06 EndY=1.0161e-12 EndZ=0
    g5: ArcOfCircle CenterX=98 CenterY=19 CenterZ=0 NormalX=0 NormalY=0 NormalZ=1 AngleXU=0 Radius=19 StartAngle=4.71239 EndAngle=6.28319
  constraints (16):
    c: Horizontal(g0)
    c: Distance(g0) = 98
    c: Coincident(g1,g0)
    c: Block(g1)
    c: Coincident(g2,g0)
    c: Vertical(g2)
    c: Distance(g2) = 19
    c: Horizontal(g3)
    c: Coincident(g4,g1)
    c: Vertical(g4)
    c: Coincident(g3,g4)
    c: Block(g3)
    c: Coincident(g5,g2)
    c: Coincident(g5,g3)
    c: Block(g0)
    c: Block(g5)
FEATURE [Sketcher::SketchObject] Sketch080  label="topSketch025"
  FullyConstrained = true
  sketch-geometry (6):
    g0: LineSegment StartX=19 StartY=38 StartZ=0 EndX=117 EndY=38 EndZ=0
    g1: ArcOfCircle CenterX=19 CenterY=19 CenterZ=0 NormalX=0 NormalY=0 NormalZ=1 AngleXU=0 Radius=19 StartAngle=1.5708 EndAngle=3.14159
    g2: LineSegment StartX=117 StartY=38 StartZ=0 EndX=117 EndY=19 EndZ=0
    g3: LineSegment StartX=98 StartY=1.0161e-12 StartZ=0 EndX=5.22862e-06 EndY=1.0161e-12 EndZ=0
    g4: LineSegment StartX=5.22862e-06 StartY=19 StartZ=0 EndX=5.22862e-06 EndY=1.0161e-12 EndZ=0
    g5: ArcOfCircle CenterX=98 CenterY=19 CenterZ=0 NormalX=0 NormalY=0 NormalZ=1 AngleXU=0 Radius=19 StartAngle=4.71239 EndAngle=6.28319
  constraints (16):
    c: Horizontal(g0)
    c: Distance(g0) = 98
    c: Coincident(g1,g0)
    c: Block(g1)
    c: Coincident(g2,g0)
    c: Vertical(g2)
    c: Distance(g2) = 19
    c: Horizontal(g3)
    c: Coincident(g4,g1)
    c: Vertical(g4)
    c: Coincident(g3,g4)
    c: Block(g3)
    c: Coincident(g5,g2)
    c: Coincident(g5,g3)
    c: Block(g0)
    c: Block(g5)
FEATURE [Part::Extrusion] Extrude070  label="sideA004"
  Base = -> Sketch080
  Dir = (0,0,1)
  DirMode = 2
  FaceMakerClass = Part::FaceMakerBullseye
  LengthFwd = 3
  LengthRev = 0
  Placement = pos=(0,0,-2.7) rot=(0,0,1;0rad)
  Solid = true
  Symmetric = false
FEATURE [Sketcher::SketchObject] Sketch081
  FullyConstrained = true
  Placement = pos=(117,19,0) rot=(0.57735,0.57735,0.57735;2.0944rad)
  sketch-geometry (8):
    g0: LineSegment StartX=-49.19 StartY=63.5 StartZ=0 EndX=-49.19 EndY=60.5 EndZ=0
    g1: LineSegment StartX=-49.19 StartY=11.5 StartZ=0 EndX=-49.19 EndY=8.5 EndZ=0
    g2: ArcOfCircle CenterX=-1.5 CenterY=62 CenterZ=0 NormalX=0 NormalY=0 NormalZ=1 AngleXU=0 Radius=1.5 StartAngle=4.71239 EndAngle=7.85398
    g3: ArcOfCircle CenterX=-1.5 CenterY=10 CenterZ=0 NormalX=0 NormalY=0 NormalZ=1 AngleXU=0 Radius=1.5 StartAngle=4.71239 EndAngle=7.85398
    g4: LineSegment StartX=-49.19 StartY=63.5 StartZ=0 EndX=-1.5 EndY=63.5 EndZ=0
    g5: LineSegment StartX=-49.19 StartY=60.5 StartZ=0 EndX=-1.5 EndY=60.5 EndZ=0
    g6: LineSegment StartX=-49.19 StartY=11.5 StartZ=0 EndX=-1.5 EndY=11.5 EndZ=0
    g7: LineSegment StartX=-49.19 StartY=8.5 StartZ=0 EndX=-1.5 EndY=8.5 EndZ=0
  constraints (19):
    c: Vertical(g0)
    c: Distance(g0) = 3
    c: Vertical(g1)
    c: Block(g1)
    c: Block(g2)
    c: Block(g3)
    c: Block(g0)
    c: Coincident(g4,g0)
    c: Coincident(g4,g2)
    c: Horizontal(g4)
    c: Coincident(g5,g0)
    c: Coincident(g5,g2)
    c: Horizontal(g5)
    c: Coincident(g6,g1)
    c: Coincident(g6,g3)
    c: Horizontal(g6)
    c: Coincident(g7,g1)
    c: Coincident(g7,g3)
    c: Horizontal(g7)
FEATURE [Part::Extrusion] Extrude071  label="sideB004"
  Base = -> Sketch079
  Dir = (0,0,1)
  DirMode = 2
  FaceMakerClass = Part::FaceMakerBullseye
  LengthFwd = 3
  LengthRev = 0
  Placement = pos=(0,0,71.7) rot=(0,0,1;0rad)
  Solid = true
  Symmetric = false
FEATURE [Part::MultiFuse] Fusion152  label="removeFromBottom004"
  Placement = pos=(2,0,0) rot=(0,0,1;0rad)
  Shapes = -> [Extrude070,Extrude071]
FEATURE [Part::Extrusion] Extrude072
  Base = -> Sketch081
  Dir = (1,0,0)
  DirMode = 2
  FaceMakerClass = Part::FaceMakerBullseye
  LengthFwd = 10
  LengthRev = 0
  Solid = true
  Symmetric = false
FEATURE [Part::Fillet] Fillet059  label="removeFromtMoreFrontCaseScrewRetainers004"
  Base = -> Extrude072
  Edges = 4 edges r=1.49: [Edge6,Edge11,Edge18,Edge23]
  Placement = pos=(-12,0,0) rot=(0,0,1;0rad)
FEATURE [Sketcher::SketchObject] Sketch082
  FullyConstrained = true
  Placement = pos=(117,19,0) rot=(0.57735,0.57735,0.57735;2.0944rad)
  sketch-geometry (8):
    g0: LineSegment StartX=-49.19 StartY=69.25 StartZ=0 EndX=-49.19 EndY=66.25 EndZ=0
    g1: LineSegment StartX=-49.19 StartY=5.75 StartZ=0 EndX=-49.19 EndY=2.75 EndZ=0
    g2: ArcOfCircle CenterX=-1.5 CenterY=67.75 CenterZ=0 NormalX=0 NormalY=0 NormalZ=1 AngleXU=0 Radius=1.5 StartAngle=4.71239 EndAngle=7.85398
    g3: ArcOfCircle CenterX=-1.5 CenterY=4.25 CenterZ=0 NormalX=0 NormalY=0 NormalZ=1 AngleXU=0 Radius=1.5 StartAngle=4.71239 EndAngle=7.85398
    g4: LineSegment StartX=-49.19 StartY=69.25 StartZ=0 EndX=-1.5 EndY=69.25 EndZ=0
    g5: LineSegment StartX=-49.19 StartY=66.25 StartZ=0 EndX=-1.5 EndY=66.25 EndZ=0
    g6: LineSegment StartX=-49.19 StartY=5.75 StartZ=0 EndX=-1.5 EndY=5.75 EndZ=0
    g7: LineSegment StartX=-49.19 StartY=2.75 StartZ=0 EndX=-1.5 EndY=2.75 EndZ=0
  constraints (19):
    c: Vertical(g0)
    c: Distance(g0) = 3
    c: Block(g0)
    c: Vertical(g1)
    c: Block(g2)
    c: Block(g3)
    c: Block(g1)
    c: Coincident(g4,g0)
    c: Coincident(g4,g2)
    c: Horizontal(g4)
    c: Coincident(g5,g0)
    c: Coincident(g5,g2)
    c: Horizontal(g5)
    c: Coincident(g6,g1)
    c: Coincident(g6,g3)
    c: Horizontal(g6)
    c: Coincident(g7,g1)
    c: Coincident(g7,g3)
    c: Horizontal(g7)
FEATURE [Part::Extrusion] Extrude073
  Base = -> Sketch082
  Dir = (1,0,0)
  DirMode = 2
  FaceMakerClass = Part::FaceMakerBullseye
  LengthFwd = 10
  LengthRev = 0
  Solid = true
  Symmetric = false
FEATURE [Part::Fillet] Fillet060  label="removeFromtMoreFrontCaseScrewRetainers005"
  Base = -> Extrude073
  Edges = 4 edges r=1.49: [Edge6,Edge11,Edge18,Edge23]
  Placement = pos=(-4,0,0) rot=(0,0,1;0rad)
FEATURE [Part::Revolution] Revolve163  label="backCaseScrewRetainer004"
  Angle = 360
  Axis = (0,1,0)
  Base = (0,0,0)
  FaceMakerClass = Part::FaceMakerBullseye
  Placement = pos=(12.5,3,62) rot=(0,0,1;0rad)
  Solid = false
  Source = -> Face149
  Symmetric = false
FEATURE [Part::Revolution] Revolve164  label="frontCaseScrewRetainer006"
  Angle = 360
  Axis = (0,1,0)
  Base = (0,0,0)
  FaceMakerClass = Part::FaceMakerBullseye
  Placement = pos=(89.5,3,68.5) rot=(0,0,1;0rad)
  Solid = false
  Source = -> Face151
  Symmetric = false
FEATURE [Part::Revolution] Revolve165  label="frontCaseScrewRetainer007"
  Angle = 360
  Axis = (0,1,0)
  Base = (0,0,0)
  FaceMakerClass = Part::FaceMakerBullseye
  Placement = pos=(89.5,3,3.5) rot=(0,0,1;0rad)
  Solid = false
  Source = -> Face152
  Symmetric = false
FEATURE [Part::Revolution] Revolve166  label="backCaseScrewRetainer005"
  Angle = 360
  Axis = (0,1,0)
  Base = (0,0,0)
  FaceMakerClass = Part::FaceMakerBullseye
  Placement = pos=(12.5,3,10) rot=(0,0,1;0rad)
  Solid = false
  Source = -> Face150
  Symmetric = false
FEATURE [Part::Revolution] Revolve167  label="moreFrontCaseScrewRetainer006"
  Angle = 360
  Axis = (0,1,0)
  Base = (0,0,0)
  FaceMakerClass = Part::FaceMakerBullseye
  Placement = pos=(109.5,4.5,68.5) rot=(0,0,1;0rad)
  Solid = false
  Source = -> Face153
  Symmetric = false
FEATURE [Part::Revolution] Revolve168  label="moreFrontCaseScrewRetainer007"
  Angle = 360
  Axis = (0,1,0)
  Base = (0,0,0)
  FaceMakerClass = Part::FaceMakerBullseye
  Placement = pos=(109.5,4.5,3.5) rot=(0,0,1;0rad)
  Solid = false
  Source = -> Face154
  Symmetric = false
FEATURE [Part::MultiFuse] Fusion151  label="screwRetainers003"
  Shapes = -> [Revolve168,Revolve167,Revolve166,Revolve165,Revolve164,Revolve163]
FEATURE [Part::Cut] Cut069  label="screwRetainers004"
  Base = -> Fusion151
  Tool = -> Fusion152
FEATURE [Part::Cut] Cut070
  Base = -> Cut069
  Tool = -> Fillet060
FEATURE [Part::Cut] Cut071  label="screwPillars001"
  Base = -> Cut070
  Tool = -> Fillet059
FEATURE [Part::MultiFuse] Fusion153  label="bottom024"
  Shapes = -> [Fusion149,Cut071]
FEATURE [Part::Cylinder] Cylinder067
  Angle = 360
  AttacherType = Attacher::AttachEngine3D
  Height = 10
  Placement = pos=(20.65,12,4.68) rot=(1,0,0;1.5708rad)
  Radius = 2
FEATURE [Part::Cylinder] Cylinder068
  Angle = 360
  AttacherType = Attacher::AttachEngine3D
  Height = 10
  Placement = pos=(20.65,12,67.38) rot=(1,0,0;1.5708rad)
  Radius = 2
FEATURE [Part::Cylinder] Cylinder069
  Angle = 360
  AttacherType = Attacher::AttachEngine3D
  Height = 10
  Placement = pos=(77.15,12,67.38) rot=(1,0,0;1.5708rad)
  Radius = 2
FEATURE [Part::Cylinder] Cylinder070
  Angle = 360
  AttacherType = Attacher::AttachEngine3D
  Height = 10
  Placement = pos=(77.15,12,4.68) rot=(1,0,0;1.5708rad)
  Radius = 2
FEATURE [Part::MultiFuse] Fusion154  label="removeFromThreadedInsertHousing001"
  Shapes = -> [Cylinder069,Cylinder068,Cylinder067,Cylinder070]
FEATURE [Part::Cut] Cut072  label="bottom025"
  Base = -> Fusion153
  Tool = -> Fusion154
FEATURE [Image::ImagePlane] ImagePlane
  XSize = 339
  YSize = 72
FEATURE [Sketcher::SketchObject] Sketch083
  FullyConstrained = false
  MapMode = 5
  Support = -> [XY_Plane]
  sketch-geometry (98):
    g0: LineSegment StartX=-151.619 StartY=28.8932 StartZ=0 EndX=-140.819 EndY=28.8932 EndZ=0
    g1: LineSegment StartX=-151.619 StartY=24.0313 StartZ=0 EndX=-151.619 EndY=28.8932 EndZ=0
    g2: LineSegment StartX=-140.819 StartY=17.7713 StartZ=0 EndX=-151.619 EndY=17.7713 EndZ=0
    g3: LineSegment StartX=-151.619 StartY=17.7713 StartZ=0 EndX=-151.619 EndY=22.6313 EndZ=0
    g4: LineSegment StartX=-151.619 StartY=22.6313 StartZ=0 EndX=-145.128 EndY=22.6313 EndZ=0
    g5: LineSegment StartX=-145.128 StartY=24.0313 StartZ=0 EndX=-140.819 EndY=28.8932 EndZ=0
    g6: LineSegment StartX=-145.128 StartY=22.6313 StartZ=0 EndX=-140.819 EndY=17.7713 EndZ=0
    g7: ArcOfCircle CenterX=-155.157 CenterY=23.3323 CenterZ=0 NormalX=0 NormalY=0 NormalZ=1 AngleXU=0 Radius=6.92354 StartAngle=1.03434 EndAngle=5.24885
    g8: ArcOfCircle CenterX=-155.157 CenterY=23.3323 CenterZ=0 NormalX=0 NormalY=0 NormalZ=1 AngleXU=0 Radius=12.6269 StartAngle=1.28675 EndAngle=4.99643
    g9: LineSegment StartX=-151.619 StartY=35.4532 StartZ=0 EndX=-151.619 EndY=29.2832 EndZ=0
    g10: LineSegment StartX=-151.619 StartY=17.3813 StartZ=0 EndX=-151.619 EndY=11.2113 EndZ=0
    g11-g21: Circle x11 (B-spline internal-alignment scaffolding for g22; pole/knot coordinates omitted)
    g22: BSplineCurve PolesCount=11 KnotsCount=9 Degree=3 IsPeriodic=0
    g23-g31: GeomPoint x9 (B-spline internal-alignment scaffolding for g22; pole/knot coordinates omitted)
    g32-g49: Circle x18 (B-spline internal-alignment scaffolding for g50; pole/knot coordinates omitted)
    g50: BSplineCurve PolesCount=18 KnotsCount=16 Degree=3 IsPeriodic=0
    g51-g66: GeomPoint x16 (B-spline internal-alignment scaffolding for g50; pole/knot coordinates omitted)
    g67: LineSegment StartX=-117.124 StartY=30.093 StartZ=0 EndX=-117.603 EndY=26.5272 EndZ=0
    g68: LineSegment StartX=-117.603 StartY=17.8472 StartZ=0 EndX=-117.124 EndY=14.2659 EndZ=0
    g69: Ellipse CenterX=-109.671 CenterY=20.025 CenterZ=0 NormalX=0 NormalY=0 NormalZ=1 MajorRadius=3.34798 MinorRadius=2.71052 AngleXU=-1.56793
    g70: GeomPoint X=-109.666 Y=18.0598 Z=0
    g71: GeomPoint X=-109.677 Y=21.9902 Z=0
    g72: Ellipse CenterX=-109.671 CenterY=20.0123 CenterZ=0 NormalX=0 NormalY=0 NormalZ=1 MajorRadius=6.93002 MinorRadius=6.36273 AngleXU=-3.13976
    g73: GeomPoint X=-112.417 Y=20.0073 Z=0
    g74: GeomPoint X=-106.925 Y=20.0173 Z=0
    g75: Ellipse CenterX=-51.7682 CenterY=20.1463 CenterZ=0 NormalX=0 NormalY=0 NormalZ=1 MajorRadius=3.19279 MinorRadius=2.71052 AngleXU=-1.52774
    g76: GeomPoint X=-51.6955 Y=18.4606 Z=0
    g77: GeomPoint X=-51.8408 Y=21.832 Z=0
    g78: GeomPoint X=-54.5142 Y=20.1413 Z=0
    g79: GeomPoint X=-49.0221 Y=20.1513 Z=0
    g80: Ellipse CenterX=-51.7682 CenterY=20.1463 CenterZ=0 NormalX=0 NormalY=0 NormalZ=1 MajorRadius=6.93002 MinorRadius=6.36273 AngleXU=-3.13976
    g81: Ellipse CenterX=-22.8436 CenterY=20.1783 CenterZ=0 NormalX=0 NormalY=0 NormalZ=1 MajorRadius=3.31512 MinorRadius=2.71052 AngleXU=-1.60214
    g82: GeomPoint X=-22.9034 Y=18.2706 Z=0
    g83: GeomPoint X=-22.7838 Y=22.0861 Z=0
    g84: GeomPoint X=-25.5897 Y=20.1733 Z=0
    g85: GeomPoint X=-20.0976 Y=20.1833 Z=0
    g86: Ellipse CenterX=-22.8436 CenterY=20.1783 CenterZ=0 NormalX=0 NormalY=0 NormalZ=1 MajorRadius=6.93002 MinorRadius=6.36273 AngleXU=-3.13976
    g87: LineSegment StartX=-101.889 StartY=14.1107 StartZ=0 EndX=-97.7455 EndY=14.1107 EndZ=0
    g88: LineSegment StartX=-93.8155 StartY=14.1107 StartZ=0 EndX=-89.6755 EndY=14.1107 EndZ=0
    g89: LineSegment StartX=-85.7455 StartY=14.1107 StartZ=0 EndX=-81.6055 EndY=14.1107 EndZ=0
    g90: LineSegment StartX=-101.889 StartY=14.1107 StartZ=0 EndX=-101.889 EndY=25.9907 EndZ=0
    g91: LineSegment StartX=-101.889 StartY=25.9907 StartZ=0 EndX=-97.8594 EndY=25.9907 EndZ=0
    g92: LineSegment StartX=-97.8594 StartY=25.9907 StartZ=0 EndX=-97.8594 EndY=24.0907 EndZ=0
    g93: LineSegment StartX=-97.8594 StartY=24.0907 StartZ=0 EndX=-89.9494 EndY=24.0907 EndZ=0
    g94: LineSegment StartX=-97.7455 StartY=14.1107 StartZ=0 EndX=-97.7455 EndY=19.9107 EndZ=0
    g95: LineSegment StartX=-89.6755 StartY=14.1107 StartZ=0 EndX=-89.6755 EndY=19.9107 EndZ=0
    g96: LineSegment StartX=-85.7455 StartY=14.1107 StartZ=0 EndX=-85.7455 EndY=21.0107 EndZ=0
    g97: LineSegment StartX=-93.8155 StartY=14.1107 StartZ=0 EndX=-93.8155 EndY=21.0107 EndZ=0
  constraints (90):
    c: Coincident(g1,g0)
    c: Horizontal(g0)
    c: Vertical(g1)
    c: Coincident(g2,g3)
    c: Coincident(g3,g4)
    c: Horizontal(g4)
    c: Horizontal(g2)
    c: Vertical(g3)
    c: Block(g1)
    c: Distance(g3) = 4.86
    c: Block(g4)
    c: Distance(g0) = 10.8
    c: Distance(g2) = 10.8
    c: Coincident(g5,g0)
    c: Coincident(g6,g4)
    c: Coincident(g6,g2)
    c: Block(g8)
    c: Block(g7)
    c: Coincident(g9,g8)
    c: Coincident(g9,g7)
    c: Vertical(g9)
    c: Coincident(g10,g7)
    c: Coincident(g10,g8)
    c: Vertical(g10)
    c: Weight(g11) = 1
    c: Equal(g11, g12-g21) x10
    c: InternalAlignment(g11-g21 -> g22) x11
    c: InternalAlignment(g23-g31 -> g22) x9
    c: Block(g22)
    c: Weight(g32) = 1
    c: Equal(g32, g33-g49) x17
    c: InternalAlignment(g32-g49 -> g50) x18
    c: InternalAlignment(g51-g66 -> g50) x16
    c: Block(g50)
    c: Coincident(g67,g50)
    c: Coincident(g67,g22)
    c: Coincident(g68,g22)
    c: Coincident(g68,g50)
    c: InternalAlignment(g70,g69)
    c: InternalAlignment(g71,g69)
    c: Block(g69)
    c: InternalAlignment(g73,g72)
    c: InternalAlignment(g74,g72)
    c: Block(g72)
    c: InternalAlignment(g76,g75)
    c: InternalAlignment(g77,g75)
    c: InternalAlignment(g78,g80)
    c: InternalAlignment(g79,g80)
    c: Block(g80)
    c: Coincident(g75,g80)
    c: Block(g75)
    c: InternalAlignment(g82,g81)
    c: InternalAlignment(g83,g81)
    c: InternalAlignment(g84,g86)
    c: InternalAlignment(g85,g86)
    c: Block(g86)
    c: Coincident(g81,g86)
    c: Block(g81)
    c: Horizontal(g87)
    c: Block(g87)
    c: Horizontal(g88)
    c: Distance(g88) = 4.14
    c: Horizontal(g89)
    c: Equal(g88,g89) = 4.14
    c: Block(g89)
    c: Block(g88)
    c: Coincident(g90,g87)
    c: Vertical(g90)
    c: Distance(g90) = 11.88
    c: Coincident(g91,g90)
    c: Horizontal(g91)
    c: Coincident(g92,g91)
    c: Vertical(g92)
    c: Distance(g91) = 4.03
    c: Distance(g92) = 1.9
    c: Coincident(g93,g92)
    c: Horizontal(g93)
    c: Coincident(g94,g87)
    c: Vertical(g94)
    c: Vertical(g95)
    c: Coincident(g95,g88)
    c: Distance(g94) = 5.8
    c: Distance(g95) = 5.8
    c: Distance(g93) = 7.91
    c: Coincident(g96,g89)
    c: Vertical(g96)
    c: Vertical(g97)
    c: Coincident(g97,g88)
    c: Distance(g97) = 6.9
    c: Distance(g96) = 6.9
FEATURE [PartDesign::Body] Body
  Group = -> [Sketch083]
  Origin = -> Origin
FEATURE [Sketcher::SketchObject] Sketch084
  FullyConstrained = true
  MapMode = 5
  Support = -> [XY_Plane001]
FEATURE [PartDesign::Body] Body001
  Group = -> [Sketch084]
  Origin = -> Origin001
